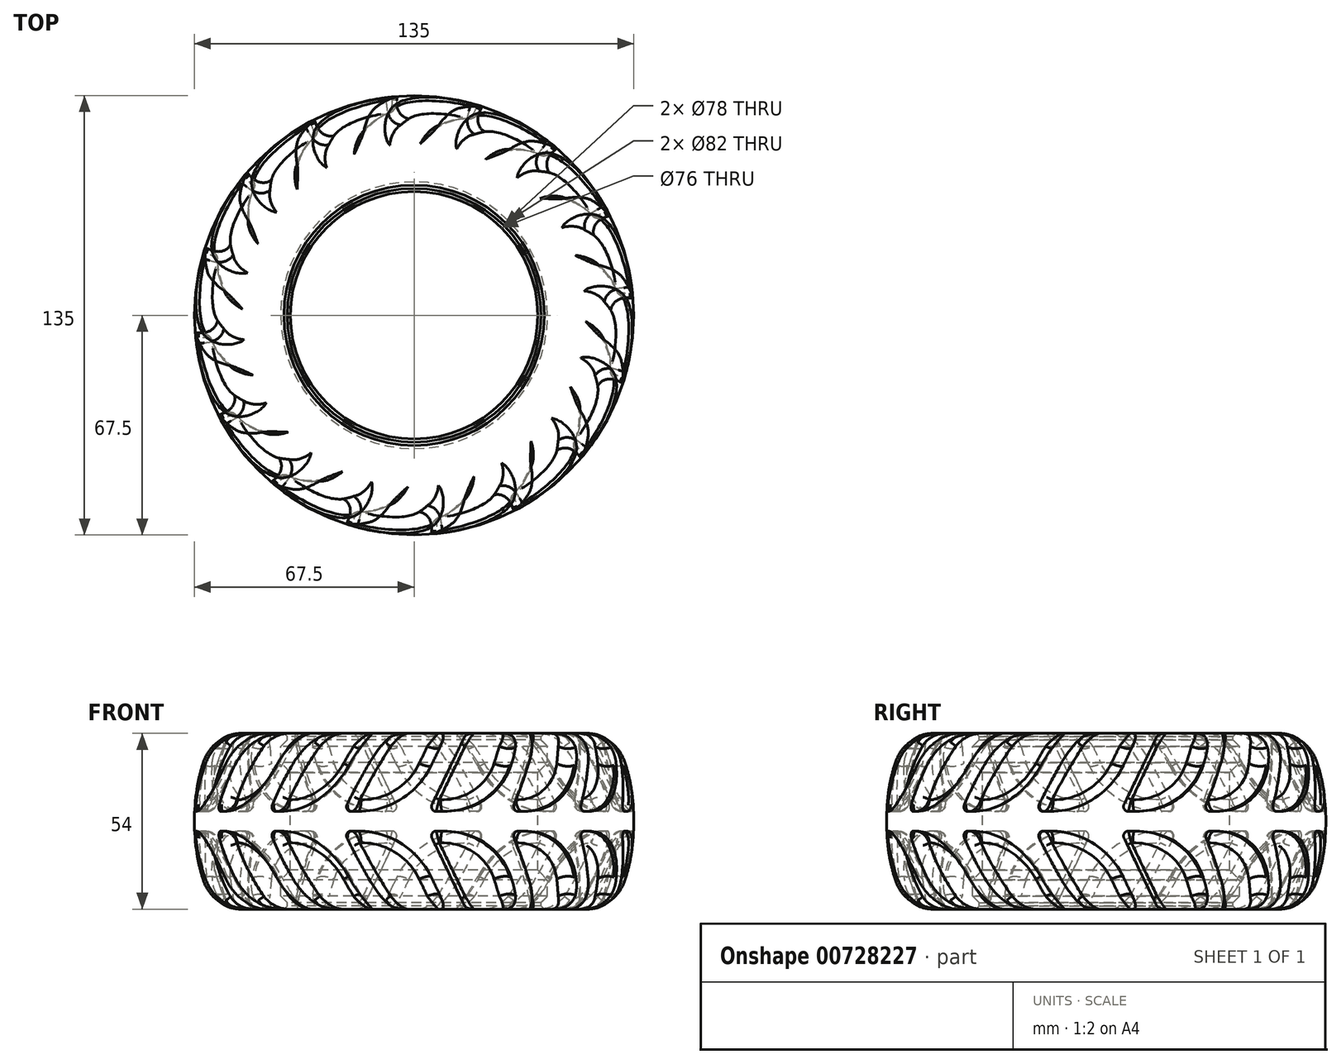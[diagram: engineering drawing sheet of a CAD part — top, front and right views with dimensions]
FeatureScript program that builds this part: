
annotation { "Feature Type Name" : "Feature", "Feature Type Description" : "" }
export const myFeature = defineFeature(function(context is Context, id is Id, definition is map)
    precondition{}
    {
        {
            var Q0;
            Q0=qCreatedBy(makeId("Front.planeOp"),FACE);
            var sketch = newSketch(context, id + "F0", { "sketchPlane" : qUnion([Q0])});
            skLineSegment(sketch, "E0", {"start": v(-39, 25) * mm, "end": v(-39, 27) * mm});
            skLineSegment(sketch, "E1", {"start": v(-39, 25) * mm, "end": v(-41, 23) * mm});
            skLineSegment(sketch, "E2", {"start": v(-41, 23) * mm, "end": v(-41, 18) * mm});
            skLineSegment(sketch, "E3", {"start": v(-41, 18) * mm, "end": v(-38, 15) * mm});
            skLineSegment(sketch, "E4", {"start": v(-38, -15) * mm, "end": v(-41, -18) * mm});
            skLineSegment(sketch, "E5", {"start": v(-41, -18) * mm, "end": v(-41, -23) * mm});
            skLineSegment(sketch, "E6", {"start": v(-41, -23) * mm, "end": v(-39, -25) * mm});
            skLineSegment(sketch, "E7", {"start": v(-39, -25) * mm, "end": v(-39, -27) * mm});
            skLineSegment(sketch, "E8", {"start": v(-38, 15) * mm, "end": v(-38, -15) * mm});
            skLineSegment(sketch, "E9", {"start": v(-38, 0) * mm, "end": v(-62.9, 0) * mm, "construction": true});
            skCircle(sketch, "E10", {"center": v(-52.82, 20.75) * mm, "radius": 6.25 * mm});
            skCircle(sketch, "E11", {"center": v(0, 0) * mm, "radius": 69 * mm});
            skCircle(sketch, "E12", {"center": v(-52.82, -20.75) * mm, "radius": 6.25 * mm});
            skCircle(sketch, "E13", {"center": v(0, 0) * mm, "radius": 63 * mm});
            skLineSegment(sketch, "E14", {"start": v(-39, 27) * mm, "end": v(-52.82, 27) * mm});
            skLineSegment(sketch, "E15", {"start": v(-39, -27) * mm, "end": v(-52.82, -27) * mm});
            skLineSegment(sketch, "E16", {"start": v(0, 89.19) * mm, "end": v(0, -93.9) * mm, "construction": true});
            skCircle(sketch, "E17", {"center": v(-52.82, 20.75) * mm, "radius": 12.25 * mm});
            skSolve(sketch);
        }
        {
            var Q0;
            Q0=makeQuery(id+"F0.imprint","IMPRINT",FACE,{"disambiguationData":[TD([[makeQuery(id+"F0.imprint","IMPRINT",EDGE,{"derivedFrom":sQuery(id+"F0.wireOp",EDGE,"E0")}),1.0]])]});
            var Q1;
            {var subQ0=sQuery(id+"F0.wireOp",EDGE,"E10");var subQ1=makeQuery(id+"F0.imprint","INTERSECT",VERTEX,{"derivedFrom":[subQ0,sQuery(id+"F0.wireOp",EDGE,"E14")]});Q1=makeQuery(id+"F0.imprint","IMPRINT",FACE,{"disambiguationData":[TD([[makeQuery(id+"F0.imprint","IMPRINT",EDGE,{"disambiguationData":[TD([[subQ1,-1.0]])],"derivedFrom":subQ0}),1.0]])]});}
            var Q2;
            {var subQ0=sQuery(id+"F0.wireOp",EDGE,"E12");var subQ1=makeQuery(id+"F0.imprint","INTERSECT",VERTEX,{"derivedFrom":[subQ0,sQuery(id+"F0.wireOp",EDGE,"E15")]});Q2=makeQuery(id+"F0.imprint","IMPRINT",FACE,{"disambiguationData":[TD([[makeQuery(id+"F0.imprint","IMPRINT",EDGE,{"disambiguationData":[TD([[subQ1,1.0]])],"derivedFrom":subQ0}),1.0]])]});}
            var Q3;
            {var subQ6=sQuery(id+"F0.wireOp",EDGE,"E2");Q3=makeQuery(id+"F0.imprint","IMPRINT",FACE,{"disambiguationData":[TD([[makeQuery(id+"F0.imprint","IMPRINT",EDGE,{"derivedFrom":subQ6}),-1.0]])]});}
            var Q4;
            Q4=makeQuery(id+"F0.imprint","IMPRINT",FACE,{"disambiguationData":[TD([[makeQuery(id+"F0.imprint","IMPRINT",EDGE,{"derivedFrom":sQuery(id+"F0.wireOp",EDGE,"E4")}),-1.0]])]});
            var Q5;
            Q5=sQuery(id+"F0.wireOp",EDGE,"E16");
            revolve(context, id + "F1", {"entities" : qUnion([Q0, Q1, Q2, Q3, Q4]), "axis" : qUnion([Q5]), "revolveType" : RevolveType.FULL});
        }
        {
            var Q0;
            Q0=qCreatedBy(makeId("Top.planeOp"),FACE);
            cPlane(context, id + "F2", {"entities" : qUnion([Q0]), "cplaneType" : CPlaneType.OFFSET, "offset" : 27 * mm, "width" : 150 * mm, "height" : 150 * mm});
        }
        {
            var Q0;
            Q0=qCreatedBy(makeId("Top.planeOp"),FACE);
            var sketch = newSketch(context, id + "F3", { "sketchPlane" : qUnion([Q0])});
            skLineSegment(sketch, "E18.bottom", {"start": v(-3, 60) * mm, "end": v(3, 60) * mm});
            skLineSegment(sketch, "E18.top", {"start": v(-3, 70) * mm, "end": v(3, 70) * mm});
            skLineSegment(sketch, "E18.left", {"start": v(-3, 60) * mm, "end": v(-3, 70) * mm});
            skLineSegment(sketch, "E18.right", {"start": v(3, 60) * mm, "end": v(3, 70) * mm});
            skLineSegment(sketch, "E19", {"start": v(0, 113.7) * mm, "end": v(0, -99.56) * mm, "construction": true});
            skLineSegment(sketch, "E20.1.0", {"start": v(-25.73, 54.28) * mm, "end": v(-29.56, 63.52) * mm});
            skLineSegment(sketch, "E20.1.1", {"start": v(-29.56, 63.52) * mm, "end": v(-24.02, 65.82) * mm});
            skLineSegment(sketch, "E20.1.2", {"start": v(-20.19, 56.58) * mm, "end": v(-24.02, 65.82) * mm});
            skLineSegment(sketch, "E20.1.3", {"start": v(-25.73, 54.28) * mm, "end": v(-20.19, 56.58) * mm});
            skLineSegment(sketch, "E20.2.0", {"start": v(-44.55, 40.3) * mm, "end": v(-51.62, 47.38) * mm});
            skLineSegment(sketch, "E20.2.1", {"start": v(-51.62, 47.38) * mm, "end": v(-47.38, 51.62) * mm});
            skLineSegment(sketch, "E20.2.2", {"start": v(-40.3, 44.55) * mm, "end": v(-47.38, 51.62) * mm});
            skLineSegment(sketch, "E20.2.3", {"start": v(-44.55, 40.3) * mm, "end": v(-40.3, 44.55) * mm});
            skLineSegment(sketch, "E20.3.0", {"start": v(-56.58, 20.19) * mm, "end": v(-65.82, 24.02) * mm});
            skLineSegment(sketch, "E20.3.1", {"start": v(-65.82, 24.02) * mm, "end": v(-63.52, 29.56) * mm});
            skLineSegment(sketch, "E20.3.2", {"start": v(-54.28, 25.73) * mm, "end": v(-63.52, 29.56) * mm});
            skLineSegment(sketch, "E20.3.3", {"start": v(-56.58, 20.19) * mm, "end": v(-54.28, 25.73) * mm});
            skLineSegment(sketch, "E20.4.0", {"start": v(-60, -3) * mm, "end": v(-70, -3) * mm});
            skLineSegment(sketch, "E20.4.1", {"start": v(-70, -3) * mm, "end": v(-70, 3) * mm});
            skLineSegment(sketch, "E20.4.2", {"start": v(-60, 3) * mm, "end": v(-70, 3) * mm});
            skLineSegment(sketch, "E20.4.3", {"start": v(-60, -3) * mm, "end": v(-60, 3) * mm});
            skLineSegment(sketch, "E20.5.0", {"start": v(-54.28, -25.73) * mm, "end": v(-63.52, -29.56) * mm});
            skLineSegment(sketch, "E20.5.1", {"start": v(-63.52, -29.56) * mm, "end": v(-65.82, -24.02) * mm});
            skLineSegment(sketch, "E20.5.2", {"start": v(-56.58, -20.19) * mm, "end": v(-65.82, -24.02) * mm});
            skLineSegment(sketch, "E20.5.3", {"start": v(-54.28, -25.73) * mm, "end": v(-56.58, -20.19) * mm});
            skLineSegment(sketch, "E20.6.0", {"start": v(-40.3, -44.55) * mm, "end": v(-47.38, -51.62) * mm});
            skLineSegment(sketch, "E20.6.1", {"start": v(-47.38, -51.62) * mm, "end": v(-51.62, -47.38) * mm});
            skLineSegment(sketch, "E20.6.2", {"start": v(-44.55, -40.3) * mm, "end": v(-51.62, -47.38) * mm});
            skLineSegment(sketch, "E20.6.3", {"start": v(-40.3, -44.55) * mm, "end": v(-44.55, -40.3) * mm});
            skLineSegment(sketch, "E20.7.0", {"start": v(-20.19, -56.58) * mm, "end": v(-24.02, -65.82) * mm});
            skLineSegment(sketch, "E20.7.1", {"start": v(-24.02, -65.82) * mm, "end": v(-29.56, -63.52) * mm});
            skLineSegment(sketch, "E20.7.2", {"start": v(-25.73, -54.28) * mm, "end": v(-29.56, -63.52) * mm});
            skLineSegment(sketch, "E20.7.3", {"start": v(-20.19, -56.58) * mm, "end": v(-25.73, -54.28) * mm});
            skLineSegment(sketch, "E20.8.0", {"start": v(3, -60) * mm, "end": v(3, -70) * mm});
            skLineSegment(sketch, "E20.8.1", {"start": v(3, -70) * mm, "end": v(-3, -70) * mm});
            skLineSegment(sketch, "E20.8.2", {"start": v(-3, -60) * mm, "end": v(-3, -70) * mm});
            skLineSegment(sketch, "E20.8.3", {"start": v(3, -60) * mm, "end": v(-3, -60) * mm});
            skLineSegment(sketch, "E20.9.0", {"start": v(25.73, -54.28) * mm, "end": v(29.56, -63.52) * mm});
            skLineSegment(sketch, "E20.9.1", {"start": v(29.56, -63.52) * mm, "end": v(24.02, -65.82) * mm});
            skLineSegment(sketch, "E20.9.2", {"start": v(20.19, -56.58) * mm, "end": v(24.02, -65.82) * mm});
            skLineSegment(sketch, "E20.9.3", {"start": v(25.73, -54.28) * mm, "end": v(20.19, -56.58) * mm});
            skLineSegment(sketch, "E20.10.0", {"start": v(44.55, -40.3) * mm, "end": v(51.62, -47.38) * mm});
            skLineSegment(sketch, "E20.10.1", {"start": v(51.62, -47.38) * mm, "end": v(47.38, -51.62) * mm});
            skLineSegment(sketch, "E20.10.2", {"start": v(40.3, -44.55) * mm, "end": v(47.38, -51.62) * mm});
            skLineSegment(sketch, "E20.10.3", {"start": v(44.55, -40.3) * mm, "end": v(40.3, -44.55) * mm});
            skLineSegment(sketch, "E20.11.0", {"start": v(56.58, -20.19) * mm, "end": v(65.82, -24.02) * mm});
            skLineSegment(sketch, "E20.11.1", {"start": v(65.82, -24.02) * mm, "end": v(63.52, -29.56) * mm});
            skLineSegment(sketch, "E20.11.2", {"start": v(54.28, -25.73) * mm, "end": v(63.52, -29.56) * mm});
            skLineSegment(sketch, "E20.11.3", {"start": v(56.58, -20.19) * mm, "end": v(54.28, -25.73) * mm});
            skLineSegment(sketch, "E20.12.0", {"start": v(60, 3) * mm, "end": v(70, 3) * mm});
            skLineSegment(sketch, "E20.12.1", {"start": v(70, 3) * mm, "end": v(70, -3) * mm});
            skLineSegment(sketch, "E20.12.2", {"start": v(60, -3) * mm, "end": v(70, -3) * mm});
            skLineSegment(sketch, "E20.12.3", {"start": v(60, 3) * mm, "end": v(60, -3) * mm});
            skLineSegment(sketch, "E20.13.0", {"start": v(54.28, 25.73) * mm, "end": v(63.52, 29.56) * mm});
            skLineSegment(sketch, "E20.13.1", {"start": v(63.52, 29.56) * mm, "end": v(65.82, 24.02) * mm});
            skLineSegment(sketch, "E20.13.2", {"start": v(56.58, 20.19) * mm, "end": v(65.82, 24.02) * mm});
            skLineSegment(sketch, "E20.13.3", {"start": v(54.28, 25.73) * mm, "end": v(56.58, 20.19) * mm});
            skLineSegment(sketch, "E20.14.0", {"start": v(40.3, 44.55) * mm, "end": v(47.38, 51.62) * mm});
            skLineSegment(sketch, "E20.14.1", {"start": v(47.38, 51.62) * mm, "end": v(51.62, 47.38) * mm});
            skLineSegment(sketch, "E20.14.2", {"start": v(44.55, 40.3) * mm, "end": v(51.62, 47.38) * mm});
            skLineSegment(sketch, "E20.14.3", {"start": v(40.3, 44.55) * mm, "end": v(44.55, 40.3) * mm});
            skLineSegment(sketch, "E20.15.0", {"start": v(20.19, 56.58) * mm, "end": v(24.02, 65.82) * mm});
            skLineSegment(sketch, "E20.15.1", {"start": v(24.02, 65.82) * mm, "end": v(29.56, 63.52) * mm});
            skLineSegment(sketch, "E20.15.2", {"start": v(25.73, 54.28) * mm, "end": v(29.56, 63.52) * mm});
            skLineSegment(sketch, "E20.15.3", {"start": v(20.19, 56.58) * mm, "end": v(25.73, 54.28) * mm});
            skPoint(sketch, "E20.center", {"position": v(0, 0) * mm});
            skSolve(sketch);
        }
        {
            var Q0;
            Q0=qCreatedBy(id+"F2.planeOp",FACE);
            var sketch = newSketch(context, id + "F4", { "sketchPlane" : qUnion([Q0])});
            skLineSegment(sketch, "E21", {"start": v(-16, 70) * mm, "end": v(-16, 50) * mm});
            skLineSegment(sketch, "E22", {"start": v(-16, 50) * mm, "end": v(-10, 50) * mm});
            skLineSegment(sketch, "E23", {"start": v(-16, 70) * mm, "end": v(-10, 70) * mm});
            skLineSegment(sketch, "E24", {"start": v(-10, 70) * mm, "end": v(-10, 50) * mm});
            skLineSegment(sketch, "E25", {"start": v(0, 99.7) * mm, "end": v(0, -107.8) * mm, "construction": true});
            skLineSegment(sketch, "E26.1.0", {"start": v(-41.57, 58.55) * mm, "end": v(-33.92, 40.07) * mm});
            skLineSegment(sketch, "E26.1.1", {"start": v(-36.03, 60.84) * mm, "end": v(-28.37, 42.37) * mm});
            skLineSegment(sketch, "E26.1.2", {"start": v(-33.92, 40.07) * mm, "end": v(-28.37, 42.37) * mm});
            skLineSegment(sketch, "E26.1.3", {"start": v(-41.57, 58.55) * mm, "end": v(-36.03, 60.84) * mm});
            skLineSegment(sketch, "E26.2.0", {"start": v(-60.81, 38.18) * mm, "end": v(-46.67, 24.04) * mm});
            skLineSegment(sketch, "E26.2.1", {"start": v(-56.57, 42.43) * mm, "end": v(-42.43, 28.28) * mm});
            skLineSegment(sketch, "E26.2.2", {"start": v(-46.67, 24.04) * mm, "end": v(-42.43, 28.28) * mm});
            skLineSegment(sketch, "E26.2.3", {"start": v(-60.81, 38.18) * mm, "end": v(-56.57, 42.43) * mm});
            skLineSegment(sketch, "E26.3.0", {"start": v(-70.8, 12) * mm, "end": v(-52.32, 4.35) * mm});
            skLineSegment(sketch, "E26.3.1", {"start": v(-68.5, 17.55) * mm, "end": v(-50.02, 9.9) * mm});
            skLineSegment(sketch, "E26.3.2", {"start": v(-52.32, 4.35) * mm, "end": v(-50.02, 9.9) * mm});
            skLineSegment(sketch, "E26.3.3", {"start": v(-70.8, 12) * mm, "end": v(-68.5, 17.55) * mm});
            skLineSegment(sketch, "E26.4.0", {"start": v(-70, -16) * mm, "end": v(-50, -16) * mm});
            skLineSegment(sketch, "E26.4.1", {"start": v(-70, -10) * mm, "end": v(-50, -10) * mm});
            skLineSegment(sketch, "E26.4.2", {"start": v(-50, -16) * mm, "end": v(-50, -10) * mm});
            skLineSegment(sketch, "E26.4.3", {"start": v(-70, -16) * mm, "end": v(-70, -10) * mm});
            skLineSegment(sketch, "E26.5.0", {"start": v(-58.55, -41.57) * mm, "end": v(-40.07, -33.92) * mm});
            skLineSegment(sketch, "E26.5.1", {"start": v(-60.84, -36.03) * mm, "end": v(-42.37, -28.37) * mm});
            skLineSegment(sketch, "E26.5.2", {"start": v(-40.07, -33.92) * mm, "end": v(-42.37, -28.37) * mm});
            skLineSegment(sketch, "E26.5.3", {"start": v(-58.55, -41.57) * mm, "end": v(-60.84, -36.03) * mm});
            skLineSegment(sketch, "E26.6.0", {"start": v(-38.18, -60.81) * mm, "end": v(-24.04, -46.67) * mm});
            skLineSegment(sketch, "E26.6.1", {"start": v(-42.43, -56.57) * mm, "end": v(-28.28, -42.43) * mm});
            skLineSegment(sketch, "E26.6.2", {"start": v(-24.04, -46.67) * mm, "end": v(-28.28, -42.43) * mm});
            skLineSegment(sketch, "E26.6.3", {"start": v(-38.18, -60.81) * mm, "end": v(-42.43, -56.57) * mm});
            skLineSegment(sketch, "E26.7.0", {"start": v(-12, -70.8) * mm, "end": v(-4.35, -52.32) * mm});
            skLineSegment(sketch, "E26.7.1", {"start": v(-17.55, -68.5) * mm, "end": v(-9.9, -50.02) * mm});
            skLineSegment(sketch, "E26.7.2", {"start": v(-4.35, -52.32) * mm, "end": v(-9.9, -50.02) * mm});
            skLineSegment(sketch, "E26.7.3", {"start": v(-12, -70.8) * mm, "end": v(-17.55, -68.5) * mm});
            skLineSegment(sketch, "E26.8.0", {"start": v(16, -70) * mm, "end": v(16, -50) * mm});
            skLineSegment(sketch, "E26.8.1", {"start": v(10, -70) * mm, "end": v(10, -50) * mm});
            skLineSegment(sketch, "E26.8.2", {"start": v(16, -50) * mm, "end": v(10, -50) * mm});
            skLineSegment(sketch, "E26.8.3", {"start": v(16, -70) * mm, "end": v(10, -70) * mm});
            skLineSegment(sketch, "E26.9.0", {"start": v(41.57, -58.55) * mm, "end": v(33.92, -40.07) * mm});
            skLineSegment(sketch, "E26.9.1", {"start": v(36.03, -60.84) * mm, "end": v(28.37, -42.37) * mm});
            skLineSegment(sketch, "E26.9.2", {"start": v(33.92, -40.07) * mm, "end": v(28.37, -42.37) * mm});
            skLineSegment(sketch, "E26.9.3", {"start": v(41.57, -58.55) * mm, "end": v(36.03, -60.84) * mm});
            skLineSegment(sketch, "E26.10.0", {"start": v(60.81, -38.18) * mm, "end": v(46.67, -24.04) * mm});
            skLineSegment(sketch, "E26.10.1", {"start": v(56.57, -42.43) * mm, "end": v(42.43, -28.28) * mm});
            skLineSegment(sketch, "E26.10.2", {"start": v(46.67, -24.04) * mm, "end": v(42.43, -28.28) * mm});
            skLineSegment(sketch, "E26.10.3", {"start": v(60.81, -38.18) * mm, "end": v(56.57, -42.43) * mm});
            skLineSegment(sketch, "E26.11.0", {"start": v(70.8, -12) * mm, "end": v(52.32, -4.35) * mm});
            skLineSegment(sketch, "E26.11.1", {"start": v(68.5, -17.55) * mm, "end": v(50.02, -9.9) * mm});
            skLineSegment(sketch, "E26.11.2", {"start": v(52.32, -4.35) * mm, "end": v(50.02, -9.9) * mm});
            skLineSegment(sketch, "E26.11.3", {"start": v(70.8, -12) * mm, "end": v(68.5, -17.55) * mm});
            skLineSegment(sketch, "E26.12.0", {"start": v(70, 16) * mm, "end": v(50, 16) * mm});
            skLineSegment(sketch, "E26.12.1", {"start": v(70, 10) * mm, "end": v(50, 10) * mm});
            skLineSegment(sketch, "E26.12.2", {"start": v(50, 16) * mm, "end": v(50, 10) * mm});
            skLineSegment(sketch, "E26.12.3", {"start": v(70, 16) * mm, "end": v(70, 10) * mm});
            skLineSegment(sketch, "E26.13.0", {"start": v(58.55, 41.57) * mm, "end": v(40.07, 33.92) * mm});
            skLineSegment(sketch, "E26.13.1", {"start": v(60.84, 36.03) * mm, "end": v(42.37, 28.37) * mm});
            skLineSegment(sketch, "E26.13.2", {"start": v(40.07, 33.92) * mm, "end": v(42.37, 28.37) * mm});
            skLineSegment(sketch, "E26.13.3", {"start": v(58.55, 41.57) * mm, "end": v(60.84, 36.03) * mm});
            skLineSegment(sketch, "E26.14.0", {"start": v(38.18, 60.81) * mm, "end": v(24.04, 46.67) * mm});
            skLineSegment(sketch, "E26.14.1", {"start": v(42.43, 56.57) * mm, "end": v(28.28, 42.43) * mm});
            skLineSegment(sketch, "E26.14.2", {"start": v(24.04, 46.67) * mm, "end": v(28.28, 42.43) * mm});
            skLineSegment(sketch, "E26.14.3", {"start": v(38.18, 60.81) * mm, "end": v(42.43, 56.57) * mm});
            skLineSegment(sketch, "E26.15.0", {"start": v(12, 70.8) * mm, "end": v(4.35, 52.32) * mm});
            skLineSegment(sketch, "E26.15.1", {"start": v(17.55, 68.5) * mm, "end": v(9.9, 50.02) * mm});
            skLineSegment(sketch, "E26.15.2", {"start": v(4.35, 52.32) * mm, "end": v(9.9, 50.02) * mm});
            skLineSegment(sketch, "E26.15.3", {"start": v(12, 70.8) * mm, "end": v(17.55, 68.5) * mm});
            skPoint(sketch, "E26.center", {"position": v(0, 0) * mm});
            skSolve(sketch);
        }
        {
            var Q1;
            Q1=makeQuery(id+"F3.imprint","IMPRINT",FACE,{"disambiguationData":[TD([[makeQuery(id+"F3.imprint","IMPRINT",EDGE,{"derivedFrom":sQuery(id+"F3.wireOp",EDGE,"E18.bottom")}),1.0]])]});
            var Q2;
            Q2=makeQuery(id+"F4.imprint","IMPRINT",FACE,{"disambiguationData":[TD([[makeQuery(id+"F4.imprint","IMPRINT",EDGE,{"derivedFrom":sQuery(id+"F4.wireOp",EDGE,"E21")}),1.0]])]});
            loft(context, id + "F5", {"operationType" : NewBodyOperationType.ADD, "sheetProfilesArray" : [{ "sheetProfileEntities" : qUnion([Q1]) }, { "sheetProfileEntities" : qUnion([Q2]) }]});
        }
        {
            var Q1;
            Q1=makeQuery(id+"F3.imprint","IMPRINT",FACE,{"disambiguationData":[TD([[makeQuery(id+"F3.imprint","IMPRINT",EDGE,{"derivedFrom":sQuery(id+"F3.wireOp",EDGE,"E20.15.0")}),-1.0]])]});
            var Q2;
            Q2=makeQuery(id+"F4.imprint","IMPRINT",FACE,{"disambiguationData":[TD([[makeQuery(id+"F4.imprint","IMPRINT",EDGE,{"derivedFrom":sQuery(id+"F4.wireOp",EDGE,"E26.15.0")}),1.0]])]});
            loft(context, id + "F6", {"operationType" : NewBodyOperationType.ADD, "sheetProfilesArray" : [{ "sheetProfileEntities" : qUnion([Q1]) }, { "sheetProfileEntities" : qUnion([Q2]) }]});
        }
        {
            var Q1;
            Q1=makeQuery(id+"F3.imprint","IMPRINT",FACE,{"disambiguationData":[TD([[makeQuery(id+"F3.imprint","IMPRINT",EDGE,{"derivedFrom":sQuery(id+"F3.wireOp",EDGE,"E20.14.0")}),-1.0]])]});
            var Q2;
            Q2=makeQuery(id+"F4.imprint","IMPRINT",FACE,{"disambiguationData":[TD([[makeQuery(id+"F4.imprint","IMPRINT",EDGE,{"derivedFrom":sQuery(id+"F4.wireOp",EDGE,"E26.14.0")}),1.0]])]});
            loft(context, id + "F7", {"operationType" : NewBodyOperationType.ADD, "sheetProfilesArray" : [{ "sheetProfileEntities" : qUnion([Q1]) }, { "sheetProfileEntities" : qUnion([Q2]) }]});
        }
        {
            var Q1;
            Q1=makeQuery(id+"F3.imprint","IMPRINT",FACE,{"disambiguationData":[TD([[makeQuery(id+"F3.imprint","IMPRINT",EDGE,{"derivedFrom":sQuery(id+"F3.wireOp",EDGE,"E20.13.0")}),-1.0]])]});
            var Q2;
            Q2=makeQuery(id+"F4.imprint","IMPRINT",FACE,{"disambiguationData":[TD([[makeQuery(id+"F4.imprint","IMPRINT",EDGE,{"derivedFrom":sQuery(id+"F4.wireOp",EDGE,"E26.13.0")}),1.0]])]});
            loft(context, id + "F8", {"operationType" : NewBodyOperationType.ADD, "sheetProfilesArray" : [{ "sheetProfileEntities" : qUnion([Q1]) }, { "sheetProfileEntities" : qUnion([Q2]) }]});
        }
        {
            var Q1;
            Q1=makeQuery(id+"F3.imprint","IMPRINT",FACE,{"disambiguationData":[TD([[makeQuery(id+"F3.imprint","IMPRINT",EDGE,{"derivedFrom":sQuery(id+"F3.wireOp",EDGE,"E20.12.0")}),-1.0]])]});
            var Q2;
            Q2=makeQuery(id+"F4.imprint","IMPRINT",FACE,{"disambiguationData":[TD([[makeQuery(id+"F4.imprint","IMPRINT",EDGE,{"derivedFrom":sQuery(id+"F4.wireOp",EDGE,"E26.12.0")}),1.0]])]});
            loft(context, id + "F9", {"operationType" : NewBodyOperationType.ADD, "sheetProfilesArray" : [{ "sheetProfileEntities" : qUnion([Q1]) }, { "sheetProfileEntities" : qUnion([Q2]) }]});
        }
        {
            var Q1;
            Q1=makeQuery(id+"F3.imprint","IMPRINT",FACE,{"disambiguationData":[TD([[makeQuery(id+"F3.imprint","IMPRINT",EDGE,{"derivedFrom":sQuery(id+"F3.wireOp",EDGE,"E20.11.0")}),-1.0]])]});
            var Q2;
            Q2=makeQuery(id+"F4.imprint","IMPRINT",FACE,{"disambiguationData":[TD([[makeQuery(id+"F4.imprint","IMPRINT",EDGE,{"derivedFrom":sQuery(id+"F4.wireOp",EDGE,"E26.11.0")}),1.0]])]});
            loft(context, id + "F10", {"operationType" : NewBodyOperationType.ADD, "sheetProfilesArray" : [{ "sheetProfileEntities" : qUnion([Q1]) }, { "sheetProfileEntities" : qUnion([Q2]) }]});
        }
        {
            var Q1;
            Q1=makeQuery(id+"F3.imprint","IMPRINT",FACE,{"disambiguationData":[TD([[makeQuery(id+"F3.imprint","IMPRINT",EDGE,{"derivedFrom":sQuery(id+"F3.wireOp",EDGE,"E20.10.0")}),-1.0]])]});
            var Q2;
            Q2=makeQuery(id+"F4.imprint","IMPRINT",FACE,{"disambiguationData":[TD([[makeQuery(id+"F4.imprint","IMPRINT",EDGE,{"derivedFrom":sQuery(id+"F4.wireOp",EDGE,"E26.10.0")}),1.0]])]});
            loft(context, id + "F11", {"operationType" : NewBodyOperationType.ADD, "sheetProfilesArray" : [{ "sheetProfileEntities" : qUnion([Q1]) }, { "sheetProfileEntities" : qUnion([Q2]) }]});
        }
        {
            var Q1;
            Q1=makeQuery(id+"F3.imprint","IMPRINT",FACE,{"disambiguationData":[TD([[makeQuery(id+"F3.imprint","IMPRINT",EDGE,{"derivedFrom":sQuery(id+"F3.wireOp",EDGE,"E20.9.0")}),-1.0]])]});
            var Q2;
            Q2=makeQuery(id+"F4.imprint","IMPRINT",FACE,{"disambiguationData":[TD([[makeQuery(id+"F4.imprint","IMPRINT",EDGE,{"derivedFrom":sQuery(id+"F4.wireOp",EDGE,"E26.9.0")}),1.0]])]});
            loft(context, id + "F12", {"operationType" : NewBodyOperationType.ADD, "sheetProfilesArray" : [{ "sheetProfileEntities" : qUnion([Q1]) }, { "sheetProfileEntities" : qUnion([Q2]) }]});
        }
        {
            var Q1;
            Q1=makeQuery(id+"F3.imprint","IMPRINT",FACE,{"disambiguationData":[TD([[makeQuery(id+"F3.imprint","IMPRINT",EDGE,{"derivedFrom":sQuery(id+"F3.wireOp",EDGE,"E20.8.0")}),-1.0]])]});
            var Q2;
            Q2=makeQuery(id+"F4.imprint","IMPRINT",FACE,{"disambiguationData":[TD([[makeQuery(id+"F4.imprint","IMPRINT",EDGE,{"derivedFrom":sQuery(id+"F4.wireOp",EDGE,"E26.8.0")}),1.0]])]});
            loft(context, id + "F13", {"operationType" : NewBodyOperationType.ADD, "sheetProfilesArray" : [{ "sheetProfileEntities" : qUnion([Q1]) }, { "sheetProfileEntities" : qUnion([Q2]) }]});
        }
        {
            var Q1;
            Q1=makeQuery(id+"F3.imprint","IMPRINT",FACE,{"disambiguationData":[TD([[makeQuery(id+"F3.imprint","IMPRINT",EDGE,{"derivedFrom":sQuery(id+"F3.wireOp",EDGE,"E20.7.0")}),-1.0]])]});
            var Q2;
            Q2=makeQuery(id+"F4.imprint","IMPRINT",FACE,{"disambiguationData":[TD([[makeQuery(id+"F4.imprint","IMPRINT",EDGE,{"derivedFrom":sQuery(id+"F4.wireOp",EDGE,"E26.7.0")}),1.0]])]});
            loft(context, id + "F14", {"operationType" : NewBodyOperationType.ADD, "sheetProfilesArray" : [{ "sheetProfileEntities" : qUnion([Q1]) }, { "sheetProfileEntities" : qUnion([Q2]) }]});
        }
        {
            var Q1;
            Q1=makeQuery(id+"F3.imprint","IMPRINT",FACE,{"disambiguationData":[TD([[makeQuery(id+"F3.imprint","IMPRINT",EDGE,{"derivedFrom":sQuery(id+"F3.wireOp",EDGE,"E20.6.0")}),-1.0]])]});
            var Q2;
            Q2=makeQuery(id+"F4.imprint","IMPRINT",FACE,{"disambiguationData":[TD([[makeQuery(id+"F4.imprint","IMPRINT",EDGE,{"derivedFrom":sQuery(id+"F4.wireOp",EDGE,"E26.6.0")}),1.0]])]});
            loft(context, id + "F15", {"operationType" : NewBodyOperationType.ADD, "sheetProfilesArray" : [{ "sheetProfileEntities" : qUnion([Q1]) }, { "sheetProfileEntities" : qUnion([Q2]) }]});
        }
        {
            var Q1;
            Q1=makeQuery(id+"F3.imprint","IMPRINT",FACE,{"disambiguationData":[TD([[makeQuery(id+"F3.imprint","IMPRINT",EDGE,{"derivedFrom":sQuery(id+"F3.wireOp",EDGE,"E20.5.0")}),-1.0]])]});
            var Q2;
            Q2=makeQuery(id+"F4.imprint","IMPRINT",FACE,{"disambiguationData":[TD([[makeQuery(id+"F4.imprint","IMPRINT",EDGE,{"derivedFrom":sQuery(id+"F4.wireOp",EDGE,"E26.5.0")}),1.0]])]});
            loft(context, id + "F16", {"operationType" : NewBodyOperationType.ADD, "sheetProfilesArray" : [{ "sheetProfileEntities" : qUnion([Q1]) }, { "sheetProfileEntities" : qUnion([Q2]) }]});
        }
        {
            var Q1;
            Q1=makeQuery(id+"F4.imprint","IMPRINT",FACE,{"disambiguationData":[TD([[makeQuery(id+"F4.imprint","IMPRINT",EDGE,{"derivedFrom":sQuery(id+"F4.wireOp",EDGE,"E26.4.0")}),1.0]])]});
            var Q2;
            Q2=makeQuery(id+"F3.imprint","IMPRINT",FACE,{"disambiguationData":[TD([[makeQuery(id+"F3.imprint","IMPRINT",EDGE,{"derivedFrom":sQuery(id+"F3.wireOp",EDGE,"E20.4.0")}),-1.0]])]});
            loft(context, id + "F17", {"operationType" : NewBodyOperationType.ADD, "sheetProfilesArray" : [{ "sheetProfileEntities" : qUnion([Q1]) }, { "sheetProfileEntities" : qUnion([Q2]) }]});
        }
        {
            var Q1;
            Q1=makeQuery(id+"F3.imprint","IMPRINT",FACE,{"disambiguationData":[TD([[makeQuery(id+"F3.imprint","IMPRINT",EDGE,{"derivedFrom":sQuery(id+"F3.wireOp",EDGE,"E20.3.0")}),-1.0]])]});
            var Q2;
            Q2=makeQuery(id+"F4.imprint","IMPRINT",FACE,{"disambiguationData":[TD([[makeQuery(id+"F4.imprint","IMPRINT",EDGE,{"derivedFrom":sQuery(id+"F4.wireOp",EDGE,"E26.3.0")}),1.0]])]});
            loft(context, id + "F18", {"operationType" : NewBodyOperationType.ADD, "sheetProfilesArray" : [{ "sheetProfileEntities" : qUnion([Q1]) }, { "sheetProfileEntities" : qUnion([Q2]) }]});
        }
        {
            var Q1;
            Q1=makeQuery(id+"F3.imprint","IMPRINT",FACE,{"disambiguationData":[TD([[makeQuery(id+"F3.imprint","IMPRINT",EDGE,{"derivedFrom":sQuery(id+"F3.wireOp",EDGE,"E20.2.0")}),-1.0]])]});
            var Q2;
            Q2=makeQuery(id+"F4.imprint","IMPRINT",FACE,{"disambiguationData":[TD([[makeQuery(id+"F4.imprint","IMPRINT",EDGE,{"derivedFrom":sQuery(id+"F4.wireOp",EDGE,"E26.2.0")}),1.0]])]});
            loft(context, id + "F19", {"operationType" : NewBodyOperationType.ADD, "sheetProfilesArray" : [{ "sheetProfileEntities" : qUnion([Q1]) }, { "sheetProfileEntities" : qUnion([Q2]) }]});
        }
        {
            var Q1;
            Q1=makeQuery(id+"F3.imprint","IMPRINT",FACE,{"disambiguationData":[TD([[makeQuery(id+"F3.imprint","IMPRINT",EDGE,{"derivedFrom":sQuery(id+"F3.wireOp",EDGE,"E20.1.0")}),-1.0]])]});
            var Q2;
            Q2=makeQuery(id+"F4.imprint","IMPRINT",FACE,{"disambiguationData":[TD([[makeQuery(id+"F4.imprint","IMPRINT",EDGE,{"derivedFrom":sQuery(id+"F4.wireOp",EDGE,"E26.1.0")}),1.0]])]});
            loft(context, id + "F20", {"operationType" : NewBodyOperationType.ADD, "sheetProfilesArray" : [{ "sheetProfileEntities" : qUnion([Q1]) }, { "sheetProfileEntities" : qUnion([Q2]) }]});
        }
        {
            var Q0;
            Q0=qCreatedBy(makeId("Top.planeOp"),FACE);
            cPlane(context, id + "F21", {"entities" : qUnion([Q0]), "cplaneType" : CPlaneType.OFFSET, "offset" : 27 * mm, "oppositeDirection" : true, "width" : 150 * mm, "height" : 150 * mm});
        }
        {
            var Q0;
            Q0=qCreatedBy(id+"F21.planeOp",FACE);
            var sketch = newSketch(context, id + "F22", { "sketchPlane" : qUnion([Q0])});
            skLineSegment(sketch, "E27.bottom", {"start": v(10, -70) * mm, "end": v(16, -70) * mm});
            skLineSegment(sketch, "E27.top", {"start": v(10, -50) * mm, "end": v(16, -50) * mm});
            skLineSegment(sketch, "E27.left", {"start": v(10, -70) * mm, "end": v(10, -50) * mm});
            skLineSegment(sketch, "E27.right", {"start": v(16, -70) * mm, "end": v(16, -50) * mm});
            skLineSegment(sketch, "E28.1.0", {"start": v(36.03, -60.84) * mm, "end": v(28.37, -42.37) * mm});
            skLineSegment(sketch, "E28.1.1", {"start": v(41.57, -58.55) * mm, "end": v(33.92, -40.07) * mm});
            skLineSegment(sketch, "E28.1.2", {"start": v(36.03, -60.84) * mm, "end": v(41.57, -58.55) * mm});
            skLineSegment(sketch, "E28.1.3", {"start": v(28.37, -42.37) * mm, "end": v(33.92, -40.07) * mm});
            skLineSegment(sketch, "E28.2.0", {"start": v(56.57, -42.43) * mm, "end": v(42.43, -28.28) * mm});
            skLineSegment(sketch, "E28.2.1", {"start": v(60.81, -38.18) * mm, "end": v(46.67, -24.04) * mm});
            skLineSegment(sketch, "E28.2.2", {"start": v(56.57, -42.43) * mm, "end": v(60.81, -38.18) * mm});
            skLineSegment(sketch, "E28.2.3", {"start": v(42.43, -28.28) * mm, "end": v(46.67, -24.04) * mm});
            skLineSegment(sketch, "E28.3.0", {"start": v(68.5, -17.55) * mm, "end": v(50.02, -9.9) * mm});
            skLineSegment(sketch, "E28.3.1", {"start": v(70.8, -12) * mm, "end": v(52.32, -4.35) * mm});
            skLineSegment(sketch, "E28.3.2", {"start": v(68.5, -17.55) * mm, "end": v(70.8, -12) * mm});
            skLineSegment(sketch, "E28.3.3", {"start": v(50.02, -9.9) * mm, "end": v(52.32, -4.35) * mm});
            skLineSegment(sketch, "E28.4.0", {"start": v(70, 10) * mm, "end": v(50, 10) * mm});
            skLineSegment(sketch, "E28.4.1", {"start": v(70, 16) * mm, "end": v(50, 16) * mm});
            skLineSegment(sketch, "E28.4.2", {"start": v(70, 10) * mm, "end": v(70, 16) * mm});
            skLineSegment(sketch, "E28.4.3", {"start": v(50, 10) * mm, "end": v(50, 16) * mm});
            skLineSegment(sketch, "E28.5.0", {"start": v(60.84, 36.03) * mm, "end": v(42.37, 28.37) * mm});
            skLineSegment(sketch, "E28.5.1", {"start": v(58.55, 41.57) * mm, "end": v(40.07, 33.92) * mm});
            skLineSegment(sketch, "E28.5.2", {"start": v(60.84, 36.03) * mm, "end": v(58.55, 41.57) * mm});
            skLineSegment(sketch, "E28.5.3", {"start": v(42.37, 28.37) * mm, "end": v(40.07, 33.92) * mm});
            skLineSegment(sketch, "E28.6.0", {"start": v(42.43, 56.57) * mm, "end": v(28.28, 42.43) * mm});
            skLineSegment(sketch, "E28.6.1", {"start": v(38.18, 60.81) * mm, "end": v(24.04, 46.67) * mm});
            skLineSegment(sketch, "E28.6.2", {"start": v(42.43, 56.57) * mm, "end": v(38.18, 60.81) * mm});
            skLineSegment(sketch, "E28.6.3", {"start": v(28.28, 42.43) * mm, "end": v(24.04, 46.67) * mm});
            skLineSegment(sketch, "E28.7.0", {"start": v(17.55, 68.5) * mm, "end": v(9.9, 50.02) * mm});
            skLineSegment(sketch, "E28.7.1", {"start": v(12, 70.8) * mm, "end": v(4.35, 52.32) * mm});
            skLineSegment(sketch, "E28.7.2", {"start": v(17.55, 68.5) * mm, "end": v(12, 70.8) * mm});
            skLineSegment(sketch, "E28.7.3", {"start": v(9.9, 50.02) * mm, "end": v(4.35, 52.32) * mm});
            skLineSegment(sketch, "E28.8.0", {"start": v(-10, 70) * mm, "end": v(-10, 50) * mm});
            skLineSegment(sketch, "E28.8.1", {"start": v(-16, 70) * mm, "end": v(-16, 50) * mm});
            skLineSegment(sketch, "E28.8.2", {"start": v(-10, 70) * mm, "end": v(-16, 70) * mm});
            skLineSegment(sketch, "E28.8.3", {"start": v(-10, 50) * mm, "end": v(-16, 50) * mm});
            skLineSegment(sketch, "E28.9.0", {"start": v(-36.03, 60.84) * mm, "end": v(-28.37, 42.37) * mm});
            skLineSegment(sketch, "E28.9.1", {"start": v(-41.57, 58.55) * mm, "end": v(-33.92, 40.07) * mm});
            skLineSegment(sketch, "E28.9.2", {"start": v(-36.03, 60.84) * mm, "end": v(-41.57, 58.55) * mm});
            skLineSegment(sketch, "E28.9.3", {"start": v(-28.37, 42.37) * mm, "end": v(-33.92, 40.07) * mm});
            skLineSegment(sketch, "E28.10.0", {"start": v(-56.57, 42.43) * mm, "end": v(-42.43, 28.28) * mm});
            skLineSegment(sketch, "E28.10.1", {"start": v(-60.81, 38.18) * mm, "end": v(-46.67, 24.04) * mm});
            skLineSegment(sketch, "E28.10.2", {"start": v(-56.57, 42.43) * mm, "end": v(-60.81, 38.18) * mm});
            skLineSegment(sketch, "E28.10.3", {"start": v(-42.43, 28.28) * mm, "end": v(-46.67, 24.04) * mm});
            skLineSegment(sketch, "E28.11.0", {"start": v(-68.5, 17.55) * mm, "end": v(-50.02, 9.9) * mm});
            skLineSegment(sketch, "E28.11.1", {"start": v(-70.8, 12) * mm, "end": v(-52.32, 4.35) * mm});
            skLineSegment(sketch, "E28.11.2", {"start": v(-68.5, 17.55) * mm, "end": v(-70.8, 12) * mm});
            skLineSegment(sketch, "E28.11.3", {"start": v(-50.02, 9.9) * mm, "end": v(-52.32, 4.35) * mm});
            skLineSegment(sketch, "E28.12.0", {"start": v(-70, -10) * mm, "end": v(-50, -10) * mm});
            skLineSegment(sketch, "E28.12.1", {"start": v(-70, -16) * mm, "end": v(-50, -16) * mm});
            skLineSegment(sketch, "E28.12.2", {"start": v(-70, -10) * mm, "end": v(-70, -16) * mm});
            skLineSegment(sketch, "E28.12.3", {"start": v(-50, -10) * mm, "end": v(-50, -16) * mm});
            skLineSegment(sketch, "E28.13.0", {"start": v(-60.84, -36.03) * mm, "end": v(-42.37, -28.37) * mm});
            skLineSegment(sketch, "E28.13.1", {"start": v(-58.55, -41.57) * mm, "end": v(-40.07, -33.92) * mm});
            skLineSegment(sketch, "E28.13.2", {"start": v(-60.84, -36.03) * mm, "end": v(-58.55, -41.57) * mm});
            skLineSegment(sketch, "E28.13.3", {"start": v(-42.37, -28.37) * mm, "end": v(-40.07, -33.92) * mm});
            skLineSegment(sketch, "E28.14.0", {"start": v(-42.43, -56.57) * mm, "end": v(-28.28, -42.43) * mm});
            skLineSegment(sketch, "E28.14.1", {"start": v(-38.18, -60.81) * mm, "end": v(-24.04, -46.67) * mm});
            skLineSegment(sketch, "E28.14.2", {"start": v(-42.43, -56.57) * mm, "end": v(-38.18, -60.81) * mm});
            skLineSegment(sketch, "E28.14.3", {"start": v(-28.28, -42.43) * mm, "end": v(-24.04, -46.67) * mm});
            skLineSegment(sketch, "E28.15.0", {"start": v(-17.55, -68.5) * mm, "end": v(-9.9, -50.02) * mm});
            skLineSegment(sketch, "E28.15.1", {"start": v(-12, -70.8) * mm, "end": v(-4.35, -52.32) * mm});
            skLineSegment(sketch, "E28.15.2", {"start": v(-17.55, -68.5) * mm, "end": v(-12, -70.8) * mm});
            skLineSegment(sketch, "E28.15.3", {"start": v(-9.9, -50.02) * mm, "end": v(-4.35, -52.32) * mm});
            skPoint(sketch, "E28.center", {"position": v(0, 0) * mm});
            skSolve(sketch);
        }
        {
            var Q1;
            Q1=makeQuery(id+"F22.imprint","IMPRINT",FACE,{"disambiguationData":[TD([[makeQuery(id+"F22.imprint","IMPRINT",EDGE,{"derivedFrom":sQuery(id+"F22.wireOp",EDGE,"E27.bottom")}),1.0]])]});
            var Q2;
            Q2=makeQuery(id+"F3.imprint","IMPRINT",FACE,{"disambiguationData":[TD([[makeQuery(id+"F3.imprint","IMPRINT",EDGE,{"derivedFrom":sQuery(id+"F3.wireOp",EDGE,"E20.8.0")}),-1.0]])]});
            loft(context, id + "F23", {"operationType" : NewBodyOperationType.ADD, "sheetProfilesArray" : [{ "sheetProfileEntities" : qUnion([Q1]) }, { "sheetProfileEntities" : qUnion([Q2]) }]});
        }
        {
            var Q1;
            Q1=makeQuery(id+"F22.imprint","IMPRINT",FACE,{"disambiguationData":[TD([[makeQuery(id+"F22.imprint","IMPRINT",EDGE,{"derivedFrom":sQuery(id+"F22.wireOp",EDGE,"E28.1.0")}),-1.0]])]});
            var Q2;
            Q2=makeQuery(id+"F3.imprint","IMPRINT",FACE,{"disambiguationData":[TD([[makeQuery(id+"F3.imprint","IMPRINT",EDGE,{"derivedFrom":sQuery(id+"F3.wireOp",EDGE,"E20.9.0")}),-1.0]])]});
            loft(context, id + "F24", {"operationType" : NewBodyOperationType.ADD, "sheetProfilesArray" : [{ "sheetProfileEntities" : qUnion([Q1]) }, { "sheetProfileEntities" : qUnion([Q2]) }]});
        }
        {
            var Q1;
            Q1=makeQuery(id+"F22.imprint","IMPRINT",FACE,{"disambiguationData":[TD([[makeQuery(id+"F22.imprint","IMPRINT",EDGE,{"derivedFrom":sQuery(id+"F22.wireOp",EDGE,"E28.2.0")}),-1.0]])]});
            var Q2;
            Q2=makeQuery(id+"F3.imprint","IMPRINT",FACE,{"disambiguationData":[TD([[makeQuery(id+"F3.imprint","IMPRINT",EDGE,{"derivedFrom":sQuery(id+"F3.wireOp",EDGE,"E20.10.0")}),-1.0]])]});
            loft(context, id + "F25", {"operationType" : NewBodyOperationType.ADD, "sheetProfilesArray" : [{ "sheetProfileEntities" : qUnion([Q1]) }, { "sheetProfileEntities" : qUnion([Q2]) }]});
        }
        {
            var Q1;
            Q1=makeQuery(id+"F22.imprint","IMPRINT",FACE,{"disambiguationData":[TD([[makeQuery(id+"F22.imprint","IMPRINT",EDGE,{"derivedFrom":sQuery(id+"F22.wireOp",EDGE,"E28.3.0")}),-1.0]])]});
            var Q2;
            Q2=makeQuery(id+"F3.imprint","IMPRINT",FACE,{"disambiguationData":[TD([[makeQuery(id+"F3.imprint","IMPRINT",EDGE,{"derivedFrom":sQuery(id+"F3.wireOp",EDGE,"E20.11.0")}),-1.0]])]});
            loft(context, id + "F26", {"operationType" : NewBodyOperationType.ADD, "sheetProfilesArray" : [{ "sheetProfileEntities" : qUnion([Q1]) }, { "sheetProfileEntities" : qUnion([Q2]) }]});
        }
        {
            var Q1;
            Q1=makeQuery(id+"F22.imprint","IMPRINT",FACE,{"disambiguationData":[TD([[makeQuery(id+"F22.imprint","IMPRINT",EDGE,{"derivedFrom":sQuery(id+"F22.wireOp",EDGE,"E28.4.0")}),-1.0]])]});
            var Q2;
            Q2=makeQuery(id+"F3.imprint","IMPRINT",FACE,{"disambiguationData":[TD([[makeQuery(id+"F3.imprint","IMPRINT",EDGE,{"derivedFrom":sQuery(id+"F3.wireOp",EDGE,"E20.12.0")}),-1.0]])]});
            loft(context, id + "F27", {"operationType" : NewBodyOperationType.ADD, "sheetProfilesArray" : [{ "sheetProfileEntities" : qUnion([Q1]) }, { "sheetProfileEntities" : qUnion([Q2]) }]});
        }
        {
            var Q1;
            Q1=makeQuery(id+"F22.imprint","IMPRINT",FACE,{"disambiguationData":[TD([[makeQuery(id+"F22.imprint","IMPRINT",EDGE,{"derivedFrom":sQuery(id+"F22.wireOp",EDGE,"E28.5.0")}),-1.0]])]});
            var Q2;
            Q2=makeQuery(id+"F3.imprint","IMPRINT",FACE,{"disambiguationData":[TD([[makeQuery(id+"F3.imprint","IMPRINT",EDGE,{"derivedFrom":sQuery(id+"F3.wireOp",EDGE,"E20.13.0")}),-1.0]])]});
            loft(context, id + "F28", {"operationType" : NewBodyOperationType.ADD, "sheetProfilesArray" : [{ "sheetProfileEntities" : qUnion([Q1]) }, { "sheetProfileEntities" : qUnion([Q2]) }]});
        }
        {
            var Q1;
            Q1=makeQuery(id+"F22.imprint","IMPRINT",FACE,{"disambiguationData":[TD([[makeQuery(id+"F22.imprint","IMPRINT",EDGE,{"derivedFrom":sQuery(id+"F22.wireOp",EDGE,"E28.6.0")}),-1.0]])]});
            var Q2;
            Q2=makeQuery(id+"F3.imprint","IMPRINT",FACE,{"disambiguationData":[TD([[makeQuery(id+"F3.imprint","IMPRINT",EDGE,{"derivedFrom":sQuery(id+"F3.wireOp",EDGE,"E20.14.0")}),-1.0]])]});
            loft(context, id + "F29", {"operationType" : NewBodyOperationType.ADD, "sheetProfilesArray" : [{ "sheetProfileEntities" : qUnion([Q1]) }, { "sheetProfileEntities" : qUnion([Q2]) }]});
        }
        {
            var Q1;
            Q1=makeQuery(id+"F22.imprint","IMPRINT",FACE,{"disambiguationData":[TD([[makeQuery(id+"F22.imprint","IMPRINT",EDGE,{"derivedFrom":sQuery(id+"F22.wireOp",EDGE,"E28.7.0")}),-1.0]])]});
            var Q2;
            Q2=makeQuery(id+"F3.imprint","IMPRINT",FACE,{"disambiguationData":[TD([[makeQuery(id+"F3.imprint","IMPRINT",EDGE,{"derivedFrom":sQuery(id+"F3.wireOp",EDGE,"E20.15.0")}),-1.0]])]});
            loft(context, id + "F30", {"operationType" : NewBodyOperationType.ADD, "sheetProfilesArray" : [{ "sheetProfileEntities" : qUnion([Q1]) }, { "sheetProfileEntities" : qUnion([Q2]) }]});
        }
        {
            var Q1;
            Q1=makeQuery(id+"F22.imprint","IMPRINT",FACE,{"disambiguationData":[TD([[makeQuery(id+"F22.imprint","IMPRINT",EDGE,{"derivedFrom":sQuery(id+"F22.wireOp",EDGE,"E28.8.0")}),-1.0]])]});
            var Q2;
            Q2=makeQuery(id+"F3.imprint","IMPRINT",FACE,{"disambiguationData":[TD([[makeQuery(id+"F3.imprint","IMPRINT",EDGE,{"derivedFrom":sQuery(id+"F3.wireOp",EDGE,"E18.bottom")}),1.0]])]});
            loft(context, id + "F31", {"operationType" : NewBodyOperationType.ADD, "sheetProfilesArray" : [{ "sheetProfileEntities" : qUnion([Q1]) }, { "sheetProfileEntities" : qUnion([Q2]) }]});
        }
        {
            var Q1;
            Q1=makeQuery(id+"F22.imprint","IMPRINT",FACE,{"disambiguationData":[TD([[makeQuery(id+"F22.imprint","IMPRINT",EDGE,{"derivedFrom":sQuery(id+"F22.wireOp",EDGE,"E28.9.0")}),-1.0]])]});
            var Q2;
            Q2=makeQuery(id+"F3.imprint","IMPRINT",FACE,{"disambiguationData":[TD([[makeQuery(id+"F3.imprint","IMPRINT",EDGE,{"derivedFrom":sQuery(id+"F3.wireOp",EDGE,"E20.1.0")}),-1.0]])]});
            loft(context, id + "F32", {"operationType" : NewBodyOperationType.ADD, "sheetProfilesArray" : [{ "sheetProfileEntities" : qUnion([Q1]) }, { "sheetProfileEntities" : qUnion([Q2]) }]});
        }
        {
            var Q1;
            Q1=makeQuery(id+"F22.imprint","IMPRINT",FACE,{"disambiguationData":[TD([[makeQuery(id+"F22.imprint","IMPRINT",EDGE,{"derivedFrom":sQuery(id+"F22.wireOp",EDGE,"E28.10.0")}),-1.0]])]});
            var Q2;
            Q2=makeQuery(id+"F3.imprint","IMPRINT",FACE,{"disambiguationData":[TD([[makeQuery(id+"F3.imprint","IMPRINT",EDGE,{"derivedFrom":sQuery(id+"F3.wireOp",EDGE,"E20.2.0")}),-1.0]])]});
            loft(context, id + "F33", {"operationType" : NewBodyOperationType.ADD, "sheetProfilesArray" : [{ "sheetProfileEntities" : qUnion([Q1]) }, { "sheetProfileEntities" : qUnion([Q2]) }]});
        }
        {
            var Q1;
            Q1=makeQuery(id+"F22.imprint","IMPRINT",FACE,{"disambiguationData":[TD([[makeQuery(id+"F22.imprint","IMPRINT",EDGE,{"derivedFrom":sQuery(id+"F22.wireOp",EDGE,"E28.11.0")}),-1.0]])]});
            var Q2;
            Q2=makeQuery(id+"F3.imprint","IMPRINT",FACE,{"disambiguationData":[TD([[makeQuery(id+"F3.imprint","IMPRINT",EDGE,{"derivedFrom":sQuery(id+"F3.wireOp",EDGE,"E20.3.0")}),-1.0]])]});
            loft(context, id + "F34", {"operationType" : NewBodyOperationType.ADD, "sheetProfilesArray" : [{ "sheetProfileEntities" : qUnion([Q1]) }, { "sheetProfileEntities" : qUnion([Q2]) }]});
        }
        {
            var Q1;
            Q1=makeQuery(id+"F22.imprint","IMPRINT",FACE,{"disambiguationData":[TD([[makeQuery(id+"F22.imprint","IMPRINT",EDGE,{"derivedFrom":sQuery(id+"F22.wireOp",EDGE,"E28.12.0")}),-1.0]])]});
            var Q2;
            Q2=makeQuery(id+"F3.imprint","IMPRINT",FACE,{"disambiguationData":[TD([[makeQuery(id+"F3.imprint","IMPRINT",EDGE,{"derivedFrom":sQuery(id+"F3.wireOp",EDGE,"E20.4.0")}),-1.0]])]});
            loft(context, id + "F35", {"operationType" : NewBodyOperationType.ADD, "sheetProfilesArray" : [{ "sheetProfileEntities" : qUnion([Q1]) }, { "sheetProfileEntities" : qUnion([Q2]) }]});
        }
        {
            var Q1;
            Q1=makeQuery(id+"F22.imprint","IMPRINT",FACE,{"disambiguationData":[TD([[makeQuery(id+"F22.imprint","IMPRINT",EDGE,{"derivedFrom":sQuery(id+"F22.wireOp",EDGE,"E28.13.0")}),-1.0]])]});
            var Q2;
            Q2=makeQuery(id+"F3.imprint","IMPRINT",FACE,{"disambiguationData":[TD([[makeQuery(id+"F3.imprint","IMPRINT",EDGE,{"derivedFrom":sQuery(id+"F3.wireOp",EDGE,"E20.5.0")}),-1.0]])]});
            loft(context, id + "F36", {"operationType" : NewBodyOperationType.ADD, "sheetProfilesArray" : [{ "sheetProfileEntities" : qUnion([Q1]) }, { "sheetProfileEntities" : qUnion([Q2]) }]});
        }
        {
            var Q1;
            Q1=makeQuery(id+"F22.imprint","IMPRINT",FACE,{"disambiguationData":[TD([[makeQuery(id+"F22.imprint","IMPRINT",EDGE,{"derivedFrom":sQuery(id+"F22.wireOp",EDGE,"E28.14.0")}),-1.0]])]});
            var Q2;
            Q2=makeQuery(id+"F3.imprint","IMPRINT",FACE,{"disambiguationData":[TD([[makeQuery(id+"F3.imprint","IMPRINT",EDGE,{"derivedFrom":sQuery(id+"F3.wireOp",EDGE,"E20.6.0")}),-1.0]])]});
            loft(context, id + "F37", {"operationType" : NewBodyOperationType.ADD, "sheetProfilesArray" : [{ "sheetProfileEntities" : qUnion([Q1]) }, { "sheetProfileEntities" : qUnion([Q2]) }]});
        }
        {
            var Q1;
            Q1=makeQuery(id+"F22.imprint","IMPRINT",FACE,{"disambiguationData":[TD([[makeQuery(id+"F22.imprint","IMPRINT",EDGE,{"derivedFrom":sQuery(id+"F22.wireOp",EDGE,"E28.15.0")}),-1.0]])]});
            var Q2;
            Q2=makeQuery(id+"F3.imprint","IMPRINT",FACE,{"disambiguationData":[TD([[makeQuery(id+"F3.imprint","IMPRINT",EDGE,{"derivedFrom":sQuery(id+"F3.wireOp",EDGE,"E20.7.0")}),-1.0]])]});
            loft(context, id + "F38", {"operationType" : NewBodyOperationType.ADD, "sheetProfilesArray" : [{ "sheetProfileEntities" : qUnion([Q1]) }, { "sheetProfileEntities" : qUnion([Q2]) }]});
        }
        {
            var Q0;
            Q0=qCreatedBy(makeId("Top.planeOp"),FACE);
            var sketch = newSketch(context, id + "F39", { "sketchPlane" : qUnion([Q0])});
            skCircle(sketch, "E29", {"center": v(0, 0) * mm, "radius": 61 * mm});
            skCircle(sketch, "E30", {"center": v(0, 0) * mm, "radius": 69 * mm});
            skSolve(sketch);
        }
        {
            var Q0;
            Q0=makeQuery(id+"F39.imprint","IMPRINT",FACE,{"disambiguationData":[TD([[makeQuery(id+"F39.imprint","IMPRINT",EDGE,{"derivedFrom":sQuery(id+"F39.wireOp",EDGE,"E29")}),-1.0]])]});
            extrude(context, id + "F40", {"entities" : qUnion([Q0]), "operationType" : NewBodyOperationType.ADD, "endBound" : BoundingType.SYMMETRIC, "depth" : 6 * mm});
        }
        {
            var Q0;
            Q0=qCreatedBy(makeId("Right.planeOp"),FACE);
            var sketch = newSketch(context, id + "F41", { "sketchPlane" : qUnion([Q0])});
            skLineSegment(sketch, "E31", {"start": v(0, 27) * mm, "end": v(0, -27) * mm, "construction": true});
            skCircle(sketch, "E32", {"center": v(0, 0) * mm, "radius": 67.5 * mm});
            skCircle(sketch, "E33", {"center": v(0, 0) * mm, "radius": 85 * mm});
            skLineSegment(sketch, "E34", {"start": v(0, 85) * mm, "end": v(0, -85) * mm});
            skSolve(sketch);
        }
        {
            var Q0;
            {var subQ0=sQuery(id+"F41.wireOp",EDGE,"E34");var subQ1=sQuery(id+"F41.wireOp",EDGE,"E32");var subQ2=makeQuery(id+"F41.imprint","INTERSECT",VERTEX,{"disambiguationData":[OD(0.0)],"derivedFrom":[subQ1,subQ0]});Q0=makeQuery(id+"F41.imprint","IMPRINT",FACE,{"disambiguationData":[TD([[makeQuery(id+"F41.imprint","IMPRINT",EDGE,{"disambiguationData":[TD([[subQ2,-1.0]])],"derivedFrom":subQ1}),-1.0]])]});}
            var Q1;
            Q1=sQuery(id+"F41.wireOp",EDGE,"E31");
            revolve(context, id + "F42", {"operationType" : NewBodyOperationType.REMOVE, "entities" : qUnion([Q0]), "axis" : qUnion([Q1]), "revolveType" : RevolveType.FULL, "oppositeDirection" : true});
        }
        {
            var Q0;
            Q0=makeQuery(id+"F42.boolean.opBoolean","INTERSECT",EDGE,{"disambiguationData":[OD(5.0)],"derivedFrom":[makeQuery(id+"F20.boolean.opBoolean","MERGE",FACE,{"derivedFrom":[makeQuery(id+"F19.boolean.opBoolean","MERGE",FACE,{"derivedFrom":[makeQuery(id+"F18.boolean.opBoolean","MERGE",FACE,{"derivedFrom":[makeQuery(id+"F17.boolean.opBoolean","MERGE",FACE,{"derivedFrom":[makeQuery(id+"F16.boolean.opBoolean","MERGE",FACE,{"derivedFrom":[makeQuery(id+"F15.boolean.opBoolean","MERGE",FACE,{"derivedFrom":[makeQuery(id+"F14.boolean.opBoolean","MERGE",FACE,{"derivedFrom":[makeQuery(id+"F13.boolean.opBoolean","MERGE",FACE,{"derivedFrom":[makeQuery(id+"F12.boolean.opBoolean","MERGE",FACE,{"derivedFrom":[makeQuery(id+"F11.boolean.opBoolean","MERGE",FACE,{"derivedFrom":[makeQuery(id+"F10.boolean.opBoolean","MERGE",FACE,{"derivedFrom":[makeQuery(id+"F9.boolean.opBoolean","MERGE",FACE,{"derivedFrom":[makeQuery(id+"F8.boolean.opBoolean","MERGE",FACE,{"derivedFrom":[makeQuery(id+"F7.boolean.opBoolean","MERGE",FACE,{"derivedFrom":[makeQuery(id+"F6.boolean.opBoolean","MERGE",FACE,{"derivedFrom":[makeQuery(id+"F5.boolean.opBoolean","MERGE",FACE,{"derivedFrom":[makeQuery(id+"F1.opRevolve","SWEPT_FACE",FACE,{"disambiguationData":[OSD([sQuery(id+"F0.wireOp",EDGE,"E14")])]}),makeQuery(id+"F5.opLoft","CAP_FACE",FACE,{"disambiguationData":[OSD([makeQuery(id+"F4.imprint","IMPRINT",FACE,{"disambiguationData":[TD([[makeQuery(id+"F4.imprint","IMPRINT",EDGE,{"derivedFrom":sQuery(id+"F4.wireOp",EDGE,"E21")}),1.0]])]})])],"isStart":true})]}),makeQuery(id+"F6.opLoft","CAP_FACE",FACE,{"disambiguationData":[OSD([makeQuery(id+"F4.imprint","IMPRINT",FACE,{"disambiguationData":[TD([[makeQuery(id+"F4.imprint","IMPRINT",EDGE,{"derivedFrom":sQuery(id+"F4.wireOp",EDGE,"E26.15.0")}),1.0]])]})])],"isStart":true})]}),makeQuery(id+"F7.opLoft","CAP_FACE",FACE,{"disambiguationData":[OSD([makeQuery(id+"F4.imprint","IMPRINT",FACE,{"disambiguationData":[TD([[makeQuery(id+"F4.imprint","IMPRINT",EDGE,{"derivedFrom":sQuery(id+"F4.wireOp",EDGE,"E26.14.0")}),1.0]])]})])],"isStart":true})]}),makeQuery(id+"F8.opLoft","CAP_FACE",FACE,{"disambiguationData":[OSD([makeQuery(id+"F4.imprint","IMPRINT",FACE,{"disambiguationData":[TD([[makeQuery(id+"F4.imprint","IMPRINT",EDGE,{"derivedFrom":sQuery(id+"F4.wireOp",EDGE,"E26.13.0")}),1.0]])]})])],"isStart":true})]}),makeQuery(id+"F9.opLoft","CAP_FACE",FACE,{"disambiguationData":[OSD([makeQuery(id+"F4.imprint","IMPRINT",FACE,{"disambiguationData":[TD([[makeQuery(id+"F4.imprint","IMPRINT",EDGE,{"derivedFrom":sQuery(id+"F4.wireOp",EDGE,"E26.12.0")}),1.0]])]})])],"isStart":true})]}),makeQuery(id+"F10.opLoft","CAP_FACE",FACE,{"disambiguationData":[OSD([makeQuery(id+"F4.imprint","IMPRINT",FACE,{"disambiguationData":[TD([[makeQuery(id+"F4.imprint","IMPRINT",EDGE,{"derivedFrom":sQuery(id+"F4.wireOp",EDGE,"E26.11.0")}),1.0]])]})])],"isStart":true})]}),makeQuery(id+"F11.opLoft","CAP_FACE",FACE,{"disambiguationData":[OSD([makeQuery(id+"F4.imprint","IMPRINT",FACE,{"disambiguationData":[TD([[makeQuery(id+"F4.imprint","IMPRINT",EDGE,{"derivedFrom":sQuery(id+"F4.wireOp",EDGE,"E26.10.0")}),1.0]])]})])],"isStart":true})]}),makeQuery(id+"F12.opLoft","CAP_FACE",FACE,{"disambiguationData":[OSD([makeQuery(id+"F4.imprint","IMPRINT",FACE,{"disambiguationData":[TD([[makeQuery(id+"F4.imprint","IMPRINT",EDGE,{"derivedFrom":sQuery(id+"F4.wireOp",EDGE,"E26.9.0")}),1.0]])]})])],"isStart":true})]}),makeQuery(id+"F13.opLoft","CAP_FACE",FACE,{"disambiguationData":[OSD([makeQuery(id+"F4.imprint","IMPRINT",FACE,{"disambiguationData":[TD([[makeQuery(id+"F4.imprint","IMPRINT",EDGE,{"derivedFrom":sQuery(id+"F4.wireOp",EDGE,"E26.8.0")}),1.0]])]})])],"isStart":true})]}),makeQuery(id+"F14.opLoft","CAP_FACE",FACE,{"disambiguationData":[OSD([makeQuery(id+"F4.imprint","IMPRINT",FACE,{"disambiguationData":[TD([[makeQuery(id+"F4.imprint","IMPRINT",EDGE,{"derivedFrom":sQuery(id+"F4.wireOp",EDGE,"E26.7.0")}),1.0]])]})])],"isStart":true})]}),makeQuery(id+"F15.opLoft","CAP_FACE",FACE,{"disambiguationData":[OSD([makeQuery(id+"F4.imprint","IMPRINT",FACE,{"disambiguationData":[TD([[makeQuery(id+"F4.imprint","IMPRINT",EDGE,{"derivedFrom":sQuery(id+"F4.wireOp",EDGE,"E26.6.0")}),1.0]])]})])],"isStart":true})]}),makeQuery(id+"F16.opLoft","CAP_FACE",FACE,{"disambiguationData":[OSD([makeQuery(id+"F4.imprint","IMPRINT",FACE,{"disambiguationData":[TD([[makeQuery(id+"F4.imprint","IMPRINT",EDGE,{"derivedFrom":sQuery(id+"F4.wireOp",EDGE,"E26.5.0")}),1.0]])]})])],"isStart":true})]}),makeQuery(id+"F17.opLoft","CAP_FACE",FACE,{"disambiguationData":[OSD([makeQuery(id+"F4.imprint","IMPRINT",FACE,{"disambiguationData":[TD([[makeQuery(id+"F4.imprint","IMPRINT",EDGE,{"derivedFrom":sQuery(id+"F4.wireOp",EDGE,"E26.4.0")}),1.0]])]})])],"isStart":true})]}),makeQuery(id+"F18.opLoft","CAP_FACE",FACE,{"disambiguationData":[OSD([makeQuery(id+"F4.imprint","IMPRINT",FACE,{"disambiguationData":[TD([[makeQuery(id+"F4.imprint","IMPRINT",EDGE,{"derivedFrom":sQuery(id+"F4.wireOp",EDGE,"E26.3.0")}),1.0]])]})])],"isStart":true})]}),makeQuery(id+"F19.opLoft","CAP_FACE",FACE,{"disambiguationData":[OSD([makeQuery(id+"F4.imprint","IMPRINT",FACE,{"disambiguationData":[TD([[makeQuery(id+"F4.imprint","IMPRINT",EDGE,{"derivedFrom":sQuery(id+"F4.wireOp",EDGE,"E26.2.0")}),1.0]])]})])],"isStart":true})]}),makeQuery(id+"F20.opLoft","CAP_FACE",FACE,{"disambiguationData":[OSD([makeQuery(id+"F4.imprint","IMPRINT",FACE,{"disambiguationData":[TD([[makeQuery(id+"F4.imprint","IMPRINT",EDGE,{"derivedFrom":sQuery(id+"F4.wireOp",EDGE,"E26.1.0")}),1.0]])]})])],"isStart":true})]}),makeQuery(id+"F42.opRevolve","SWEPT_FACE",FACE,{"disambiguationData":[OSD([sQuery(id+"F41.wireOp",EDGE,"E32")])]})]});
            var Q1;
            Q1=makeQuery(id+"F42.boolean.opBoolean","INTERSECT",EDGE,{"disambiguationData":[OD(4.0)],"derivedFrom":[makeQuery(id+"F20.boolean.opBoolean","MERGE",FACE,{"derivedFrom":[makeQuery(id+"F19.boolean.opBoolean","MERGE",FACE,{"derivedFrom":[makeQuery(id+"F18.boolean.opBoolean","MERGE",FACE,{"derivedFrom":[makeQuery(id+"F17.boolean.opBoolean","MERGE",FACE,{"derivedFrom":[makeQuery(id+"F16.boolean.opBoolean","MERGE",FACE,{"derivedFrom":[makeQuery(id+"F15.boolean.opBoolean","MERGE",FACE,{"derivedFrom":[makeQuery(id+"F14.boolean.opBoolean","MERGE",FACE,{"derivedFrom":[makeQuery(id+"F13.boolean.opBoolean","MERGE",FACE,{"derivedFrom":[makeQuery(id+"F12.boolean.opBoolean","MERGE",FACE,{"derivedFrom":[makeQuery(id+"F11.boolean.opBoolean","MERGE",FACE,{"derivedFrom":[makeQuery(id+"F10.boolean.opBoolean","MERGE",FACE,{"derivedFrom":[makeQuery(id+"F9.boolean.opBoolean","MERGE",FACE,{"derivedFrom":[makeQuery(id+"F8.boolean.opBoolean","MERGE",FACE,{"derivedFrom":[makeQuery(id+"F7.boolean.opBoolean","MERGE",FACE,{"derivedFrom":[makeQuery(id+"F6.boolean.opBoolean","MERGE",FACE,{"derivedFrom":[makeQuery(id+"F5.boolean.opBoolean","MERGE",FACE,{"derivedFrom":[makeQuery(id+"F1.opRevolve","SWEPT_FACE",FACE,{"disambiguationData":[OSD([sQuery(id+"F0.wireOp",EDGE,"E14")])]}),makeQuery(id+"F5.opLoft","CAP_FACE",FACE,{"disambiguationData":[OSD([makeQuery(id+"F4.imprint","IMPRINT",FACE,{"disambiguationData":[TD([[makeQuery(id+"F4.imprint","IMPRINT",EDGE,{"derivedFrom":sQuery(id+"F4.wireOp",EDGE,"E21")}),1.0]])]})])],"isStart":true})]}),makeQuery(id+"F6.opLoft","CAP_FACE",FACE,{"disambiguationData":[OSD([makeQuery(id+"F4.imprint","IMPRINT",FACE,{"disambiguationData":[TD([[makeQuery(id+"F4.imprint","IMPRINT",EDGE,{"derivedFrom":sQuery(id+"F4.wireOp",EDGE,"E26.15.0")}),1.0]])]})])],"isStart":true})]}),makeQuery(id+"F7.opLoft","CAP_FACE",FACE,{"disambiguationData":[OSD([makeQuery(id+"F4.imprint","IMPRINT",FACE,{"disambiguationData":[TD([[makeQuery(id+"F4.imprint","IMPRINT",EDGE,{"derivedFrom":sQuery(id+"F4.wireOp",EDGE,"E26.14.0")}),1.0]])]})])],"isStart":true})]}),makeQuery(id+"F8.opLoft","CAP_FACE",FACE,{"disambiguationData":[OSD([makeQuery(id+"F4.imprint","IMPRINT",FACE,{"disambiguationData":[TD([[makeQuery(id+"F4.imprint","IMPRINT",EDGE,{"derivedFrom":sQuery(id+"F4.wireOp",EDGE,"E26.13.0")}),1.0]])]})])],"isStart":true})]}),makeQuery(id+"F9.opLoft","CAP_FACE",FACE,{"disambiguationData":[OSD([makeQuery(id+"F4.imprint","IMPRINT",FACE,{"disambiguationData":[TD([[makeQuery(id+"F4.imprint","IMPRINT",EDGE,{"derivedFrom":sQuery(id+"F4.wireOp",EDGE,"E26.12.0")}),1.0]])]})])],"isStart":true})]}),makeQuery(id+"F10.opLoft","CAP_FACE",FACE,{"disambiguationData":[OSD([makeQuery(id+"F4.imprint","IMPRINT",FACE,{"disambiguationData":[TD([[makeQuery(id+"F4.imprint","IMPRINT",EDGE,{"derivedFrom":sQuery(id+"F4.wireOp",EDGE,"E26.11.0")}),1.0]])]})])],"isStart":true})]}),makeQuery(id+"F11.opLoft","CAP_FACE",FACE,{"disambiguationData":[OSD([makeQuery(id+"F4.imprint","IMPRINT",FACE,{"disambiguationData":[TD([[makeQuery(id+"F4.imprint","IMPRINT",EDGE,{"derivedFrom":sQuery(id+"F4.wireOp",EDGE,"E26.10.0")}),1.0]])]})])],"isStart":true})]}),makeQuery(id+"F12.opLoft","CAP_FACE",FACE,{"disambiguationData":[OSD([makeQuery(id+"F4.imprint","IMPRINT",FACE,{"disambiguationData":[TD([[makeQuery(id+"F4.imprint","IMPRINT",EDGE,{"derivedFrom":sQuery(id+"F4.wireOp",EDGE,"E26.9.0")}),1.0]])]})])],"isStart":true})]}),makeQuery(id+"F13.opLoft","CAP_FACE",FACE,{"disambiguationData":[OSD([makeQuery(id+"F4.imprint","IMPRINT",FACE,{"disambiguationData":[TD([[makeQuery(id+"F4.imprint","IMPRINT",EDGE,{"derivedFrom":sQuery(id+"F4.wireOp",EDGE,"E26.8.0")}),1.0]])]})])],"isStart":true})]}),makeQuery(id+"F14.opLoft","CAP_FACE",FACE,{"disambiguationData":[OSD([makeQuery(id+"F4.imprint","IMPRINT",FACE,{"disambiguationData":[TD([[makeQuery(id+"F4.imprint","IMPRINT",EDGE,{"derivedFrom":sQuery(id+"F4.wireOp",EDGE,"E26.7.0")}),1.0]])]})])],"isStart":true})]}),makeQuery(id+"F15.opLoft","CAP_FACE",FACE,{"disambiguationData":[OSD([makeQuery(id+"F4.imprint","IMPRINT",FACE,{"disambiguationData":[TD([[makeQuery(id+"F4.imprint","IMPRINT",EDGE,{"derivedFrom":sQuery(id+"F4.wireOp",EDGE,"E26.6.0")}),1.0]])]})])],"isStart":true})]}),makeQuery(id+"F16.opLoft","CAP_FACE",FACE,{"disambiguationData":[OSD([makeQuery(id+"F4.imprint","IMPRINT",FACE,{"disambiguationData":[TD([[makeQuery(id+"F4.imprint","IMPRINT",EDGE,{"derivedFrom":sQuery(id+"F4.wireOp",EDGE,"E26.5.0")}),1.0]])]})])],"isStart":true})]}),makeQuery(id+"F17.opLoft","CAP_FACE",FACE,{"disambiguationData":[OSD([makeQuery(id+"F4.imprint","IMPRINT",FACE,{"disambiguationData":[TD([[makeQuery(id+"F4.imprint","IMPRINT",EDGE,{"derivedFrom":sQuery(id+"F4.wireOp",EDGE,"E26.4.0")}),1.0]])]})])],"isStart":true})]}),makeQuery(id+"F18.opLoft","CAP_FACE",FACE,{"disambiguationData":[OSD([makeQuery(id+"F4.imprint","IMPRINT",FACE,{"disambiguationData":[TD([[makeQuery(id+"F4.imprint","IMPRINT",EDGE,{"derivedFrom":sQuery(id+"F4.wireOp",EDGE,"E26.3.0")}),1.0]])]})])],"isStart":true})]}),makeQuery(id+"F19.opLoft","CAP_FACE",FACE,{"disambiguationData":[OSD([makeQuery(id+"F4.imprint","IMPRINT",FACE,{"disambiguationData":[TD([[makeQuery(id+"F4.imprint","IMPRINT",EDGE,{"derivedFrom":sQuery(id+"F4.wireOp",EDGE,"E26.2.0")}),1.0]])]})])],"isStart":true})]}),makeQuery(id+"F20.opLoft","CAP_FACE",FACE,{"disambiguationData":[OSD([makeQuery(id+"F4.imprint","IMPRINT",FACE,{"disambiguationData":[TD([[makeQuery(id+"F4.imprint","IMPRINT",EDGE,{"derivedFrom":sQuery(id+"F4.wireOp",EDGE,"E26.1.0")}),1.0]])]})])],"isStart":true})]}),makeQuery(id+"F42.opRevolve","SWEPT_FACE",FACE,{"disambiguationData":[OSD([sQuery(id+"F41.wireOp",EDGE,"E32")])]})]});
            var Q2;
            Q2=makeQuery(id+"F42.boolean.opBoolean","INTERSECT",EDGE,{"disambiguationData":[OD(3.0)],"derivedFrom":[makeQuery(id+"F20.boolean.opBoolean","MERGE",FACE,{"derivedFrom":[makeQuery(id+"F19.boolean.opBoolean","MERGE",FACE,{"derivedFrom":[makeQuery(id+"F18.boolean.opBoolean","MERGE",FACE,{"derivedFrom":[makeQuery(id+"F17.boolean.opBoolean","MERGE",FACE,{"derivedFrom":[makeQuery(id+"F16.boolean.opBoolean","MERGE",FACE,{"derivedFrom":[makeQuery(id+"F15.boolean.opBoolean","MERGE",FACE,{"derivedFrom":[makeQuery(id+"F14.boolean.opBoolean","MERGE",FACE,{"derivedFrom":[makeQuery(id+"F13.boolean.opBoolean","MERGE",FACE,{"derivedFrom":[makeQuery(id+"F12.boolean.opBoolean","MERGE",FACE,{"derivedFrom":[makeQuery(id+"F11.boolean.opBoolean","MERGE",FACE,{"derivedFrom":[makeQuery(id+"F10.boolean.opBoolean","MERGE",FACE,{"derivedFrom":[makeQuery(id+"F9.boolean.opBoolean","MERGE",FACE,{"derivedFrom":[makeQuery(id+"F8.boolean.opBoolean","MERGE",FACE,{"derivedFrom":[makeQuery(id+"F7.boolean.opBoolean","MERGE",FACE,{"derivedFrom":[makeQuery(id+"F6.boolean.opBoolean","MERGE",FACE,{"derivedFrom":[makeQuery(id+"F5.boolean.opBoolean","MERGE",FACE,{"derivedFrom":[makeQuery(id+"F1.opRevolve","SWEPT_FACE",FACE,{"disambiguationData":[OSD([sQuery(id+"F0.wireOp",EDGE,"E14")])]}),makeQuery(id+"F5.opLoft","CAP_FACE",FACE,{"disambiguationData":[OSD([makeQuery(id+"F4.imprint","IMPRINT",FACE,{"disambiguationData":[TD([[makeQuery(id+"F4.imprint","IMPRINT",EDGE,{"derivedFrom":sQuery(id+"F4.wireOp",EDGE,"E21")}),1.0]])]})])],"isStart":true})]}),makeQuery(id+"F6.opLoft","CAP_FACE",FACE,{"disambiguationData":[OSD([makeQuery(id+"F4.imprint","IMPRINT",FACE,{"disambiguationData":[TD([[makeQuery(id+"F4.imprint","IMPRINT",EDGE,{"derivedFrom":sQuery(id+"F4.wireOp",EDGE,"E26.15.0")}),1.0]])]})])],"isStart":true})]}),makeQuery(id+"F7.opLoft","CAP_FACE",FACE,{"disambiguationData":[OSD([makeQuery(id+"F4.imprint","IMPRINT",FACE,{"disambiguationData":[TD([[makeQuery(id+"F4.imprint","IMPRINT",EDGE,{"derivedFrom":sQuery(id+"F4.wireOp",EDGE,"E26.14.0")}),1.0]])]})])],"isStart":true})]}),makeQuery(id+"F8.opLoft","CAP_FACE",FACE,{"disambiguationData":[OSD([makeQuery(id+"F4.imprint","IMPRINT",FACE,{"disambiguationData":[TD([[makeQuery(id+"F4.imprint","IMPRINT",EDGE,{"derivedFrom":sQuery(id+"F4.wireOp",EDGE,"E26.13.0")}),1.0]])]})])],"isStart":true})]}),makeQuery(id+"F9.opLoft","CAP_FACE",FACE,{"disambiguationData":[OSD([makeQuery(id+"F4.imprint","IMPRINT",FACE,{"disambiguationData":[TD([[makeQuery(id+"F4.imprint","IMPRINT",EDGE,{"derivedFrom":sQuery(id+"F4.wireOp",EDGE,"E26.12.0")}),1.0]])]})])],"isStart":true})]}),makeQuery(id+"F10.opLoft","CAP_FACE",FACE,{"disambiguationData":[OSD([makeQuery(id+"F4.imprint","IMPRINT",FACE,{"disambiguationData":[TD([[makeQuery(id+"F4.imprint","IMPRINT",EDGE,{"derivedFrom":sQuery(id+"F4.wireOp",EDGE,"E26.11.0")}),1.0]])]})])],"isStart":true})]}),makeQuery(id+"F11.opLoft","CAP_FACE",FACE,{"disambiguationData":[OSD([makeQuery(id+"F4.imprint","IMPRINT",FACE,{"disambiguationData":[TD([[makeQuery(id+"F4.imprint","IMPRINT",EDGE,{"derivedFrom":sQuery(id+"F4.wireOp",EDGE,"E26.10.0")}),1.0]])]})])],"isStart":true})]}),makeQuery(id+"F12.opLoft","CAP_FACE",FACE,{"disambiguationData":[OSD([makeQuery(id+"F4.imprint","IMPRINT",FACE,{"disambiguationData":[TD([[makeQuery(id+"F4.imprint","IMPRINT",EDGE,{"derivedFrom":sQuery(id+"F4.wireOp",EDGE,"E26.9.0")}),1.0]])]})])],"isStart":true})]}),makeQuery(id+"F13.opLoft","CAP_FACE",FACE,{"disambiguationData":[OSD([makeQuery(id+"F4.imprint","IMPRINT",FACE,{"disambiguationData":[TD([[makeQuery(id+"F4.imprint","IMPRINT",EDGE,{"derivedFrom":sQuery(id+"F4.wireOp",EDGE,"E26.8.0")}),1.0]])]})])],"isStart":true})]}),makeQuery(id+"F14.opLoft","CAP_FACE",FACE,{"disambiguationData":[OSD([makeQuery(id+"F4.imprint","IMPRINT",FACE,{"disambiguationData":[TD([[makeQuery(id+"F4.imprint","IMPRINT",EDGE,{"derivedFrom":sQuery(id+"F4.wireOp",EDGE,"E26.7.0")}),1.0]])]})])],"isStart":true})]}),makeQuery(id+"F15.opLoft","CAP_FACE",FACE,{"disambiguationData":[OSD([makeQuery(id+"F4.imprint","IMPRINT",FACE,{"disambiguationData":[TD([[makeQuery(id+"F4.imprint","IMPRINT",EDGE,{"derivedFrom":sQuery(id+"F4.wireOp",EDGE,"E26.6.0")}),1.0]])]})])],"isStart":true})]}),makeQuery(id+"F16.opLoft","CAP_FACE",FACE,{"disambiguationData":[OSD([makeQuery(id+"F4.imprint","IMPRINT",FACE,{"disambiguationData":[TD([[makeQuery(id+"F4.imprint","IMPRINT",EDGE,{"derivedFrom":sQuery(id+"F4.wireOp",EDGE,"E26.5.0")}),1.0]])]})])],"isStart":true})]}),makeQuery(id+"F17.opLoft","CAP_FACE",FACE,{"disambiguationData":[OSD([makeQuery(id+"F4.imprint","IMPRINT",FACE,{"disambiguationData":[TD([[makeQuery(id+"F4.imprint","IMPRINT",EDGE,{"derivedFrom":sQuery(id+"F4.wireOp",EDGE,"E26.4.0")}),1.0]])]})])],"isStart":true})]}),makeQuery(id+"F18.opLoft","CAP_FACE",FACE,{"disambiguationData":[OSD([makeQuery(id+"F4.imprint","IMPRINT",FACE,{"disambiguationData":[TD([[makeQuery(id+"F4.imprint","IMPRINT",EDGE,{"derivedFrom":sQuery(id+"F4.wireOp",EDGE,"E26.3.0")}),1.0]])]})])],"isStart":true})]}),makeQuery(id+"F19.opLoft","CAP_FACE",FACE,{"disambiguationData":[OSD([makeQuery(id+"F4.imprint","IMPRINT",FACE,{"disambiguationData":[TD([[makeQuery(id+"F4.imprint","IMPRINT",EDGE,{"derivedFrom":sQuery(id+"F4.wireOp",EDGE,"E26.2.0")}),1.0]])]})])],"isStart":true})]}),makeQuery(id+"F20.opLoft","CAP_FACE",FACE,{"disambiguationData":[OSD([makeQuery(id+"F4.imprint","IMPRINT",FACE,{"disambiguationData":[TD([[makeQuery(id+"F4.imprint","IMPRINT",EDGE,{"derivedFrom":sQuery(id+"F4.wireOp",EDGE,"E26.1.0")}),1.0]])]})])],"isStart":true})]}),makeQuery(id+"F42.opRevolve","SWEPT_FACE",FACE,{"disambiguationData":[OSD([sQuery(id+"F41.wireOp",EDGE,"E32")])]})]});
            var Q3;
            Q3=makeQuery(id+"F42.boolean.opBoolean","INTERSECT",EDGE,{"disambiguationData":[OD(2.0)],"derivedFrom":[makeQuery(id+"F20.boolean.opBoolean","MERGE",FACE,{"derivedFrom":[makeQuery(id+"F19.boolean.opBoolean","MERGE",FACE,{"derivedFrom":[makeQuery(id+"F18.boolean.opBoolean","MERGE",FACE,{"derivedFrom":[makeQuery(id+"F17.boolean.opBoolean","MERGE",FACE,{"derivedFrom":[makeQuery(id+"F16.boolean.opBoolean","MERGE",FACE,{"derivedFrom":[makeQuery(id+"F15.boolean.opBoolean","MERGE",FACE,{"derivedFrom":[makeQuery(id+"F14.boolean.opBoolean","MERGE",FACE,{"derivedFrom":[makeQuery(id+"F13.boolean.opBoolean","MERGE",FACE,{"derivedFrom":[makeQuery(id+"F12.boolean.opBoolean","MERGE",FACE,{"derivedFrom":[makeQuery(id+"F11.boolean.opBoolean","MERGE",FACE,{"derivedFrom":[makeQuery(id+"F10.boolean.opBoolean","MERGE",FACE,{"derivedFrom":[makeQuery(id+"F9.boolean.opBoolean","MERGE",FACE,{"derivedFrom":[makeQuery(id+"F8.boolean.opBoolean","MERGE",FACE,{"derivedFrom":[makeQuery(id+"F7.boolean.opBoolean","MERGE",FACE,{"derivedFrom":[makeQuery(id+"F6.boolean.opBoolean","MERGE",FACE,{"derivedFrom":[makeQuery(id+"F5.boolean.opBoolean","MERGE",FACE,{"derivedFrom":[makeQuery(id+"F1.opRevolve","SWEPT_FACE",FACE,{"disambiguationData":[OSD([sQuery(id+"F0.wireOp",EDGE,"E14")])]}),makeQuery(id+"F5.opLoft","CAP_FACE",FACE,{"disambiguationData":[OSD([makeQuery(id+"F4.imprint","IMPRINT",FACE,{"disambiguationData":[TD([[makeQuery(id+"F4.imprint","IMPRINT",EDGE,{"derivedFrom":sQuery(id+"F4.wireOp",EDGE,"E21")}),1.0]])]})])],"isStart":true})]}),makeQuery(id+"F6.opLoft","CAP_FACE",FACE,{"disambiguationData":[OSD([makeQuery(id+"F4.imprint","IMPRINT",FACE,{"disambiguationData":[TD([[makeQuery(id+"F4.imprint","IMPRINT",EDGE,{"derivedFrom":sQuery(id+"F4.wireOp",EDGE,"E26.15.0")}),1.0]])]})])],"isStart":true})]}),makeQuery(id+"F7.opLoft","CAP_FACE",FACE,{"disambiguationData":[OSD([makeQuery(id+"F4.imprint","IMPRINT",FACE,{"disambiguationData":[TD([[makeQuery(id+"F4.imprint","IMPRINT",EDGE,{"derivedFrom":sQuery(id+"F4.wireOp",EDGE,"E26.14.0")}),1.0]])]})])],"isStart":true})]}),makeQuery(id+"F8.opLoft","CAP_FACE",FACE,{"disambiguationData":[OSD([makeQuery(id+"F4.imprint","IMPRINT",FACE,{"disambiguationData":[TD([[makeQuery(id+"F4.imprint","IMPRINT",EDGE,{"derivedFrom":sQuery(id+"F4.wireOp",EDGE,"E26.13.0")}),1.0]])]})])],"isStart":true})]}),makeQuery(id+"F9.opLoft","CAP_FACE",FACE,{"disambiguationData":[OSD([makeQuery(id+"F4.imprint","IMPRINT",FACE,{"disambiguationData":[TD([[makeQuery(id+"F4.imprint","IMPRINT",EDGE,{"derivedFrom":sQuery(id+"F4.wireOp",EDGE,"E26.12.0")}),1.0]])]})])],"isStart":true})]}),makeQuery(id+"F10.opLoft","CAP_FACE",FACE,{"disambiguationData":[OSD([makeQuery(id+"F4.imprint","IMPRINT",FACE,{"disambiguationData":[TD([[makeQuery(id+"F4.imprint","IMPRINT",EDGE,{"derivedFrom":sQuery(id+"F4.wireOp",EDGE,"E26.11.0")}),1.0]])]})])],"isStart":true})]}),makeQuery(id+"F11.opLoft","CAP_FACE",FACE,{"disambiguationData":[OSD([makeQuery(id+"F4.imprint","IMPRINT",FACE,{"disambiguationData":[TD([[makeQuery(id+"F4.imprint","IMPRINT",EDGE,{"derivedFrom":sQuery(id+"F4.wireOp",EDGE,"E26.10.0")}),1.0]])]})])],"isStart":true})]}),makeQuery(id+"F12.opLoft","CAP_FACE",FACE,{"disambiguationData":[OSD([makeQuery(id+"F4.imprint","IMPRINT",FACE,{"disambiguationData":[TD([[makeQuery(id+"F4.imprint","IMPRINT",EDGE,{"derivedFrom":sQuery(id+"F4.wireOp",EDGE,"E26.9.0")}),1.0]])]})])],"isStart":true})]}),makeQuery(id+"F13.opLoft","CAP_FACE",FACE,{"disambiguationData":[OSD([makeQuery(id+"F4.imprint","IMPRINT",FACE,{"disambiguationData":[TD([[makeQuery(id+"F4.imprint","IMPRINT",EDGE,{"derivedFrom":sQuery(id+"F4.wireOp",EDGE,"E26.8.0")}),1.0]])]})])],"isStart":true})]}),makeQuery(id+"F14.opLoft","CAP_FACE",FACE,{"disambiguationData":[OSD([makeQuery(id+"F4.imprint","IMPRINT",FACE,{"disambiguationData":[TD([[makeQuery(id+"F4.imprint","IMPRINT",EDGE,{"derivedFrom":sQuery(id+"F4.wireOp",EDGE,"E26.7.0")}),1.0]])]})])],"isStart":true})]}),makeQuery(id+"F15.opLoft","CAP_FACE",FACE,{"disambiguationData":[OSD([makeQuery(id+"F4.imprint","IMPRINT",FACE,{"disambiguationData":[TD([[makeQuery(id+"F4.imprint","IMPRINT",EDGE,{"derivedFrom":sQuery(id+"F4.wireOp",EDGE,"E26.6.0")}),1.0]])]})])],"isStart":true})]}),makeQuery(id+"F16.opLoft","CAP_FACE",FACE,{"disambiguationData":[OSD([makeQuery(id+"F4.imprint","IMPRINT",FACE,{"disambiguationData":[TD([[makeQuery(id+"F4.imprint","IMPRINT",EDGE,{"derivedFrom":sQuery(id+"F4.wireOp",EDGE,"E26.5.0")}),1.0]])]})])],"isStart":true})]}),makeQuery(id+"F17.opLoft","CAP_FACE",FACE,{"disambiguationData":[OSD([makeQuery(id+"F4.imprint","IMPRINT",FACE,{"disambiguationData":[TD([[makeQuery(id+"F4.imprint","IMPRINT",EDGE,{"derivedFrom":sQuery(id+"F4.wireOp",EDGE,"E26.4.0")}),1.0]])]})])],"isStart":true})]}),makeQuery(id+"F18.opLoft","CAP_FACE",FACE,{"disambiguationData":[OSD([makeQuery(id+"F4.imprint","IMPRINT",FACE,{"disambiguationData":[TD([[makeQuery(id+"F4.imprint","IMPRINT",EDGE,{"derivedFrom":sQuery(id+"F4.wireOp",EDGE,"E26.3.0")}),1.0]])]})])],"isStart":true})]}),makeQuery(id+"F19.opLoft","CAP_FACE",FACE,{"disambiguationData":[OSD([makeQuery(id+"F4.imprint","IMPRINT",FACE,{"disambiguationData":[TD([[makeQuery(id+"F4.imprint","IMPRINT",EDGE,{"derivedFrom":sQuery(id+"F4.wireOp",EDGE,"E26.2.0")}),1.0]])]})])],"isStart":true})]}),makeQuery(id+"F20.opLoft","CAP_FACE",FACE,{"disambiguationData":[OSD([makeQuery(id+"F4.imprint","IMPRINT",FACE,{"disambiguationData":[TD([[makeQuery(id+"F4.imprint","IMPRINT",EDGE,{"derivedFrom":sQuery(id+"F4.wireOp",EDGE,"E26.1.0")}),1.0]])]})])],"isStart":true})]}),makeQuery(id+"F42.opRevolve","SWEPT_FACE",FACE,{"disambiguationData":[OSD([sQuery(id+"F41.wireOp",EDGE,"E32")])]})]});
            var Q4;
            Q4=makeQuery(id+"F42.boolean.opBoolean","INTERSECT",EDGE,{"disambiguationData":[OD(1.0)],"derivedFrom":[makeQuery(id+"F20.boolean.opBoolean","MERGE",FACE,{"derivedFrom":[makeQuery(id+"F19.boolean.opBoolean","MERGE",FACE,{"derivedFrom":[makeQuery(id+"F18.boolean.opBoolean","MERGE",FACE,{"derivedFrom":[makeQuery(id+"F17.boolean.opBoolean","MERGE",FACE,{"derivedFrom":[makeQuery(id+"F16.boolean.opBoolean","MERGE",FACE,{"derivedFrom":[makeQuery(id+"F15.boolean.opBoolean","MERGE",FACE,{"derivedFrom":[makeQuery(id+"F14.boolean.opBoolean","MERGE",FACE,{"derivedFrom":[makeQuery(id+"F13.boolean.opBoolean","MERGE",FACE,{"derivedFrom":[makeQuery(id+"F12.boolean.opBoolean","MERGE",FACE,{"derivedFrom":[makeQuery(id+"F11.boolean.opBoolean","MERGE",FACE,{"derivedFrom":[makeQuery(id+"F10.boolean.opBoolean","MERGE",FACE,{"derivedFrom":[makeQuery(id+"F9.boolean.opBoolean","MERGE",FACE,{"derivedFrom":[makeQuery(id+"F8.boolean.opBoolean","MERGE",FACE,{"derivedFrom":[makeQuery(id+"F7.boolean.opBoolean","MERGE",FACE,{"derivedFrom":[makeQuery(id+"F6.boolean.opBoolean","MERGE",FACE,{"derivedFrom":[makeQuery(id+"F5.boolean.opBoolean","MERGE",FACE,{"derivedFrom":[makeQuery(id+"F1.opRevolve","SWEPT_FACE",FACE,{"disambiguationData":[OSD([sQuery(id+"F0.wireOp",EDGE,"E14")])]}),makeQuery(id+"F5.opLoft","CAP_FACE",FACE,{"disambiguationData":[OSD([makeQuery(id+"F4.imprint","IMPRINT",FACE,{"disambiguationData":[TD([[makeQuery(id+"F4.imprint","IMPRINT",EDGE,{"derivedFrom":sQuery(id+"F4.wireOp",EDGE,"E21")}),1.0]])]})])],"isStart":true})]}),makeQuery(id+"F6.opLoft","CAP_FACE",FACE,{"disambiguationData":[OSD([makeQuery(id+"F4.imprint","IMPRINT",FACE,{"disambiguationData":[TD([[makeQuery(id+"F4.imprint","IMPRINT",EDGE,{"derivedFrom":sQuery(id+"F4.wireOp",EDGE,"E26.15.0")}),1.0]])]})])],"isStart":true})]}),makeQuery(id+"F7.opLoft","CAP_FACE",FACE,{"disambiguationData":[OSD([makeQuery(id+"F4.imprint","IMPRINT",FACE,{"disambiguationData":[TD([[makeQuery(id+"F4.imprint","IMPRINT",EDGE,{"derivedFrom":sQuery(id+"F4.wireOp",EDGE,"E26.14.0")}),1.0]])]})])],"isStart":true})]}),makeQuery(id+"F8.opLoft","CAP_FACE",FACE,{"disambiguationData":[OSD([makeQuery(id+"F4.imprint","IMPRINT",FACE,{"disambiguationData":[TD([[makeQuery(id+"F4.imprint","IMPRINT",EDGE,{"derivedFrom":sQuery(id+"F4.wireOp",EDGE,"E26.13.0")}),1.0]])]})])],"isStart":true})]}),makeQuery(id+"F9.opLoft","CAP_FACE",FACE,{"disambiguationData":[OSD([makeQuery(id+"F4.imprint","IMPRINT",FACE,{"disambiguationData":[TD([[makeQuery(id+"F4.imprint","IMPRINT",EDGE,{"derivedFrom":sQuery(id+"F4.wireOp",EDGE,"E26.12.0")}),1.0]])]})])],"isStart":true})]}),makeQuery(id+"F10.opLoft","CAP_FACE",FACE,{"disambiguationData":[OSD([makeQuery(id+"F4.imprint","IMPRINT",FACE,{"disambiguationData":[TD([[makeQuery(id+"F4.imprint","IMPRINT",EDGE,{"derivedFrom":sQuery(id+"F4.wireOp",EDGE,"E26.11.0")}),1.0]])]})])],"isStart":true})]}),makeQuery(id+"F11.opLoft","CAP_FACE",FACE,{"disambiguationData":[OSD([makeQuery(id+"F4.imprint","IMPRINT",FACE,{"disambiguationData":[TD([[makeQuery(id+"F4.imprint","IMPRINT",EDGE,{"derivedFrom":sQuery(id+"F4.wireOp",EDGE,"E26.10.0")}),1.0]])]})])],"isStart":true})]}),makeQuery(id+"F12.opLoft","CAP_FACE",FACE,{"disambiguationData":[OSD([makeQuery(id+"F4.imprint","IMPRINT",FACE,{"disambiguationData":[TD([[makeQuery(id+"F4.imprint","IMPRINT",EDGE,{"derivedFrom":sQuery(id+"F4.wireOp",EDGE,"E26.9.0")}),1.0]])]})])],"isStart":true})]}),makeQuery(id+"F13.opLoft","CAP_FACE",FACE,{"disambiguationData":[OSD([makeQuery(id+"F4.imprint","IMPRINT",FACE,{"disambiguationData":[TD([[makeQuery(id+"F4.imprint","IMPRINT",EDGE,{"derivedFrom":sQuery(id+"F4.wireOp",EDGE,"E26.8.0")}),1.0]])]})])],"isStart":true})]}),makeQuery(id+"F14.opLoft","CAP_FACE",FACE,{"disambiguationData":[OSD([makeQuery(id+"F4.imprint","IMPRINT",FACE,{"disambiguationData":[TD([[makeQuery(id+"F4.imprint","IMPRINT",EDGE,{"derivedFrom":sQuery(id+"F4.wireOp",EDGE,"E26.7.0")}),1.0]])]})])],"isStart":true})]}),makeQuery(id+"F15.opLoft","CAP_FACE",FACE,{"disambiguationData":[OSD([makeQuery(id+"F4.imprint","IMPRINT",FACE,{"disambiguationData":[TD([[makeQuery(id+"F4.imprint","IMPRINT",EDGE,{"derivedFrom":sQuery(id+"F4.wireOp",EDGE,"E26.6.0")}),1.0]])]})])],"isStart":true})]}),makeQuery(id+"F16.opLoft","CAP_FACE",FACE,{"disambiguationData":[OSD([makeQuery(id+"F4.imprint","IMPRINT",FACE,{"disambiguationData":[TD([[makeQuery(id+"F4.imprint","IMPRINT",EDGE,{"derivedFrom":sQuery(id+"F4.wireOp",EDGE,"E26.5.0")}),1.0]])]})])],"isStart":true})]}),makeQuery(id+"F17.opLoft","CAP_FACE",FACE,{"disambiguationData":[OSD([makeQuery(id+"F4.imprint","IMPRINT",FACE,{"disambiguationData":[TD([[makeQuery(id+"F4.imprint","IMPRINT",EDGE,{"derivedFrom":sQuery(id+"F4.wireOp",EDGE,"E26.4.0")}),1.0]])]})])],"isStart":true})]}),makeQuery(id+"F18.opLoft","CAP_FACE",FACE,{"disambiguationData":[OSD([makeQuery(id+"F4.imprint","IMPRINT",FACE,{"disambiguationData":[TD([[makeQuery(id+"F4.imprint","IMPRINT",EDGE,{"derivedFrom":sQuery(id+"F4.wireOp",EDGE,"E26.3.0")}),1.0]])]})])],"isStart":true})]}),makeQuery(id+"F19.opLoft","CAP_FACE",FACE,{"disambiguationData":[OSD([makeQuery(id+"F4.imprint","IMPRINT",FACE,{"disambiguationData":[TD([[makeQuery(id+"F4.imprint","IMPRINT",EDGE,{"derivedFrom":sQuery(id+"F4.wireOp",EDGE,"E26.2.0")}),1.0]])]})])],"isStart":true})]}),makeQuery(id+"F20.opLoft","CAP_FACE",FACE,{"disambiguationData":[OSD([makeQuery(id+"F4.imprint","IMPRINT",FACE,{"disambiguationData":[TD([[makeQuery(id+"F4.imprint","IMPRINT",EDGE,{"derivedFrom":sQuery(id+"F4.wireOp",EDGE,"E26.1.0")}),1.0]])]})])],"isStart":true})]}),makeQuery(id+"F42.opRevolve","SWEPT_FACE",FACE,{"disambiguationData":[OSD([sQuery(id+"F41.wireOp",EDGE,"E32")])]})]});
            var Q5;
            Q5=makeQuery(id+"F42.boolean.opBoolean","INTERSECT",EDGE,{"disambiguationData":[OD(0.0)],"derivedFrom":[makeQuery(id+"F20.boolean.opBoolean","MERGE",FACE,{"derivedFrom":[makeQuery(id+"F19.boolean.opBoolean","MERGE",FACE,{"derivedFrom":[makeQuery(id+"F18.boolean.opBoolean","MERGE",FACE,{"derivedFrom":[makeQuery(id+"F17.boolean.opBoolean","MERGE",FACE,{"derivedFrom":[makeQuery(id+"F16.boolean.opBoolean","MERGE",FACE,{"derivedFrom":[makeQuery(id+"F15.boolean.opBoolean","MERGE",FACE,{"derivedFrom":[makeQuery(id+"F14.boolean.opBoolean","MERGE",FACE,{"derivedFrom":[makeQuery(id+"F13.boolean.opBoolean","MERGE",FACE,{"derivedFrom":[makeQuery(id+"F12.boolean.opBoolean","MERGE",FACE,{"derivedFrom":[makeQuery(id+"F11.boolean.opBoolean","MERGE",FACE,{"derivedFrom":[makeQuery(id+"F10.boolean.opBoolean","MERGE",FACE,{"derivedFrom":[makeQuery(id+"F9.boolean.opBoolean","MERGE",FACE,{"derivedFrom":[makeQuery(id+"F8.boolean.opBoolean","MERGE",FACE,{"derivedFrom":[makeQuery(id+"F7.boolean.opBoolean","MERGE",FACE,{"derivedFrom":[makeQuery(id+"F6.boolean.opBoolean","MERGE",FACE,{"derivedFrom":[makeQuery(id+"F5.boolean.opBoolean","MERGE",FACE,{"derivedFrom":[makeQuery(id+"F1.opRevolve","SWEPT_FACE",FACE,{"disambiguationData":[OSD([sQuery(id+"F0.wireOp",EDGE,"E14")])]}),makeQuery(id+"F5.opLoft","CAP_FACE",FACE,{"disambiguationData":[OSD([makeQuery(id+"F4.imprint","IMPRINT",FACE,{"disambiguationData":[TD([[makeQuery(id+"F4.imprint","IMPRINT",EDGE,{"derivedFrom":sQuery(id+"F4.wireOp",EDGE,"E21")}),1.0]])]})])],"isStart":true})]}),makeQuery(id+"F6.opLoft","CAP_FACE",FACE,{"disambiguationData":[OSD([makeQuery(id+"F4.imprint","IMPRINT",FACE,{"disambiguationData":[TD([[makeQuery(id+"F4.imprint","IMPRINT",EDGE,{"derivedFrom":sQuery(id+"F4.wireOp",EDGE,"E26.15.0")}),1.0]])]})])],"isStart":true})]}),makeQuery(id+"F7.opLoft","CAP_FACE",FACE,{"disambiguationData":[OSD([makeQuery(id+"F4.imprint","IMPRINT",FACE,{"disambiguationData":[TD([[makeQuery(id+"F4.imprint","IMPRINT",EDGE,{"derivedFrom":sQuery(id+"F4.wireOp",EDGE,"E26.14.0")}),1.0]])]})])],"isStart":true})]}),makeQuery(id+"F8.opLoft","CAP_FACE",FACE,{"disambiguationData":[OSD([makeQuery(id+"F4.imprint","IMPRINT",FACE,{"disambiguationData":[TD([[makeQuery(id+"F4.imprint","IMPRINT",EDGE,{"derivedFrom":sQuery(id+"F4.wireOp",EDGE,"E26.13.0")}),1.0]])]})])],"isStart":true})]}),makeQuery(id+"F9.opLoft","CAP_FACE",FACE,{"disambiguationData":[OSD([makeQuery(id+"F4.imprint","IMPRINT",FACE,{"disambiguationData":[TD([[makeQuery(id+"F4.imprint","IMPRINT",EDGE,{"derivedFrom":sQuery(id+"F4.wireOp",EDGE,"E26.12.0")}),1.0]])]})])],"isStart":true})]}),makeQuery(id+"F10.opLoft","CAP_FACE",FACE,{"disambiguationData":[OSD([makeQuery(id+"F4.imprint","IMPRINT",FACE,{"disambiguationData":[TD([[makeQuery(id+"F4.imprint","IMPRINT",EDGE,{"derivedFrom":sQuery(id+"F4.wireOp",EDGE,"E26.11.0")}),1.0]])]})])],"isStart":true})]}),makeQuery(id+"F11.opLoft","CAP_FACE",FACE,{"disambiguationData":[OSD([makeQuery(id+"F4.imprint","IMPRINT",FACE,{"disambiguationData":[TD([[makeQuery(id+"F4.imprint","IMPRINT",EDGE,{"derivedFrom":sQuery(id+"F4.wireOp",EDGE,"E26.10.0")}),1.0]])]})])],"isStart":true})]}),makeQuery(id+"F12.opLoft","CAP_FACE",FACE,{"disambiguationData":[OSD([makeQuery(id+"F4.imprint","IMPRINT",FACE,{"disambiguationData":[TD([[makeQuery(id+"F4.imprint","IMPRINT",EDGE,{"derivedFrom":sQuery(id+"F4.wireOp",EDGE,"E26.9.0")}),1.0]])]})])],"isStart":true})]}),makeQuery(id+"F13.opLoft","CAP_FACE",FACE,{"disambiguationData":[OSD([makeQuery(id+"F4.imprint","IMPRINT",FACE,{"disambiguationData":[TD([[makeQuery(id+"F4.imprint","IMPRINT",EDGE,{"derivedFrom":sQuery(id+"F4.wireOp",EDGE,"E26.8.0")}),1.0]])]})])],"isStart":true})]}),makeQuery(id+"F14.opLoft","CAP_FACE",FACE,{"disambiguationData":[OSD([makeQuery(id+"F4.imprint","IMPRINT",FACE,{"disambiguationData":[TD([[makeQuery(id+"F4.imprint","IMPRINT",EDGE,{"derivedFrom":sQuery(id+"F4.wireOp",EDGE,"E26.7.0")}),1.0]])]})])],"isStart":true})]}),makeQuery(id+"F15.opLoft","CAP_FACE",FACE,{"disambiguationData":[OSD([makeQuery(id+"F4.imprint","IMPRINT",FACE,{"disambiguationData":[TD([[makeQuery(id+"F4.imprint","IMPRINT",EDGE,{"derivedFrom":sQuery(id+"F4.wireOp",EDGE,"E26.6.0")}),1.0]])]})])],"isStart":true})]}),makeQuery(id+"F16.opLoft","CAP_FACE",FACE,{"disambiguationData":[OSD([makeQuery(id+"F4.imprint","IMPRINT",FACE,{"disambiguationData":[TD([[makeQuery(id+"F4.imprint","IMPRINT",EDGE,{"derivedFrom":sQuery(id+"F4.wireOp",EDGE,"E26.5.0")}),1.0]])]})])],"isStart":true})]}),makeQuery(id+"F17.opLoft","CAP_FACE",FACE,{"disambiguationData":[OSD([makeQuery(id+"F4.imprint","IMPRINT",FACE,{"disambiguationData":[TD([[makeQuery(id+"F4.imprint","IMPRINT",EDGE,{"derivedFrom":sQuery(id+"F4.wireOp",EDGE,"E26.4.0")}),1.0]])]})])],"isStart":true})]}),makeQuery(id+"F18.opLoft","CAP_FACE",FACE,{"disambiguationData":[OSD([makeQuery(id+"F4.imprint","IMPRINT",FACE,{"disambiguationData":[TD([[makeQuery(id+"F4.imprint","IMPRINT",EDGE,{"derivedFrom":sQuery(id+"F4.wireOp",EDGE,"E26.3.0")}),1.0]])]})])],"isStart":true})]}),makeQuery(id+"F19.opLoft","CAP_FACE",FACE,{"disambiguationData":[OSD([makeQuery(id+"F4.imprint","IMPRINT",FACE,{"disambiguationData":[TD([[makeQuery(id+"F4.imprint","IMPRINT",EDGE,{"derivedFrom":sQuery(id+"F4.wireOp",EDGE,"E26.2.0")}),1.0]])]})])],"isStart":true})]}),makeQuery(id+"F20.opLoft","CAP_FACE",FACE,{"disambiguationData":[OSD([makeQuery(id+"F4.imprint","IMPRINT",FACE,{"disambiguationData":[TD([[makeQuery(id+"F4.imprint","IMPRINT",EDGE,{"derivedFrom":sQuery(id+"F4.wireOp",EDGE,"E26.1.0")}),1.0]])]})])],"isStart":true})]}),makeQuery(id+"F42.opRevolve","SWEPT_FACE",FACE,{"disambiguationData":[OSD([sQuery(id+"F41.wireOp",EDGE,"E32")])]})]});
            var Q6;
            Q6=makeQuery(id+"F42.boolean.opBoolean","INTERSECT",EDGE,{"disambiguationData":[OD(15.0)],"derivedFrom":[makeQuery(id+"F20.boolean.opBoolean","MERGE",FACE,{"derivedFrom":[makeQuery(id+"F19.boolean.opBoolean","MERGE",FACE,{"derivedFrom":[makeQuery(id+"F18.boolean.opBoolean","MERGE",FACE,{"derivedFrom":[makeQuery(id+"F17.boolean.opBoolean","MERGE",FACE,{"derivedFrom":[makeQuery(id+"F16.boolean.opBoolean","MERGE",FACE,{"derivedFrom":[makeQuery(id+"F15.boolean.opBoolean","MERGE",FACE,{"derivedFrom":[makeQuery(id+"F14.boolean.opBoolean","MERGE",FACE,{"derivedFrom":[makeQuery(id+"F13.boolean.opBoolean","MERGE",FACE,{"derivedFrom":[makeQuery(id+"F12.boolean.opBoolean","MERGE",FACE,{"derivedFrom":[makeQuery(id+"F11.boolean.opBoolean","MERGE",FACE,{"derivedFrom":[makeQuery(id+"F10.boolean.opBoolean","MERGE",FACE,{"derivedFrom":[makeQuery(id+"F9.boolean.opBoolean","MERGE",FACE,{"derivedFrom":[makeQuery(id+"F8.boolean.opBoolean","MERGE",FACE,{"derivedFrom":[makeQuery(id+"F7.boolean.opBoolean","MERGE",FACE,{"derivedFrom":[makeQuery(id+"F6.boolean.opBoolean","MERGE",FACE,{"derivedFrom":[makeQuery(id+"F5.boolean.opBoolean","MERGE",FACE,{"derivedFrom":[makeQuery(id+"F1.opRevolve","SWEPT_FACE",FACE,{"disambiguationData":[OSD([sQuery(id+"F0.wireOp",EDGE,"E14")])]}),makeQuery(id+"F5.opLoft","CAP_FACE",FACE,{"disambiguationData":[OSD([makeQuery(id+"F4.imprint","IMPRINT",FACE,{"disambiguationData":[TD([[makeQuery(id+"F4.imprint","IMPRINT",EDGE,{"derivedFrom":sQuery(id+"F4.wireOp",EDGE,"E21")}),1.0]])]})])],"isStart":true})]}),makeQuery(id+"F6.opLoft","CAP_FACE",FACE,{"disambiguationData":[OSD([makeQuery(id+"F4.imprint","IMPRINT",FACE,{"disambiguationData":[TD([[makeQuery(id+"F4.imprint","IMPRINT",EDGE,{"derivedFrom":sQuery(id+"F4.wireOp",EDGE,"E26.15.0")}),1.0]])]})])],"isStart":true})]}),makeQuery(id+"F7.opLoft","CAP_FACE",FACE,{"disambiguationData":[OSD([makeQuery(id+"F4.imprint","IMPRINT",FACE,{"disambiguationData":[TD([[makeQuery(id+"F4.imprint","IMPRINT",EDGE,{"derivedFrom":sQuery(id+"F4.wireOp",EDGE,"E26.14.0")}),1.0]])]})])],"isStart":true})]}),makeQuery(id+"F8.opLoft","CAP_FACE",FACE,{"disambiguationData":[OSD([makeQuery(id+"F4.imprint","IMPRINT",FACE,{"disambiguationData":[TD([[makeQuery(id+"F4.imprint","IMPRINT",EDGE,{"derivedFrom":sQuery(id+"F4.wireOp",EDGE,"E26.13.0")}),1.0]])]})])],"isStart":true})]}),makeQuery(id+"F9.opLoft","CAP_FACE",FACE,{"disambiguationData":[OSD([makeQuery(id+"F4.imprint","IMPRINT",FACE,{"disambiguationData":[TD([[makeQuery(id+"F4.imprint","IMPRINT",EDGE,{"derivedFrom":sQuery(id+"F4.wireOp",EDGE,"E26.12.0")}),1.0]])]})])],"isStart":true})]}),makeQuery(id+"F10.opLoft","CAP_FACE",FACE,{"disambiguationData":[OSD([makeQuery(id+"F4.imprint","IMPRINT",FACE,{"disambiguationData":[TD([[makeQuery(id+"F4.imprint","IMPRINT",EDGE,{"derivedFrom":sQuery(id+"F4.wireOp",EDGE,"E26.11.0")}),1.0]])]})])],"isStart":true})]}),makeQuery(id+"F11.opLoft","CAP_FACE",FACE,{"disambiguationData":[OSD([makeQuery(id+"F4.imprint","IMPRINT",FACE,{"disambiguationData":[TD([[makeQuery(id+"F4.imprint","IMPRINT",EDGE,{"derivedFrom":sQuery(id+"F4.wireOp",EDGE,"E26.10.0")}),1.0]])]})])],"isStart":true})]}),makeQuery(id+"F12.opLoft","CAP_FACE",FACE,{"disambiguationData":[OSD([makeQuery(id+"F4.imprint","IMPRINT",FACE,{"disambiguationData":[TD([[makeQuery(id+"F4.imprint","IMPRINT",EDGE,{"derivedFrom":sQuery(id+"F4.wireOp",EDGE,"E26.9.0")}),1.0]])]})])],"isStart":true})]}),makeQuery(id+"F13.opLoft","CAP_FACE",FACE,{"disambiguationData":[OSD([makeQuery(id+"F4.imprint","IMPRINT",FACE,{"disambiguationData":[TD([[makeQuery(id+"F4.imprint","IMPRINT",EDGE,{"derivedFrom":sQuery(id+"F4.wireOp",EDGE,"E26.8.0")}),1.0]])]})])],"isStart":true})]}),makeQuery(id+"F14.opLoft","CAP_FACE",FACE,{"disambiguationData":[OSD([makeQuery(id+"F4.imprint","IMPRINT",FACE,{"disambiguationData":[TD([[makeQuery(id+"F4.imprint","IMPRINT",EDGE,{"derivedFrom":sQuery(id+"F4.wireOp",EDGE,"E26.7.0")}),1.0]])]})])],"isStart":true})]}),makeQuery(id+"F15.opLoft","CAP_FACE",FACE,{"disambiguationData":[OSD([makeQuery(id+"F4.imprint","IMPRINT",FACE,{"disambiguationData":[TD([[makeQuery(id+"F4.imprint","IMPRINT",EDGE,{"derivedFrom":sQuery(id+"F4.wireOp",EDGE,"E26.6.0")}),1.0]])]})])],"isStart":true})]}),makeQuery(id+"F16.opLoft","CAP_FACE",FACE,{"disambiguationData":[OSD([makeQuery(id+"F4.imprint","IMPRINT",FACE,{"disambiguationData":[TD([[makeQuery(id+"F4.imprint","IMPRINT",EDGE,{"derivedFrom":sQuery(id+"F4.wireOp",EDGE,"E26.5.0")}),1.0]])]})])],"isStart":true})]}),makeQuery(id+"F17.opLoft","CAP_FACE",FACE,{"disambiguationData":[OSD([makeQuery(id+"F4.imprint","IMPRINT",FACE,{"disambiguationData":[TD([[makeQuery(id+"F4.imprint","IMPRINT",EDGE,{"derivedFrom":sQuery(id+"F4.wireOp",EDGE,"E26.4.0")}),1.0]])]})])],"isStart":true})]}),makeQuery(id+"F18.opLoft","CAP_FACE",FACE,{"disambiguationData":[OSD([makeQuery(id+"F4.imprint","IMPRINT",FACE,{"disambiguationData":[TD([[makeQuery(id+"F4.imprint","IMPRINT",EDGE,{"derivedFrom":sQuery(id+"F4.wireOp",EDGE,"E26.3.0")}),1.0]])]})])],"isStart":true})]}),makeQuery(id+"F19.opLoft","CAP_FACE",FACE,{"disambiguationData":[OSD([makeQuery(id+"F4.imprint","IMPRINT",FACE,{"disambiguationData":[TD([[makeQuery(id+"F4.imprint","IMPRINT",EDGE,{"derivedFrom":sQuery(id+"F4.wireOp",EDGE,"E26.2.0")}),1.0]])]})])],"isStart":true})]}),makeQuery(id+"F20.opLoft","CAP_FACE",FACE,{"disambiguationData":[OSD([makeQuery(id+"F4.imprint","IMPRINT",FACE,{"disambiguationData":[TD([[makeQuery(id+"F4.imprint","IMPRINT",EDGE,{"derivedFrom":sQuery(id+"F4.wireOp",EDGE,"E26.1.0")}),1.0]])]})])],"isStart":true})]}),makeQuery(id+"F42.opRevolve","SWEPT_FACE",FACE,{"disambiguationData":[OSD([sQuery(id+"F41.wireOp",EDGE,"E32")])]})]});
            var Q7;
            Q7=makeQuery(id+"F42.boolean.opBoolean","INTERSECT",EDGE,{"disambiguationData":[OD(14.0)],"derivedFrom":[makeQuery(id+"F20.boolean.opBoolean","MERGE",FACE,{"derivedFrom":[makeQuery(id+"F19.boolean.opBoolean","MERGE",FACE,{"derivedFrom":[makeQuery(id+"F18.boolean.opBoolean","MERGE",FACE,{"derivedFrom":[makeQuery(id+"F17.boolean.opBoolean","MERGE",FACE,{"derivedFrom":[makeQuery(id+"F16.boolean.opBoolean","MERGE",FACE,{"derivedFrom":[makeQuery(id+"F15.boolean.opBoolean","MERGE",FACE,{"derivedFrom":[makeQuery(id+"F14.boolean.opBoolean","MERGE",FACE,{"derivedFrom":[makeQuery(id+"F13.boolean.opBoolean","MERGE",FACE,{"derivedFrom":[makeQuery(id+"F12.boolean.opBoolean","MERGE",FACE,{"derivedFrom":[makeQuery(id+"F11.boolean.opBoolean","MERGE",FACE,{"derivedFrom":[makeQuery(id+"F10.boolean.opBoolean","MERGE",FACE,{"derivedFrom":[makeQuery(id+"F9.boolean.opBoolean","MERGE",FACE,{"derivedFrom":[makeQuery(id+"F8.boolean.opBoolean","MERGE",FACE,{"derivedFrom":[makeQuery(id+"F7.boolean.opBoolean","MERGE",FACE,{"derivedFrom":[makeQuery(id+"F6.boolean.opBoolean","MERGE",FACE,{"derivedFrom":[makeQuery(id+"F5.boolean.opBoolean","MERGE",FACE,{"derivedFrom":[makeQuery(id+"F1.opRevolve","SWEPT_FACE",FACE,{"disambiguationData":[OSD([sQuery(id+"F0.wireOp",EDGE,"E14")])]}),makeQuery(id+"F5.opLoft","CAP_FACE",FACE,{"disambiguationData":[OSD([makeQuery(id+"F4.imprint","IMPRINT",FACE,{"disambiguationData":[TD([[makeQuery(id+"F4.imprint","IMPRINT",EDGE,{"derivedFrom":sQuery(id+"F4.wireOp",EDGE,"E21")}),1.0]])]})])],"isStart":true})]}),makeQuery(id+"F6.opLoft","CAP_FACE",FACE,{"disambiguationData":[OSD([makeQuery(id+"F4.imprint","IMPRINT",FACE,{"disambiguationData":[TD([[makeQuery(id+"F4.imprint","IMPRINT",EDGE,{"derivedFrom":sQuery(id+"F4.wireOp",EDGE,"E26.15.0")}),1.0]])]})])],"isStart":true})]}),makeQuery(id+"F7.opLoft","CAP_FACE",FACE,{"disambiguationData":[OSD([makeQuery(id+"F4.imprint","IMPRINT",FACE,{"disambiguationData":[TD([[makeQuery(id+"F4.imprint","IMPRINT",EDGE,{"derivedFrom":sQuery(id+"F4.wireOp",EDGE,"E26.14.0")}),1.0]])]})])],"isStart":true})]}),makeQuery(id+"F8.opLoft","CAP_FACE",FACE,{"disambiguationData":[OSD([makeQuery(id+"F4.imprint","IMPRINT",FACE,{"disambiguationData":[TD([[makeQuery(id+"F4.imprint","IMPRINT",EDGE,{"derivedFrom":sQuery(id+"F4.wireOp",EDGE,"E26.13.0")}),1.0]])]})])],"isStart":true})]}),makeQuery(id+"F9.opLoft","CAP_FACE",FACE,{"disambiguationData":[OSD([makeQuery(id+"F4.imprint","IMPRINT",FACE,{"disambiguationData":[TD([[makeQuery(id+"F4.imprint","IMPRINT",EDGE,{"derivedFrom":sQuery(id+"F4.wireOp",EDGE,"E26.12.0")}),1.0]])]})])],"isStart":true})]}),makeQuery(id+"F10.opLoft","CAP_FACE",FACE,{"disambiguationData":[OSD([makeQuery(id+"F4.imprint","IMPRINT",FACE,{"disambiguationData":[TD([[makeQuery(id+"F4.imprint","IMPRINT",EDGE,{"derivedFrom":sQuery(id+"F4.wireOp",EDGE,"E26.11.0")}),1.0]])]})])],"isStart":true})]}),makeQuery(id+"F11.opLoft","CAP_FACE",FACE,{"disambiguationData":[OSD([makeQuery(id+"F4.imprint","IMPRINT",FACE,{"disambiguationData":[TD([[makeQuery(id+"F4.imprint","IMPRINT",EDGE,{"derivedFrom":sQuery(id+"F4.wireOp",EDGE,"E26.10.0")}),1.0]])]})])],"isStart":true})]}),makeQuery(id+"F12.opLoft","CAP_FACE",FACE,{"disambiguationData":[OSD([makeQuery(id+"F4.imprint","IMPRINT",FACE,{"disambiguationData":[TD([[makeQuery(id+"F4.imprint","IMPRINT",EDGE,{"derivedFrom":sQuery(id+"F4.wireOp",EDGE,"E26.9.0")}),1.0]])]})])],"isStart":true})]}),makeQuery(id+"F13.opLoft","CAP_FACE",FACE,{"disambiguationData":[OSD([makeQuery(id+"F4.imprint","IMPRINT",FACE,{"disambiguationData":[TD([[makeQuery(id+"F4.imprint","IMPRINT",EDGE,{"derivedFrom":sQuery(id+"F4.wireOp",EDGE,"E26.8.0")}),1.0]])]})])],"isStart":true})]}),makeQuery(id+"F14.opLoft","CAP_FACE",FACE,{"disambiguationData":[OSD([makeQuery(id+"F4.imprint","IMPRINT",FACE,{"disambiguationData":[TD([[makeQuery(id+"F4.imprint","IMPRINT",EDGE,{"derivedFrom":sQuery(id+"F4.wireOp",EDGE,"E26.7.0")}),1.0]])]})])],"isStart":true})]}),makeQuery(id+"F15.opLoft","CAP_FACE",FACE,{"disambiguationData":[OSD([makeQuery(id+"F4.imprint","IMPRINT",FACE,{"disambiguationData":[TD([[makeQuery(id+"F4.imprint","IMPRINT",EDGE,{"derivedFrom":sQuery(id+"F4.wireOp",EDGE,"E26.6.0")}),1.0]])]})])],"isStart":true})]}),makeQuery(id+"F16.opLoft","CAP_FACE",FACE,{"disambiguationData":[OSD([makeQuery(id+"F4.imprint","IMPRINT",FACE,{"disambiguationData":[TD([[makeQuery(id+"F4.imprint","IMPRINT",EDGE,{"derivedFrom":sQuery(id+"F4.wireOp",EDGE,"E26.5.0")}),1.0]])]})])],"isStart":true})]}),makeQuery(id+"F17.opLoft","CAP_FACE",FACE,{"disambiguationData":[OSD([makeQuery(id+"F4.imprint","IMPRINT",FACE,{"disambiguationData":[TD([[makeQuery(id+"F4.imprint","IMPRINT",EDGE,{"derivedFrom":sQuery(id+"F4.wireOp",EDGE,"E26.4.0")}),1.0]])]})])],"isStart":true})]}),makeQuery(id+"F18.opLoft","CAP_FACE",FACE,{"disambiguationData":[OSD([makeQuery(id+"F4.imprint","IMPRINT",FACE,{"disambiguationData":[TD([[makeQuery(id+"F4.imprint","IMPRINT",EDGE,{"derivedFrom":sQuery(id+"F4.wireOp",EDGE,"E26.3.0")}),1.0]])]})])],"isStart":true})]}),makeQuery(id+"F19.opLoft","CAP_FACE",FACE,{"disambiguationData":[OSD([makeQuery(id+"F4.imprint","IMPRINT",FACE,{"disambiguationData":[TD([[makeQuery(id+"F4.imprint","IMPRINT",EDGE,{"derivedFrom":sQuery(id+"F4.wireOp",EDGE,"E26.2.0")}),1.0]])]})])],"isStart":true})]}),makeQuery(id+"F20.opLoft","CAP_FACE",FACE,{"disambiguationData":[OSD([makeQuery(id+"F4.imprint","IMPRINT",FACE,{"disambiguationData":[TD([[makeQuery(id+"F4.imprint","IMPRINT",EDGE,{"derivedFrom":sQuery(id+"F4.wireOp",EDGE,"E26.1.0")}),1.0]])]})])],"isStart":true})]}),makeQuery(id+"F42.opRevolve","SWEPT_FACE",FACE,{"disambiguationData":[OSD([sQuery(id+"F41.wireOp",EDGE,"E32")])]})]});
            var Q8;
            Q8=makeQuery(id+"F42.boolean.opBoolean","INTERSECT",EDGE,{"disambiguationData":[OD(13.0)],"derivedFrom":[makeQuery(id+"F20.boolean.opBoolean","MERGE",FACE,{"derivedFrom":[makeQuery(id+"F19.boolean.opBoolean","MERGE",FACE,{"derivedFrom":[makeQuery(id+"F18.boolean.opBoolean","MERGE",FACE,{"derivedFrom":[makeQuery(id+"F17.boolean.opBoolean","MERGE",FACE,{"derivedFrom":[makeQuery(id+"F16.boolean.opBoolean","MERGE",FACE,{"derivedFrom":[makeQuery(id+"F15.boolean.opBoolean","MERGE",FACE,{"derivedFrom":[makeQuery(id+"F14.boolean.opBoolean","MERGE",FACE,{"derivedFrom":[makeQuery(id+"F13.boolean.opBoolean","MERGE",FACE,{"derivedFrom":[makeQuery(id+"F12.boolean.opBoolean","MERGE",FACE,{"derivedFrom":[makeQuery(id+"F11.boolean.opBoolean","MERGE",FACE,{"derivedFrom":[makeQuery(id+"F10.boolean.opBoolean","MERGE",FACE,{"derivedFrom":[makeQuery(id+"F9.boolean.opBoolean","MERGE",FACE,{"derivedFrom":[makeQuery(id+"F8.boolean.opBoolean","MERGE",FACE,{"derivedFrom":[makeQuery(id+"F7.boolean.opBoolean","MERGE",FACE,{"derivedFrom":[makeQuery(id+"F6.boolean.opBoolean","MERGE",FACE,{"derivedFrom":[makeQuery(id+"F5.boolean.opBoolean","MERGE",FACE,{"derivedFrom":[makeQuery(id+"F1.opRevolve","SWEPT_FACE",FACE,{"disambiguationData":[OSD([sQuery(id+"F0.wireOp",EDGE,"E14")])]}),makeQuery(id+"F5.opLoft","CAP_FACE",FACE,{"disambiguationData":[OSD([makeQuery(id+"F4.imprint","IMPRINT",FACE,{"disambiguationData":[TD([[makeQuery(id+"F4.imprint","IMPRINT",EDGE,{"derivedFrom":sQuery(id+"F4.wireOp",EDGE,"E21")}),1.0]])]})])],"isStart":true})]}),makeQuery(id+"F6.opLoft","CAP_FACE",FACE,{"disambiguationData":[OSD([makeQuery(id+"F4.imprint","IMPRINT",FACE,{"disambiguationData":[TD([[makeQuery(id+"F4.imprint","IMPRINT",EDGE,{"derivedFrom":sQuery(id+"F4.wireOp",EDGE,"E26.15.0")}),1.0]])]})])],"isStart":true})]}),makeQuery(id+"F7.opLoft","CAP_FACE",FACE,{"disambiguationData":[OSD([makeQuery(id+"F4.imprint","IMPRINT",FACE,{"disambiguationData":[TD([[makeQuery(id+"F4.imprint","IMPRINT",EDGE,{"derivedFrom":sQuery(id+"F4.wireOp",EDGE,"E26.14.0")}),1.0]])]})])],"isStart":true})]}),makeQuery(id+"F8.opLoft","CAP_FACE",FACE,{"disambiguationData":[OSD([makeQuery(id+"F4.imprint","IMPRINT",FACE,{"disambiguationData":[TD([[makeQuery(id+"F4.imprint","IMPRINT",EDGE,{"derivedFrom":sQuery(id+"F4.wireOp",EDGE,"E26.13.0")}),1.0]])]})])],"isStart":true})]}),makeQuery(id+"F9.opLoft","CAP_FACE",FACE,{"disambiguationData":[OSD([makeQuery(id+"F4.imprint","IMPRINT",FACE,{"disambiguationData":[TD([[makeQuery(id+"F4.imprint","IMPRINT",EDGE,{"derivedFrom":sQuery(id+"F4.wireOp",EDGE,"E26.12.0")}),1.0]])]})])],"isStart":true})]}),makeQuery(id+"F10.opLoft","CAP_FACE",FACE,{"disambiguationData":[OSD([makeQuery(id+"F4.imprint","IMPRINT",FACE,{"disambiguationData":[TD([[makeQuery(id+"F4.imprint","IMPRINT",EDGE,{"derivedFrom":sQuery(id+"F4.wireOp",EDGE,"E26.11.0")}),1.0]])]})])],"isStart":true})]}),makeQuery(id+"F11.opLoft","CAP_FACE",FACE,{"disambiguationData":[OSD([makeQuery(id+"F4.imprint","IMPRINT",FACE,{"disambiguationData":[TD([[makeQuery(id+"F4.imprint","IMPRINT",EDGE,{"derivedFrom":sQuery(id+"F4.wireOp",EDGE,"E26.10.0")}),1.0]])]})])],"isStart":true})]}),makeQuery(id+"F12.opLoft","CAP_FACE",FACE,{"disambiguationData":[OSD([makeQuery(id+"F4.imprint","IMPRINT",FACE,{"disambiguationData":[TD([[makeQuery(id+"F4.imprint","IMPRINT",EDGE,{"derivedFrom":sQuery(id+"F4.wireOp",EDGE,"E26.9.0")}),1.0]])]})])],"isStart":true})]}),makeQuery(id+"F13.opLoft","CAP_FACE",FACE,{"disambiguationData":[OSD([makeQuery(id+"F4.imprint","IMPRINT",FACE,{"disambiguationData":[TD([[makeQuery(id+"F4.imprint","IMPRINT",EDGE,{"derivedFrom":sQuery(id+"F4.wireOp",EDGE,"E26.8.0")}),1.0]])]})])],"isStart":true})]}),makeQuery(id+"F14.opLoft","CAP_FACE",FACE,{"disambiguationData":[OSD([makeQuery(id+"F4.imprint","IMPRINT",FACE,{"disambiguationData":[TD([[makeQuery(id+"F4.imprint","IMPRINT",EDGE,{"derivedFrom":sQuery(id+"F4.wireOp",EDGE,"E26.7.0")}),1.0]])]})])],"isStart":true})]}),makeQuery(id+"F15.opLoft","CAP_FACE",FACE,{"disambiguationData":[OSD([makeQuery(id+"F4.imprint","IMPRINT",FACE,{"disambiguationData":[TD([[makeQuery(id+"F4.imprint","IMPRINT",EDGE,{"derivedFrom":sQuery(id+"F4.wireOp",EDGE,"E26.6.0")}),1.0]])]})])],"isStart":true})]}),makeQuery(id+"F16.opLoft","CAP_FACE",FACE,{"disambiguationData":[OSD([makeQuery(id+"F4.imprint","IMPRINT",FACE,{"disambiguationData":[TD([[makeQuery(id+"F4.imprint","IMPRINT",EDGE,{"derivedFrom":sQuery(id+"F4.wireOp",EDGE,"E26.5.0")}),1.0]])]})])],"isStart":true})]}),makeQuery(id+"F17.opLoft","CAP_FACE",FACE,{"disambiguationData":[OSD([makeQuery(id+"F4.imprint","IMPRINT",FACE,{"disambiguationData":[TD([[makeQuery(id+"F4.imprint","IMPRINT",EDGE,{"derivedFrom":sQuery(id+"F4.wireOp",EDGE,"E26.4.0")}),1.0]])]})])],"isStart":true})]}),makeQuery(id+"F18.opLoft","CAP_FACE",FACE,{"disambiguationData":[OSD([makeQuery(id+"F4.imprint","IMPRINT",FACE,{"disambiguationData":[TD([[makeQuery(id+"F4.imprint","IMPRINT",EDGE,{"derivedFrom":sQuery(id+"F4.wireOp",EDGE,"E26.3.0")}),1.0]])]})])],"isStart":true})]}),makeQuery(id+"F19.opLoft","CAP_FACE",FACE,{"disambiguationData":[OSD([makeQuery(id+"F4.imprint","IMPRINT",FACE,{"disambiguationData":[TD([[makeQuery(id+"F4.imprint","IMPRINT",EDGE,{"derivedFrom":sQuery(id+"F4.wireOp",EDGE,"E26.2.0")}),1.0]])]})])],"isStart":true})]}),makeQuery(id+"F20.opLoft","CAP_FACE",FACE,{"disambiguationData":[OSD([makeQuery(id+"F4.imprint","IMPRINT",FACE,{"disambiguationData":[TD([[makeQuery(id+"F4.imprint","IMPRINT",EDGE,{"derivedFrom":sQuery(id+"F4.wireOp",EDGE,"E26.1.0")}),1.0]])]})])],"isStart":true})]}),makeQuery(id+"F42.opRevolve","SWEPT_FACE",FACE,{"disambiguationData":[OSD([sQuery(id+"F41.wireOp",EDGE,"E32")])]})]});
            var Q9;
            Q9=makeQuery(id+"F42.boolean.opBoolean","INTERSECT",EDGE,{"disambiguationData":[OD(12.0)],"derivedFrom":[makeQuery(id+"F20.boolean.opBoolean","MERGE",FACE,{"derivedFrom":[makeQuery(id+"F19.boolean.opBoolean","MERGE",FACE,{"derivedFrom":[makeQuery(id+"F18.boolean.opBoolean","MERGE",FACE,{"derivedFrom":[makeQuery(id+"F17.boolean.opBoolean","MERGE",FACE,{"derivedFrom":[makeQuery(id+"F16.boolean.opBoolean","MERGE",FACE,{"derivedFrom":[makeQuery(id+"F15.boolean.opBoolean","MERGE",FACE,{"derivedFrom":[makeQuery(id+"F14.boolean.opBoolean","MERGE",FACE,{"derivedFrom":[makeQuery(id+"F13.boolean.opBoolean","MERGE",FACE,{"derivedFrom":[makeQuery(id+"F12.boolean.opBoolean","MERGE",FACE,{"derivedFrom":[makeQuery(id+"F11.boolean.opBoolean","MERGE",FACE,{"derivedFrom":[makeQuery(id+"F10.boolean.opBoolean","MERGE",FACE,{"derivedFrom":[makeQuery(id+"F9.boolean.opBoolean","MERGE",FACE,{"derivedFrom":[makeQuery(id+"F8.boolean.opBoolean","MERGE",FACE,{"derivedFrom":[makeQuery(id+"F7.boolean.opBoolean","MERGE",FACE,{"derivedFrom":[makeQuery(id+"F6.boolean.opBoolean","MERGE",FACE,{"derivedFrom":[makeQuery(id+"F5.boolean.opBoolean","MERGE",FACE,{"derivedFrom":[makeQuery(id+"F1.opRevolve","SWEPT_FACE",FACE,{"disambiguationData":[OSD([sQuery(id+"F0.wireOp",EDGE,"E14")])]}),makeQuery(id+"F5.opLoft","CAP_FACE",FACE,{"disambiguationData":[OSD([makeQuery(id+"F4.imprint","IMPRINT",FACE,{"disambiguationData":[TD([[makeQuery(id+"F4.imprint","IMPRINT",EDGE,{"derivedFrom":sQuery(id+"F4.wireOp",EDGE,"E21")}),1.0]])]})])],"isStart":true})]}),makeQuery(id+"F6.opLoft","CAP_FACE",FACE,{"disambiguationData":[OSD([makeQuery(id+"F4.imprint","IMPRINT",FACE,{"disambiguationData":[TD([[makeQuery(id+"F4.imprint","IMPRINT",EDGE,{"derivedFrom":sQuery(id+"F4.wireOp",EDGE,"E26.15.0")}),1.0]])]})])],"isStart":true})]}),makeQuery(id+"F7.opLoft","CAP_FACE",FACE,{"disambiguationData":[OSD([makeQuery(id+"F4.imprint","IMPRINT",FACE,{"disambiguationData":[TD([[makeQuery(id+"F4.imprint","IMPRINT",EDGE,{"derivedFrom":sQuery(id+"F4.wireOp",EDGE,"E26.14.0")}),1.0]])]})])],"isStart":true})]}),makeQuery(id+"F8.opLoft","CAP_FACE",FACE,{"disambiguationData":[OSD([makeQuery(id+"F4.imprint","IMPRINT",FACE,{"disambiguationData":[TD([[makeQuery(id+"F4.imprint","IMPRINT",EDGE,{"derivedFrom":sQuery(id+"F4.wireOp",EDGE,"E26.13.0")}),1.0]])]})])],"isStart":true})]}),makeQuery(id+"F9.opLoft","CAP_FACE",FACE,{"disambiguationData":[OSD([makeQuery(id+"F4.imprint","IMPRINT",FACE,{"disambiguationData":[TD([[makeQuery(id+"F4.imprint","IMPRINT",EDGE,{"derivedFrom":sQuery(id+"F4.wireOp",EDGE,"E26.12.0")}),1.0]])]})])],"isStart":true})]}),makeQuery(id+"F10.opLoft","CAP_FACE",FACE,{"disambiguationData":[OSD([makeQuery(id+"F4.imprint","IMPRINT",FACE,{"disambiguationData":[TD([[makeQuery(id+"F4.imprint","IMPRINT",EDGE,{"derivedFrom":sQuery(id+"F4.wireOp",EDGE,"E26.11.0")}),1.0]])]})])],"isStart":true})]}),makeQuery(id+"F11.opLoft","CAP_FACE",FACE,{"disambiguationData":[OSD([makeQuery(id+"F4.imprint","IMPRINT",FACE,{"disambiguationData":[TD([[makeQuery(id+"F4.imprint","IMPRINT",EDGE,{"derivedFrom":sQuery(id+"F4.wireOp",EDGE,"E26.10.0")}),1.0]])]})])],"isStart":true})]}),makeQuery(id+"F12.opLoft","CAP_FACE",FACE,{"disambiguationData":[OSD([makeQuery(id+"F4.imprint","IMPRINT",FACE,{"disambiguationData":[TD([[makeQuery(id+"F4.imprint","IMPRINT",EDGE,{"derivedFrom":sQuery(id+"F4.wireOp",EDGE,"E26.9.0")}),1.0]])]})])],"isStart":true})]}),makeQuery(id+"F13.opLoft","CAP_FACE",FACE,{"disambiguationData":[OSD([makeQuery(id+"F4.imprint","IMPRINT",FACE,{"disambiguationData":[TD([[makeQuery(id+"F4.imprint","IMPRINT",EDGE,{"derivedFrom":sQuery(id+"F4.wireOp",EDGE,"E26.8.0")}),1.0]])]})])],"isStart":true})]}),makeQuery(id+"F14.opLoft","CAP_FACE",FACE,{"disambiguationData":[OSD([makeQuery(id+"F4.imprint","IMPRINT",FACE,{"disambiguationData":[TD([[makeQuery(id+"F4.imprint","IMPRINT",EDGE,{"derivedFrom":sQuery(id+"F4.wireOp",EDGE,"E26.7.0")}),1.0]])]})])],"isStart":true})]}),makeQuery(id+"F15.opLoft","CAP_FACE",FACE,{"disambiguationData":[OSD([makeQuery(id+"F4.imprint","IMPRINT",FACE,{"disambiguationData":[TD([[makeQuery(id+"F4.imprint","IMPRINT",EDGE,{"derivedFrom":sQuery(id+"F4.wireOp",EDGE,"E26.6.0")}),1.0]])]})])],"isStart":true})]}),makeQuery(id+"F16.opLoft","CAP_FACE",FACE,{"disambiguationData":[OSD([makeQuery(id+"F4.imprint","IMPRINT",FACE,{"disambiguationData":[TD([[makeQuery(id+"F4.imprint","IMPRINT",EDGE,{"derivedFrom":sQuery(id+"F4.wireOp",EDGE,"E26.5.0")}),1.0]])]})])],"isStart":true})]}),makeQuery(id+"F17.opLoft","CAP_FACE",FACE,{"disambiguationData":[OSD([makeQuery(id+"F4.imprint","IMPRINT",FACE,{"disambiguationData":[TD([[makeQuery(id+"F4.imprint","IMPRINT",EDGE,{"derivedFrom":sQuery(id+"F4.wireOp",EDGE,"E26.4.0")}),1.0]])]})])],"isStart":true})]}),makeQuery(id+"F18.opLoft","CAP_FACE",FACE,{"disambiguationData":[OSD([makeQuery(id+"F4.imprint","IMPRINT",FACE,{"disambiguationData":[TD([[makeQuery(id+"F4.imprint","IMPRINT",EDGE,{"derivedFrom":sQuery(id+"F4.wireOp",EDGE,"E26.3.0")}),1.0]])]})])],"isStart":true})]}),makeQuery(id+"F19.opLoft","CAP_FACE",FACE,{"disambiguationData":[OSD([makeQuery(id+"F4.imprint","IMPRINT",FACE,{"disambiguationData":[TD([[makeQuery(id+"F4.imprint","IMPRINT",EDGE,{"derivedFrom":sQuery(id+"F4.wireOp",EDGE,"E26.2.0")}),1.0]])]})])],"isStart":true})]}),makeQuery(id+"F20.opLoft","CAP_FACE",FACE,{"disambiguationData":[OSD([makeQuery(id+"F4.imprint","IMPRINT",FACE,{"disambiguationData":[TD([[makeQuery(id+"F4.imprint","IMPRINT",EDGE,{"derivedFrom":sQuery(id+"F4.wireOp",EDGE,"E26.1.0")}),1.0]])]})])],"isStart":true})]}),makeQuery(id+"F42.opRevolve","SWEPT_FACE",FACE,{"disambiguationData":[OSD([sQuery(id+"F41.wireOp",EDGE,"E32")])]})]});
            var Q10;
            Q10=makeQuery(id+"F42.boolean.opBoolean","INTERSECT",EDGE,{"disambiguationData":[OD(11.0)],"derivedFrom":[makeQuery(id+"F20.boolean.opBoolean","MERGE",FACE,{"derivedFrom":[makeQuery(id+"F19.boolean.opBoolean","MERGE",FACE,{"derivedFrom":[makeQuery(id+"F18.boolean.opBoolean","MERGE",FACE,{"derivedFrom":[makeQuery(id+"F17.boolean.opBoolean","MERGE",FACE,{"derivedFrom":[makeQuery(id+"F16.boolean.opBoolean","MERGE",FACE,{"derivedFrom":[makeQuery(id+"F15.boolean.opBoolean","MERGE",FACE,{"derivedFrom":[makeQuery(id+"F14.boolean.opBoolean","MERGE",FACE,{"derivedFrom":[makeQuery(id+"F13.boolean.opBoolean","MERGE",FACE,{"derivedFrom":[makeQuery(id+"F12.boolean.opBoolean","MERGE",FACE,{"derivedFrom":[makeQuery(id+"F11.boolean.opBoolean","MERGE",FACE,{"derivedFrom":[makeQuery(id+"F10.boolean.opBoolean","MERGE",FACE,{"derivedFrom":[makeQuery(id+"F9.boolean.opBoolean","MERGE",FACE,{"derivedFrom":[makeQuery(id+"F8.boolean.opBoolean","MERGE",FACE,{"derivedFrom":[makeQuery(id+"F7.boolean.opBoolean","MERGE",FACE,{"derivedFrom":[makeQuery(id+"F6.boolean.opBoolean","MERGE",FACE,{"derivedFrom":[makeQuery(id+"F5.boolean.opBoolean","MERGE",FACE,{"derivedFrom":[makeQuery(id+"F1.opRevolve","SWEPT_FACE",FACE,{"disambiguationData":[OSD([sQuery(id+"F0.wireOp",EDGE,"E14")])]}),makeQuery(id+"F5.opLoft","CAP_FACE",FACE,{"disambiguationData":[OSD([makeQuery(id+"F4.imprint","IMPRINT",FACE,{"disambiguationData":[TD([[makeQuery(id+"F4.imprint","IMPRINT",EDGE,{"derivedFrom":sQuery(id+"F4.wireOp",EDGE,"E21")}),1.0]])]})])],"isStart":true})]}),makeQuery(id+"F6.opLoft","CAP_FACE",FACE,{"disambiguationData":[OSD([makeQuery(id+"F4.imprint","IMPRINT",FACE,{"disambiguationData":[TD([[makeQuery(id+"F4.imprint","IMPRINT",EDGE,{"derivedFrom":sQuery(id+"F4.wireOp",EDGE,"E26.15.0")}),1.0]])]})])],"isStart":true})]}),makeQuery(id+"F7.opLoft","CAP_FACE",FACE,{"disambiguationData":[OSD([makeQuery(id+"F4.imprint","IMPRINT",FACE,{"disambiguationData":[TD([[makeQuery(id+"F4.imprint","IMPRINT",EDGE,{"derivedFrom":sQuery(id+"F4.wireOp",EDGE,"E26.14.0")}),1.0]])]})])],"isStart":true})]}),makeQuery(id+"F8.opLoft","CAP_FACE",FACE,{"disambiguationData":[OSD([makeQuery(id+"F4.imprint","IMPRINT",FACE,{"disambiguationData":[TD([[makeQuery(id+"F4.imprint","IMPRINT",EDGE,{"derivedFrom":sQuery(id+"F4.wireOp",EDGE,"E26.13.0")}),1.0]])]})])],"isStart":true})]}),makeQuery(id+"F9.opLoft","CAP_FACE",FACE,{"disambiguationData":[OSD([makeQuery(id+"F4.imprint","IMPRINT",FACE,{"disambiguationData":[TD([[makeQuery(id+"F4.imprint","IMPRINT",EDGE,{"derivedFrom":sQuery(id+"F4.wireOp",EDGE,"E26.12.0")}),1.0]])]})])],"isStart":true})]}),makeQuery(id+"F10.opLoft","CAP_FACE",FACE,{"disambiguationData":[OSD([makeQuery(id+"F4.imprint","IMPRINT",FACE,{"disambiguationData":[TD([[makeQuery(id+"F4.imprint","IMPRINT",EDGE,{"derivedFrom":sQuery(id+"F4.wireOp",EDGE,"E26.11.0")}),1.0]])]})])],"isStart":true})]}),makeQuery(id+"F11.opLoft","CAP_FACE",FACE,{"disambiguationData":[OSD([makeQuery(id+"F4.imprint","IMPRINT",FACE,{"disambiguationData":[TD([[makeQuery(id+"F4.imprint","IMPRINT",EDGE,{"derivedFrom":sQuery(id+"F4.wireOp",EDGE,"E26.10.0")}),1.0]])]})])],"isStart":true})]}),makeQuery(id+"F12.opLoft","CAP_FACE",FACE,{"disambiguationData":[OSD([makeQuery(id+"F4.imprint","IMPRINT",FACE,{"disambiguationData":[TD([[makeQuery(id+"F4.imprint","IMPRINT",EDGE,{"derivedFrom":sQuery(id+"F4.wireOp",EDGE,"E26.9.0")}),1.0]])]})])],"isStart":true})]}),makeQuery(id+"F13.opLoft","CAP_FACE",FACE,{"disambiguationData":[OSD([makeQuery(id+"F4.imprint","IMPRINT",FACE,{"disambiguationData":[TD([[makeQuery(id+"F4.imprint","IMPRINT",EDGE,{"derivedFrom":sQuery(id+"F4.wireOp",EDGE,"E26.8.0")}),1.0]])]})])],"isStart":true})]}),makeQuery(id+"F14.opLoft","CAP_FACE",FACE,{"disambiguationData":[OSD([makeQuery(id+"F4.imprint","IMPRINT",FACE,{"disambiguationData":[TD([[makeQuery(id+"F4.imprint","IMPRINT",EDGE,{"derivedFrom":sQuery(id+"F4.wireOp",EDGE,"E26.7.0")}),1.0]])]})])],"isStart":true})]}),makeQuery(id+"F15.opLoft","CAP_FACE",FACE,{"disambiguationData":[OSD([makeQuery(id+"F4.imprint","IMPRINT",FACE,{"disambiguationData":[TD([[makeQuery(id+"F4.imprint","IMPRINT",EDGE,{"derivedFrom":sQuery(id+"F4.wireOp",EDGE,"E26.6.0")}),1.0]])]})])],"isStart":true})]}),makeQuery(id+"F16.opLoft","CAP_FACE",FACE,{"disambiguationData":[OSD([makeQuery(id+"F4.imprint","IMPRINT",FACE,{"disambiguationData":[TD([[makeQuery(id+"F4.imprint","IMPRINT",EDGE,{"derivedFrom":sQuery(id+"F4.wireOp",EDGE,"E26.5.0")}),1.0]])]})])],"isStart":true})]}),makeQuery(id+"F17.opLoft","CAP_FACE",FACE,{"disambiguationData":[OSD([makeQuery(id+"F4.imprint","IMPRINT",FACE,{"disambiguationData":[TD([[makeQuery(id+"F4.imprint","IMPRINT",EDGE,{"derivedFrom":sQuery(id+"F4.wireOp",EDGE,"E26.4.0")}),1.0]])]})])],"isStart":true})]}),makeQuery(id+"F18.opLoft","CAP_FACE",FACE,{"disambiguationData":[OSD([makeQuery(id+"F4.imprint","IMPRINT",FACE,{"disambiguationData":[TD([[makeQuery(id+"F4.imprint","IMPRINT",EDGE,{"derivedFrom":sQuery(id+"F4.wireOp",EDGE,"E26.3.0")}),1.0]])]})])],"isStart":true})]}),makeQuery(id+"F19.opLoft","CAP_FACE",FACE,{"disambiguationData":[OSD([makeQuery(id+"F4.imprint","IMPRINT",FACE,{"disambiguationData":[TD([[makeQuery(id+"F4.imprint","IMPRINT",EDGE,{"derivedFrom":sQuery(id+"F4.wireOp",EDGE,"E26.2.0")}),1.0]])]})])],"isStart":true})]}),makeQuery(id+"F20.opLoft","CAP_FACE",FACE,{"disambiguationData":[OSD([makeQuery(id+"F4.imprint","IMPRINT",FACE,{"disambiguationData":[TD([[makeQuery(id+"F4.imprint","IMPRINT",EDGE,{"derivedFrom":sQuery(id+"F4.wireOp",EDGE,"E26.1.0")}),1.0]])]})])],"isStart":true})]}),makeQuery(id+"F42.opRevolve","SWEPT_FACE",FACE,{"disambiguationData":[OSD([sQuery(id+"F41.wireOp",EDGE,"E32")])]})]});
            var Q11;
            Q11=makeQuery(id+"F42.boolean.opBoolean","INTERSECT",EDGE,{"disambiguationData":[OD(10.0)],"derivedFrom":[makeQuery(id+"F20.boolean.opBoolean","MERGE",FACE,{"derivedFrom":[makeQuery(id+"F19.boolean.opBoolean","MERGE",FACE,{"derivedFrom":[makeQuery(id+"F18.boolean.opBoolean","MERGE",FACE,{"derivedFrom":[makeQuery(id+"F17.boolean.opBoolean","MERGE",FACE,{"derivedFrom":[makeQuery(id+"F16.boolean.opBoolean","MERGE",FACE,{"derivedFrom":[makeQuery(id+"F15.boolean.opBoolean","MERGE",FACE,{"derivedFrom":[makeQuery(id+"F14.boolean.opBoolean","MERGE",FACE,{"derivedFrom":[makeQuery(id+"F13.boolean.opBoolean","MERGE",FACE,{"derivedFrom":[makeQuery(id+"F12.boolean.opBoolean","MERGE",FACE,{"derivedFrom":[makeQuery(id+"F11.boolean.opBoolean","MERGE",FACE,{"derivedFrom":[makeQuery(id+"F10.boolean.opBoolean","MERGE",FACE,{"derivedFrom":[makeQuery(id+"F9.boolean.opBoolean","MERGE",FACE,{"derivedFrom":[makeQuery(id+"F8.boolean.opBoolean","MERGE",FACE,{"derivedFrom":[makeQuery(id+"F7.boolean.opBoolean","MERGE",FACE,{"derivedFrom":[makeQuery(id+"F6.boolean.opBoolean","MERGE",FACE,{"derivedFrom":[makeQuery(id+"F5.boolean.opBoolean","MERGE",FACE,{"derivedFrom":[makeQuery(id+"F1.opRevolve","SWEPT_FACE",FACE,{"disambiguationData":[OSD([sQuery(id+"F0.wireOp",EDGE,"E14")])]}),makeQuery(id+"F5.opLoft","CAP_FACE",FACE,{"disambiguationData":[OSD([makeQuery(id+"F4.imprint","IMPRINT",FACE,{"disambiguationData":[TD([[makeQuery(id+"F4.imprint","IMPRINT",EDGE,{"derivedFrom":sQuery(id+"F4.wireOp",EDGE,"E21")}),1.0]])]})])],"isStart":true})]}),makeQuery(id+"F6.opLoft","CAP_FACE",FACE,{"disambiguationData":[OSD([makeQuery(id+"F4.imprint","IMPRINT",FACE,{"disambiguationData":[TD([[makeQuery(id+"F4.imprint","IMPRINT",EDGE,{"derivedFrom":sQuery(id+"F4.wireOp",EDGE,"E26.15.0")}),1.0]])]})])],"isStart":true})]}),makeQuery(id+"F7.opLoft","CAP_FACE",FACE,{"disambiguationData":[OSD([makeQuery(id+"F4.imprint","IMPRINT",FACE,{"disambiguationData":[TD([[makeQuery(id+"F4.imprint","IMPRINT",EDGE,{"derivedFrom":sQuery(id+"F4.wireOp",EDGE,"E26.14.0")}),1.0]])]})])],"isStart":true})]}),makeQuery(id+"F8.opLoft","CAP_FACE",FACE,{"disambiguationData":[OSD([makeQuery(id+"F4.imprint","IMPRINT",FACE,{"disambiguationData":[TD([[makeQuery(id+"F4.imprint","IMPRINT",EDGE,{"derivedFrom":sQuery(id+"F4.wireOp",EDGE,"E26.13.0")}),1.0]])]})])],"isStart":true})]}),makeQuery(id+"F9.opLoft","CAP_FACE",FACE,{"disambiguationData":[OSD([makeQuery(id+"F4.imprint","IMPRINT",FACE,{"disambiguationData":[TD([[makeQuery(id+"F4.imprint","IMPRINT",EDGE,{"derivedFrom":sQuery(id+"F4.wireOp",EDGE,"E26.12.0")}),1.0]])]})])],"isStart":true})]}),makeQuery(id+"F10.opLoft","CAP_FACE",FACE,{"disambiguationData":[OSD([makeQuery(id+"F4.imprint","IMPRINT",FACE,{"disambiguationData":[TD([[makeQuery(id+"F4.imprint","IMPRINT",EDGE,{"derivedFrom":sQuery(id+"F4.wireOp",EDGE,"E26.11.0")}),1.0]])]})])],"isStart":true})]}),makeQuery(id+"F11.opLoft","CAP_FACE",FACE,{"disambiguationData":[OSD([makeQuery(id+"F4.imprint","IMPRINT",FACE,{"disambiguationData":[TD([[makeQuery(id+"F4.imprint","IMPRINT",EDGE,{"derivedFrom":sQuery(id+"F4.wireOp",EDGE,"E26.10.0")}),1.0]])]})])],"isStart":true})]}),makeQuery(id+"F12.opLoft","CAP_FACE",FACE,{"disambiguationData":[OSD([makeQuery(id+"F4.imprint","IMPRINT",FACE,{"disambiguationData":[TD([[makeQuery(id+"F4.imprint","IMPRINT",EDGE,{"derivedFrom":sQuery(id+"F4.wireOp",EDGE,"E26.9.0")}),1.0]])]})])],"isStart":true})]}),makeQuery(id+"F13.opLoft","CAP_FACE",FACE,{"disambiguationData":[OSD([makeQuery(id+"F4.imprint","IMPRINT",FACE,{"disambiguationData":[TD([[makeQuery(id+"F4.imprint","IMPRINT",EDGE,{"derivedFrom":sQuery(id+"F4.wireOp",EDGE,"E26.8.0")}),1.0]])]})])],"isStart":true})]}),makeQuery(id+"F14.opLoft","CAP_FACE",FACE,{"disambiguationData":[OSD([makeQuery(id+"F4.imprint","IMPRINT",FACE,{"disambiguationData":[TD([[makeQuery(id+"F4.imprint","IMPRINT",EDGE,{"derivedFrom":sQuery(id+"F4.wireOp",EDGE,"E26.7.0")}),1.0]])]})])],"isStart":true})]}),makeQuery(id+"F15.opLoft","CAP_FACE",FACE,{"disambiguationData":[OSD([makeQuery(id+"F4.imprint","IMPRINT",FACE,{"disambiguationData":[TD([[makeQuery(id+"F4.imprint","IMPRINT",EDGE,{"derivedFrom":sQuery(id+"F4.wireOp",EDGE,"E26.6.0")}),1.0]])]})])],"isStart":true})]}),makeQuery(id+"F16.opLoft","CAP_FACE",FACE,{"disambiguationData":[OSD([makeQuery(id+"F4.imprint","IMPRINT",FACE,{"disambiguationData":[TD([[makeQuery(id+"F4.imprint","IMPRINT",EDGE,{"derivedFrom":sQuery(id+"F4.wireOp",EDGE,"E26.5.0")}),1.0]])]})])],"isStart":true})]}),makeQuery(id+"F17.opLoft","CAP_FACE",FACE,{"disambiguationData":[OSD([makeQuery(id+"F4.imprint","IMPRINT",FACE,{"disambiguationData":[TD([[makeQuery(id+"F4.imprint","IMPRINT",EDGE,{"derivedFrom":sQuery(id+"F4.wireOp",EDGE,"E26.4.0")}),1.0]])]})])],"isStart":true})]}),makeQuery(id+"F18.opLoft","CAP_FACE",FACE,{"disambiguationData":[OSD([makeQuery(id+"F4.imprint","IMPRINT",FACE,{"disambiguationData":[TD([[makeQuery(id+"F4.imprint","IMPRINT",EDGE,{"derivedFrom":sQuery(id+"F4.wireOp",EDGE,"E26.3.0")}),1.0]])]})])],"isStart":true})]}),makeQuery(id+"F19.opLoft","CAP_FACE",FACE,{"disambiguationData":[OSD([makeQuery(id+"F4.imprint","IMPRINT",FACE,{"disambiguationData":[TD([[makeQuery(id+"F4.imprint","IMPRINT",EDGE,{"derivedFrom":sQuery(id+"F4.wireOp",EDGE,"E26.2.0")}),1.0]])]})])],"isStart":true})]}),makeQuery(id+"F20.opLoft","CAP_FACE",FACE,{"disambiguationData":[OSD([makeQuery(id+"F4.imprint","IMPRINT",FACE,{"disambiguationData":[TD([[makeQuery(id+"F4.imprint","IMPRINT",EDGE,{"derivedFrom":sQuery(id+"F4.wireOp",EDGE,"E26.1.0")}),1.0]])]})])],"isStart":true})]}),makeQuery(id+"F42.opRevolve","SWEPT_FACE",FACE,{"disambiguationData":[OSD([sQuery(id+"F41.wireOp",EDGE,"E32")])]})]});
            var Q12;
            Q12=makeQuery(id+"F42.boolean.opBoolean","INTERSECT",EDGE,{"disambiguationData":[OD(9.0)],"derivedFrom":[makeQuery(id+"F20.boolean.opBoolean","MERGE",FACE,{"derivedFrom":[makeQuery(id+"F19.boolean.opBoolean","MERGE",FACE,{"derivedFrom":[makeQuery(id+"F18.boolean.opBoolean","MERGE",FACE,{"derivedFrom":[makeQuery(id+"F17.boolean.opBoolean","MERGE",FACE,{"derivedFrom":[makeQuery(id+"F16.boolean.opBoolean","MERGE",FACE,{"derivedFrom":[makeQuery(id+"F15.boolean.opBoolean","MERGE",FACE,{"derivedFrom":[makeQuery(id+"F14.boolean.opBoolean","MERGE",FACE,{"derivedFrom":[makeQuery(id+"F13.boolean.opBoolean","MERGE",FACE,{"derivedFrom":[makeQuery(id+"F12.boolean.opBoolean","MERGE",FACE,{"derivedFrom":[makeQuery(id+"F11.boolean.opBoolean","MERGE",FACE,{"derivedFrom":[makeQuery(id+"F10.boolean.opBoolean","MERGE",FACE,{"derivedFrom":[makeQuery(id+"F9.boolean.opBoolean","MERGE",FACE,{"derivedFrom":[makeQuery(id+"F8.boolean.opBoolean","MERGE",FACE,{"derivedFrom":[makeQuery(id+"F7.boolean.opBoolean","MERGE",FACE,{"derivedFrom":[makeQuery(id+"F6.boolean.opBoolean","MERGE",FACE,{"derivedFrom":[makeQuery(id+"F5.boolean.opBoolean","MERGE",FACE,{"derivedFrom":[makeQuery(id+"F1.opRevolve","SWEPT_FACE",FACE,{"disambiguationData":[OSD([sQuery(id+"F0.wireOp",EDGE,"E14")])]}),makeQuery(id+"F5.opLoft","CAP_FACE",FACE,{"disambiguationData":[OSD([makeQuery(id+"F4.imprint","IMPRINT",FACE,{"disambiguationData":[TD([[makeQuery(id+"F4.imprint","IMPRINT",EDGE,{"derivedFrom":sQuery(id+"F4.wireOp",EDGE,"E21")}),1.0]])]})])],"isStart":true})]}),makeQuery(id+"F6.opLoft","CAP_FACE",FACE,{"disambiguationData":[OSD([makeQuery(id+"F4.imprint","IMPRINT",FACE,{"disambiguationData":[TD([[makeQuery(id+"F4.imprint","IMPRINT",EDGE,{"derivedFrom":sQuery(id+"F4.wireOp",EDGE,"E26.15.0")}),1.0]])]})])],"isStart":true})]}),makeQuery(id+"F7.opLoft","CAP_FACE",FACE,{"disambiguationData":[OSD([makeQuery(id+"F4.imprint","IMPRINT",FACE,{"disambiguationData":[TD([[makeQuery(id+"F4.imprint","IMPRINT",EDGE,{"derivedFrom":sQuery(id+"F4.wireOp",EDGE,"E26.14.0")}),1.0]])]})])],"isStart":true})]}),makeQuery(id+"F8.opLoft","CAP_FACE",FACE,{"disambiguationData":[OSD([makeQuery(id+"F4.imprint","IMPRINT",FACE,{"disambiguationData":[TD([[makeQuery(id+"F4.imprint","IMPRINT",EDGE,{"derivedFrom":sQuery(id+"F4.wireOp",EDGE,"E26.13.0")}),1.0]])]})])],"isStart":true})]}),makeQuery(id+"F9.opLoft","CAP_FACE",FACE,{"disambiguationData":[OSD([makeQuery(id+"F4.imprint","IMPRINT",FACE,{"disambiguationData":[TD([[makeQuery(id+"F4.imprint","IMPRINT",EDGE,{"derivedFrom":sQuery(id+"F4.wireOp",EDGE,"E26.12.0")}),1.0]])]})])],"isStart":true})]}),makeQuery(id+"F10.opLoft","CAP_FACE",FACE,{"disambiguationData":[OSD([makeQuery(id+"F4.imprint","IMPRINT",FACE,{"disambiguationData":[TD([[makeQuery(id+"F4.imprint","IMPRINT",EDGE,{"derivedFrom":sQuery(id+"F4.wireOp",EDGE,"E26.11.0")}),1.0]])]})])],"isStart":true})]}),makeQuery(id+"F11.opLoft","CAP_FACE",FACE,{"disambiguationData":[OSD([makeQuery(id+"F4.imprint","IMPRINT",FACE,{"disambiguationData":[TD([[makeQuery(id+"F4.imprint","IMPRINT",EDGE,{"derivedFrom":sQuery(id+"F4.wireOp",EDGE,"E26.10.0")}),1.0]])]})])],"isStart":true})]}),makeQuery(id+"F12.opLoft","CAP_FACE",FACE,{"disambiguationData":[OSD([makeQuery(id+"F4.imprint","IMPRINT",FACE,{"disambiguationData":[TD([[makeQuery(id+"F4.imprint","IMPRINT",EDGE,{"derivedFrom":sQuery(id+"F4.wireOp",EDGE,"E26.9.0")}),1.0]])]})])],"isStart":true})]}),makeQuery(id+"F13.opLoft","CAP_FACE",FACE,{"disambiguationData":[OSD([makeQuery(id+"F4.imprint","IMPRINT",FACE,{"disambiguationData":[TD([[makeQuery(id+"F4.imprint","IMPRINT",EDGE,{"derivedFrom":sQuery(id+"F4.wireOp",EDGE,"E26.8.0")}),1.0]])]})])],"isStart":true})]}),makeQuery(id+"F14.opLoft","CAP_FACE",FACE,{"disambiguationData":[OSD([makeQuery(id+"F4.imprint","IMPRINT",FACE,{"disambiguationData":[TD([[makeQuery(id+"F4.imprint","IMPRINT",EDGE,{"derivedFrom":sQuery(id+"F4.wireOp",EDGE,"E26.7.0")}),1.0]])]})])],"isStart":true})]}),makeQuery(id+"F15.opLoft","CAP_FACE",FACE,{"disambiguationData":[OSD([makeQuery(id+"F4.imprint","IMPRINT",FACE,{"disambiguationData":[TD([[makeQuery(id+"F4.imprint","IMPRINT",EDGE,{"derivedFrom":sQuery(id+"F4.wireOp",EDGE,"E26.6.0")}),1.0]])]})])],"isStart":true})]}),makeQuery(id+"F16.opLoft","CAP_FACE",FACE,{"disambiguationData":[OSD([makeQuery(id+"F4.imprint","IMPRINT",FACE,{"disambiguationData":[TD([[makeQuery(id+"F4.imprint","IMPRINT",EDGE,{"derivedFrom":sQuery(id+"F4.wireOp",EDGE,"E26.5.0")}),1.0]])]})])],"isStart":true})]}),makeQuery(id+"F17.opLoft","CAP_FACE",FACE,{"disambiguationData":[OSD([makeQuery(id+"F4.imprint","IMPRINT",FACE,{"disambiguationData":[TD([[makeQuery(id+"F4.imprint","IMPRINT",EDGE,{"derivedFrom":sQuery(id+"F4.wireOp",EDGE,"E26.4.0")}),1.0]])]})])],"isStart":true})]}),makeQuery(id+"F18.opLoft","CAP_FACE",FACE,{"disambiguationData":[OSD([makeQuery(id+"F4.imprint","IMPRINT",FACE,{"disambiguationData":[TD([[makeQuery(id+"F4.imprint","IMPRINT",EDGE,{"derivedFrom":sQuery(id+"F4.wireOp",EDGE,"E26.3.0")}),1.0]])]})])],"isStart":true})]}),makeQuery(id+"F19.opLoft","CAP_FACE",FACE,{"disambiguationData":[OSD([makeQuery(id+"F4.imprint","IMPRINT",FACE,{"disambiguationData":[TD([[makeQuery(id+"F4.imprint","IMPRINT",EDGE,{"derivedFrom":sQuery(id+"F4.wireOp",EDGE,"E26.2.0")}),1.0]])]})])],"isStart":true})]}),makeQuery(id+"F20.opLoft","CAP_FACE",FACE,{"disambiguationData":[OSD([makeQuery(id+"F4.imprint","IMPRINT",FACE,{"disambiguationData":[TD([[makeQuery(id+"F4.imprint","IMPRINT",EDGE,{"derivedFrom":sQuery(id+"F4.wireOp",EDGE,"E26.1.0")}),1.0]])]})])],"isStart":true})]}),makeQuery(id+"F42.opRevolve","SWEPT_FACE",FACE,{"disambiguationData":[OSD([sQuery(id+"F41.wireOp",EDGE,"E32")])]})]});
            var Q13;
            Q13=makeQuery(id+"F42.boolean.opBoolean","INTERSECT",EDGE,{"disambiguationData":[OD(8.0)],"derivedFrom":[makeQuery(id+"F20.boolean.opBoolean","MERGE",FACE,{"derivedFrom":[makeQuery(id+"F19.boolean.opBoolean","MERGE",FACE,{"derivedFrom":[makeQuery(id+"F18.boolean.opBoolean","MERGE",FACE,{"derivedFrom":[makeQuery(id+"F17.boolean.opBoolean","MERGE",FACE,{"derivedFrom":[makeQuery(id+"F16.boolean.opBoolean","MERGE",FACE,{"derivedFrom":[makeQuery(id+"F15.boolean.opBoolean","MERGE",FACE,{"derivedFrom":[makeQuery(id+"F14.boolean.opBoolean","MERGE",FACE,{"derivedFrom":[makeQuery(id+"F13.boolean.opBoolean","MERGE",FACE,{"derivedFrom":[makeQuery(id+"F12.boolean.opBoolean","MERGE",FACE,{"derivedFrom":[makeQuery(id+"F11.boolean.opBoolean","MERGE",FACE,{"derivedFrom":[makeQuery(id+"F10.boolean.opBoolean","MERGE",FACE,{"derivedFrom":[makeQuery(id+"F9.boolean.opBoolean","MERGE",FACE,{"derivedFrom":[makeQuery(id+"F8.boolean.opBoolean","MERGE",FACE,{"derivedFrom":[makeQuery(id+"F7.boolean.opBoolean","MERGE",FACE,{"derivedFrom":[makeQuery(id+"F6.boolean.opBoolean","MERGE",FACE,{"derivedFrom":[makeQuery(id+"F5.boolean.opBoolean","MERGE",FACE,{"derivedFrom":[makeQuery(id+"F1.opRevolve","SWEPT_FACE",FACE,{"disambiguationData":[OSD([sQuery(id+"F0.wireOp",EDGE,"E14")])]}),makeQuery(id+"F5.opLoft","CAP_FACE",FACE,{"disambiguationData":[OSD([makeQuery(id+"F4.imprint","IMPRINT",FACE,{"disambiguationData":[TD([[makeQuery(id+"F4.imprint","IMPRINT",EDGE,{"derivedFrom":sQuery(id+"F4.wireOp",EDGE,"E21")}),1.0]])]})])],"isStart":true})]}),makeQuery(id+"F6.opLoft","CAP_FACE",FACE,{"disambiguationData":[OSD([makeQuery(id+"F4.imprint","IMPRINT",FACE,{"disambiguationData":[TD([[makeQuery(id+"F4.imprint","IMPRINT",EDGE,{"derivedFrom":sQuery(id+"F4.wireOp",EDGE,"E26.15.0")}),1.0]])]})])],"isStart":true})]}),makeQuery(id+"F7.opLoft","CAP_FACE",FACE,{"disambiguationData":[OSD([makeQuery(id+"F4.imprint","IMPRINT",FACE,{"disambiguationData":[TD([[makeQuery(id+"F4.imprint","IMPRINT",EDGE,{"derivedFrom":sQuery(id+"F4.wireOp",EDGE,"E26.14.0")}),1.0]])]})])],"isStart":true})]}),makeQuery(id+"F8.opLoft","CAP_FACE",FACE,{"disambiguationData":[OSD([makeQuery(id+"F4.imprint","IMPRINT",FACE,{"disambiguationData":[TD([[makeQuery(id+"F4.imprint","IMPRINT",EDGE,{"derivedFrom":sQuery(id+"F4.wireOp",EDGE,"E26.13.0")}),1.0]])]})])],"isStart":true})]}),makeQuery(id+"F9.opLoft","CAP_FACE",FACE,{"disambiguationData":[OSD([makeQuery(id+"F4.imprint","IMPRINT",FACE,{"disambiguationData":[TD([[makeQuery(id+"F4.imprint","IMPRINT",EDGE,{"derivedFrom":sQuery(id+"F4.wireOp",EDGE,"E26.12.0")}),1.0]])]})])],"isStart":true})]}),makeQuery(id+"F10.opLoft","CAP_FACE",FACE,{"disambiguationData":[OSD([makeQuery(id+"F4.imprint","IMPRINT",FACE,{"disambiguationData":[TD([[makeQuery(id+"F4.imprint","IMPRINT",EDGE,{"derivedFrom":sQuery(id+"F4.wireOp",EDGE,"E26.11.0")}),1.0]])]})])],"isStart":true})]}),makeQuery(id+"F11.opLoft","CAP_FACE",FACE,{"disambiguationData":[OSD([makeQuery(id+"F4.imprint","IMPRINT",FACE,{"disambiguationData":[TD([[makeQuery(id+"F4.imprint","IMPRINT",EDGE,{"derivedFrom":sQuery(id+"F4.wireOp",EDGE,"E26.10.0")}),1.0]])]})])],"isStart":true})]}),makeQuery(id+"F12.opLoft","CAP_FACE",FACE,{"disambiguationData":[OSD([makeQuery(id+"F4.imprint","IMPRINT",FACE,{"disambiguationData":[TD([[makeQuery(id+"F4.imprint","IMPRINT",EDGE,{"derivedFrom":sQuery(id+"F4.wireOp",EDGE,"E26.9.0")}),1.0]])]})])],"isStart":true})]}),makeQuery(id+"F13.opLoft","CAP_FACE",FACE,{"disambiguationData":[OSD([makeQuery(id+"F4.imprint","IMPRINT",FACE,{"disambiguationData":[TD([[makeQuery(id+"F4.imprint","IMPRINT",EDGE,{"derivedFrom":sQuery(id+"F4.wireOp",EDGE,"E26.8.0")}),1.0]])]})])],"isStart":true})]}),makeQuery(id+"F14.opLoft","CAP_FACE",FACE,{"disambiguationData":[OSD([makeQuery(id+"F4.imprint","IMPRINT",FACE,{"disambiguationData":[TD([[makeQuery(id+"F4.imprint","IMPRINT",EDGE,{"derivedFrom":sQuery(id+"F4.wireOp",EDGE,"E26.7.0")}),1.0]])]})])],"isStart":true})]}),makeQuery(id+"F15.opLoft","CAP_FACE",FACE,{"disambiguationData":[OSD([makeQuery(id+"F4.imprint","IMPRINT",FACE,{"disambiguationData":[TD([[makeQuery(id+"F4.imprint","IMPRINT",EDGE,{"derivedFrom":sQuery(id+"F4.wireOp",EDGE,"E26.6.0")}),1.0]])]})])],"isStart":true})]}),makeQuery(id+"F16.opLoft","CAP_FACE",FACE,{"disambiguationData":[OSD([makeQuery(id+"F4.imprint","IMPRINT",FACE,{"disambiguationData":[TD([[makeQuery(id+"F4.imprint","IMPRINT",EDGE,{"derivedFrom":sQuery(id+"F4.wireOp",EDGE,"E26.5.0")}),1.0]])]})])],"isStart":true})]}),makeQuery(id+"F17.opLoft","CAP_FACE",FACE,{"disambiguationData":[OSD([makeQuery(id+"F4.imprint","IMPRINT",FACE,{"disambiguationData":[TD([[makeQuery(id+"F4.imprint","IMPRINT",EDGE,{"derivedFrom":sQuery(id+"F4.wireOp",EDGE,"E26.4.0")}),1.0]])]})])],"isStart":true})]}),makeQuery(id+"F18.opLoft","CAP_FACE",FACE,{"disambiguationData":[OSD([makeQuery(id+"F4.imprint","IMPRINT",FACE,{"disambiguationData":[TD([[makeQuery(id+"F4.imprint","IMPRINT",EDGE,{"derivedFrom":sQuery(id+"F4.wireOp",EDGE,"E26.3.0")}),1.0]])]})])],"isStart":true})]}),makeQuery(id+"F19.opLoft","CAP_FACE",FACE,{"disambiguationData":[OSD([makeQuery(id+"F4.imprint","IMPRINT",FACE,{"disambiguationData":[TD([[makeQuery(id+"F4.imprint","IMPRINT",EDGE,{"derivedFrom":sQuery(id+"F4.wireOp",EDGE,"E26.2.0")}),1.0]])]})])],"isStart":true})]}),makeQuery(id+"F20.opLoft","CAP_FACE",FACE,{"disambiguationData":[OSD([makeQuery(id+"F4.imprint","IMPRINT",FACE,{"disambiguationData":[TD([[makeQuery(id+"F4.imprint","IMPRINT",EDGE,{"derivedFrom":sQuery(id+"F4.wireOp",EDGE,"E26.1.0")}),1.0]])]})])],"isStart":true})]}),makeQuery(id+"F42.opRevolve","SWEPT_FACE",FACE,{"disambiguationData":[OSD([sQuery(id+"F41.wireOp",EDGE,"E32")])]})]});
            var Q14;
            Q14=makeQuery(id+"F42.boolean.opBoolean","INTERSECT",EDGE,{"disambiguationData":[OD(7.0)],"derivedFrom":[makeQuery(id+"F20.boolean.opBoolean","MERGE",FACE,{"derivedFrom":[makeQuery(id+"F19.boolean.opBoolean","MERGE",FACE,{"derivedFrom":[makeQuery(id+"F18.boolean.opBoolean","MERGE",FACE,{"derivedFrom":[makeQuery(id+"F17.boolean.opBoolean","MERGE",FACE,{"derivedFrom":[makeQuery(id+"F16.boolean.opBoolean","MERGE",FACE,{"derivedFrom":[makeQuery(id+"F15.boolean.opBoolean","MERGE",FACE,{"derivedFrom":[makeQuery(id+"F14.boolean.opBoolean","MERGE",FACE,{"derivedFrom":[makeQuery(id+"F13.boolean.opBoolean","MERGE",FACE,{"derivedFrom":[makeQuery(id+"F12.boolean.opBoolean","MERGE",FACE,{"derivedFrom":[makeQuery(id+"F11.boolean.opBoolean","MERGE",FACE,{"derivedFrom":[makeQuery(id+"F10.boolean.opBoolean","MERGE",FACE,{"derivedFrom":[makeQuery(id+"F9.boolean.opBoolean","MERGE",FACE,{"derivedFrom":[makeQuery(id+"F8.boolean.opBoolean","MERGE",FACE,{"derivedFrom":[makeQuery(id+"F7.boolean.opBoolean","MERGE",FACE,{"derivedFrom":[makeQuery(id+"F6.boolean.opBoolean","MERGE",FACE,{"derivedFrom":[makeQuery(id+"F5.boolean.opBoolean","MERGE",FACE,{"derivedFrom":[makeQuery(id+"F1.opRevolve","SWEPT_FACE",FACE,{"disambiguationData":[OSD([sQuery(id+"F0.wireOp",EDGE,"E14")])]}),makeQuery(id+"F5.opLoft","CAP_FACE",FACE,{"disambiguationData":[OSD([makeQuery(id+"F4.imprint","IMPRINT",FACE,{"disambiguationData":[TD([[makeQuery(id+"F4.imprint","IMPRINT",EDGE,{"derivedFrom":sQuery(id+"F4.wireOp",EDGE,"E21")}),1.0]])]})])],"isStart":true})]}),makeQuery(id+"F6.opLoft","CAP_FACE",FACE,{"disambiguationData":[OSD([makeQuery(id+"F4.imprint","IMPRINT",FACE,{"disambiguationData":[TD([[makeQuery(id+"F4.imprint","IMPRINT",EDGE,{"derivedFrom":sQuery(id+"F4.wireOp",EDGE,"E26.15.0")}),1.0]])]})])],"isStart":true})]}),makeQuery(id+"F7.opLoft","CAP_FACE",FACE,{"disambiguationData":[OSD([makeQuery(id+"F4.imprint","IMPRINT",FACE,{"disambiguationData":[TD([[makeQuery(id+"F4.imprint","IMPRINT",EDGE,{"derivedFrom":sQuery(id+"F4.wireOp",EDGE,"E26.14.0")}),1.0]])]})])],"isStart":true})]}),makeQuery(id+"F8.opLoft","CAP_FACE",FACE,{"disambiguationData":[OSD([makeQuery(id+"F4.imprint","IMPRINT",FACE,{"disambiguationData":[TD([[makeQuery(id+"F4.imprint","IMPRINT",EDGE,{"derivedFrom":sQuery(id+"F4.wireOp",EDGE,"E26.13.0")}),1.0]])]})])],"isStart":true})]}),makeQuery(id+"F9.opLoft","CAP_FACE",FACE,{"disambiguationData":[OSD([makeQuery(id+"F4.imprint","IMPRINT",FACE,{"disambiguationData":[TD([[makeQuery(id+"F4.imprint","IMPRINT",EDGE,{"derivedFrom":sQuery(id+"F4.wireOp",EDGE,"E26.12.0")}),1.0]])]})])],"isStart":true})]}),makeQuery(id+"F10.opLoft","CAP_FACE",FACE,{"disambiguationData":[OSD([makeQuery(id+"F4.imprint","IMPRINT",FACE,{"disambiguationData":[TD([[makeQuery(id+"F4.imprint","IMPRINT",EDGE,{"derivedFrom":sQuery(id+"F4.wireOp",EDGE,"E26.11.0")}),1.0]])]})])],"isStart":true})]}),makeQuery(id+"F11.opLoft","CAP_FACE",FACE,{"disambiguationData":[OSD([makeQuery(id+"F4.imprint","IMPRINT",FACE,{"disambiguationData":[TD([[makeQuery(id+"F4.imprint","IMPRINT",EDGE,{"derivedFrom":sQuery(id+"F4.wireOp",EDGE,"E26.10.0")}),1.0]])]})])],"isStart":true})]}),makeQuery(id+"F12.opLoft","CAP_FACE",FACE,{"disambiguationData":[OSD([makeQuery(id+"F4.imprint","IMPRINT",FACE,{"disambiguationData":[TD([[makeQuery(id+"F4.imprint","IMPRINT",EDGE,{"derivedFrom":sQuery(id+"F4.wireOp",EDGE,"E26.9.0")}),1.0]])]})])],"isStart":true})]}),makeQuery(id+"F13.opLoft","CAP_FACE",FACE,{"disambiguationData":[OSD([makeQuery(id+"F4.imprint","IMPRINT",FACE,{"disambiguationData":[TD([[makeQuery(id+"F4.imprint","IMPRINT",EDGE,{"derivedFrom":sQuery(id+"F4.wireOp",EDGE,"E26.8.0")}),1.0]])]})])],"isStart":true})]}),makeQuery(id+"F14.opLoft","CAP_FACE",FACE,{"disambiguationData":[OSD([makeQuery(id+"F4.imprint","IMPRINT",FACE,{"disambiguationData":[TD([[makeQuery(id+"F4.imprint","IMPRINT",EDGE,{"derivedFrom":sQuery(id+"F4.wireOp",EDGE,"E26.7.0")}),1.0]])]})])],"isStart":true})]}),makeQuery(id+"F15.opLoft","CAP_FACE",FACE,{"disambiguationData":[OSD([makeQuery(id+"F4.imprint","IMPRINT",FACE,{"disambiguationData":[TD([[makeQuery(id+"F4.imprint","IMPRINT",EDGE,{"derivedFrom":sQuery(id+"F4.wireOp",EDGE,"E26.6.0")}),1.0]])]})])],"isStart":true})]}),makeQuery(id+"F16.opLoft","CAP_FACE",FACE,{"disambiguationData":[OSD([makeQuery(id+"F4.imprint","IMPRINT",FACE,{"disambiguationData":[TD([[makeQuery(id+"F4.imprint","IMPRINT",EDGE,{"derivedFrom":sQuery(id+"F4.wireOp",EDGE,"E26.5.0")}),1.0]])]})])],"isStart":true})]}),makeQuery(id+"F17.opLoft","CAP_FACE",FACE,{"disambiguationData":[OSD([makeQuery(id+"F4.imprint","IMPRINT",FACE,{"disambiguationData":[TD([[makeQuery(id+"F4.imprint","IMPRINT",EDGE,{"derivedFrom":sQuery(id+"F4.wireOp",EDGE,"E26.4.0")}),1.0]])]})])],"isStart":true})]}),makeQuery(id+"F18.opLoft","CAP_FACE",FACE,{"disambiguationData":[OSD([makeQuery(id+"F4.imprint","IMPRINT",FACE,{"disambiguationData":[TD([[makeQuery(id+"F4.imprint","IMPRINT",EDGE,{"derivedFrom":sQuery(id+"F4.wireOp",EDGE,"E26.3.0")}),1.0]])]})])],"isStart":true})]}),makeQuery(id+"F19.opLoft","CAP_FACE",FACE,{"disambiguationData":[OSD([makeQuery(id+"F4.imprint","IMPRINT",FACE,{"disambiguationData":[TD([[makeQuery(id+"F4.imprint","IMPRINT",EDGE,{"derivedFrom":sQuery(id+"F4.wireOp",EDGE,"E26.2.0")}),1.0]])]})])],"isStart":true})]}),makeQuery(id+"F20.opLoft","CAP_FACE",FACE,{"disambiguationData":[OSD([makeQuery(id+"F4.imprint","IMPRINT",FACE,{"disambiguationData":[TD([[makeQuery(id+"F4.imprint","IMPRINT",EDGE,{"derivedFrom":sQuery(id+"F4.wireOp",EDGE,"E26.1.0")}),1.0]])]})])],"isStart":true})]}),makeQuery(id+"F42.opRevolve","SWEPT_FACE",FACE,{"disambiguationData":[OSD([sQuery(id+"F41.wireOp",EDGE,"E32")])]})]});
            var Q15;
            Q15=makeQuery(id+"F42.boolean.opBoolean","INTERSECT",EDGE,{"disambiguationData":[OD(6.0)],"derivedFrom":[makeQuery(id+"F20.boolean.opBoolean","MERGE",FACE,{"derivedFrom":[makeQuery(id+"F19.boolean.opBoolean","MERGE",FACE,{"derivedFrom":[makeQuery(id+"F18.boolean.opBoolean","MERGE",FACE,{"derivedFrom":[makeQuery(id+"F17.boolean.opBoolean","MERGE",FACE,{"derivedFrom":[makeQuery(id+"F16.boolean.opBoolean","MERGE",FACE,{"derivedFrom":[makeQuery(id+"F15.boolean.opBoolean","MERGE",FACE,{"derivedFrom":[makeQuery(id+"F14.boolean.opBoolean","MERGE",FACE,{"derivedFrom":[makeQuery(id+"F13.boolean.opBoolean","MERGE",FACE,{"derivedFrom":[makeQuery(id+"F12.boolean.opBoolean","MERGE",FACE,{"derivedFrom":[makeQuery(id+"F11.boolean.opBoolean","MERGE",FACE,{"derivedFrom":[makeQuery(id+"F10.boolean.opBoolean","MERGE",FACE,{"derivedFrom":[makeQuery(id+"F9.boolean.opBoolean","MERGE",FACE,{"derivedFrom":[makeQuery(id+"F8.boolean.opBoolean","MERGE",FACE,{"derivedFrom":[makeQuery(id+"F7.boolean.opBoolean","MERGE",FACE,{"derivedFrom":[makeQuery(id+"F6.boolean.opBoolean","MERGE",FACE,{"derivedFrom":[makeQuery(id+"F5.boolean.opBoolean","MERGE",FACE,{"derivedFrom":[makeQuery(id+"F1.opRevolve","SWEPT_FACE",FACE,{"disambiguationData":[OSD([sQuery(id+"F0.wireOp",EDGE,"E14")])]}),makeQuery(id+"F5.opLoft","CAP_FACE",FACE,{"disambiguationData":[OSD([makeQuery(id+"F4.imprint","IMPRINT",FACE,{"disambiguationData":[TD([[makeQuery(id+"F4.imprint","IMPRINT",EDGE,{"derivedFrom":sQuery(id+"F4.wireOp",EDGE,"E21")}),1.0]])]})])],"isStart":true})]}),makeQuery(id+"F6.opLoft","CAP_FACE",FACE,{"disambiguationData":[OSD([makeQuery(id+"F4.imprint","IMPRINT",FACE,{"disambiguationData":[TD([[makeQuery(id+"F4.imprint","IMPRINT",EDGE,{"derivedFrom":sQuery(id+"F4.wireOp",EDGE,"E26.15.0")}),1.0]])]})])],"isStart":true})]}),makeQuery(id+"F7.opLoft","CAP_FACE",FACE,{"disambiguationData":[OSD([makeQuery(id+"F4.imprint","IMPRINT",FACE,{"disambiguationData":[TD([[makeQuery(id+"F4.imprint","IMPRINT",EDGE,{"derivedFrom":sQuery(id+"F4.wireOp",EDGE,"E26.14.0")}),1.0]])]})])],"isStart":true})]}),makeQuery(id+"F8.opLoft","CAP_FACE",FACE,{"disambiguationData":[OSD([makeQuery(id+"F4.imprint","IMPRINT",FACE,{"disambiguationData":[TD([[makeQuery(id+"F4.imprint","IMPRINT",EDGE,{"derivedFrom":sQuery(id+"F4.wireOp",EDGE,"E26.13.0")}),1.0]])]})])],"isStart":true})]}),makeQuery(id+"F9.opLoft","CAP_FACE",FACE,{"disambiguationData":[OSD([makeQuery(id+"F4.imprint","IMPRINT",FACE,{"disambiguationData":[TD([[makeQuery(id+"F4.imprint","IMPRINT",EDGE,{"derivedFrom":sQuery(id+"F4.wireOp",EDGE,"E26.12.0")}),1.0]])]})])],"isStart":true})]}),makeQuery(id+"F10.opLoft","CAP_FACE",FACE,{"disambiguationData":[OSD([makeQuery(id+"F4.imprint","IMPRINT",FACE,{"disambiguationData":[TD([[makeQuery(id+"F4.imprint","IMPRINT",EDGE,{"derivedFrom":sQuery(id+"F4.wireOp",EDGE,"E26.11.0")}),1.0]])]})])],"isStart":true})]}),makeQuery(id+"F11.opLoft","CAP_FACE",FACE,{"disambiguationData":[OSD([makeQuery(id+"F4.imprint","IMPRINT",FACE,{"disambiguationData":[TD([[makeQuery(id+"F4.imprint","IMPRINT",EDGE,{"derivedFrom":sQuery(id+"F4.wireOp",EDGE,"E26.10.0")}),1.0]])]})])],"isStart":true})]}),makeQuery(id+"F12.opLoft","CAP_FACE",FACE,{"disambiguationData":[OSD([makeQuery(id+"F4.imprint","IMPRINT",FACE,{"disambiguationData":[TD([[makeQuery(id+"F4.imprint","IMPRINT",EDGE,{"derivedFrom":sQuery(id+"F4.wireOp",EDGE,"E26.9.0")}),1.0]])]})])],"isStart":true})]}),makeQuery(id+"F13.opLoft","CAP_FACE",FACE,{"disambiguationData":[OSD([makeQuery(id+"F4.imprint","IMPRINT",FACE,{"disambiguationData":[TD([[makeQuery(id+"F4.imprint","IMPRINT",EDGE,{"derivedFrom":sQuery(id+"F4.wireOp",EDGE,"E26.8.0")}),1.0]])]})])],"isStart":true})]}),makeQuery(id+"F14.opLoft","CAP_FACE",FACE,{"disambiguationData":[OSD([makeQuery(id+"F4.imprint","IMPRINT",FACE,{"disambiguationData":[TD([[makeQuery(id+"F4.imprint","IMPRINT",EDGE,{"derivedFrom":sQuery(id+"F4.wireOp",EDGE,"E26.7.0")}),1.0]])]})])],"isStart":true})]}),makeQuery(id+"F15.opLoft","CAP_FACE",FACE,{"disambiguationData":[OSD([makeQuery(id+"F4.imprint","IMPRINT",FACE,{"disambiguationData":[TD([[makeQuery(id+"F4.imprint","IMPRINT",EDGE,{"derivedFrom":sQuery(id+"F4.wireOp",EDGE,"E26.6.0")}),1.0]])]})])],"isStart":true})]}),makeQuery(id+"F16.opLoft","CAP_FACE",FACE,{"disambiguationData":[OSD([makeQuery(id+"F4.imprint","IMPRINT",FACE,{"disambiguationData":[TD([[makeQuery(id+"F4.imprint","IMPRINT",EDGE,{"derivedFrom":sQuery(id+"F4.wireOp",EDGE,"E26.5.0")}),1.0]])]})])],"isStart":true})]}),makeQuery(id+"F17.opLoft","CAP_FACE",FACE,{"disambiguationData":[OSD([makeQuery(id+"F4.imprint","IMPRINT",FACE,{"disambiguationData":[TD([[makeQuery(id+"F4.imprint","IMPRINT",EDGE,{"derivedFrom":sQuery(id+"F4.wireOp",EDGE,"E26.4.0")}),1.0]])]})])],"isStart":true})]}),makeQuery(id+"F18.opLoft","CAP_FACE",FACE,{"disambiguationData":[OSD([makeQuery(id+"F4.imprint","IMPRINT",FACE,{"disambiguationData":[TD([[makeQuery(id+"F4.imprint","IMPRINT",EDGE,{"derivedFrom":sQuery(id+"F4.wireOp",EDGE,"E26.3.0")}),1.0]])]})])],"isStart":true})]}),makeQuery(id+"F19.opLoft","CAP_FACE",FACE,{"disambiguationData":[OSD([makeQuery(id+"F4.imprint","IMPRINT",FACE,{"disambiguationData":[TD([[makeQuery(id+"F4.imprint","IMPRINT",EDGE,{"derivedFrom":sQuery(id+"F4.wireOp",EDGE,"E26.2.0")}),1.0]])]})])],"isStart":true})]}),makeQuery(id+"F20.opLoft","CAP_FACE",FACE,{"disambiguationData":[OSD([makeQuery(id+"F4.imprint","IMPRINT",FACE,{"disambiguationData":[TD([[makeQuery(id+"F4.imprint","IMPRINT",EDGE,{"derivedFrom":sQuery(id+"F4.wireOp",EDGE,"E26.1.0")}),1.0]])]})])],"isStart":true})]}),makeQuery(id+"F42.opRevolve","SWEPT_FACE",FACE,{"disambiguationData":[OSD([sQuery(id+"F41.wireOp",EDGE,"E32")])]})]});
            var Q16;
            Q16=makeQuery(id+"F42.boolean.opBoolean","INTERSECT",EDGE,{"derivedFrom":[makeQuery(id+"F27.opLoft","CAP_FACE",FACE,{"disambiguationData":[OSD([makeQuery(id+"F22.imprint","IMPRINT",FACE,{"disambiguationData":[TD([[makeQuery(id+"F22.imprint","IMPRINT",EDGE,{"derivedFrom":sQuery(id+"F22.wireOp",EDGE,"E28.4.0")}),-1.0]])]})])],"isStart":true}),makeQuery(id+"F42.opRevolve","SWEPT_FACE",FACE,{"disambiguationData":[OSD([sQuery(id+"F41.wireOp",EDGE,"E32")])]})]});
            var Q17;
            Q17=makeQuery(id+"F42.boolean.opBoolean","INTERSECT",EDGE,{"derivedFrom":[makeQuery(id+"F26.opLoft","CAP_FACE",FACE,{"disambiguationData":[OSD([makeQuery(id+"F22.imprint","IMPRINT",FACE,{"disambiguationData":[TD([[makeQuery(id+"F22.imprint","IMPRINT",EDGE,{"derivedFrom":sQuery(id+"F22.wireOp",EDGE,"E28.3.0")}),-1.0]])]})])],"isStart":true}),makeQuery(id+"F42.opRevolve","SWEPT_FACE",FACE,{"disambiguationData":[OSD([sQuery(id+"F41.wireOp",EDGE,"E32")])]})]});
            var Q18;
            Q18=makeQuery(id+"F42.boolean.opBoolean","INTERSECT",EDGE,{"derivedFrom":[makeQuery(id+"F25.opLoft","CAP_FACE",FACE,{"disambiguationData":[OSD([makeQuery(id+"F22.imprint","IMPRINT",FACE,{"disambiguationData":[TD([[makeQuery(id+"F22.imprint","IMPRINT",EDGE,{"derivedFrom":sQuery(id+"F22.wireOp",EDGE,"E28.2.0")}),-1.0]])]})])],"isStart":true}),makeQuery(id+"F42.opRevolve","SWEPT_FACE",FACE,{"disambiguationData":[OSD([sQuery(id+"F41.wireOp",EDGE,"E32")])]})]});
            var Q19;
            Q19=makeQuery(id+"F42.boolean.opBoolean","INTERSECT",EDGE,{"derivedFrom":[makeQuery(id+"F24.opLoft","CAP_FACE",FACE,{"disambiguationData":[OSD([makeQuery(id+"F22.imprint","IMPRINT",FACE,{"disambiguationData":[TD([[makeQuery(id+"F22.imprint","IMPRINT",EDGE,{"derivedFrom":sQuery(id+"F22.wireOp",EDGE,"E28.1.0")}),-1.0]])]})])],"isStart":true}),makeQuery(id+"F42.opRevolve","SWEPT_FACE",FACE,{"disambiguationData":[OSD([sQuery(id+"F41.wireOp",EDGE,"E32")])]})]});
            var Q20;
            Q20=makeQuery(id+"F42.boolean.opBoolean","INTERSECT",EDGE,{"derivedFrom":[makeQuery(id+"F23.opLoft","CAP_FACE",FACE,{"disambiguationData":[OSD([makeQuery(id+"F22.imprint","IMPRINT",FACE,{"disambiguationData":[TD([[makeQuery(id+"F22.imprint","IMPRINT",EDGE,{"derivedFrom":sQuery(id+"F22.wireOp",EDGE,"E27.bottom")}),1.0]])]})])],"isStart":true}),makeQuery(id+"F42.opRevolve","SWEPT_FACE",FACE,{"disambiguationData":[OSD([sQuery(id+"F41.wireOp",EDGE,"E32")])]})]});
            var Q21;
            Q21=makeQuery(id+"F42.boolean.opBoolean","INTERSECT",EDGE,{"derivedFrom":[makeQuery(id+"F38.opLoft","CAP_FACE",FACE,{"disambiguationData":[OSD([makeQuery(id+"F22.imprint","IMPRINT",FACE,{"disambiguationData":[TD([[makeQuery(id+"F22.imprint","IMPRINT",EDGE,{"derivedFrom":sQuery(id+"F22.wireOp",EDGE,"E28.15.0")}),-1.0]])]})])],"isStart":true}),makeQuery(id+"F42.opRevolve","SWEPT_FACE",FACE,{"disambiguationData":[OSD([sQuery(id+"F41.wireOp",EDGE,"E32")])]})]});
            var Q22;
            Q22=makeQuery(id+"F42.boolean.opBoolean","INTERSECT",EDGE,{"derivedFrom":[makeQuery(id+"F37.opLoft","CAP_FACE",FACE,{"disambiguationData":[OSD([makeQuery(id+"F22.imprint","IMPRINT",FACE,{"disambiguationData":[TD([[makeQuery(id+"F22.imprint","IMPRINT",EDGE,{"derivedFrom":sQuery(id+"F22.wireOp",EDGE,"E28.14.0")}),-1.0]])]})])],"isStart":true}),makeQuery(id+"F42.opRevolve","SWEPT_FACE",FACE,{"disambiguationData":[OSD([sQuery(id+"F41.wireOp",EDGE,"E32")])]})]});
            var Q23;
            Q23=makeQuery(id+"F42.boolean.opBoolean","INTERSECT",EDGE,{"derivedFrom":[makeQuery(id+"F36.opLoft","CAP_FACE",FACE,{"disambiguationData":[OSD([makeQuery(id+"F22.imprint","IMPRINT",FACE,{"disambiguationData":[TD([[makeQuery(id+"F22.imprint","IMPRINT",EDGE,{"derivedFrom":sQuery(id+"F22.wireOp",EDGE,"E28.13.0")}),-1.0]])]})])],"isStart":true}),makeQuery(id+"F42.opRevolve","SWEPT_FACE",FACE,{"disambiguationData":[OSD([sQuery(id+"F41.wireOp",EDGE,"E32")])]})]});
            var Q24;
            Q24=makeQuery(id+"F42.boolean.opBoolean","INTERSECT",EDGE,{"derivedFrom":[makeQuery(id+"F35.opLoft","CAP_FACE",FACE,{"disambiguationData":[OSD([makeQuery(id+"F22.imprint","IMPRINT",FACE,{"disambiguationData":[TD([[makeQuery(id+"F22.imprint","IMPRINT",EDGE,{"derivedFrom":sQuery(id+"F22.wireOp",EDGE,"E28.12.0")}),-1.0]])]})])],"isStart":true}),makeQuery(id+"F42.opRevolve","SWEPT_FACE",FACE,{"disambiguationData":[OSD([sQuery(id+"F41.wireOp",EDGE,"E32")])]})]});
            var Q25;
            Q25=makeQuery(id+"F42.boolean.opBoolean","INTERSECT",EDGE,{"derivedFrom":[makeQuery(id+"F34.opLoft","CAP_FACE",FACE,{"disambiguationData":[OSD([makeQuery(id+"F22.imprint","IMPRINT",FACE,{"disambiguationData":[TD([[makeQuery(id+"F22.imprint","IMPRINT",EDGE,{"derivedFrom":sQuery(id+"F22.wireOp",EDGE,"E28.11.0")}),-1.0]])]})])],"isStart":true}),makeQuery(id+"F42.opRevolve","SWEPT_FACE",FACE,{"disambiguationData":[OSD([sQuery(id+"F41.wireOp",EDGE,"E32")])]})]});
            var Q26;
            Q26=makeQuery(id+"F42.boolean.opBoolean","INTERSECT",EDGE,{"derivedFrom":[makeQuery(id+"F33.opLoft","CAP_FACE",FACE,{"disambiguationData":[OSD([makeQuery(id+"F22.imprint","IMPRINT",FACE,{"disambiguationData":[TD([[makeQuery(id+"F22.imprint","IMPRINT",EDGE,{"derivedFrom":sQuery(id+"F22.wireOp",EDGE,"E28.10.0")}),-1.0]])]})])],"isStart":true}),makeQuery(id+"F42.opRevolve","SWEPT_FACE",FACE,{"disambiguationData":[OSD([sQuery(id+"F41.wireOp",EDGE,"E32")])]})]});
            var Q27;
            Q27=makeQuery(id+"F42.boolean.opBoolean","INTERSECT",EDGE,{"derivedFrom":[makeQuery(id+"F32.opLoft","CAP_FACE",FACE,{"disambiguationData":[OSD([makeQuery(id+"F22.imprint","IMPRINT",FACE,{"disambiguationData":[TD([[makeQuery(id+"F22.imprint","IMPRINT",EDGE,{"derivedFrom":sQuery(id+"F22.wireOp",EDGE,"E28.9.0")}),-1.0]])]})])],"isStart":true}),makeQuery(id+"F42.opRevolve","SWEPT_FACE",FACE,{"disambiguationData":[OSD([sQuery(id+"F41.wireOp",EDGE,"E32")])]})]});
            var Q28;
            Q28=makeQuery(id+"F42.boolean.opBoolean","INTERSECT",EDGE,{"derivedFrom":[makeQuery(id+"F31.opLoft","CAP_FACE",FACE,{"disambiguationData":[OSD([makeQuery(id+"F22.imprint","IMPRINT",FACE,{"disambiguationData":[TD([[makeQuery(id+"F22.imprint","IMPRINT",EDGE,{"derivedFrom":sQuery(id+"F22.wireOp",EDGE,"E28.8.0")}),-1.0]])]})])],"isStart":true}),makeQuery(id+"F42.opRevolve","SWEPT_FACE",FACE,{"disambiguationData":[OSD([sQuery(id+"F41.wireOp",EDGE,"E32")])]})]});
            var Q29;
            Q29=makeQuery(id+"F42.boolean.opBoolean","INTERSECT",EDGE,{"derivedFrom":[makeQuery(id+"F30.opLoft","CAP_FACE",FACE,{"disambiguationData":[OSD([makeQuery(id+"F22.imprint","IMPRINT",FACE,{"disambiguationData":[TD([[makeQuery(id+"F22.imprint","IMPRINT",EDGE,{"derivedFrom":sQuery(id+"F22.wireOp",EDGE,"E28.7.0")}),-1.0]])]})])],"isStart":true}),makeQuery(id+"F42.opRevolve","SWEPT_FACE",FACE,{"disambiguationData":[OSD([sQuery(id+"F41.wireOp",EDGE,"E32")])]})]});
            var Q30;
            Q30=makeQuery(id+"F42.boolean.opBoolean","INTERSECT",EDGE,{"derivedFrom":[makeQuery(id+"F29.opLoft","CAP_FACE",FACE,{"disambiguationData":[OSD([makeQuery(id+"F22.imprint","IMPRINT",FACE,{"disambiguationData":[TD([[makeQuery(id+"F22.imprint","IMPRINT",EDGE,{"derivedFrom":sQuery(id+"F22.wireOp",EDGE,"E28.6.0")}),-1.0]])]})])],"isStart":true}),makeQuery(id+"F42.opRevolve","SWEPT_FACE",FACE,{"disambiguationData":[OSD([sQuery(id+"F41.wireOp",EDGE,"E32")])]})]});
            var Q31;
            Q31=makeQuery(id+"F42.boolean.opBoolean","INTERSECT",EDGE,{"derivedFrom":[makeQuery(id+"F28.opLoft","CAP_FACE",FACE,{"disambiguationData":[OSD([makeQuery(id+"F22.imprint","IMPRINT",FACE,{"disambiguationData":[TD([[makeQuery(id+"F22.imprint","IMPRINT",EDGE,{"derivedFrom":sQuery(id+"F22.wireOp",EDGE,"E28.5.0")}),-1.0]])]})])],"isStart":true}),makeQuery(id+"F42.opRevolve","SWEPT_FACE",FACE,{"disambiguationData":[OSD([sQuery(id+"F41.wireOp",EDGE,"E32")])]})]});
            fillet(context, id + "F43", {"entities" : qUnion([Q0, Q1, Q2, Q3, Q4, Q5, Q6, Q7, Q8, Q9, Q10, Q11, Q12, Q13, Q14, Q15, Q16, Q17, Q18, Q19, Q20, Q21, Q22, Q23, Q24, Q25, Q26, Q27, Q28, Q29, Q30, Q31]), "radius" : 12 * mm, "tangentPropagation" : true, "allowEdgeOverflow" : false});
        }
        {
            var Q0;
            Q0=makeQuery(id+"F40.boolean.opBoolean","INTERSECT",EDGE,{"derivedFrom":[makeQuery(id+"F20.opLoft","SWEPT_FACE",FACE,{"disambiguationData":[OSD([sQuery(id+"F3.wireOp",EDGE,"E20.1.1"),sQuery(id+"F3.wireOp",EDGE,"E20.1.2"),sQuery(id+"F3.wireOp",EDGE,"E20.1.3"),sQuery(id+"F4.wireOp",EDGE,"E26.1.1"),sQuery(id+"F4.wireOp",EDGE,"E26.1.2"),sQuery(id+"F4.wireOp",EDGE,"E26.1.3")])]}),makeQuery(id+"F40.opExtrude","CAP_FACE",FACE,{"disambiguationData":[OSD([sQuery(id+"F39.wireOp",EDGE,"E29"),sQuery(id+"F39.wireOp",EDGE,"E30")])],"isStart":false})]});
            var Q1;
            Q1=makeQuery(id+"F40.boolean.opBoolean","INTERSECT",EDGE,{"derivedFrom":[makeQuery(id+"F32.opLoft","SWEPT_FACE",FACE,{"disambiguationData":[OSD([sQuery(id+"F3.wireOp",EDGE,"E20.1.1"),sQuery(id+"F3.wireOp",EDGE,"E20.1.2"),sQuery(id+"F3.wireOp",EDGE,"E20.1.3"),sQuery(id+"F22.wireOp",EDGE,"E28.9.0"),sQuery(id+"F22.wireOp",EDGE,"E28.9.2"),sQuery(id+"F22.wireOp",EDGE,"E28.9.3")])]}),makeQuery(id+"F40.opExtrude","CAP_FACE",FACE,{"disambiguationData":[OSD([sQuery(id+"F39.wireOp",EDGE,"E29"),sQuery(id+"F39.wireOp",EDGE,"E30")])],"isStart":true})]});
            var Q2;
            Q2=makeQuery(id+"F40.boolean.opBoolean","INTERSECT",EDGE,{"derivedFrom":[makeQuery(id+"F5.opLoft","SWEPT_FACE",FACE,{"disambiguationData":[OSD([sQuery(id+"F3.wireOp",EDGE,"E18.bottom"),sQuery(id+"F3.wireOp",EDGE,"E18.top"),sQuery(id+"F3.wireOp",EDGE,"E18.right"),sQuery(id+"F4.wireOp",EDGE,"E22"),sQuery(id+"F4.wireOp",EDGE,"E23"),sQuery(id+"F4.wireOp",EDGE,"E24")])]}),makeQuery(id+"F40.opExtrude","CAP_FACE",FACE,{"disambiguationData":[OSD([sQuery(id+"F39.wireOp",EDGE,"E29"),sQuery(id+"F39.wireOp",EDGE,"E30")])],"isStart":false})]});
            var Q3;
            Q3=makeQuery(id+"F40.boolean.opBoolean","INTERSECT",EDGE,{"derivedFrom":[makeQuery(id+"F31.opLoft","SWEPT_FACE",FACE,{"disambiguationData":[OSD([sQuery(id+"F3.wireOp",EDGE,"E18.bottom"),sQuery(id+"F3.wireOp",EDGE,"E18.top"),sQuery(id+"F3.wireOp",EDGE,"E18.right"),sQuery(id+"F22.wireOp",EDGE,"E28.8.0"),sQuery(id+"F22.wireOp",EDGE,"E28.8.2"),sQuery(id+"F22.wireOp",EDGE,"E28.8.3")])]}),makeQuery(id+"F40.opExtrude","CAP_FACE",FACE,{"disambiguationData":[OSD([sQuery(id+"F39.wireOp",EDGE,"E29"),sQuery(id+"F39.wireOp",EDGE,"E30")])],"isStart":true})]});
            var Q4;
            Q4=makeQuery(id+"F40.boolean.opBoolean","INTERSECT",EDGE,{"derivedFrom":[makeQuery(id+"F6.opLoft","SWEPT_FACE",FACE,{"disambiguationData":[OSD([sQuery(id+"F3.wireOp",EDGE,"E20.15.1"),sQuery(id+"F3.wireOp",EDGE,"E20.15.2"),sQuery(id+"F3.wireOp",EDGE,"E20.15.3"),sQuery(id+"F4.wireOp",EDGE,"E26.15.1"),sQuery(id+"F4.wireOp",EDGE,"E26.15.2"),sQuery(id+"F4.wireOp",EDGE,"E26.15.3")])]}),makeQuery(id+"F40.opExtrude","CAP_FACE",FACE,{"disambiguationData":[OSD([sQuery(id+"F39.wireOp",EDGE,"E29"),sQuery(id+"F39.wireOp",EDGE,"E30")])],"isStart":false})]});
            var Q5;
            Q5=makeQuery(id+"F40.boolean.opBoolean","INTERSECT",EDGE,{"derivedFrom":[makeQuery(id+"F30.opLoft","SWEPT_FACE",FACE,{"disambiguationData":[OSD([sQuery(id+"F3.wireOp",EDGE,"E20.15.1"),sQuery(id+"F3.wireOp",EDGE,"E20.15.2"),sQuery(id+"F3.wireOp",EDGE,"E20.15.3"),sQuery(id+"F22.wireOp",EDGE,"E28.7.0"),sQuery(id+"F22.wireOp",EDGE,"E28.7.2"),sQuery(id+"F22.wireOp",EDGE,"E28.7.3")])]}),makeQuery(id+"F40.opExtrude","CAP_FACE",FACE,{"disambiguationData":[OSD([sQuery(id+"F39.wireOp",EDGE,"E29"),sQuery(id+"F39.wireOp",EDGE,"E30")])],"isStart":true})]});
            var Q6;
            Q6=makeQuery(id+"F40.boolean.opBoolean","INTERSECT",EDGE,{"derivedFrom":[makeQuery(id+"F29.opLoft","SWEPT_FACE",FACE,{"disambiguationData":[OSD([sQuery(id+"F3.wireOp",EDGE,"E20.14.1"),sQuery(id+"F3.wireOp",EDGE,"E20.14.2"),sQuery(id+"F3.wireOp",EDGE,"E20.14.3"),sQuery(id+"F22.wireOp",EDGE,"E28.6.0"),sQuery(id+"F22.wireOp",EDGE,"E28.6.2"),sQuery(id+"F22.wireOp",EDGE,"E28.6.3")])]}),makeQuery(id+"F40.opExtrude","CAP_FACE",FACE,{"disambiguationData":[OSD([sQuery(id+"F39.wireOp",EDGE,"E29"),sQuery(id+"F39.wireOp",EDGE,"E30")])],"isStart":true})]});
            var Q7;
            Q7=makeQuery(id+"F40.boolean.opBoolean","INTERSECT",EDGE,{"derivedFrom":[makeQuery(id+"F28.opLoft","SWEPT_FACE",FACE,{"disambiguationData":[OSD([sQuery(id+"F3.wireOp",EDGE,"E20.13.1"),sQuery(id+"F3.wireOp",EDGE,"E20.13.2"),sQuery(id+"F3.wireOp",EDGE,"E20.13.3"),sQuery(id+"F22.wireOp",EDGE,"E28.5.0"),sQuery(id+"F22.wireOp",EDGE,"E28.5.2"),sQuery(id+"F22.wireOp",EDGE,"E28.5.3")])]}),makeQuery(id+"F40.opExtrude","CAP_FACE",FACE,{"disambiguationData":[OSD([sQuery(id+"F39.wireOp",EDGE,"E29"),sQuery(id+"F39.wireOp",EDGE,"E30")])],"isStart":true})]});
            var Q8;
            Q8=makeQuery(id+"F40.boolean.opBoolean","INTERSECT",EDGE,{"derivedFrom":[makeQuery(id+"F27.opLoft","SWEPT_FACE",FACE,{"disambiguationData":[OSD([sQuery(id+"F3.wireOp",EDGE,"E20.12.1"),sQuery(id+"F3.wireOp",EDGE,"E20.12.2"),sQuery(id+"F3.wireOp",EDGE,"E20.12.3"),sQuery(id+"F22.wireOp",EDGE,"E28.4.0"),sQuery(id+"F22.wireOp",EDGE,"E28.4.2"),sQuery(id+"F22.wireOp",EDGE,"E28.4.3")])]}),makeQuery(id+"F40.opExtrude","CAP_FACE",FACE,{"disambiguationData":[OSD([sQuery(id+"F39.wireOp",EDGE,"E29"),sQuery(id+"F39.wireOp",EDGE,"E30")])],"isStart":true})]});
            var Q9;
            Q9=makeQuery(id+"F40.boolean.opBoolean","INTERSECT",EDGE,{"derivedFrom":[makeQuery(id+"F26.opLoft","SWEPT_FACE",FACE,{"disambiguationData":[OSD([sQuery(id+"F3.wireOp",EDGE,"E20.11.1"),sQuery(id+"F3.wireOp",EDGE,"E20.11.2"),sQuery(id+"F3.wireOp",EDGE,"E20.11.3"),sQuery(id+"F22.wireOp",EDGE,"E28.3.0"),sQuery(id+"F22.wireOp",EDGE,"E28.3.2"),sQuery(id+"F22.wireOp",EDGE,"E28.3.3")])]}),makeQuery(id+"F40.opExtrude","CAP_FACE",FACE,{"disambiguationData":[OSD([sQuery(id+"F39.wireOp",EDGE,"E29"),sQuery(id+"F39.wireOp",EDGE,"E30")])],"isStart":true})]});
            var Q10;
            Q10=makeQuery(id+"F40.boolean.opBoolean","INTERSECT",EDGE,{"derivedFrom":[makeQuery(id+"F25.opLoft","SWEPT_FACE",FACE,{"disambiguationData":[OSD([sQuery(id+"F3.wireOp",EDGE,"E20.10.1"),sQuery(id+"F3.wireOp",EDGE,"E20.10.2"),sQuery(id+"F3.wireOp",EDGE,"E20.10.3"),sQuery(id+"F22.wireOp",EDGE,"E28.2.0"),sQuery(id+"F22.wireOp",EDGE,"E28.2.2"),sQuery(id+"F22.wireOp",EDGE,"E28.2.3")])]}),makeQuery(id+"F40.opExtrude","CAP_FACE",FACE,{"disambiguationData":[OSD([sQuery(id+"F39.wireOp",EDGE,"E29"),sQuery(id+"F39.wireOp",EDGE,"E30")])],"isStart":true})]});
            var Q11;
            Q11=makeQuery(id+"F40.boolean.opBoolean","INTERSECT",EDGE,{"derivedFrom":[makeQuery(id+"F24.opLoft","SWEPT_FACE",FACE,{"disambiguationData":[OSD([sQuery(id+"F3.wireOp",EDGE,"E20.9.1"),sQuery(id+"F3.wireOp",EDGE,"E20.9.2"),sQuery(id+"F3.wireOp",EDGE,"E20.9.3"),sQuery(id+"F22.wireOp",EDGE,"E28.1.0"),sQuery(id+"F22.wireOp",EDGE,"E28.1.2"),sQuery(id+"F22.wireOp",EDGE,"E28.1.3")])]}),makeQuery(id+"F40.opExtrude","CAP_FACE",FACE,{"disambiguationData":[OSD([sQuery(id+"F39.wireOp",EDGE,"E29"),sQuery(id+"F39.wireOp",EDGE,"E30")])],"isStart":true})]});
            var Q12;
            Q12=makeQuery(id+"F40.boolean.opBoolean","INTERSECT",EDGE,{"derivedFrom":[makeQuery(id+"F23.opLoft","SWEPT_FACE",FACE,{"disambiguationData":[OSD([sQuery(id+"F3.wireOp",EDGE,"E20.8.1"),sQuery(id+"F3.wireOp",EDGE,"E20.8.2"),sQuery(id+"F3.wireOp",EDGE,"E20.8.3"),sQuery(id+"F22.wireOp",EDGE,"E27.bottom"),sQuery(id+"F22.wireOp",EDGE,"E27.top"),sQuery(id+"F22.wireOp",EDGE,"E27.left")])]}),makeQuery(id+"F40.opExtrude","CAP_FACE",FACE,{"disambiguationData":[OSD([sQuery(id+"F39.wireOp",EDGE,"E29"),sQuery(id+"F39.wireOp",EDGE,"E30")])],"isStart":true})]});
            var Q13;
            Q13=makeQuery(id+"F40.boolean.opBoolean","INTERSECT",EDGE,{"derivedFrom":[makeQuery(id+"F38.opLoft","SWEPT_FACE",FACE,{"disambiguationData":[OSD([sQuery(id+"F3.wireOp",EDGE,"E20.7.1"),sQuery(id+"F3.wireOp",EDGE,"E20.7.2"),sQuery(id+"F3.wireOp",EDGE,"E20.7.3"),sQuery(id+"F22.wireOp",EDGE,"E28.15.0"),sQuery(id+"F22.wireOp",EDGE,"E28.15.2"),sQuery(id+"F22.wireOp",EDGE,"E28.15.3")])]}),makeQuery(id+"F40.opExtrude","CAP_FACE",FACE,{"disambiguationData":[OSD([sQuery(id+"F39.wireOp",EDGE,"E29"),sQuery(id+"F39.wireOp",EDGE,"E30")])],"isStart":true})]});
            var Q14;
            Q14=makeQuery(id+"F40.boolean.opBoolean","INTERSECT",EDGE,{"derivedFrom":[makeQuery(id+"F37.opLoft","SWEPT_FACE",FACE,{"disambiguationData":[OSD([sQuery(id+"F3.wireOp",EDGE,"E20.6.1"),sQuery(id+"F3.wireOp",EDGE,"E20.6.2"),sQuery(id+"F3.wireOp",EDGE,"E20.6.3"),sQuery(id+"F22.wireOp",EDGE,"E28.14.0"),sQuery(id+"F22.wireOp",EDGE,"E28.14.2"),sQuery(id+"F22.wireOp",EDGE,"E28.14.3")])]}),makeQuery(id+"F40.opExtrude","CAP_FACE",FACE,{"disambiguationData":[OSD([sQuery(id+"F39.wireOp",EDGE,"E29"),sQuery(id+"F39.wireOp",EDGE,"E30")])],"isStart":true})]});
            var Q15;
            Q15=makeQuery(id+"F40.boolean.opBoolean","INTERSECT",EDGE,{"derivedFrom":[makeQuery(id+"F36.opLoft","SWEPT_FACE",FACE,{"disambiguationData":[OSD([sQuery(id+"F3.wireOp",EDGE,"E20.5.1"),sQuery(id+"F3.wireOp",EDGE,"E20.5.2"),sQuery(id+"F3.wireOp",EDGE,"E20.5.3"),sQuery(id+"F22.wireOp",EDGE,"E28.13.0"),sQuery(id+"F22.wireOp",EDGE,"E28.13.2"),sQuery(id+"F22.wireOp",EDGE,"E28.13.3")])]}),makeQuery(id+"F40.opExtrude","CAP_FACE",FACE,{"disambiguationData":[OSD([sQuery(id+"F39.wireOp",EDGE,"E29"),sQuery(id+"F39.wireOp",EDGE,"E30")])],"isStart":true})]});
            var Q16;
            Q16=makeQuery(id+"F40.boolean.opBoolean","INTERSECT",EDGE,{"derivedFrom":[makeQuery(id+"F35.opLoft","SWEPT_FACE",FACE,{"disambiguationData":[OSD([sQuery(id+"F3.wireOp",EDGE,"E20.4.1"),sQuery(id+"F3.wireOp",EDGE,"E20.4.2"),sQuery(id+"F3.wireOp",EDGE,"E20.4.3"),sQuery(id+"F22.wireOp",EDGE,"E28.12.0"),sQuery(id+"F22.wireOp",EDGE,"E28.12.2"),sQuery(id+"F22.wireOp",EDGE,"E28.12.3")])]}),makeQuery(id+"F40.opExtrude","CAP_FACE",FACE,{"disambiguationData":[OSD([sQuery(id+"F39.wireOp",EDGE,"E29"),sQuery(id+"F39.wireOp",EDGE,"E30")])],"isStart":true})]});
            var Q17;
            Q17=makeQuery(id+"F40.boolean.opBoolean","INTERSECT",EDGE,{"derivedFrom":[makeQuery(id+"F34.opLoft","SWEPT_FACE",FACE,{"disambiguationData":[OSD([sQuery(id+"F3.wireOp",EDGE,"E20.3.1"),sQuery(id+"F3.wireOp",EDGE,"E20.3.2"),sQuery(id+"F3.wireOp",EDGE,"E20.3.3"),sQuery(id+"F22.wireOp",EDGE,"E28.11.0"),sQuery(id+"F22.wireOp",EDGE,"E28.11.2"),sQuery(id+"F22.wireOp",EDGE,"E28.11.3")])]}),makeQuery(id+"F40.opExtrude","CAP_FACE",FACE,{"disambiguationData":[OSD([sQuery(id+"F39.wireOp",EDGE,"E29"),sQuery(id+"F39.wireOp",EDGE,"E30")])],"isStart":true})]});
            var Q18;
            Q18=makeQuery(id+"F40.boolean.opBoolean","INTERSECT",EDGE,{"derivedFrom":[makeQuery(id+"F33.opLoft","SWEPT_FACE",FACE,{"disambiguationData":[OSD([sQuery(id+"F3.wireOp",EDGE,"E20.2.1"),sQuery(id+"F3.wireOp",EDGE,"E20.2.2"),sQuery(id+"F3.wireOp",EDGE,"E20.2.3"),sQuery(id+"F22.wireOp",EDGE,"E28.10.0"),sQuery(id+"F22.wireOp",EDGE,"E28.10.2"),sQuery(id+"F22.wireOp",EDGE,"E28.10.3")])]}),makeQuery(id+"F40.opExtrude","CAP_FACE",FACE,{"disambiguationData":[OSD([sQuery(id+"F39.wireOp",EDGE,"E29"),sQuery(id+"F39.wireOp",EDGE,"E30")])],"isStart":true})]});
            var Q19;
            Q19=makeQuery(id+"F40.boolean.opBoolean","INTERSECT",EDGE,{"derivedFrom":[makeQuery(id+"F19.opLoft","SWEPT_FACE",FACE,{"disambiguationData":[OSD([sQuery(id+"F3.wireOp",EDGE,"E20.2.1"),sQuery(id+"F3.wireOp",EDGE,"E20.2.2"),sQuery(id+"F3.wireOp",EDGE,"E20.2.3"),sQuery(id+"F4.wireOp",EDGE,"E26.2.1"),sQuery(id+"F4.wireOp",EDGE,"E26.2.2"),sQuery(id+"F4.wireOp",EDGE,"E26.2.3")])]}),makeQuery(id+"F40.opExtrude","CAP_FACE",FACE,{"disambiguationData":[OSD([sQuery(id+"F39.wireOp",EDGE,"E29"),sQuery(id+"F39.wireOp",EDGE,"E30")])],"isStart":false})]});
            var Q20;
            Q20=makeQuery(id+"F40.boolean.opBoolean","INTERSECT",EDGE,{"derivedFrom":[makeQuery(id+"F18.opLoft","SWEPT_FACE",FACE,{"disambiguationData":[OSD([sQuery(id+"F3.wireOp",EDGE,"E20.3.1"),sQuery(id+"F3.wireOp",EDGE,"E20.3.2"),sQuery(id+"F3.wireOp",EDGE,"E20.3.3"),sQuery(id+"F4.wireOp",EDGE,"E26.3.1"),sQuery(id+"F4.wireOp",EDGE,"E26.3.2"),sQuery(id+"F4.wireOp",EDGE,"E26.3.3")])]}),makeQuery(id+"F40.opExtrude","CAP_FACE",FACE,{"disambiguationData":[OSD([sQuery(id+"F39.wireOp",EDGE,"E29"),sQuery(id+"F39.wireOp",EDGE,"E30")])],"isStart":false})]});
            var Q21;
            Q21=makeQuery(id+"F40.boolean.opBoolean","INTERSECT",EDGE,{"derivedFrom":[makeQuery(id+"F17.opLoft","SWEPT_FACE",FACE,{"disambiguationData":[OSD([sQuery(id+"F3.wireOp",EDGE,"E20.4.1"),sQuery(id+"F3.wireOp",EDGE,"E20.4.2"),sQuery(id+"F3.wireOp",EDGE,"E20.4.3"),sQuery(id+"F4.wireOp",EDGE,"E26.4.1"),sQuery(id+"F4.wireOp",EDGE,"E26.4.2"),sQuery(id+"F4.wireOp",EDGE,"E26.4.3")])]}),makeQuery(id+"F40.opExtrude","CAP_FACE",FACE,{"disambiguationData":[OSD([sQuery(id+"F39.wireOp",EDGE,"E29"),sQuery(id+"F39.wireOp",EDGE,"E30")])],"isStart":false})]});
            var Q22;
            Q22=makeQuery(id+"F40.boolean.opBoolean","INTERSECT",EDGE,{"derivedFrom":[makeQuery(id+"F16.opLoft","SWEPT_FACE",FACE,{"disambiguationData":[OSD([sQuery(id+"F3.wireOp",EDGE,"E20.5.1"),sQuery(id+"F3.wireOp",EDGE,"E20.5.2"),sQuery(id+"F3.wireOp",EDGE,"E20.5.3"),sQuery(id+"F4.wireOp",EDGE,"E26.5.1"),sQuery(id+"F4.wireOp",EDGE,"E26.5.2"),sQuery(id+"F4.wireOp",EDGE,"E26.5.3")])]}),makeQuery(id+"F40.opExtrude","CAP_FACE",FACE,{"disambiguationData":[OSD([sQuery(id+"F39.wireOp",EDGE,"E29"),sQuery(id+"F39.wireOp",EDGE,"E30")])],"isStart":false})]});
            var Q23;
            Q23=makeQuery(id+"F40.boolean.opBoolean","INTERSECT",EDGE,{"derivedFrom":[makeQuery(id+"F15.opLoft","SWEPT_FACE",FACE,{"disambiguationData":[OSD([sQuery(id+"F3.wireOp",EDGE,"E20.6.1"),sQuery(id+"F3.wireOp",EDGE,"E20.6.2"),sQuery(id+"F3.wireOp",EDGE,"E20.6.3"),sQuery(id+"F4.wireOp",EDGE,"E26.6.1"),sQuery(id+"F4.wireOp",EDGE,"E26.6.2"),sQuery(id+"F4.wireOp",EDGE,"E26.6.3")])]}),makeQuery(id+"F40.opExtrude","CAP_FACE",FACE,{"disambiguationData":[OSD([sQuery(id+"F39.wireOp",EDGE,"E29"),sQuery(id+"F39.wireOp",EDGE,"E30")])],"isStart":false})]});
            var Q24;
            Q24=makeQuery(id+"F40.boolean.opBoolean","INTERSECT",EDGE,{"derivedFrom":[makeQuery(id+"F14.opLoft","SWEPT_FACE",FACE,{"disambiguationData":[OSD([sQuery(id+"F3.wireOp",EDGE,"E20.7.1"),sQuery(id+"F3.wireOp",EDGE,"E20.7.2"),sQuery(id+"F3.wireOp",EDGE,"E20.7.3"),sQuery(id+"F4.wireOp",EDGE,"E26.7.1"),sQuery(id+"F4.wireOp",EDGE,"E26.7.2"),sQuery(id+"F4.wireOp",EDGE,"E26.7.3")])]}),makeQuery(id+"F40.opExtrude","CAP_FACE",FACE,{"disambiguationData":[OSD([sQuery(id+"F39.wireOp",EDGE,"E29"),sQuery(id+"F39.wireOp",EDGE,"E30")])],"isStart":false})]});
            var Q25;
            Q25=makeQuery(id+"F40.boolean.opBoolean","INTERSECT",EDGE,{"derivedFrom":[makeQuery(id+"F13.opLoft","SWEPT_FACE",FACE,{"disambiguationData":[OSD([sQuery(id+"F3.wireOp",EDGE,"E20.8.1"),sQuery(id+"F3.wireOp",EDGE,"E20.8.2"),sQuery(id+"F3.wireOp",EDGE,"E20.8.3"),sQuery(id+"F4.wireOp",EDGE,"E26.8.1"),sQuery(id+"F4.wireOp",EDGE,"E26.8.2"),sQuery(id+"F4.wireOp",EDGE,"E26.8.3")])]}),makeQuery(id+"F40.opExtrude","CAP_FACE",FACE,{"disambiguationData":[OSD([sQuery(id+"F39.wireOp",EDGE,"E29"),sQuery(id+"F39.wireOp",EDGE,"E30")])],"isStart":false})]});
            var Q26;
            Q26=makeQuery(id+"F40.boolean.opBoolean","INTERSECT",EDGE,{"derivedFrom":[makeQuery(id+"F12.opLoft","SWEPT_FACE",FACE,{"disambiguationData":[OSD([sQuery(id+"F3.wireOp",EDGE,"E20.9.1"),sQuery(id+"F3.wireOp",EDGE,"E20.9.2"),sQuery(id+"F3.wireOp",EDGE,"E20.9.3"),sQuery(id+"F4.wireOp",EDGE,"E26.9.1"),sQuery(id+"F4.wireOp",EDGE,"E26.9.2"),sQuery(id+"F4.wireOp",EDGE,"E26.9.3")])]}),makeQuery(id+"F40.opExtrude","CAP_FACE",FACE,{"disambiguationData":[OSD([sQuery(id+"F39.wireOp",EDGE,"E29"),sQuery(id+"F39.wireOp",EDGE,"E30")])],"isStart":false})]});
            var Q27;
            Q27=makeQuery(id+"F40.boolean.opBoolean","INTERSECT",EDGE,{"derivedFrom":[makeQuery(id+"F11.opLoft","SWEPT_FACE",FACE,{"disambiguationData":[OSD([sQuery(id+"F3.wireOp",EDGE,"E20.10.1"),sQuery(id+"F3.wireOp",EDGE,"E20.10.2"),sQuery(id+"F3.wireOp",EDGE,"E20.10.3"),sQuery(id+"F4.wireOp",EDGE,"E26.10.1"),sQuery(id+"F4.wireOp",EDGE,"E26.10.2"),sQuery(id+"F4.wireOp",EDGE,"E26.10.3")])]}),makeQuery(id+"F40.opExtrude","CAP_FACE",FACE,{"disambiguationData":[OSD([sQuery(id+"F39.wireOp",EDGE,"E29"),sQuery(id+"F39.wireOp",EDGE,"E30")])],"isStart":false})]});
            var Q28;
            Q28=makeQuery(id+"F40.boolean.opBoolean","INTERSECT",EDGE,{"derivedFrom":[makeQuery(id+"F10.opLoft","SWEPT_FACE",FACE,{"disambiguationData":[OSD([sQuery(id+"F3.wireOp",EDGE,"E20.11.1"),sQuery(id+"F3.wireOp",EDGE,"E20.11.2"),sQuery(id+"F3.wireOp",EDGE,"E20.11.3"),sQuery(id+"F4.wireOp",EDGE,"E26.11.1"),sQuery(id+"F4.wireOp",EDGE,"E26.11.2"),sQuery(id+"F4.wireOp",EDGE,"E26.11.3")])]}),makeQuery(id+"F40.opExtrude","CAP_FACE",FACE,{"disambiguationData":[OSD([sQuery(id+"F39.wireOp",EDGE,"E29"),sQuery(id+"F39.wireOp",EDGE,"E30")])],"isStart":false})]});
            var Q29;
            Q29=makeQuery(id+"F40.boolean.opBoolean","INTERSECT",EDGE,{"derivedFrom":[makeQuery(id+"F9.opLoft","SWEPT_FACE",FACE,{"disambiguationData":[OSD([sQuery(id+"F3.wireOp",EDGE,"E20.12.1"),sQuery(id+"F3.wireOp",EDGE,"E20.12.2"),sQuery(id+"F3.wireOp",EDGE,"E20.12.3"),sQuery(id+"F4.wireOp",EDGE,"E26.12.1"),sQuery(id+"F4.wireOp",EDGE,"E26.12.2"),sQuery(id+"F4.wireOp",EDGE,"E26.12.3")])]}),makeQuery(id+"F40.opExtrude","CAP_FACE",FACE,{"disambiguationData":[OSD([sQuery(id+"F39.wireOp",EDGE,"E29"),sQuery(id+"F39.wireOp",EDGE,"E30")])],"isStart":false})]});
            var Q30;
            Q30=makeQuery(id+"F40.boolean.opBoolean","INTERSECT",EDGE,{"derivedFrom":[makeQuery(id+"F8.opLoft","SWEPT_FACE",FACE,{"disambiguationData":[OSD([sQuery(id+"F3.wireOp",EDGE,"E20.13.1"),sQuery(id+"F3.wireOp",EDGE,"E20.13.2"),sQuery(id+"F3.wireOp",EDGE,"E20.13.3"),sQuery(id+"F4.wireOp",EDGE,"E26.13.1"),sQuery(id+"F4.wireOp",EDGE,"E26.13.2"),sQuery(id+"F4.wireOp",EDGE,"E26.13.3")])]}),makeQuery(id+"F40.opExtrude","CAP_FACE",FACE,{"disambiguationData":[OSD([sQuery(id+"F39.wireOp",EDGE,"E29"),sQuery(id+"F39.wireOp",EDGE,"E30")])],"isStart":false})]});
            var Q31;
            Q31=makeQuery(id+"F40.boolean.opBoolean","INTERSECT",EDGE,{"derivedFrom":[makeQuery(id+"F7.opLoft","SWEPT_FACE",FACE,{"disambiguationData":[OSD([sQuery(id+"F3.wireOp",EDGE,"E20.14.1"),sQuery(id+"F3.wireOp",EDGE,"E20.14.2"),sQuery(id+"F3.wireOp",EDGE,"E20.14.3"),sQuery(id+"F4.wireOp",EDGE,"E26.14.1"),sQuery(id+"F4.wireOp",EDGE,"E26.14.2"),sQuery(id+"F4.wireOp",EDGE,"E26.14.3")])]}),makeQuery(id+"F40.opExtrude","CAP_FACE",FACE,{"disambiguationData":[OSD([sQuery(id+"F39.wireOp",EDGE,"E29"),sQuery(id+"F39.wireOp",EDGE,"E30")])],"isStart":false})]});
            fillet(context, id + "F44", {"entities" : qUnion([Q0, Q1, Q2, Q3, Q4, Q5, Q6, Q7, Q8, Q9, Q10, Q11, Q12, Q13, Q14, Q15, Q16, Q17, Q18, Q19, Q20, Q21, Q22, Q23, Q24, Q25, Q26, Q27, Q28, Q29, Q30, Q31]), "radius" : 25 * mm, "tangentPropagation" : true, "allowEdgeOverflow" : false});
        }
        {
            var Q0;
            {var subQ0=makeQuery(id+"F1.opRevolve","SWEPT_FACE",FACE,{"disambiguationData":[OSD([sQuery(id+"F0.wireOp",EDGE,"E10")])]});var subQ1=sQuery(id+"F4.wireOp",EDGE,"E23");var subQ2=sQuery(id+"F4.wireOp",EDGE,"E22");var subQ3=sQuery(id+"F3.wireOp",EDGE,"E18.right");var subQ4=sQuery(id+"F3.wireOp",EDGE,"E18.top");var subQ5=sQuery(id+"F3.wireOp",EDGE,"E18.bottom");var subQ6=makeQuery(id+"F5.opLoft","SWEPT_FACE",FACE,{"disambiguationData":[OSD([subQ5,subQ4,subQ3,subQ2,subQ1,sQuery(id+"F4.wireOp",EDGE,"E24")])]});var subQ13=makeQuery(id+"F40.opExtrude","CAP_FACE",FACE,{"disambiguationData":[OSD([sQuery(id+"F39.wireOp",EDGE,"E29"),sQuery(id+"F39.wireOp",EDGE,"E30")])],"isStart":false});var subQ58=makeQuery(id+"F5.opLoft","CAP_FACE",FACE,{"disambiguationData":[OSD([makeQuery(id+"F3.imprint","IMPRINT",FACE,{"disambiguationData":[TD([[makeQuery(id+"F3.imprint","IMPRINT",EDGE,{"derivedFrom":subQ5}),1.0]])]})])],"isStart":true});Q0=makeQuery(id+"F44.opFillet","BLEND_EDGE",EDGE,{"blendedFrom":[makeQuery(id+"F40.boolean.opBoolean","INTERSECT",EDGE,{"derivedFrom":[subQ6,subQ13]}),makeQuery(id+"F40.boolean.opBoolean","SPLIT",FACE,{"disambiguationData":[TD([subQ0])],"derivedFrom":makeQuery(id+"F31.boolean.opBoolean","SPLIT",FACE,{"disambiguationData":[TD([subQ6])],"derivedFrom":makeQuery(id+"F30.boolean.opBoolean","SPLIT",FACE,{"disambiguationData":[TD([subQ58])],"derivedFrom":makeQuery(id+"F29.boolean.opBoolean","SPLIT",FACE,{"disambiguationData":[TD([subQ58])],"derivedFrom":makeQuery(id+"F28.boolean.opBoolean","SPLIT",FACE,{"disambiguationData":[TD([subQ58])],"derivedFrom":makeQuery(id+"F27.boolean.opBoolean","SPLIT",FACE,{"disambiguationData":[TD([subQ58])],"derivedFrom":makeQuery(id+"F26.boolean.opBoolean","SPLIT",FACE,{"disambiguationData":[TD([subQ58])],"derivedFrom":makeQuery(id+"F25.boolean.opBoolean","SPLIT",FACE,{"disambiguationData":[TD([subQ58])],"derivedFrom":makeQuery(id+"F24.boolean.opBoolean","SPLIT",FACE,{"disambiguationData":[TD([subQ58])],"derivedFrom":makeQuery(id+"F1.opRevolve","SWEPT_FACE",FACE,{"disambiguationData":[OSD([sQuery(id+"F0.wireOp",EDGE,"E13")])]})})})})})})})})})})],"blendedInto":[makeQuery(id+"F40.boolean.opBoolean","SPLIT",FACE,{"disambiguationData":[TD([subQ0])],"derivedFrom":makeQuery(id+"F31.boolean.opBoolean","SPLIT",FACE,{"disambiguationData":[TD([subQ6])],"derivedFrom":makeQuery(id+"F30.boolean.opBoolean","SPLIT",FACE,{"disambiguationData":[TD([subQ58])],"derivedFrom":makeQuery(id+"F29.boolean.opBoolean","SPLIT",FACE,{"disambiguationData":[TD([subQ58])],"derivedFrom":makeQuery(id+"F28.boolean.opBoolean","SPLIT",FACE,{"disambiguationData":[TD([subQ58])],"derivedFrom":makeQuery(id+"F27.boolean.opBoolean","SPLIT",FACE,{"disambiguationData":[TD([subQ58])],"derivedFrom":makeQuery(id+"F26.boolean.opBoolean","SPLIT",FACE,{"disambiguationData":[TD([subQ58])],"derivedFrom":makeQuery(id+"F25.boolean.opBoolean","SPLIT",FACE,{"disambiguationData":[TD([subQ58])],"derivedFrom":makeQuery(id+"F24.boolean.opBoolean","SPLIT",FACE,{"disambiguationData":[TD([subQ58])],"derivedFrom":makeQuery(id+"F1.opRevolve","SWEPT_FACE",FACE,{"disambiguationData":[OSD([sQuery(id+"F0.wireOp",EDGE,"E13")])]})})})})})})})})})})]});}
            var Q1;
            {var subQ0=makeQuery(id+"F1.opRevolve","SWEPT_FACE",FACE,{"disambiguationData":[OSD([sQuery(id+"F0.wireOp",EDGE,"E10")])]});var subQ1=sQuery(id+"F4.wireOp",EDGE,"E23");var subQ2=sQuery(id+"F4.wireOp",EDGE,"E22");var subQ3=sQuery(id+"F3.wireOp",EDGE,"E18.left");var subQ4=sQuery(id+"F3.wireOp",EDGE,"E18.top");var subQ5=sQuery(id+"F3.wireOp",EDGE,"E18.bottom");var subQ6=makeQuery(id+"F5.opLoft","SWEPT_FACE",FACE,{"disambiguationData":[OSD([subQ5,subQ4,subQ3,sQuery(id+"F4.wireOp",EDGE,"E21"),subQ2,subQ1])]});var subQ7=sQuery(id+"F4.wireOp",EDGE,"E26.1.3");var subQ8=sQuery(id+"F4.wireOp",EDGE,"E26.1.2");var subQ9=sQuery(id+"F3.wireOp",EDGE,"E20.1.3");var subQ10=sQuery(id+"F3.wireOp",EDGE,"E20.1.2");var subQ11=sQuery(id+"F3.wireOp",EDGE,"E20.1.1");var subQ12=makeQuery(id+"F20.opLoft","SWEPT_FACE",FACE,{"disambiguationData":[OSD([subQ11,subQ10,subQ9,sQuery(id+"F4.wireOp",EDGE,"E26.1.1"),subQ8,subQ7])]});var subQ13=makeQuery(id+"F40.opExtrude","CAP_FACE",FACE,{"disambiguationData":[OSD([sQuery(id+"F39.wireOp",EDGE,"E29"),sQuery(id+"F39.wireOp",EDGE,"E30")])],"isStart":false});var subQ64=sQuery(id+"F3.wireOp",EDGE,"E20.7.0");var subQ72=makeQuery(id+"F14.opLoft","CAP_FACE",FACE,{"disambiguationData":[OSD([makeQuery(id+"F3.imprint","IMPRINT",FACE,{"disambiguationData":[TD([[makeQuery(id+"F3.imprint","IMPRINT",EDGE,{"derivedFrom":subQ64}),-1.0]])]})])],"isStart":true});var subQ80=makeQuery(id+"F5.opLoft","CAP_FACE",FACE,{"disambiguationData":[OSD([makeQuery(id+"F3.imprint","IMPRINT",FACE,{"disambiguationData":[TD([[makeQuery(id+"F3.imprint","IMPRINT",EDGE,{"derivedFrom":subQ5}),1.0]])]})])],"isStart":true});Q1=makeQuery(id+"F44.opFillet","BLEND_EDGE",EDGE,{"blendedFrom":[makeQuery(id+"F40.boolean.opBoolean","INTERSECT",EDGE,{"derivedFrom":[subQ12,subQ13]}),makeQuery(id+"F40.boolean.opBoolean","SPLIT",FACE,{"disambiguationData":[TD([subQ0])],"derivedFrom":makeQuery(id+"F32.boolean.opBoolean","SPLIT",FACE,{"disambiguationData":[TD([subQ6])],"derivedFrom":makeQuery(id+"F31.boolean.opBoolean","SPLIT",FACE,{"disambiguationData":[TD([subQ72])],"derivedFrom":makeQuery(id+"F30.boolean.opBoolean","SPLIT",FACE,{"disambiguationData":[TD([subQ80])],"derivedFrom":makeQuery(id+"F29.boolean.opBoolean","SPLIT",FACE,{"disambiguationData":[TD([subQ80])],"derivedFrom":makeQuery(id+"F28.boolean.opBoolean","SPLIT",FACE,{"disambiguationData":[TD([subQ80])],"derivedFrom":makeQuery(id+"F27.boolean.opBoolean","SPLIT",FACE,{"disambiguationData":[TD([subQ80])],"derivedFrom":makeQuery(id+"F26.boolean.opBoolean","SPLIT",FACE,{"disambiguationData":[TD([subQ80])],"derivedFrom":makeQuery(id+"F25.boolean.opBoolean","SPLIT",FACE,{"disambiguationData":[TD([subQ80])],"derivedFrom":makeQuery(id+"F24.boolean.opBoolean","SPLIT",FACE,{"disambiguationData":[TD([subQ80])],"derivedFrom":makeQuery(id+"F1.opRevolve","SWEPT_FACE",FACE,{"disambiguationData":[OSD([sQuery(id+"F0.wireOp",EDGE,"E13")])]})})})})})})})})})})})],"blendedInto":[makeQuery(id+"F40.boolean.opBoolean","SPLIT",FACE,{"disambiguationData":[TD([subQ0])],"derivedFrom":makeQuery(id+"F32.boolean.opBoolean","SPLIT",FACE,{"disambiguationData":[TD([subQ6])],"derivedFrom":makeQuery(id+"F31.boolean.opBoolean","SPLIT",FACE,{"disambiguationData":[TD([subQ72])],"derivedFrom":makeQuery(id+"F30.boolean.opBoolean","SPLIT",FACE,{"disambiguationData":[TD([subQ80])],"derivedFrom":makeQuery(id+"F29.boolean.opBoolean","SPLIT",FACE,{"disambiguationData":[TD([subQ80])],"derivedFrom":makeQuery(id+"F28.boolean.opBoolean","SPLIT",FACE,{"disambiguationData":[TD([subQ80])],"derivedFrom":makeQuery(id+"F27.boolean.opBoolean","SPLIT",FACE,{"disambiguationData":[TD([subQ80])],"derivedFrom":makeQuery(id+"F26.boolean.opBoolean","SPLIT",FACE,{"disambiguationData":[TD([subQ80])],"derivedFrom":makeQuery(id+"F25.boolean.opBoolean","SPLIT",FACE,{"disambiguationData":[TD([subQ80])],"derivedFrom":makeQuery(id+"F24.boolean.opBoolean","SPLIT",FACE,{"disambiguationData":[TD([subQ80])],"derivedFrom":makeQuery(id+"F1.opRevolve","SWEPT_FACE",FACE,{"disambiguationData":[OSD([sQuery(id+"F0.wireOp",EDGE,"E13")])]})})})})})})})})})})})]});}
            var Q2;
            {var subQ0=makeQuery(id+"F1.opRevolve","SWEPT_FACE",FACE,{"disambiguationData":[OSD([sQuery(id+"F0.wireOp",EDGE,"E10")])]});var subQ1=sQuery(id+"F4.wireOp",EDGE,"E26.2.3");var subQ2=sQuery(id+"F4.wireOp",EDGE,"E26.2.2");var subQ3=sQuery(id+"F3.wireOp",EDGE,"E20.2.3");var subQ4=sQuery(id+"F3.wireOp",EDGE,"E20.2.2");var subQ5=sQuery(id+"F3.wireOp",EDGE,"E20.2.1");var subQ6=makeQuery(id+"F19.opLoft","SWEPT_FACE",FACE,{"disambiguationData":[OSD([subQ5,subQ4,subQ3,sQuery(id+"F4.wireOp",EDGE,"E26.2.1"),subQ2,subQ1])]});var subQ13=makeQuery(id+"F40.opExtrude","CAP_FACE",FACE,{"disambiguationData":[OSD([sQuery(id+"F39.wireOp",EDGE,"E29"),sQuery(id+"F39.wireOp",EDGE,"E30")])],"isStart":false});var subQ55=sQuery(id+"F3.wireOp",EDGE,"E20.7.0");var subQ62=makeQuery(id+"F14.opLoft","CAP_FACE",FACE,{"disambiguationData":[OSD([makeQuery(id+"F3.imprint","IMPRINT",FACE,{"disambiguationData":[TD([[makeQuery(id+"F3.imprint","IMPRINT",EDGE,{"derivedFrom":subQ55}),-1.0]])]})])],"isStart":true});var subQ75=sQuery(id+"F3.wireOp",EDGE,"E18.bottom");var subQ80=makeQuery(id+"F5.opLoft","CAP_FACE",FACE,{"disambiguationData":[OSD([makeQuery(id+"F3.imprint","IMPRINT",FACE,{"disambiguationData":[TD([[makeQuery(id+"F3.imprint","IMPRINT",EDGE,{"derivedFrom":subQ75}),1.0]])]})])],"isStart":true});Q2=makeQuery(id+"F44.opFillet","BLEND_EDGE",EDGE,{"blendedFrom":[makeQuery(id+"F40.boolean.opBoolean","INTERSECT",EDGE,{"derivedFrom":[subQ6,subQ13]}),makeQuery(id+"F40.boolean.opBoolean","SPLIT",FACE,{"disambiguationData":[TD([subQ0])],"derivedFrom":makeQuery(id+"F33.boolean.opBoolean","SPLIT",FACE,{"disambiguationData":[TD([subQ6])],"derivedFrom":makeQuery(id+"F32.boolean.opBoolean","SPLIT",FACE,{"disambiguationData":[TD([subQ62])],"derivedFrom":makeQuery(id+"F31.boolean.opBoolean","SPLIT",FACE,{"disambiguationData":[TD([subQ62])],"derivedFrom":makeQuery(id+"F30.boolean.opBoolean","SPLIT",FACE,{"disambiguationData":[TD([subQ80])],"derivedFrom":makeQuery(id+"F29.boolean.opBoolean","SPLIT",FACE,{"disambiguationData":[TD([subQ80])],"derivedFrom":makeQuery(id+"F28.boolean.opBoolean","SPLIT",FACE,{"disambiguationData":[TD([subQ80])],"derivedFrom":makeQuery(id+"F27.boolean.opBoolean","SPLIT",FACE,{"disambiguationData":[TD([subQ80])],"derivedFrom":makeQuery(id+"F26.boolean.opBoolean","SPLIT",FACE,{"disambiguationData":[TD([subQ80])],"derivedFrom":makeQuery(id+"F25.boolean.opBoolean","SPLIT",FACE,{"disambiguationData":[TD([subQ80])],"derivedFrom":makeQuery(id+"F24.boolean.opBoolean","SPLIT",FACE,{"disambiguationData":[TD([subQ80])],"derivedFrom":makeQuery(id+"F1.opRevolve","SWEPT_FACE",FACE,{"disambiguationData":[OSD([sQuery(id+"F0.wireOp",EDGE,"E13")])]})})})})})})})})})})})})],"blendedInto":[makeQuery(id+"F40.boolean.opBoolean","SPLIT",FACE,{"disambiguationData":[TD([subQ0])],"derivedFrom":makeQuery(id+"F33.boolean.opBoolean","SPLIT",FACE,{"disambiguationData":[TD([subQ6])],"derivedFrom":makeQuery(id+"F32.boolean.opBoolean","SPLIT",FACE,{"disambiguationData":[TD([subQ62])],"derivedFrom":makeQuery(id+"F31.boolean.opBoolean","SPLIT",FACE,{"disambiguationData":[TD([subQ62])],"derivedFrom":makeQuery(id+"F30.boolean.opBoolean","SPLIT",FACE,{"disambiguationData":[TD([subQ80])],"derivedFrom":makeQuery(id+"F29.boolean.opBoolean","SPLIT",FACE,{"disambiguationData":[TD([subQ80])],"derivedFrom":makeQuery(id+"F28.boolean.opBoolean","SPLIT",FACE,{"disambiguationData":[TD([subQ80])],"derivedFrom":makeQuery(id+"F27.boolean.opBoolean","SPLIT",FACE,{"disambiguationData":[TD([subQ80])],"derivedFrom":makeQuery(id+"F26.boolean.opBoolean","SPLIT",FACE,{"disambiguationData":[TD([subQ80])],"derivedFrom":makeQuery(id+"F25.boolean.opBoolean","SPLIT",FACE,{"disambiguationData":[TD([subQ80])],"derivedFrom":makeQuery(id+"F24.boolean.opBoolean","SPLIT",FACE,{"disambiguationData":[TD([subQ80])],"derivedFrom":makeQuery(id+"F1.opRevolve","SWEPT_FACE",FACE,{"disambiguationData":[OSD([sQuery(id+"F0.wireOp",EDGE,"E13")])]})})})})})})})})})})})})]});}
            var Q3;
            {var subQ0=makeQuery(id+"F1.opRevolve","SWEPT_FACE",FACE,{"disambiguationData":[OSD([sQuery(id+"F0.wireOp",EDGE,"E12")])]});var subQ5=sQuery(id+"F3.wireOp",EDGE,"E20.2.3");var subQ6=sQuery(id+"F3.wireOp",EDGE,"E20.2.2");var subQ7=sQuery(id+"F3.wireOp",EDGE,"E20.2.1");var subQ8=makeQuery(id+"F33.opLoft","SWEPT_FACE",FACE,{"disambiguationData":[OSD([subQ7,subQ6,subQ5,sQuery(id+"F22.wireOp",EDGE,"E28.10.0"),sQuery(id+"F22.wireOp",EDGE,"E28.10.2"),sQuery(id+"F22.wireOp",EDGE,"E28.10.3")])]});var subQ9=makeQuery(id+"F40.opExtrude","CAP_FACE",FACE,{"disambiguationData":[OSD([sQuery(id+"F39.wireOp",EDGE,"E29"),sQuery(id+"F39.wireOp",EDGE,"E30")])],"isStart":true});var subQ13=sQuery(id+"F4.wireOp",EDGE,"E26.2.3");var subQ14=sQuery(id+"F4.wireOp",EDGE,"E26.2.2");var subQ15=makeQuery(id+"F19.opLoft","SWEPT_FACE",FACE,{"disambiguationData":[OSD([subQ7,subQ6,subQ5,sQuery(id+"F4.wireOp",EDGE,"E26.2.1"),subQ14,subQ13])]});var subQ56=sQuery(id+"F3.wireOp",EDGE,"E20.7.0");var subQ63=makeQuery(id+"F14.opLoft","CAP_FACE",FACE,{"disambiguationData":[OSD([makeQuery(id+"F3.imprint","IMPRINT",FACE,{"disambiguationData":[TD([[makeQuery(id+"F3.imprint","IMPRINT",EDGE,{"derivedFrom":subQ56}),-1.0]])]})])],"isStart":true});var subQ76=sQuery(id+"F3.wireOp",EDGE,"E18.bottom");var subQ81=makeQuery(id+"F5.opLoft","CAP_FACE",FACE,{"disambiguationData":[OSD([makeQuery(id+"F3.imprint","IMPRINT",FACE,{"disambiguationData":[TD([[makeQuery(id+"F3.imprint","IMPRINT",EDGE,{"derivedFrom":subQ76}),1.0]])]})])],"isStart":true});Q3=makeQuery(id+"F44.opFillet","BLEND_EDGE",EDGE,{"blendedFrom":[makeQuery(id+"F40.boolean.opBoolean","INTERSECT",EDGE,{"derivedFrom":[subQ8,subQ9]}),makeQuery(id+"F40.boolean.opBoolean","SPLIT",FACE,{"disambiguationData":[TD([subQ0])],"derivedFrom":makeQuery(id+"F33.boolean.opBoolean","SPLIT",FACE,{"disambiguationData":[TD([subQ15])],"derivedFrom":makeQuery(id+"F32.boolean.opBoolean","SPLIT",FACE,{"disambiguationData":[TD([subQ63])],"derivedFrom":makeQuery(id+"F31.boolean.opBoolean","SPLIT",FACE,{"disambiguationData":[TD([subQ63])],"derivedFrom":makeQuery(id+"F30.boolean.opBoolean","SPLIT",FACE,{"disambiguationData":[TD([subQ81])],"derivedFrom":makeQuery(id+"F29.boolean.opBoolean","SPLIT",FACE,{"disambiguationData":[TD([subQ81])],"derivedFrom":makeQuery(id+"F28.boolean.opBoolean","SPLIT",FACE,{"disambiguationData":[TD([subQ81])],"derivedFrom":makeQuery(id+"F27.boolean.opBoolean","SPLIT",FACE,{"disambiguationData":[TD([subQ81])],"derivedFrom":makeQuery(id+"F26.boolean.opBoolean","SPLIT",FACE,{"disambiguationData":[TD([subQ81])],"derivedFrom":makeQuery(id+"F25.boolean.opBoolean","SPLIT",FACE,{"disambiguationData":[TD([subQ81])],"derivedFrom":makeQuery(id+"F24.boolean.opBoolean","SPLIT",FACE,{"disambiguationData":[TD([subQ81])],"derivedFrom":makeQuery(id+"F1.opRevolve","SWEPT_FACE",FACE,{"disambiguationData":[OSD([sQuery(id+"F0.wireOp",EDGE,"E13")])]})})})})})})})})})})})})],"blendedInto":[makeQuery(id+"F40.boolean.opBoolean","SPLIT",FACE,{"disambiguationData":[TD([subQ0])],"derivedFrom":makeQuery(id+"F33.boolean.opBoolean","SPLIT",FACE,{"disambiguationData":[TD([subQ15])],"derivedFrom":makeQuery(id+"F32.boolean.opBoolean","SPLIT",FACE,{"disambiguationData":[TD([subQ63])],"derivedFrom":makeQuery(id+"F31.boolean.opBoolean","SPLIT",FACE,{"disambiguationData":[TD([subQ63])],"derivedFrom":makeQuery(id+"F30.boolean.opBoolean","SPLIT",FACE,{"disambiguationData":[TD([subQ81])],"derivedFrom":makeQuery(id+"F29.boolean.opBoolean","SPLIT",FACE,{"disambiguationData":[TD([subQ81])],"derivedFrom":makeQuery(id+"F28.boolean.opBoolean","SPLIT",FACE,{"disambiguationData":[TD([subQ81])],"derivedFrom":makeQuery(id+"F27.boolean.opBoolean","SPLIT",FACE,{"disambiguationData":[TD([subQ81])],"derivedFrom":makeQuery(id+"F26.boolean.opBoolean","SPLIT",FACE,{"disambiguationData":[TD([subQ81])],"derivedFrom":makeQuery(id+"F25.boolean.opBoolean","SPLIT",FACE,{"disambiguationData":[TD([subQ81])],"derivedFrom":makeQuery(id+"F24.boolean.opBoolean","SPLIT",FACE,{"disambiguationData":[TD([subQ81])],"derivedFrom":makeQuery(id+"F1.opRevolve","SWEPT_FACE",FACE,{"disambiguationData":[OSD([sQuery(id+"F0.wireOp",EDGE,"E13")])]})})})})})})})})})})})})]});}
            var Q4;
            {var subQ0=makeQuery(id+"F1.opRevolve","SWEPT_FACE",FACE,{"disambiguationData":[OSD([sQuery(id+"F0.wireOp",EDGE,"E12")])]});var subQ1=sQuery(id+"F3.wireOp",EDGE,"E20.1.3");var subQ2=sQuery(id+"F3.wireOp",EDGE,"E20.1.2");var subQ3=sQuery(id+"F3.wireOp",EDGE,"E20.1.1");var subQ4=makeQuery(id+"F32.opLoft","SWEPT_FACE",FACE,{"disambiguationData":[OSD([subQ3,subQ2,subQ1,sQuery(id+"F22.wireOp",EDGE,"E28.9.0"),sQuery(id+"F22.wireOp",EDGE,"E28.9.2"),sQuery(id+"F22.wireOp",EDGE,"E28.9.3")])]});var subQ5=sQuery(id+"F3.wireOp",EDGE,"E18.left");var subQ6=sQuery(id+"F3.wireOp",EDGE,"E18.top");var subQ7=sQuery(id+"F3.wireOp",EDGE,"E18.bottom");var subQ9=makeQuery(id+"F40.opExtrude","CAP_FACE",FACE,{"disambiguationData":[OSD([sQuery(id+"F39.wireOp",EDGE,"E29"),sQuery(id+"F39.wireOp",EDGE,"E30")])],"isStart":true});var subQ13=sQuery(id+"F4.wireOp",EDGE,"E23");var subQ14=sQuery(id+"F4.wireOp",EDGE,"E22");var subQ15=makeQuery(id+"F5.opLoft","SWEPT_FACE",FACE,{"disambiguationData":[OSD([subQ7,subQ6,subQ5,sQuery(id+"F4.wireOp",EDGE,"E21"),subQ14,subQ13])]});var subQ65=sQuery(id+"F3.wireOp",EDGE,"E20.7.0");var subQ73=makeQuery(id+"F14.opLoft","CAP_FACE",FACE,{"disambiguationData":[OSD([makeQuery(id+"F3.imprint","IMPRINT",FACE,{"disambiguationData":[TD([[makeQuery(id+"F3.imprint","IMPRINT",EDGE,{"derivedFrom":subQ65}),-1.0]])]})])],"isStart":true});var subQ81=makeQuery(id+"F5.opLoft","CAP_FACE",FACE,{"disambiguationData":[OSD([makeQuery(id+"F3.imprint","IMPRINT",FACE,{"disambiguationData":[TD([[makeQuery(id+"F3.imprint","IMPRINT",EDGE,{"derivedFrom":subQ7}),1.0]])]})])],"isStart":true});Q4=makeQuery(id+"F44.opFillet","BLEND_EDGE",EDGE,{"blendedFrom":[makeQuery(id+"F40.boolean.opBoolean","INTERSECT",EDGE,{"derivedFrom":[subQ4,subQ9]}),makeQuery(id+"F40.boolean.opBoolean","SPLIT",FACE,{"disambiguationData":[TD([subQ0])],"derivedFrom":makeQuery(id+"F32.boolean.opBoolean","SPLIT",FACE,{"disambiguationData":[TD([subQ15])],"derivedFrom":makeQuery(id+"F31.boolean.opBoolean","SPLIT",FACE,{"disambiguationData":[TD([subQ73])],"derivedFrom":makeQuery(id+"F30.boolean.opBoolean","SPLIT",FACE,{"disambiguationData":[TD([subQ81])],"derivedFrom":makeQuery(id+"F29.boolean.opBoolean","SPLIT",FACE,{"disambiguationData":[TD([subQ81])],"derivedFrom":makeQuery(id+"F28.boolean.opBoolean","SPLIT",FACE,{"disambiguationData":[TD([subQ81])],"derivedFrom":makeQuery(id+"F27.boolean.opBoolean","SPLIT",FACE,{"disambiguationData":[TD([subQ81])],"derivedFrom":makeQuery(id+"F26.boolean.opBoolean","SPLIT",FACE,{"disambiguationData":[TD([subQ81])],"derivedFrom":makeQuery(id+"F25.boolean.opBoolean","SPLIT",FACE,{"disambiguationData":[TD([subQ81])],"derivedFrom":makeQuery(id+"F24.boolean.opBoolean","SPLIT",FACE,{"disambiguationData":[TD([subQ81])],"derivedFrom":makeQuery(id+"F1.opRevolve","SWEPT_FACE",FACE,{"disambiguationData":[OSD([sQuery(id+"F0.wireOp",EDGE,"E13")])]})})})})})})})})})})})],"blendedInto":[makeQuery(id+"F40.boolean.opBoolean","SPLIT",FACE,{"disambiguationData":[TD([subQ0])],"derivedFrom":makeQuery(id+"F32.boolean.opBoolean","SPLIT",FACE,{"disambiguationData":[TD([subQ15])],"derivedFrom":makeQuery(id+"F31.boolean.opBoolean","SPLIT",FACE,{"disambiguationData":[TD([subQ73])],"derivedFrom":makeQuery(id+"F30.boolean.opBoolean","SPLIT",FACE,{"disambiguationData":[TD([subQ81])],"derivedFrom":makeQuery(id+"F29.boolean.opBoolean","SPLIT",FACE,{"disambiguationData":[TD([subQ81])],"derivedFrom":makeQuery(id+"F28.boolean.opBoolean","SPLIT",FACE,{"disambiguationData":[TD([subQ81])],"derivedFrom":makeQuery(id+"F27.boolean.opBoolean","SPLIT",FACE,{"disambiguationData":[TD([subQ81])],"derivedFrom":makeQuery(id+"F26.boolean.opBoolean","SPLIT",FACE,{"disambiguationData":[TD([subQ81])],"derivedFrom":makeQuery(id+"F25.boolean.opBoolean","SPLIT",FACE,{"disambiguationData":[TD([subQ81])],"derivedFrom":makeQuery(id+"F24.boolean.opBoolean","SPLIT",FACE,{"disambiguationData":[TD([subQ81])],"derivedFrom":makeQuery(id+"F1.opRevolve","SWEPT_FACE",FACE,{"disambiguationData":[OSD([sQuery(id+"F0.wireOp",EDGE,"E13")])]})})})})})})})})})})})]});}
            var Q5;
            {var subQ0=makeQuery(id+"F1.opRevolve","SWEPT_FACE",FACE,{"disambiguationData":[OSD([sQuery(id+"F0.wireOp",EDGE,"E12")])]});var subQ1=sQuery(id+"F3.wireOp",EDGE,"E18.right");var subQ2=sQuery(id+"F3.wireOp",EDGE,"E18.top");var subQ3=sQuery(id+"F3.wireOp",EDGE,"E18.bottom");var subQ4=makeQuery(id+"F31.opLoft","SWEPT_FACE",FACE,{"disambiguationData":[OSD([subQ3,subQ2,subQ1,sQuery(id+"F22.wireOp",EDGE,"E28.8.0"),sQuery(id+"F22.wireOp",EDGE,"E28.8.2"),sQuery(id+"F22.wireOp",EDGE,"E28.8.3")])]});var subQ9=makeQuery(id+"F40.opExtrude","CAP_FACE",FACE,{"disambiguationData":[OSD([sQuery(id+"F39.wireOp",EDGE,"E29"),sQuery(id+"F39.wireOp",EDGE,"E30")])],"isStart":true});var subQ13=sQuery(id+"F4.wireOp",EDGE,"E23");var subQ14=sQuery(id+"F4.wireOp",EDGE,"E22");var subQ15=makeQuery(id+"F5.opLoft","SWEPT_FACE",FACE,{"disambiguationData":[OSD([subQ3,subQ2,subQ1,subQ14,subQ13,sQuery(id+"F4.wireOp",EDGE,"E24")])]});var subQ59=makeQuery(id+"F5.opLoft","CAP_FACE",FACE,{"disambiguationData":[OSD([makeQuery(id+"F3.imprint","IMPRINT",FACE,{"disambiguationData":[TD([[makeQuery(id+"F3.imprint","IMPRINT",EDGE,{"derivedFrom":subQ3}),1.0]])]})])],"isStart":true});Q5=makeQuery(id+"F44.opFillet","BLEND_EDGE",EDGE,{"blendedFrom":[makeQuery(id+"F40.boolean.opBoolean","INTERSECT",EDGE,{"derivedFrom":[subQ4,subQ9]}),makeQuery(id+"F40.boolean.opBoolean","SPLIT",FACE,{"disambiguationData":[TD([subQ0])],"derivedFrom":makeQuery(id+"F31.boolean.opBoolean","SPLIT",FACE,{"disambiguationData":[TD([subQ15])],"derivedFrom":makeQuery(id+"F30.boolean.opBoolean","SPLIT",FACE,{"disambiguationData":[TD([subQ59])],"derivedFrom":makeQuery(id+"F29.boolean.opBoolean","SPLIT",FACE,{"disambiguationData":[TD([subQ59])],"derivedFrom":makeQuery(id+"F28.boolean.opBoolean","SPLIT",FACE,{"disambiguationData":[TD([subQ59])],"derivedFrom":makeQuery(id+"F27.boolean.opBoolean","SPLIT",FACE,{"disambiguationData":[TD([subQ59])],"derivedFrom":makeQuery(id+"F26.boolean.opBoolean","SPLIT",FACE,{"disambiguationData":[TD([subQ59])],"derivedFrom":makeQuery(id+"F25.boolean.opBoolean","SPLIT",FACE,{"disambiguationData":[TD([subQ59])],"derivedFrom":makeQuery(id+"F24.boolean.opBoolean","SPLIT",FACE,{"disambiguationData":[TD([subQ59])],"derivedFrom":makeQuery(id+"F1.opRevolve","SWEPT_FACE",FACE,{"disambiguationData":[OSD([sQuery(id+"F0.wireOp",EDGE,"E13")])]})})})})})})})})})})],"blendedInto":[makeQuery(id+"F40.boolean.opBoolean","SPLIT",FACE,{"disambiguationData":[TD([subQ0])],"derivedFrom":makeQuery(id+"F31.boolean.opBoolean","SPLIT",FACE,{"disambiguationData":[TD([subQ15])],"derivedFrom":makeQuery(id+"F30.boolean.opBoolean","SPLIT",FACE,{"disambiguationData":[TD([subQ59])],"derivedFrom":makeQuery(id+"F29.boolean.opBoolean","SPLIT",FACE,{"disambiguationData":[TD([subQ59])],"derivedFrom":makeQuery(id+"F28.boolean.opBoolean","SPLIT",FACE,{"disambiguationData":[TD([subQ59])],"derivedFrom":makeQuery(id+"F27.boolean.opBoolean","SPLIT",FACE,{"disambiguationData":[TD([subQ59])],"derivedFrom":makeQuery(id+"F26.boolean.opBoolean","SPLIT",FACE,{"disambiguationData":[TD([subQ59])],"derivedFrom":makeQuery(id+"F25.boolean.opBoolean","SPLIT",FACE,{"disambiguationData":[TD([subQ59])],"derivedFrom":makeQuery(id+"F24.boolean.opBoolean","SPLIT",FACE,{"disambiguationData":[TD([subQ59])],"derivedFrom":makeQuery(id+"F1.opRevolve","SWEPT_FACE",FACE,{"disambiguationData":[OSD([sQuery(id+"F0.wireOp",EDGE,"E13")])]})})})})})})})})})})]});}
            var Q6;
            {var subQ0=makeQuery(id+"F1.opRevolve","SWEPT_FACE",FACE,{"disambiguationData":[OSD([sQuery(id+"F0.wireOp",EDGE,"E12")])]});var subQ5=sQuery(id+"F3.wireOp",EDGE,"E20.15.3");var subQ6=sQuery(id+"F3.wireOp",EDGE,"E20.15.2");var subQ7=sQuery(id+"F3.wireOp",EDGE,"E20.15.1");var subQ8=makeQuery(id+"F30.opLoft","SWEPT_FACE",FACE,{"disambiguationData":[OSD([subQ7,subQ6,subQ5,sQuery(id+"F22.wireOp",EDGE,"E28.7.0"),sQuery(id+"F22.wireOp",EDGE,"E28.7.2"),sQuery(id+"F22.wireOp",EDGE,"E28.7.3")])]});var subQ9=makeQuery(id+"F40.opExtrude","CAP_FACE",FACE,{"disambiguationData":[OSD([sQuery(id+"F39.wireOp",EDGE,"E29"),sQuery(id+"F39.wireOp",EDGE,"E30")])],"isStart":true});var subQ10=sQuery(id+"F4.wireOp",EDGE,"E26.15.3");var subQ11=sQuery(id+"F4.wireOp",EDGE,"E26.15.2");var subQ12=makeQuery(id+"F6.opLoft","SWEPT_FACE",FACE,{"disambiguationData":[OSD([subQ7,subQ6,subQ5,sQuery(id+"F4.wireOp",EDGE,"E26.15.1"),subQ11,subQ10])]});var subQ48=sQuery(id+"F3.wireOp",EDGE,"E18.bottom");var subQ51=makeQuery(id+"F5.opLoft","CAP_FACE",FACE,{"disambiguationData":[OSD([makeQuery(id+"F3.imprint","IMPRINT",FACE,{"disambiguationData":[TD([[makeQuery(id+"F3.imprint","IMPRINT",EDGE,{"derivedFrom":subQ48}),1.0]])]})])],"isStart":true});Q6=makeQuery(id+"F44.opFillet","BLEND_EDGE",EDGE,{"blendedFrom":[makeQuery(id+"F40.boolean.opBoolean","INTERSECT",EDGE,{"derivedFrom":[subQ8,subQ9]}),makeQuery(id+"F40.boolean.opBoolean","SPLIT",FACE,{"disambiguationData":[TD([subQ0])],"derivedFrom":makeQuery(id+"F30.boolean.opBoolean","SPLIT",FACE,{"disambiguationData":[TD([subQ12])],"derivedFrom":makeQuery(id+"F29.boolean.opBoolean","SPLIT",FACE,{"disambiguationData":[TD([subQ51])],"derivedFrom":makeQuery(id+"F28.boolean.opBoolean","SPLIT",FACE,{"disambiguationData":[TD([subQ51])],"derivedFrom":makeQuery(id+"F27.boolean.opBoolean","SPLIT",FACE,{"disambiguationData":[TD([subQ51])],"derivedFrom":makeQuery(id+"F26.boolean.opBoolean","SPLIT",FACE,{"disambiguationData":[TD([subQ51])],"derivedFrom":makeQuery(id+"F25.boolean.opBoolean","SPLIT",FACE,{"disambiguationData":[TD([subQ51])],"derivedFrom":makeQuery(id+"F24.boolean.opBoolean","SPLIT",FACE,{"disambiguationData":[TD([subQ51])],"derivedFrom":makeQuery(id+"F1.opRevolve","SWEPT_FACE",FACE,{"disambiguationData":[OSD([sQuery(id+"F0.wireOp",EDGE,"E13")])]})})})})})})})})})],"blendedInto":[makeQuery(id+"F40.boolean.opBoolean","SPLIT",FACE,{"disambiguationData":[TD([subQ0])],"derivedFrom":makeQuery(id+"F30.boolean.opBoolean","SPLIT",FACE,{"disambiguationData":[TD([subQ12])],"derivedFrom":makeQuery(id+"F29.boolean.opBoolean","SPLIT",FACE,{"disambiguationData":[TD([subQ51])],"derivedFrom":makeQuery(id+"F28.boolean.opBoolean","SPLIT",FACE,{"disambiguationData":[TD([subQ51])],"derivedFrom":makeQuery(id+"F27.boolean.opBoolean","SPLIT",FACE,{"disambiguationData":[TD([subQ51])],"derivedFrom":makeQuery(id+"F26.boolean.opBoolean","SPLIT",FACE,{"disambiguationData":[TD([subQ51])],"derivedFrom":makeQuery(id+"F25.boolean.opBoolean","SPLIT",FACE,{"disambiguationData":[TD([subQ51])],"derivedFrom":makeQuery(id+"F24.boolean.opBoolean","SPLIT",FACE,{"disambiguationData":[TD([subQ51])],"derivedFrom":makeQuery(id+"F1.opRevolve","SWEPT_FACE",FACE,{"disambiguationData":[OSD([sQuery(id+"F0.wireOp",EDGE,"E13")])]})})})})})})})})})]});}
            var Q7;
            {var subQ0=makeQuery(id+"F1.opRevolve","SWEPT_FACE",FACE,{"disambiguationData":[OSD([sQuery(id+"F0.wireOp",EDGE,"E12")])]});var subQ5=sQuery(id+"F3.wireOp",EDGE,"E20.14.3");var subQ6=sQuery(id+"F3.wireOp",EDGE,"E20.14.2");var subQ7=sQuery(id+"F3.wireOp",EDGE,"E20.14.1");var subQ8=makeQuery(id+"F29.opLoft","SWEPT_FACE",FACE,{"disambiguationData":[OSD([subQ7,subQ6,subQ5,sQuery(id+"F22.wireOp",EDGE,"E28.6.0"),sQuery(id+"F22.wireOp",EDGE,"E28.6.2"),sQuery(id+"F22.wireOp",EDGE,"E28.6.3")])]});var subQ9=makeQuery(id+"F40.opExtrude","CAP_FACE",FACE,{"disambiguationData":[OSD([sQuery(id+"F39.wireOp",EDGE,"E29"),sQuery(id+"F39.wireOp",EDGE,"E30")])],"isStart":true});var subQ13=sQuery(id+"F4.wireOp",EDGE,"E26.14.3");var subQ14=sQuery(id+"F4.wireOp",EDGE,"E26.14.2");var subQ15=makeQuery(id+"F7.opLoft","SWEPT_FACE",FACE,{"disambiguationData":[OSD([subQ7,subQ6,subQ5,sQuery(id+"F4.wireOp",EDGE,"E26.14.1"),subQ14,subQ13])]});var subQ49=sQuery(id+"F3.wireOp",EDGE,"E18.bottom");var subQ52=makeQuery(id+"F5.opLoft","CAP_FACE",FACE,{"disambiguationData":[OSD([makeQuery(id+"F3.imprint","IMPRINT",FACE,{"disambiguationData":[TD([[makeQuery(id+"F3.imprint","IMPRINT",EDGE,{"derivedFrom":subQ49}),1.0]])]})])],"isStart":true});Q7=makeQuery(id+"F44.opFillet","BLEND_EDGE",EDGE,{"blendedFrom":[makeQuery(id+"F40.boolean.opBoolean","INTERSECT",EDGE,{"derivedFrom":[subQ8,subQ9]}),makeQuery(id+"F40.boolean.opBoolean","SPLIT",FACE,{"disambiguationData":[TD([subQ0])],"derivedFrom":makeQuery(id+"F29.boolean.opBoolean","SPLIT",FACE,{"disambiguationData":[TD([subQ15])],"derivedFrom":makeQuery(id+"F28.boolean.opBoolean","SPLIT",FACE,{"disambiguationData":[TD([subQ52])],"derivedFrom":makeQuery(id+"F27.boolean.opBoolean","SPLIT",FACE,{"disambiguationData":[TD([subQ52])],"derivedFrom":makeQuery(id+"F26.boolean.opBoolean","SPLIT",FACE,{"disambiguationData":[TD([subQ52])],"derivedFrom":makeQuery(id+"F25.boolean.opBoolean","SPLIT",FACE,{"disambiguationData":[TD([subQ52])],"derivedFrom":makeQuery(id+"F24.boolean.opBoolean","SPLIT",FACE,{"disambiguationData":[TD([subQ52])],"derivedFrom":makeQuery(id+"F1.opRevolve","SWEPT_FACE",FACE,{"disambiguationData":[OSD([sQuery(id+"F0.wireOp",EDGE,"E13")])]})})})})})})})})],"blendedInto":[makeQuery(id+"F40.boolean.opBoolean","SPLIT",FACE,{"disambiguationData":[TD([subQ0])],"derivedFrom":makeQuery(id+"F29.boolean.opBoolean","SPLIT",FACE,{"disambiguationData":[TD([subQ15])],"derivedFrom":makeQuery(id+"F28.boolean.opBoolean","SPLIT",FACE,{"disambiguationData":[TD([subQ52])],"derivedFrom":makeQuery(id+"F27.boolean.opBoolean","SPLIT",FACE,{"disambiguationData":[TD([subQ52])],"derivedFrom":makeQuery(id+"F26.boolean.opBoolean","SPLIT",FACE,{"disambiguationData":[TD([subQ52])],"derivedFrom":makeQuery(id+"F25.boolean.opBoolean","SPLIT",FACE,{"disambiguationData":[TD([subQ52])],"derivedFrom":makeQuery(id+"F24.boolean.opBoolean","SPLIT",FACE,{"disambiguationData":[TD([subQ52])],"derivedFrom":makeQuery(id+"F1.opRevolve","SWEPT_FACE",FACE,{"disambiguationData":[OSD([sQuery(id+"F0.wireOp",EDGE,"E13")])]})})})})})})})})]});}
            var Q8;
            {var subQ0=makeQuery(id+"F1.opRevolve","SWEPT_FACE",FACE,{"disambiguationData":[OSD([sQuery(id+"F0.wireOp",EDGE,"E12")])]});var subQ5=sQuery(id+"F3.wireOp",EDGE,"E20.13.3");var subQ6=sQuery(id+"F3.wireOp",EDGE,"E20.13.2");var subQ7=sQuery(id+"F3.wireOp",EDGE,"E20.13.1");var subQ8=makeQuery(id+"F28.opLoft","SWEPT_FACE",FACE,{"disambiguationData":[OSD([subQ7,subQ6,subQ5,sQuery(id+"F22.wireOp",EDGE,"E28.5.0"),sQuery(id+"F22.wireOp",EDGE,"E28.5.2"),sQuery(id+"F22.wireOp",EDGE,"E28.5.3")])]});var subQ9=makeQuery(id+"F40.opExtrude","CAP_FACE",FACE,{"disambiguationData":[OSD([sQuery(id+"F39.wireOp",EDGE,"E29"),sQuery(id+"F39.wireOp",EDGE,"E30")])],"isStart":true});var subQ13=sQuery(id+"F4.wireOp",EDGE,"E26.13.3");var subQ14=sQuery(id+"F4.wireOp",EDGE,"E26.13.2");var subQ15=makeQuery(id+"F8.opLoft","SWEPT_FACE",FACE,{"disambiguationData":[OSD([subQ7,subQ6,subQ5,sQuery(id+"F4.wireOp",EDGE,"E26.13.1"),subQ14,subQ13])]});var subQ57=sQuery(id+"F3.wireOp",EDGE,"E18.bottom");var subQ60=makeQuery(id+"F5.opLoft","CAP_FACE",FACE,{"disambiguationData":[OSD([makeQuery(id+"F3.imprint","IMPRINT",FACE,{"disambiguationData":[TD([[makeQuery(id+"F3.imprint","IMPRINT",EDGE,{"derivedFrom":subQ57}),1.0]])]})])],"isStart":true});Q8=makeQuery(id+"F44.opFillet","BLEND_EDGE",EDGE,{"blendedFrom":[makeQuery(id+"F40.boolean.opBoolean","INTERSECT",EDGE,{"derivedFrom":[subQ8,subQ9]}),makeQuery(id+"F40.boolean.opBoolean","SPLIT",FACE,{"disambiguationData":[TD([subQ0])],"derivedFrom":makeQuery(id+"F28.boolean.opBoolean","SPLIT",FACE,{"disambiguationData":[TD([subQ15])],"derivedFrom":makeQuery(id+"F27.boolean.opBoolean","SPLIT",FACE,{"disambiguationData":[TD([subQ60])],"derivedFrom":makeQuery(id+"F26.boolean.opBoolean","SPLIT",FACE,{"disambiguationData":[TD([subQ60])],"derivedFrom":makeQuery(id+"F25.boolean.opBoolean","SPLIT",FACE,{"disambiguationData":[TD([subQ60])],"derivedFrom":makeQuery(id+"F24.boolean.opBoolean","SPLIT",FACE,{"disambiguationData":[TD([subQ60])],"derivedFrom":makeQuery(id+"F1.opRevolve","SWEPT_FACE",FACE,{"disambiguationData":[OSD([sQuery(id+"F0.wireOp",EDGE,"E13")])]})})})})})})})],"blendedInto":[makeQuery(id+"F40.boolean.opBoolean","SPLIT",FACE,{"disambiguationData":[TD([subQ0])],"derivedFrom":makeQuery(id+"F28.boolean.opBoolean","SPLIT",FACE,{"disambiguationData":[TD([subQ15])],"derivedFrom":makeQuery(id+"F27.boolean.opBoolean","SPLIT",FACE,{"disambiguationData":[TD([subQ60])],"derivedFrom":makeQuery(id+"F26.boolean.opBoolean","SPLIT",FACE,{"disambiguationData":[TD([subQ60])],"derivedFrom":makeQuery(id+"F25.boolean.opBoolean","SPLIT",FACE,{"disambiguationData":[TD([subQ60])],"derivedFrom":makeQuery(id+"F24.boolean.opBoolean","SPLIT",FACE,{"disambiguationData":[TD([subQ60])],"derivedFrom":makeQuery(id+"F1.opRevolve","SWEPT_FACE",FACE,{"disambiguationData":[OSD([sQuery(id+"F0.wireOp",EDGE,"E13")])]})})})})})})})]});}
            var Q9;
            {var subQ0=makeQuery(id+"F1.opRevolve","SWEPT_FACE",FACE,{"disambiguationData":[OSD([sQuery(id+"F0.wireOp",EDGE,"E12")])]});var subQ5=sQuery(id+"F3.wireOp",EDGE,"E20.12.3");var subQ6=sQuery(id+"F3.wireOp",EDGE,"E20.12.2");var subQ7=sQuery(id+"F3.wireOp",EDGE,"E20.12.1");var subQ8=makeQuery(id+"F27.opLoft","SWEPT_FACE",FACE,{"disambiguationData":[OSD([subQ7,subQ6,subQ5,sQuery(id+"F22.wireOp",EDGE,"E28.4.0"),sQuery(id+"F22.wireOp",EDGE,"E28.4.2"),sQuery(id+"F22.wireOp",EDGE,"E28.4.3")])]});var subQ9=makeQuery(id+"F40.opExtrude","CAP_FACE",FACE,{"disambiguationData":[OSD([sQuery(id+"F39.wireOp",EDGE,"E29"),sQuery(id+"F39.wireOp",EDGE,"E30")])],"isStart":true});var subQ13=sQuery(id+"F4.wireOp",EDGE,"E26.12.3");var subQ14=sQuery(id+"F4.wireOp",EDGE,"E26.12.2");var subQ15=makeQuery(id+"F9.opLoft","SWEPT_FACE",FACE,{"disambiguationData":[OSD([subQ7,subQ6,subQ5,sQuery(id+"F4.wireOp",EDGE,"E26.12.1"),subQ14,subQ13])]});var subQ75=sQuery(id+"F3.wireOp",EDGE,"E18.bottom");var subQ78=makeQuery(id+"F5.opLoft","CAP_FACE",FACE,{"disambiguationData":[OSD([makeQuery(id+"F3.imprint","IMPRINT",FACE,{"disambiguationData":[TD([[makeQuery(id+"F3.imprint","IMPRINT",EDGE,{"derivedFrom":subQ75}),1.0]])]})])],"isStart":true});Q9=makeQuery(id+"F44.opFillet","BLEND_EDGE",EDGE,{"blendedFrom":[makeQuery(id+"F40.boolean.opBoolean","INTERSECT",EDGE,{"derivedFrom":[subQ8,subQ9]}),makeQuery(id+"F40.boolean.opBoolean","SPLIT",FACE,{"disambiguationData":[TD([subQ0])],"derivedFrom":makeQuery(id+"F27.boolean.opBoolean","SPLIT",FACE,{"disambiguationData":[TD([subQ15])],"derivedFrom":makeQuery(id+"F26.boolean.opBoolean","SPLIT",FACE,{"disambiguationData":[TD([subQ78])],"derivedFrom":makeQuery(id+"F25.boolean.opBoolean","SPLIT",FACE,{"disambiguationData":[TD([subQ78])],"derivedFrom":makeQuery(id+"F24.boolean.opBoolean","SPLIT",FACE,{"disambiguationData":[TD([subQ78])],"derivedFrom":makeQuery(id+"F1.opRevolve","SWEPT_FACE",FACE,{"disambiguationData":[OSD([sQuery(id+"F0.wireOp",EDGE,"E13")])]})})})})})})],"blendedInto":[makeQuery(id+"F40.boolean.opBoolean","SPLIT",FACE,{"disambiguationData":[TD([subQ0])],"derivedFrom":makeQuery(id+"F27.boolean.opBoolean","SPLIT",FACE,{"disambiguationData":[TD([subQ15])],"derivedFrom":makeQuery(id+"F26.boolean.opBoolean","SPLIT",FACE,{"disambiguationData":[TD([subQ78])],"derivedFrom":makeQuery(id+"F25.boolean.opBoolean","SPLIT",FACE,{"disambiguationData":[TD([subQ78])],"derivedFrom":makeQuery(id+"F24.boolean.opBoolean","SPLIT",FACE,{"disambiguationData":[TD([subQ78])],"derivedFrom":makeQuery(id+"F1.opRevolve","SWEPT_FACE",FACE,{"disambiguationData":[OSD([sQuery(id+"F0.wireOp",EDGE,"E13")])]})})})})})})]});}
            var Q10;
            {var subQ0=makeQuery(id+"F1.opRevolve","SWEPT_FACE",FACE,{"disambiguationData":[OSD([sQuery(id+"F0.wireOp",EDGE,"E12")])]});var subQ5=sQuery(id+"F3.wireOp",EDGE,"E20.11.3");var subQ6=sQuery(id+"F3.wireOp",EDGE,"E20.11.2");var subQ7=sQuery(id+"F3.wireOp",EDGE,"E20.11.1");var subQ8=makeQuery(id+"F26.opLoft","SWEPT_FACE",FACE,{"disambiguationData":[OSD([subQ7,subQ6,subQ5,sQuery(id+"F22.wireOp",EDGE,"E28.3.0"),sQuery(id+"F22.wireOp",EDGE,"E28.3.2"),sQuery(id+"F22.wireOp",EDGE,"E28.3.3")])]});var subQ9=makeQuery(id+"F40.opExtrude","CAP_FACE",FACE,{"disambiguationData":[OSD([sQuery(id+"F39.wireOp",EDGE,"E29"),sQuery(id+"F39.wireOp",EDGE,"E30")])],"isStart":true});var subQ13=sQuery(id+"F4.wireOp",EDGE,"E26.11.3");var subQ14=sQuery(id+"F4.wireOp",EDGE,"E26.11.2");var subQ15=makeQuery(id+"F10.opLoft","SWEPT_FACE",FACE,{"disambiguationData":[OSD([subQ7,subQ6,subQ5,sQuery(id+"F4.wireOp",EDGE,"E26.11.1"),subQ14,subQ13])]});var subQ80=sQuery(id+"F3.wireOp",EDGE,"E18.bottom");var subQ83=makeQuery(id+"F5.opLoft","CAP_FACE",FACE,{"disambiguationData":[OSD([makeQuery(id+"F3.imprint","IMPRINT",FACE,{"disambiguationData":[TD([[makeQuery(id+"F3.imprint","IMPRINT",EDGE,{"derivedFrom":subQ80}),1.0]])]})])],"isStart":true});Q10=makeQuery(id+"F44.opFillet","BLEND_EDGE",EDGE,{"blendedFrom":[makeQuery(id+"F40.boolean.opBoolean","INTERSECT",EDGE,{"derivedFrom":[subQ8,subQ9]}),makeQuery(id+"F40.boolean.opBoolean","SPLIT",FACE,{"disambiguationData":[TD([subQ0])],"derivedFrom":makeQuery(id+"F26.boolean.opBoolean","SPLIT",FACE,{"disambiguationData":[TD([subQ15])],"derivedFrom":makeQuery(id+"F25.boolean.opBoolean","SPLIT",FACE,{"disambiguationData":[TD([subQ83])],"derivedFrom":makeQuery(id+"F24.boolean.opBoolean","SPLIT",FACE,{"disambiguationData":[TD([subQ83])],"derivedFrom":makeQuery(id+"F1.opRevolve","SWEPT_FACE",FACE,{"disambiguationData":[OSD([sQuery(id+"F0.wireOp",EDGE,"E13")])]})})})})})],"blendedInto":[makeQuery(id+"F40.boolean.opBoolean","SPLIT",FACE,{"disambiguationData":[TD([subQ0])],"derivedFrom":makeQuery(id+"F26.boolean.opBoolean","SPLIT",FACE,{"disambiguationData":[TD([subQ15])],"derivedFrom":makeQuery(id+"F25.boolean.opBoolean","SPLIT",FACE,{"disambiguationData":[TD([subQ83])],"derivedFrom":makeQuery(id+"F24.boolean.opBoolean","SPLIT",FACE,{"disambiguationData":[TD([subQ83])],"derivedFrom":makeQuery(id+"F1.opRevolve","SWEPT_FACE",FACE,{"disambiguationData":[OSD([sQuery(id+"F0.wireOp",EDGE,"E13")])]})})})})})]});}
            var Q11;
            {var subQ0=makeQuery(id+"F1.opRevolve","SWEPT_FACE",FACE,{"disambiguationData":[OSD([sQuery(id+"F0.wireOp",EDGE,"E12")])]});var subQ5=sQuery(id+"F3.wireOp",EDGE,"E20.10.3");var subQ6=sQuery(id+"F3.wireOp",EDGE,"E20.10.2");var subQ7=sQuery(id+"F3.wireOp",EDGE,"E20.10.1");var subQ8=makeQuery(id+"F25.opLoft","SWEPT_FACE",FACE,{"disambiguationData":[OSD([subQ7,subQ6,subQ5,sQuery(id+"F22.wireOp",EDGE,"E28.2.0"),sQuery(id+"F22.wireOp",EDGE,"E28.2.2"),sQuery(id+"F22.wireOp",EDGE,"E28.2.3")])]});var subQ9=makeQuery(id+"F40.opExtrude","CAP_FACE",FACE,{"disambiguationData":[OSD([sQuery(id+"F39.wireOp",EDGE,"E29"),sQuery(id+"F39.wireOp",EDGE,"E30")])],"isStart":true});var subQ12=sQuery(id+"F4.wireOp",EDGE,"E26.10.3");var subQ13=sQuery(id+"F4.wireOp",EDGE,"E26.10.2");var subQ14=makeQuery(id+"F11.opLoft","SWEPT_FACE",FACE,{"disambiguationData":[OSD([subQ7,subQ6,subQ5,sQuery(id+"F4.wireOp",EDGE,"E26.10.1"),subQ13,subQ12])]});var subQ90=sQuery(id+"F3.wireOp",EDGE,"E18.bottom");Q11=makeQuery(id+"F44.opFillet","BLEND_EDGE",EDGE,{"blendedFrom":[makeQuery(id+"F40.boolean.opBoolean","INTERSECT",EDGE,{"derivedFrom":[subQ8,subQ9]}),makeQuery(id+"F40.boolean.opBoolean","SPLIT",FACE,{"disambiguationData":[TD([subQ0])],"derivedFrom":makeQuery(id+"F25.boolean.opBoolean","SPLIT",FACE,{"disambiguationData":[TD([subQ14])],"derivedFrom":makeQuery(id+"F24.boolean.opBoolean","SPLIT",FACE,{"disambiguationData":[TD([makeQuery(id+"F5.opLoft","CAP_FACE",FACE,{"disambiguationData":[OSD([makeQuery(id+"F3.imprint","IMPRINT",FACE,{"disambiguationData":[TD([[makeQuery(id+"F3.imprint","IMPRINT",EDGE,{"derivedFrom":subQ90}),1.0]])]})])],"isStart":true})])],"derivedFrom":makeQuery(id+"F1.opRevolve","SWEPT_FACE",FACE,{"disambiguationData":[OSD([sQuery(id+"F0.wireOp",EDGE,"E13")])]})})})})],"blendedInto":[makeQuery(id+"F40.boolean.opBoolean","SPLIT",FACE,{"disambiguationData":[TD([subQ0])],"derivedFrom":makeQuery(id+"F25.boolean.opBoolean","SPLIT",FACE,{"disambiguationData":[TD([subQ14])],"derivedFrom":makeQuery(id+"F24.boolean.opBoolean","SPLIT",FACE,{"disambiguationData":[TD([makeQuery(id+"F5.opLoft","CAP_FACE",FACE,{"disambiguationData":[OSD([makeQuery(id+"F3.imprint","IMPRINT",FACE,{"disambiguationData":[TD([[makeQuery(id+"F3.imprint","IMPRINT",EDGE,{"derivedFrom":subQ90}),1.0]])]})])],"isStart":true})])],"derivedFrom":makeQuery(id+"F1.opRevolve","SWEPT_FACE",FACE,{"disambiguationData":[OSD([sQuery(id+"F0.wireOp",EDGE,"E13")])]})})})})]});}
            var Q12;
            {var subQ0=makeQuery(id+"F1.opRevolve","SWEPT_FACE",FACE,{"disambiguationData":[OSD([sQuery(id+"F0.wireOp",EDGE,"E12")])]});var subQ1=sQuery(id+"F3.wireOp",EDGE,"E20.9.3");var subQ2=sQuery(id+"F3.wireOp",EDGE,"E20.9.2");var subQ3=sQuery(id+"F3.wireOp",EDGE,"E20.9.1");var subQ4=makeQuery(id+"F24.opLoft","SWEPT_FACE",FACE,{"disambiguationData":[OSD([subQ3,subQ2,subQ1,sQuery(id+"F22.wireOp",EDGE,"E28.1.0"),sQuery(id+"F22.wireOp",EDGE,"E28.1.2"),sQuery(id+"F22.wireOp",EDGE,"E28.1.3")])]});var subQ9=makeQuery(id+"F40.opExtrude","CAP_FACE",FACE,{"disambiguationData":[OSD([sQuery(id+"F39.wireOp",EDGE,"E29"),sQuery(id+"F39.wireOp",EDGE,"E30")])],"isStart":true});Q12=makeQuery(id+"F44.opFillet","BLEND_EDGE",EDGE,{"blendedFrom":[makeQuery(id+"F40.boolean.opBoolean","INTERSECT",EDGE,{"derivedFrom":[subQ4,subQ9]}),makeQuery(id+"F40.boolean.opBoolean","SPLIT",FACE,{"disambiguationData":[TD([subQ0])],"derivedFrom":makeQuery(id+"F24.boolean.opBoolean","SPLIT",FACE,{"disambiguationData":[TD([makeQuery(id+"F12.opLoft","SWEPT_FACE",FACE,{"disambiguationData":[OSD([subQ3,subQ2,subQ1,sQuery(id+"F4.wireOp",EDGE,"E26.9.1"),sQuery(id+"F4.wireOp",EDGE,"E26.9.2"),sQuery(id+"F4.wireOp",EDGE,"E26.9.3")])]})])],"derivedFrom":makeQuery(id+"F1.opRevolve","SWEPT_FACE",FACE,{"disambiguationData":[OSD([sQuery(id+"F0.wireOp",EDGE,"E13")])]})})})],"blendedInto":[makeQuery(id+"F40.boolean.opBoolean","SPLIT",FACE,{"disambiguationData":[TD([subQ0])],"derivedFrom":makeQuery(id+"F24.boolean.opBoolean","SPLIT",FACE,{"disambiguationData":[TD([makeQuery(id+"F12.opLoft","SWEPT_FACE",FACE,{"disambiguationData":[OSD([subQ3,subQ2,subQ1,sQuery(id+"F4.wireOp",EDGE,"E26.9.1"),sQuery(id+"F4.wireOp",EDGE,"E26.9.2"),sQuery(id+"F4.wireOp",EDGE,"E26.9.3")])]})])],"derivedFrom":makeQuery(id+"F1.opRevolve","SWEPT_FACE",FACE,{"disambiguationData":[OSD([sQuery(id+"F0.wireOp",EDGE,"E13")])]})})})]});}
            var Q13;
            {var subQ0=makeQuery(id+"F1.opRevolve","SWEPT_FACE",FACE,{"disambiguationData":[OSD([sQuery(id+"F0.wireOp",EDGE,"E12")])]});var subQ1=sQuery(id+"F3.wireOp",EDGE,"E20.8.3");var subQ2=sQuery(id+"F3.wireOp",EDGE,"E20.8.2");var subQ3=sQuery(id+"F3.wireOp",EDGE,"E20.8.1");var subQ4=makeQuery(id+"F23.opLoft","SWEPT_FACE",FACE,{"disambiguationData":[OSD([subQ3,subQ2,subQ1,sQuery(id+"F22.wireOp",EDGE,"E27.bottom"),sQuery(id+"F22.wireOp",EDGE,"E27.top"),sQuery(id+"F22.wireOp",EDGE,"E27.left")])]});var subQ7=sQuery(id+"F3.wireOp",EDGE,"E20.7.0");var subQ9=makeQuery(id+"F40.opExtrude","CAP_FACE",FACE,{"disambiguationData":[OSD([sQuery(id+"F39.wireOp",EDGE,"E29"),sQuery(id+"F39.wireOp",EDGE,"E30")])],"isStart":true});var subQ10=makeQuery(id+"F13.opLoft","SWEPT_FACE",FACE,{"disambiguationData":[OSD([subQ3,subQ2,subQ1,sQuery(id+"F4.wireOp",EDGE,"E26.8.1"),sQuery(id+"F4.wireOp",EDGE,"E26.8.2"),sQuery(id+"F4.wireOp",EDGE,"E26.8.3")])]});var subQ17=makeQuery(id+"F14.opLoft","CAP_FACE",FACE,{"disambiguationData":[OSD([makeQuery(id+"F3.imprint","IMPRINT",FACE,{"disambiguationData":[TD([[makeQuery(id+"F3.imprint","IMPRINT",EDGE,{"derivedFrom":subQ7}),-1.0]])]})])],"isStart":true});var subQ75=sQuery(id+"F3.wireOp",EDGE,"E18.bottom");var subQ80=makeQuery(id+"F5.opLoft","CAP_FACE",FACE,{"disambiguationData":[OSD([makeQuery(id+"F3.imprint","IMPRINT",FACE,{"disambiguationData":[TD([[makeQuery(id+"F3.imprint","IMPRINT",EDGE,{"derivedFrom":subQ75}),1.0]])]})])],"isStart":true});Q13=makeQuery(id+"F44.opFillet","BLEND_EDGE",EDGE,{"blendedFrom":[makeQuery(id+"F40.boolean.opBoolean","INTERSECT",EDGE,{"derivedFrom":[subQ4,subQ9]}),makeQuery(id+"F40.boolean.opBoolean","SPLIT",FACE,{"disambiguationData":[TD([subQ0])],"derivedFrom":makeQuery(id+"F38.boolean.opBoolean","SPLIT",FACE,{"disambiguationData":[TD([subQ10])],"derivedFrom":makeQuery(id+"F37.boolean.opBoolean","SPLIT",FACE,{"disambiguationData":[TD([subQ17])],"derivedFrom":makeQuery(id+"F36.boolean.opBoolean","SPLIT",FACE,{"disambiguationData":[TD([subQ17])],"derivedFrom":makeQuery(id+"F35.boolean.opBoolean","SPLIT",FACE,{"disambiguationData":[TD([subQ17])],"derivedFrom":makeQuery(id+"F34.boolean.opBoolean","SPLIT",FACE,{"disambiguationData":[TD([subQ17])],"derivedFrom":makeQuery(id+"F33.boolean.opBoolean","SPLIT",FACE,{"disambiguationData":[TD([subQ17])],"derivedFrom":makeQuery(id+"F32.boolean.opBoolean","SPLIT",FACE,{"disambiguationData":[TD([subQ17])],"derivedFrom":makeQuery(id+"F31.boolean.opBoolean","SPLIT",FACE,{"disambiguationData":[TD([subQ17])],"derivedFrom":makeQuery(id+"F30.boolean.opBoolean","SPLIT",FACE,{"disambiguationData":[TD([subQ80])],"derivedFrom":makeQuery(id+"F29.boolean.opBoolean","SPLIT",FACE,{"disambiguationData":[TD([subQ80])],"derivedFrom":makeQuery(id+"F28.boolean.opBoolean","SPLIT",FACE,{"disambiguationData":[TD([subQ80])],"derivedFrom":makeQuery(id+"F27.boolean.opBoolean","SPLIT",FACE,{"disambiguationData":[TD([subQ80])],"derivedFrom":makeQuery(id+"F26.boolean.opBoolean","SPLIT",FACE,{"disambiguationData":[TD([subQ80])],"derivedFrom":makeQuery(id+"F25.boolean.opBoolean","SPLIT",FACE,{"disambiguationData":[TD([subQ80])],"derivedFrom":makeQuery(id+"F24.boolean.opBoolean","SPLIT",FACE,{"disambiguationData":[TD([subQ80])],"derivedFrom":makeQuery(id+"F1.opRevolve","SWEPT_FACE",FACE,{"disambiguationData":[OSD([sQuery(id+"F0.wireOp",EDGE,"E13")])]})})})})})})})})})})})})})})})})})],"blendedInto":[makeQuery(id+"F40.boolean.opBoolean","SPLIT",FACE,{"disambiguationData":[TD([subQ0])],"derivedFrom":makeQuery(id+"F38.boolean.opBoolean","SPLIT",FACE,{"disambiguationData":[TD([subQ10])],"derivedFrom":makeQuery(id+"F37.boolean.opBoolean","SPLIT",FACE,{"disambiguationData":[TD([subQ17])],"derivedFrom":makeQuery(id+"F36.boolean.opBoolean","SPLIT",FACE,{"disambiguationData":[TD([subQ17])],"derivedFrom":makeQuery(id+"F35.boolean.opBoolean","SPLIT",FACE,{"disambiguationData":[TD([subQ17])],"derivedFrom":makeQuery(id+"F34.boolean.opBoolean","SPLIT",FACE,{"disambiguationData":[TD([subQ17])],"derivedFrom":makeQuery(id+"F33.boolean.opBoolean","SPLIT",FACE,{"disambiguationData":[TD([subQ17])],"derivedFrom":makeQuery(id+"F32.boolean.opBoolean","SPLIT",FACE,{"disambiguationData":[TD([subQ17])],"derivedFrom":makeQuery(id+"F31.boolean.opBoolean","SPLIT",FACE,{"disambiguationData":[TD([subQ17])],"derivedFrom":makeQuery(id+"F30.boolean.opBoolean","SPLIT",FACE,{"disambiguationData":[TD([subQ80])],"derivedFrom":makeQuery(id+"F29.boolean.opBoolean","SPLIT",FACE,{"disambiguationData":[TD([subQ80])],"derivedFrom":makeQuery(id+"F28.boolean.opBoolean","SPLIT",FACE,{"disambiguationData":[TD([subQ80])],"derivedFrom":makeQuery(id+"F27.boolean.opBoolean","SPLIT",FACE,{"disambiguationData":[TD([subQ80])],"derivedFrom":makeQuery(id+"F26.boolean.opBoolean","SPLIT",FACE,{"disambiguationData":[TD([subQ80])],"derivedFrom":makeQuery(id+"F25.boolean.opBoolean","SPLIT",FACE,{"disambiguationData":[TD([subQ80])],"derivedFrom":makeQuery(id+"F24.boolean.opBoolean","SPLIT",FACE,{"disambiguationData":[TD([subQ80])],"derivedFrom":makeQuery(id+"F1.opRevolve","SWEPT_FACE",FACE,{"disambiguationData":[OSD([sQuery(id+"F0.wireOp",EDGE,"E13")])]})})})})})})})})})})})})})})})})})]});}
            var Q14;
            {var subQ0=makeQuery(id+"F1.opRevolve","SWEPT_FACE",FACE,{"disambiguationData":[OSD([sQuery(id+"F0.wireOp",EDGE,"E12")])]});var subQ5=sQuery(id+"F3.wireOp",EDGE,"E20.7.3");var subQ6=sQuery(id+"F3.wireOp",EDGE,"E20.7.2");var subQ7=sQuery(id+"F3.wireOp",EDGE,"E20.7.1");var subQ8=makeQuery(id+"F38.opLoft","SWEPT_FACE",FACE,{"disambiguationData":[OSD([subQ7,subQ6,subQ5,sQuery(id+"F22.wireOp",EDGE,"E28.15.0"),sQuery(id+"F22.wireOp",EDGE,"E28.15.2"),sQuery(id+"F22.wireOp",EDGE,"E28.15.3")])]});var subQ9=makeQuery(id+"F40.opExtrude","CAP_FACE",FACE,{"disambiguationData":[OSD([sQuery(id+"F39.wireOp",EDGE,"E29"),sQuery(id+"F39.wireOp",EDGE,"E30")])],"isStart":true});var subQ13=sQuery(id+"F4.wireOp",EDGE,"E26.7.3");var subQ14=sQuery(id+"F4.wireOp",EDGE,"E26.7.2");var subQ15=makeQuery(id+"F14.opLoft","SWEPT_FACE",FACE,{"disambiguationData":[OSD([subQ7,subQ6,subQ5,sQuery(id+"F4.wireOp",EDGE,"E26.7.1"),subQ14,subQ13])]});var subQ21=sQuery(id+"F3.wireOp",EDGE,"E20.7.0");var subQ23=makeQuery(id+"F14.opLoft","CAP_FACE",FACE,{"disambiguationData":[OSD([makeQuery(id+"F3.imprint","IMPRINT",FACE,{"disambiguationData":[TD([[makeQuery(id+"F3.imprint","IMPRINT",EDGE,{"derivedFrom":subQ21}),-1.0]])]})])],"isStart":true});var subQ76=sQuery(id+"F3.wireOp",EDGE,"E18.bottom");var subQ81=makeQuery(id+"F5.opLoft","CAP_FACE",FACE,{"disambiguationData":[OSD([makeQuery(id+"F3.imprint","IMPRINT",FACE,{"disambiguationData":[TD([[makeQuery(id+"F3.imprint","IMPRINT",EDGE,{"derivedFrom":subQ76}),1.0]])]})])],"isStart":true});Q14=makeQuery(id+"F44.opFillet","BLEND_EDGE",EDGE,{"blendedFrom":[makeQuery(id+"F40.boolean.opBoolean","INTERSECT",EDGE,{"derivedFrom":[subQ8,subQ9]}),makeQuery(id+"F40.boolean.opBoolean","SPLIT",FACE,{"disambiguationData":[TD([subQ0])],"derivedFrom":makeQuery(id+"F38.boolean.opBoolean","SPLIT",FACE,{"disambiguationData":[TD([subQ15])],"derivedFrom":makeQuery(id+"F37.boolean.opBoolean","SPLIT",FACE,{"disambiguationData":[TD([subQ23])],"derivedFrom":makeQuery(id+"F36.boolean.opBoolean","SPLIT",FACE,{"disambiguationData":[TD([subQ23])],"derivedFrom":makeQuery(id+"F35.boolean.opBoolean","SPLIT",FACE,{"disambiguationData":[TD([subQ23])],"derivedFrom":makeQuery(id+"F34.boolean.opBoolean","SPLIT",FACE,{"disambiguationData":[TD([subQ23])],"derivedFrom":makeQuery(id+"F33.boolean.opBoolean","SPLIT",FACE,{"disambiguationData":[TD([subQ23])],"derivedFrom":makeQuery(id+"F32.boolean.opBoolean","SPLIT",FACE,{"disambiguationData":[TD([subQ23])],"derivedFrom":makeQuery(id+"F31.boolean.opBoolean","SPLIT",FACE,{"disambiguationData":[TD([subQ23])],"derivedFrom":makeQuery(id+"F30.boolean.opBoolean","SPLIT",FACE,{"disambiguationData":[TD([subQ81])],"derivedFrom":makeQuery(id+"F29.boolean.opBoolean","SPLIT",FACE,{"disambiguationData":[TD([subQ81])],"derivedFrom":makeQuery(id+"F28.boolean.opBoolean","SPLIT",FACE,{"disambiguationData":[TD([subQ81])],"derivedFrom":makeQuery(id+"F27.boolean.opBoolean","SPLIT",FACE,{"disambiguationData":[TD([subQ81])],"derivedFrom":makeQuery(id+"F26.boolean.opBoolean","SPLIT",FACE,{"disambiguationData":[TD([subQ81])],"derivedFrom":makeQuery(id+"F25.boolean.opBoolean","SPLIT",FACE,{"disambiguationData":[TD([subQ81])],"derivedFrom":makeQuery(id+"F24.boolean.opBoolean","SPLIT",FACE,{"disambiguationData":[TD([subQ81])],"derivedFrom":makeQuery(id+"F1.opRevolve","SWEPT_FACE",FACE,{"disambiguationData":[OSD([sQuery(id+"F0.wireOp",EDGE,"E13")])]})})})})})})})})})})})})})})})})})],"blendedInto":[makeQuery(id+"F40.boolean.opBoolean","SPLIT",FACE,{"disambiguationData":[TD([subQ0])],"derivedFrom":makeQuery(id+"F38.boolean.opBoolean","SPLIT",FACE,{"disambiguationData":[TD([subQ15])],"derivedFrom":makeQuery(id+"F37.boolean.opBoolean","SPLIT",FACE,{"disambiguationData":[TD([subQ23])],"derivedFrom":makeQuery(id+"F36.boolean.opBoolean","SPLIT",FACE,{"disambiguationData":[TD([subQ23])],"derivedFrom":makeQuery(id+"F35.boolean.opBoolean","SPLIT",FACE,{"disambiguationData":[TD([subQ23])],"derivedFrom":makeQuery(id+"F34.boolean.opBoolean","SPLIT",FACE,{"disambiguationData":[TD([subQ23])],"derivedFrom":makeQuery(id+"F33.boolean.opBoolean","SPLIT",FACE,{"disambiguationData":[TD([subQ23])],"derivedFrom":makeQuery(id+"F32.boolean.opBoolean","SPLIT",FACE,{"disambiguationData":[TD([subQ23])],"derivedFrom":makeQuery(id+"F31.boolean.opBoolean","SPLIT",FACE,{"disambiguationData":[TD([subQ23])],"derivedFrom":makeQuery(id+"F30.boolean.opBoolean","SPLIT",FACE,{"disambiguationData":[TD([subQ81])],"derivedFrom":makeQuery(id+"F29.boolean.opBoolean","SPLIT",FACE,{"disambiguationData":[TD([subQ81])],"derivedFrom":makeQuery(id+"F28.boolean.opBoolean","SPLIT",FACE,{"disambiguationData":[TD([subQ81])],"derivedFrom":makeQuery(id+"F27.boolean.opBoolean","SPLIT",FACE,{"disambiguationData":[TD([subQ81])],"derivedFrom":makeQuery(id+"F26.boolean.opBoolean","SPLIT",FACE,{"disambiguationData":[TD([subQ81])],"derivedFrom":makeQuery(id+"F25.boolean.opBoolean","SPLIT",FACE,{"disambiguationData":[TD([subQ81])],"derivedFrom":makeQuery(id+"F24.boolean.opBoolean","SPLIT",FACE,{"disambiguationData":[TD([subQ81])],"derivedFrom":makeQuery(id+"F1.opRevolve","SWEPT_FACE",FACE,{"disambiguationData":[OSD([sQuery(id+"F0.wireOp",EDGE,"E13")])]})})})})})})})})})})})})})})})})})]});}
            var Q15;
            {var subQ0=makeQuery(id+"F1.opRevolve","SWEPT_FACE",FACE,{"disambiguationData":[OSD([sQuery(id+"F0.wireOp",EDGE,"E12")])]});var subQ5=sQuery(id+"F3.wireOp",EDGE,"E20.6.3");var subQ6=sQuery(id+"F3.wireOp",EDGE,"E20.6.2");var subQ7=sQuery(id+"F3.wireOp",EDGE,"E20.6.1");var subQ8=makeQuery(id+"F37.opLoft","SWEPT_FACE",FACE,{"disambiguationData":[OSD([subQ7,subQ6,subQ5,sQuery(id+"F22.wireOp",EDGE,"E28.14.0"),sQuery(id+"F22.wireOp",EDGE,"E28.14.2"),sQuery(id+"F22.wireOp",EDGE,"E28.14.3")])]});var subQ9=makeQuery(id+"F40.opExtrude","CAP_FACE",FACE,{"disambiguationData":[OSD([sQuery(id+"F39.wireOp",EDGE,"E29"),sQuery(id+"F39.wireOp",EDGE,"E30")])],"isStart":true});var subQ13=sQuery(id+"F4.wireOp",EDGE,"E26.6.3");var subQ14=sQuery(id+"F4.wireOp",EDGE,"E26.6.2");var subQ15=makeQuery(id+"F15.opLoft","SWEPT_FACE",FACE,{"disambiguationData":[OSD([subQ7,subQ6,subQ5,sQuery(id+"F4.wireOp",EDGE,"E26.6.1"),subQ14,subQ13])]});var subQ20=sQuery(id+"F3.wireOp",EDGE,"E20.7.0");var subQ24=makeQuery(id+"F14.opLoft","CAP_FACE",FACE,{"disambiguationData":[OSD([makeQuery(id+"F3.imprint","IMPRINT",FACE,{"disambiguationData":[TD([[makeQuery(id+"F3.imprint","IMPRINT",EDGE,{"derivedFrom":subQ20}),-1.0]])]})])],"isStart":true});var subQ76=sQuery(id+"F3.wireOp",EDGE,"E18.bottom");var subQ81=makeQuery(id+"F5.opLoft","CAP_FACE",FACE,{"disambiguationData":[OSD([makeQuery(id+"F3.imprint","IMPRINT",FACE,{"disambiguationData":[TD([[makeQuery(id+"F3.imprint","IMPRINT",EDGE,{"derivedFrom":subQ76}),1.0]])]})])],"isStart":true});Q15=makeQuery(id+"F44.opFillet","BLEND_EDGE",EDGE,{"blendedFrom":[makeQuery(id+"F40.boolean.opBoolean","INTERSECT",EDGE,{"derivedFrom":[subQ8,subQ9]}),makeQuery(id+"F40.boolean.opBoolean","SPLIT",FACE,{"disambiguationData":[TD([subQ0])],"derivedFrom":makeQuery(id+"F37.boolean.opBoolean","SPLIT",FACE,{"disambiguationData":[TD([subQ15])],"derivedFrom":makeQuery(id+"F36.boolean.opBoolean","SPLIT",FACE,{"disambiguationData":[TD([subQ24])],"derivedFrom":makeQuery(id+"F35.boolean.opBoolean","SPLIT",FACE,{"disambiguationData":[TD([subQ24])],"derivedFrom":makeQuery(id+"F34.boolean.opBoolean","SPLIT",FACE,{"disambiguationData":[TD([subQ24])],"derivedFrom":makeQuery(id+"F33.boolean.opBoolean","SPLIT",FACE,{"disambiguationData":[TD([subQ24])],"derivedFrom":makeQuery(id+"F32.boolean.opBoolean","SPLIT",FACE,{"disambiguationData":[TD([subQ24])],"derivedFrom":makeQuery(id+"F31.boolean.opBoolean","SPLIT",FACE,{"disambiguationData":[TD([subQ24])],"derivedFrom":makeQuery(id+"F30.boolean.opBoolean","SPLIT",FACE,{"disambiguationData":[TD([subQ81])],"derivedFrom":makeQuery(id+"F29.boolean.opBoolean","SPLIT",FACE,{"disambiguationData":[TD([subQ81])],"derivedFrom":makeQuery(id+"F28.boolean.opBoolean","SPLIT",FACE,{"disambiguationData":[TD([subQ81])],"derivedFrom":makeQuery(id+"F27.boolean.opBoolean","SPLIT",FACE,{"disambiguationData":[TD([subQ81])],"derivedFrom":makeQuery(id+"F26.boolean.opBoolean","SPLIT",FACE,{"disambiguationData":[TD([subQ81])],"derivedFrom":makeQuery(id+"F25.boolean.opBoolean","SPLIT",FACE,{"disambiguationData":[TD([subQ81])],"derivedFrom":makeQuery(id+"F24.boolean.opBoolean","SPLIT",FACE,{"disambiguationData":[TD([subQ81])],"derivedFrom":makeQuery(id+"F1.opRevolve","SWEPT_FACE",FACE,{"disambiguationData":[OSD([sQuery(id+"F0.wireOp",EDGE,"E13")])]})})})})})})})})})})})})})})})})],"blendedInto":[makeQuery(id+"F40.boolean.opBoolean","SPLIT",FACE,{"disambiguationData":[TD([subQ0])],"derivedFrom":makeQuery(id+"F37.boolean.opBoolean","SPLIT",FACE,{"disambiguationData":[TD([subQ15])],"derivedFrom":makeQuery(id+"F36.boolean.opBoolean","SPLIT",FACE,{"disambiguationData":[TD([subQ24])],"derivedFrom":makeQuery(id+"F35.boolean.opBoolean","SPLIT",FACE,{"disambiguationData":[TD([subQ24])],"derivedFrom":makeQuery(id+"F34.boolean.opBoolean","SPLIT",FACE,{"disambiguationData":[TD([subQ24])],"derivedFrom":makeQuery(id+"F33.boolean.opBoolean","SPLIT",FACE,{"disambiguationData":[TD([subQ24])],"derivedFrom":makeQuery(id+"F32.boolean.opBoolean","SPLIT",FACE,{"disambiguationData":[TD([subQ24])],"derivedFrom":makeQuery(id+"F31.boolean.opBoolean","SPLIT",FACE,{"disambiguationData":[TD([subQ24])],"derivedFrom":makeQuery(id+"F30.boolean.opBoolean","SPLIT",FACE,{"disambiguationData":[TD([subQ81])],"derivedFrom":makeQuery(id+"F29.boolean.opBoolean","SPLIT",FACE,{"disambiguationData":[TD([subQ81])],"derivedFrom":makeQuery(id+"F28.boolean.opBoolean","SPLIT",FACE,{"disambiguationData":[TD([subQ81])],"derivedFrom":makeQuery(id+"F27.boolean.opBoolean","SPLIT",FACE,{"disambiguationData":[TD([subQ81])],"derivedFrom":makeQuery(id+"F26.boolean.opBoolean","SPLIT",FACE,{"disambiguationData":[TD([subQ81])],"derivedFrom":makeQuery(id+"F25.boolean.opBoolean","SPLIT",FACE,{"disambiguationData":[TD([subQ81])],"derivedFrom":makeQuery(id+"F24.boolean.opBoolean","SPLIT",FACE,{"disambiguationData":[TD([subQ81])],"derivedFrom":makeQuery(id+"F1.opRevolve","SWEPT_FACE",FACE,{"disambiguationData":[OSD([sQuery(id+"F0.wireOp",EDGE,"E13")])]})})})})})})})})})})})})})})})})]});}
            var Q16;
            {var subQ0=makeQuery(id+"F1.opRevolve","SWEPT_FACE",FACE,{"disambiguationData":[OSD([sQuery(id+"F0.wireOp",EDGE,"E12")])]});var subQ1=sQuery(id+"F3.wireOp",EDGE,"E20.5.3");var subQ2=sQuery(id+"F3.wireOp",EDGE,"E20.5.2");var subQ3=sQuery(id+"F3.wireOp",EDGE,"E20.5.1");var subQ4=makeQuery(id+"F36.opLoft","SWEPT_FACE",FACE,{"disambiguationData":[OSD([subQ3,subQ2,subQ1,sQuery(id+"F22.wireOp",EDGE,"E28.13.0"),sQuery(id+"F22.wireOp",EDGE,"E28.13.2"),sQuery(id+"F22.wireOp",EDGE,"E28.13.3")])]});var subQ9=makeQuery(id+"F40.opExtrude","CAP_FACE",FACE,{"disambiguationData":[OSD([sQuery(id+"F39.wireOp",EDGE,"E29"),sQuery(id+"F39.wireOp",EDGE,"E30")])],"isStart":true});var subQ10=sQuery(id+"F4.wireOp",EDGE,"E26.5.3");var subQ11=sQuery(id+"F4.wireOp",EDGE,"E26.5.2");var subQ12=makeQuery(id+"F16.opLoft","SWEPT_FACE",FACE,{"disambiguationData":[OSD([subQ3,subQ2,subQ1,sQuery(id+"F4.wireOp",EDGE,"E26.5.1"),subQ11,subQ10])]});var subQ27=sQuery(id+"F3.wireOp",EDGE,"E20.7.0");var subQ31=makeQuery(id+"F14.opLoft","CAP_FACE",FACE,{"disambiguationData":[OSD([makeQuery(id+"F3.imprint","IMPRINT",FACE,{"disambiguationData":[TD([[makeQuery(id+"F3.imprint","IMPRINT",EDGE,{"derivedFrom":subQ27}),-1.0]])]})])],"isStart":true});var subQ76=sQuery(id+"F3.wireOp",EDGE,"E18.bottom");var subQ81=makeQuery(id+"F5.opLoft","CAP_FACE",FACE,{"disambiguationData":[OSD([makeQuery(id+"F3.imprint","IMPRINT",FACE,{"disambiguationData":[TD([[makeQuery(id+"F3.imprint","IMPRINT",EDGE,{"derivedFrom":subQ76}),1.0]])]})])],"isStart":true});Q16=makeQuery(id+"F44.opFillet","BLEND_EDGE",EDGE,{"blendedFrom":[makeQuery(id+"F40.boolean.opBoolean","INTERSECT",EDGE,{"derivedFrom":[subQ4,subQ9]}),makeQuery(id+"F40.boolean.opBoolean","SPLIT",FACE,{"disambiguationData":[TD([subQ0])],"derivedFrom":makeQuery(id+"F36.boolean.opBoolean","SPLIT",FACE,{"disambiguationData":[TD([subQ12])],"derivedFrom":makeQuery(id+"F35.boolean.opBoolean","SPLIT",FACE,{"disambiguationData":[TD([subQ31])],"derivedFrom":makeQuery(id+"F34.boolean.opBoolean","SPLIT",FACE,{"disambiguationData":[TD([subQ31])],"derivedFrom":makeQuery(id+"F33.boolean.opBoolean","SPLIT",FACE,{"disambiguationData":[TD([subQ31])],"derivedFrom":makeQuery(id+"F32.boolean.opBoolean","SPLIT",FACE,{"disambiguationData":[TD([subQ31])],"derivedFrom":makeQuery(id+"F31.boolean.opBoolean","SPLIT",FACE,{"disambiguationData":[TD([subQ31])],"derivedFrom":makeQuery(id+"F30.boolean.opBoolean","SPLIT",FACE,{"disambiguationData":[TD([subQ81])],"derivedFrom":makeQuery(id+"F29.boolean.opBoolean","SPLIT",FACE,{"disambiguationData":[TD([subQ81])],"derivedFrom":makeQuery(id+"F28.boolean.opBoolean","SPLIT",FACE,{"disambiguationData":[TD([subQ81])],"derivedFrom":makeQuery(id+"F27.boolean.opBoolean","SPLIT",FACE,{"disambiguationData":[TD([subQ81])],"derivedFrom":makeQuery(id+"F26.boolean.opBoolean","SPLIT",FACE,{"disambiguationData":[TD([subQ81])],"derivedFrom":makeQuery(id+"F25.boolean.opBoolean","SPLIT",FACE,{"disambiguationData":[TD([subQ81])],"derivedFrom":makeQuery(id+"F24.boolean.opBoolean","SPLIT",FACE,{"disambiguationData":[TD([subQ81])],"derivedFrom":makeQuery(id+"F1.opRevolve","SWEPT_FACE",FACE,{"disambiguationData":[OSD([sQuery(id+"F0.wireOp",EDGE,"E13")])]})})})})})})})})})})})})})})})],"blendedInto":[makeQuery(id+"F40.boolean.opBoolean","SPLIT",FACE,{"disambiguationData":[TD([subQ0])],"derivedFrom":makeQuery(id+"F36.boolean.opBoolean","SPLIT",FACE,{"disambiguationData":[TD([subQ12])],"derivedFrom":makeQuery(id+"F35.boolean.opBoolean","SPLIT",FACE,{"disambiguationData":[TD([subQ31])],"derivedFrom":makeQuery(id+"F34.boolean.opBoolean","SPLIT",FACE,{"disambiguationData":[TD([subQ31])],"derivedFrom":makeQuery(id+"F33.boolean.opBoolean","SPLIT",FACE,{"disambiguationData":[TD([subQ31])],"derivedFrom":makeQuery(id+"F32.boolean.opBoolean","SPLIT",FACE,{"disambiguationData":[TD([subQ31])],"derivedFrom":makeQuery(id+"F31.boolean.opBoolean","SPLIT",FACE,{"disambiguationData":[TD([subQ31])],"derivedFrom":makeQuery(id+"F30.boolean.opBoolean","SPLIT",FACE,{"disambiguationData":[TD([subQ81])],"derivedFrom":makeQuery(id+"F29.boolean.opBoolean","SPLIT",FACE,{"disambiguationData":[TD([subQ81])],"derivedFrom":makeQuery(id+"F28.boolean.opBoolean","SPLIT",FACE,{"disambiguationData":[TD([subQ81])],"derivedFrom":makeQuery(id+"F27.boolean.opBoolean","SPLIT",FACE,{"disambiguationData":[TD([subQ81])],"derivedFrom":makeQuery(id+"F26.boolean.opBoolean","SPLIT",FACE,{"disambiguationData":[TD([subQ81])],"derivedFrom":makeQuery(id+"F25.boolean.opBoolean","SPLIT",FACE,{"disambiguationData":[TD([subQ81])],"derivedFrom":makeQuery(id+"F24.boolean.opBoolean","SPLIT",FACE,{"disambiguationData":[TD([subQ81])],"derivedFrom":makeQuery(id+"F1.opRevolve","SWEPT_FACE",FACE,{"disambiguationData":[OSD([sQuery(id+"F0.wireOp",EDGE,"E13")])]})})})})})})})})})})})})})})})]});}
            var Q17;
            {var subQ0=makeQuery(id+"F1.opRevolve","SWEPT_FACE",FACE,{"disambiguationData":[OSD([sQuery(id+"F0.wireOp",EDGE,"E12")])]});var subQ5=sQuery(id+"F3.wireOp",EDGE,"E20.4.3");var subQ6=sQuery(id+"F3.wireOp",EDGE,"E20.4.2");var subQ7=sQuery(id+"F3.wireOp",EDGE,"E20.4.1");var subQ8=makeQuery(id+"F35.opLoft","SWEPT_FACE",FACE,{"disambiguationData":[OSD([subQ7,subQ6,subQ5,sQuery(id+"F22.wireOp",EDGE,"E28.12.0"),sQuery(id+"F22.wireOp",EDGE,"E28.12.2"),sQuery(id+"F22.wireOp",EDGE,"E28.12.3")])]});var subQ9=makeQuery(id+"F40.opExtrude","CAP_FACE",FACE,{"disambiguationData":[OSD([sQuery(id+"F39.wireOp",EDGE,"E29"),sQuery(id+"F39.wireOp",EDGE,"E30")])],"isStart":true});var subQ10=sQuery(id+"F4.wireOp",EDGE,"E26.4.3");var subQ11=sQuery(id+"F4.wireOp",EDGE,"E26.4.2");var subQ12=makeQuery(id+"F17.opLoft","SWEPT_FACE",FACE,{"disambiguationData":[OSD([subQ7,subQ6,subQ5,sQuery(id+"F4.wireOp",EDGE,"E26.4.1"),subQ11,subQ10])]});var subQ33=sQuery(id+"F3.wireOp",EDGE,"E20.7.0");var subQ37=makeQuery(id+"F14.opLoft","CAP_FACE",FACE,{"disambiguationData":[OSD([makeQuery(id+"F3.imprint","IMPRINT",FACE,{"disambiguationData":[TD([[makeQuery(id+"F3.imprint","IMPRINT",EDGE,{"derivedFrom":subQ33}),-1.0]])]})])],"isStart":true});var subQ76=sQuery(id+"F3.wireOp",EDGE,"E18.bottom");var subQ81=makeQuery(id+"F5.opLoft","CAP_FACE",FACE,{"disambiguationData":[OSD([makeQuery(id+"F3.imprint","IMPRINT",FACE,{"disambiguationData":[TD([[makeQuery(id+"F3.imprint","IMPRINT",EDGE,{"derivedFrom":subQ76}),1.0]])]})])],"isStart":true});Q17=makeQuery(id+"F44.opFillet","BLEND_EDGE",EDGE,{"blendedFrom":[makeQuery(id+"F40.boolean.opBoolean","INTERSECT",EDGE,{"derivedFrom":[subQ8,subQ9]}),makeQuery(id+"F40.boolean.opBoolean","SPLIT",FACE,{"disambiguationData":[TD([subQ0])],"derivedFrom":makeQuery(id+"F35.boolean.opBoolean","SPLIT",FACE,{"disambiguationData":[TD([subQ12])],"derivedFrom":makeQuery(id+"F34.boolean.opBoolean","SPLIT",FACE,{"disambiguationData":[TD([subQ37])],"derivedFrom":makeQuery(id+"F33.boolean.opBoolean","SPLIT",FACE,{"disambiguationData":[TD([subQ37])],"derivedFrom":makeQuery(id+"F32.boolean.opBoolean","SPLIT",FACE,{"disambiguationData":[TD([subQ37])],"derivedFrom":makeQuery(id+"F31.boolean.opBoolean","SPLIT",FACE,{"disambiguationData":[TD([subQ37])],"derivedFrom":makeQuery(id+"F30.boolean.opBoolean","SPLIT",FACE,{"disambiguationData":[TD([subQ81])],"derivedFrom":makeQuery(id+"F29.boolean.opBoolean","SPLIT",FACE,{"disambiguationData":[TD([subQ81])],"derivedFrom":makeQuery(id+"F28.boolean.opBoolean","SPLIT",FACE,{"disambiguationData":[TD([subQ81])],"derivedFrom":makeQuery(id+"F27.boolean.opBoolean","SPLIT",FACE,{"disambiguationData":[TD([subQ81])],"derivedFrom":makeQuery(id+"F26.boolean.opBoolean","SPLIT",FACE,{"disambiguationData":[TD([subQ81])],"derivedFrom":makeQuery(id+"F25.boolean.opBoolean","SPLIT",FACE,{"disambiguationData":[TD([subQ81])],"derivedFrom":makeQuery(id+"F24.boolean.opBoolean","SPLIT",FACE,{"disambiguationData":[TD([subQ81])],"derivedFrom":makeQuery(id+"F1.opRevolve","SWEPT_FACE",FACE,{"disambiguationData":[OSD([sQuery(id+"F0.wireOp",EDGE,"E13")])]})})})})})})})})})})})})})})],"blendedInto":[makeQuery(id+"F40.boolean.opBoolean","SPLIT",FACE,{"disambiguationData":[TD([subQ0])],"derivedFrom":makeQuery(id+"F35.boolean.opBoolean","SPLIT",FACE,{"disambiguationData":[TD([subQ12])],"derivedFrom":makeQuery(id+"F34.boolean.opBoolean","SPLIT",FACE,{"disambiguationData":[TD([subQ37])],"derivedFrom":makeQuery(id+"F33.boolean.opBoolean","SPLIT",FACE,{"disambiguationData":[TD([subQ37])],"derivedFrom":makeQuery(id+"F32.boolean.opBoolean","SPLIT",FACE,{"disambiguationData":[TD([subQ37])],"derivedFrom":makeQuery(id+"F31.boolean.opBoolean","SPLIT",FACE,{"disambiguationData":[TD([subQ37])],"derivedFrom":makeQuery(id+"F30.boolean.opBoolean","SPLIT",FACE,{"disambiguationData":[TD([subQ81])],"derivedFrom":makeQuery(id+"F29.boolean.opBoolean","SPLIT",FACE,{"disambiguationData":[TD([subQ81])],"derivedFrom":makeQuery(id+"F28.boolean.opBoolean","SPLIT",FACE,{"disambiguationData":[TD([subQ81])],"derivedFrom":makeQuery(id+"F27.boolean.opBoolean","SPLIT",FACE,{"disambiguationData":[TD([subQ81])],"derivedFrom":makeQuery(id+"F26.boolean.opBoolean","SPLIT",FACE,{"disambiguationData":[TD([subQ81])],"derivedFrom":makeQuery(id+"F25.boolean.opBoolean","SPLIT",FACE,{"disambiguationData":[TD([subQ81])],"derivedFrom":makeQuery(id+"F24.boolean.opBoolean","SPLIT",FACE,{"disambiguationData":[TD([subQ81])],"derivedFrom":makeQuery(id+"F1.opRevolve","SWEPT_FACE",FACE,{"disambiguationData":[OSD([sQuery(id+"F0.wireOp",EDGE,"E13")])]})})})})})})})})})})})})})})]});}
            var Q18;
            {var subQ0=makeQuery(id+"F1.opRevolve","SWEPT_FACE",FACE,{"disambiguationData":[OSD([sQuery(id+"F0.wireOp",EDGE,"E12")])]});var subQ5=makeQuery(id+"F40.opExtrude","CAP_FACE",FACE,{"disambiguationData":[OSD([sQuery(id+"F39.wireOp",EDGE,"E29"),sQuery(id+"F39.wireOp",EDGE,"E30")])],"isStart":true});var subQ6=sQuery(id+"F3.wireOp",EDGE,"E20.3.3");var subQ7=sQuery(id+"F3.wireOp",EDGE,"E20.3.2");var subQ8=sQuery(id+"F3.wireOp",EDGE,"E20.3.1");var subQ9=makeQuery(id+"F34.opLoft","SWEPT_FACE",FACE,{"disambiguationData":[OSD([subQ8,subQ7,subQ6,sQuery(id+"F22.wireOp",EDGE,"E28.11.0"),sQuery(id+"F22.wireOp",EDGE,"E28.11.2"),sQuery(id+"F22.wireOp",EDGE,"E28.11.3")])]});var subQ13=sQuery(id+"F4.wireOp",EDGE,"E26.3.3");var subQ14=sQuery(id+"F4.wireOp",EDGE,"E26.3.2");var subQ15=makeQuery(id+"F18.opLoft","SWEPT_FACE",FACE,{"disambiguationData":[OSD([subQ8,subQ7,subQ6,sQuery(id+"F4.wireOp",EDGE,"E26.3.1"),subQ14,subQ13])]});var subQ36=sQuery(id+"F3.wireOp",EDGE,"E20.7.0");var subQ40=makeQuery(id+"F14.opLoft","CAP_FACE",FACE,{"disambiguationData":[OSD([makeQuery(id+"F3.imprint","IMPRINT",FACE,{"disambiguationData":[TD([[makeQuery(id+"F3.imprint","IMPRINT",EDGE,{"derivedFrom":subQ36}),-1.0]])]})])],"isStart":true});var subQ76=sQuery(id+"F3.wireOp",EDGE,"E18.bottom");var subQ81=makeQuery(id+"F5.opLoft","CAP_FACE",FACE,{"disambiguationData":[OSD([makeQuery(id+"F3.imprint","IMPRINT",FACE,{"disambiguationData":[TD([[makeQuery(id+"F3.imprint","IMPRINT",EDGE,{"derivedFrom":subQ76}),1.0]])]})])],"isStart":true});Q18=makeQuery(id+"F44.opFillet","BLEND_EDGE",EDGE,{"blendedFrom":[makeQuery(id+"F40.boolean.opBoolean","INTERSECT",EDGE,{"derivedFrom":[subQ9,subQ5]}),makeQuery(id+"F40.boolean.opBoolean","SPLIT",FACE,{"disambiguationData":[TD([subQ0])],"derivedFrom":makeQuery(id+"F34.boolean.opBoolean","SPLIT",FACE,{"disambiguationData":[TD([subQ15])],"derivedFrom":makeQuery(id+"F33.boolean.opBoolean","SPLIT",FACE,{"disambiguationData":[TD([subQ40])],"derivedFrom":makeQuery(id+"F32.boolean.opBoolean","SPLIT",FACE,{"disambiguationData":[TD([subQ40])],"derivedFrom":makeQuery(id+"F31.boolean.opBoolean","SPLIT",FACE,{"disambiguationData":[TD([subQ40])],"derivedFrom":makeQuery(id+"F30.boolean.opBoolean","SPLIT",FACE,{"disambiguationData":[TD([subQ81])],"derivedFrom":makeQuery(id+"F29.boolean.opBoolean","SPLIT",FACE,{"disambiguationData":[TD([subQ81])],"derivedFrom":makeQuery(id+"F28.boolean.opBoolean","SPLIT",FACE,{"disambiguationData":[TD([subQ81])],"derivedFrom":makeQuery(id+"F27.boolean.opBoolean","SPLIT",FACE,{"disambiguationData":[TD([subQ81])],"derivedFrom":makeQuery(id+"F26.boolean.opBoolean","SPLIT",FACE,{"disambiguationData":[TD([subQ81])],"derivedFrom":makeQuery(id+"F25.boolean.opBoolean","SPLIT",FACE,{"disambiguationData":[TD([subQ81])],"derivedFrom":makeQuery(id+"F24.boolean.opBoolean","SPLIT",FACE,{"disambiguationData":[TD([subQ81])],"derivedFrom":makeQuery(id+"F1.opRevolve","SWEPT_FACE",FACE,{"disambiguationData":[OSD([sQuery(id+"F0.wireOp",EDGE,"E13")])]})})})})})})})})})})})})})],"blendedInto":[makeQuery(id+"F40.boolean.opBoolean","SPLIT",FACE,{"disambiguationData":[TD([subQ0])],"derivedFrom":makeQuery(id+"F34.boolean.opBoolean","SPLIT",FACE,{"disambiguationData":[TD([subQ15])],"derivedFrom":makeQuery(id+"F33.boolean.opBoolean","SPLIT",FACE,{"disambiguationData":[TD([subQ40])],"derivedFrom":makeQuery(id+"F32.boolean.opBoolean","SPLIT",FACE,{"disambiguationData":[TD([subQ40])],"derivedFrom":makeQuery(id+"F31.boolean.opBoolean","SPLIT",FACE,{"disambiguationData":[TD([subQ40])],"derivedFrom":makeQuery(id+"F30.boolean.opBoolean","SPLIT",FACE,{"disambiguationData":[TD([subQ81])],"derivedFrom":makeQuery(id+"F29.boolean.opBoolean","SPLIT",FACE,{"disambiguationData":[TD([subQ81])],"derivedFrom":makeQuery(id+"F28.boolean.opBoolean","SPLIT",FACE,{"disambiguationData":[TD([subQ81])],"derivedFrom":makeQuery(id+"F27.boolean.opBoolean","SPLIT",FACE,{"disambiguationData":[TD([subQ81])],"derivedFrom":makeQuery(id+"F26.boolean.opBoolean","SPLIT",FACE,{"disambiguationData":[TD([subQ81])],"derivedFrom":makeQuery(id+"F25.boolean.opBoolean","SPLIT",FACE,{"disambiguationData":[TD([subQ81])],"derivedFrom":makeQuery(id+"F24.boolean.opBoolean","SPLIT",FACE,{"disambiguationData":[TD([subQ81])],"derivedFrom":makeQuery(id+"F1.opRevolve","SWEPT_FACE",FACE,{"disambiguationData":[OSD([sQuery(id+"F0.wireOp",EDGE,"E13")])]})})})})})})})})})})})})})]});}
            var Q19;
            {var subQ0=makeQuery(id+"F1.opRevolve","SWEPT_FACE",FACE,{"disambiguationData":[OSD([sQuery(id+"F0.wireOp",EDGE,"E10")])]});var subQ1=sQuery(id+"F4.wireOp",EDGE,"E26.3.3");var subQ2=sQuery(id+"F4.wireOp",EDGE,"E26.3.2");var subQ3=sQuery(id+"F3.wireOp",EDGE,"E20.3.3");var subQ4=sQuery(id+"F3.wireOp",EDGE,"E20.3.2");var subQ5=sQuery(id+"F3.wireOp",EDGE,"E20.3.1");var subQ6=makeQuery(id+"F18.opLoft","SWEPT_FACE",FACE,{"disambiguationData":[OSD([subQ5,subQ4,subQ3,sQuery(id+"F4.wireOp",EDGE,"E26.3.1"),subQ2,subQ1])]});var subQ13=makeQuery(id+"F40.opExtrude","CAP_FACE",FACE,{"disambiguationData":[OSD([sQuery(id+"F39.wireOp",EDGE,"E29"),sQuery(id+"F39.wireOp",EDGE,"E30")])],"isStart":false});var subQ35=sQuery(id+"F3.wireOp",EDGE,"E20.7.0");var subQ39=makeQuery(id+"F14.opLoft","CAP_FACE",FACE,{"disambiguationData":[OSD([makeQuery(id+"F3.imprint","IMPRINT",FACE,{"disambiguationData":[TD([[makeQuery(id+"F3.imprint","IMPRINT",EDGE,{"derivedFrom":subQ35}),-1.0]])]})])],"isStart":true});var subQ75=sQuery(id+"F3.wireOp",EDGE,"E18.bottom");var subQ80=makeQuery(id+"F5.opLoft","CAP_FACE",FACE,{"disambiguationData":[OSD([makeQuery(id+"F3.imprint","IMPRINT",FACE,{"disambiguationData":[TD([[makeQuery(id+"F3.imprint","IMPRINT",EDGE,{"derivedFrom":subQ75}),1.0]])]})])],"isStart":true});Q19=makeQuery(id+"F44.opFillet","BLEND_EDGE",EDGE,{"blendedFrom":[makeQuery(id+"F40.boolean.opBoolean","INTERSECT",EDGE,{"derivedFrom":[subQ6,subQ13]}),makeQuery(id+"F40.boolean.opBoolean","SPLIT",FACE,{"disambiguationData":[TD([subQ0])],"derivedFrom":makeQuery(id+"F34.boolean.opBoolean","SPLIT",FACE,{"disambiguationData":[TD([subQ6])],"derivedFrom":makeQuery(id+"F33.boolean.opBoolean","SPLIT",FACE,{"disambiguationData":[TD([subQ39])],"derivedFrom":makeQuery(id+"F32.boolean.opBoolean","SPLIT",FACE,{"disambiguationData":[TD([subQ39])],"derivedFrom":makeQuery(id+"F31.boolean.opBoolean","SPLIT",FACE,{"disambiguationData":[TD([subQ39])],"derivedFrom":makeQuery(id+"F30.boolean.opBoolean","SPLIT",FACE,{"disambiguationData":[TD([subQ80])],"derivedFrom":makeQuery(id+"F29.boolean.opBoolean","SPLIT",FACE,{"disambiguationData":[TD([subQ80])],"derivedFrom":makeQuery(id+"F28.boolean.opBoolean","SPLIT",FACE,{"disambiguationData":[TD([subQ80])],"derivedFrom":makeQuery(id+"F27.boolean.opBoolean","SPLIT",FACE,{"disambiguationData":[TD([subQ80])],"derivedFrom":makeQuery(id+"F26.boolean.opBoolean","SPLIT",FACE,{"disambiguationData":[TD([subQ80])],"derivedFrom":makeQuery(id+"F25.boolean.opBoolean","SPLIT",FACE,{"disambiguationData":[TD([subQ80])],"derivedFrom":makeQuery(id+"F24.boolean.opBoolean","SPLIT",FACE,{"disambiguationData":[TD([subQ80])],"derivedFrom":makeQuery(id+"F1.opRevolve","SWEPT_FACE",FACE,{"disambiguationData":[OSD([sQuery(id+"F0.wireOp",EDGE,"E13")])]})})})})})})})})})})})})})],"blendedInto":[makeQuery(id+"F40.boolean.opBoolean","SPLIT",FACE,{"disambiguationData":[TD([subQ0])],"derivedFrom":makeQuery(id+"F34.boolean.opBoolean","SPLIT",FACE,{"disambiguationData":[TD([subQ6])],"derivedFrom":makeQuery(id+"F33.boolean.opBoolean","SPLIT",FACE,{"disambiguationData":[TD([subQ39])],"derivedFrom":makeQuery(id+"F32.boolean.opBoolean","SPLIT",FACE,{"disambiguationData":[TD([subQ39])],"derivedFrom":makeQuery(id+"F31.boolean.opBoolean","SPLIT",FACE,{"disambiguationData":[TD([subQ39])],"derivedFrom":makeQuery(id+"F30.boolean.opBoolean","SPLIT",FACE,{"disambiguationData":[TD([subQ80])],"derivedFrom":makeQuery(id+"F29.boolean.opBoolean","SPLIT",FACE,{"disambiguationData":[TD([subQ80])],"derivedFrom":makeQuery(id+"F28.boolean.opBoolean","SPLIT",FACE,{"disambiguationData":[TD([subQ80])],"derivedFrom":makeQuery(id+"F27.boolean.opBoolean","SPLIT",FACE,{"disambiguationData":[TD([subQ80])],"derivedFrom":makeQuery(id+"F26.boolean.opBoolean","SPLIT",FACE,{"disambiguationData":[TD([subQ80])],"derivedFrom":makeQuery(id+"F25.boolean.opBoolean","SPLIT",FACE,{"disambiguationData":[TD([subQ80])],"derivedFrom":makeQuery(id+"F24.boolean.opBoolean","SPLIT",FACE,{"disambiguationData":[TD([subQ80])],"derivedFrom":makeQuery(id+"F1.opRevolve","SWEPT_FACE",FACE,{"disambiguationData":[OSD([sQuery(id+"F0.wireOp",EDGE,"E13")])]})})})})})})})})})})})})})]});}
            var Q20;
            {var subQ0=makeQuery(id+"F1.opRevolve","SWEPT_FACE",FACE,{"disambiguationData":[OSD([sQuery(id+"F0.wireOp",EDGE,"E10")])]});var subQ7=sQuery(id+"F4.wireOp",EDGE,"E26.4.3");var subQ8=sQuery(id+"F4.wireOp",EDGE,"E26.4.2");var subQ9=sQuery(id+"F3.wireOp",EDGE,"E20.4.3");var subQ10=sQuery(id+"F3.wireOp",EDGE,"E20.4.2");var subQ11=sQuery(id+"F3.wireOp",EDGE,"E20.4.1");var subQ12=makeQuery(id+"F17.opLoft","SWEPT_FACE",FACE,{"disambiguationData":[OSD([subQ11,subQ10,subQ9,sQuery(id+"F4.wireOp",EDGE,"E26.4.1"),subQ8,subQ7])]});var subQ13=makeQuery(id+"F40.opExtrude","CAP_FACE",FACE,{"disambiguationData":[OSD([sQuery(id+"F39.wireOp",EDGE,"E29"),sQuery(id+"F39.wireOp",EDGE,"E30")])],"isStart":false});var subQ32=sQuery(id+"F3.wireOp",EDGE,"E20.7.0");var subQ36=makeQuery(id+"F14.opLoft","CAP_FACE",FACE,{"disambiguationData":[OSD([makeQuery(id+"F3.imprint","IMPRINT",FACE,{"disambiguationData":[TD([[makeQuery(id+"F3.imprint","IMPRINT",EDGE,{"derivedFrom":subQ32}),-1.0]])]})])],"isStart":true});var subQ75=sQuery(id+"F3.wireOp",EDGE,"E18.bottom");var subQ80=makeQuery(id+"F5.opLoft","CAP_FACE",FACE,{"disambiguationData":[OSD([makeQuery(id+"F3.imprint","IMPRINT",FACE,{"disambiguationData":[TD([[makeQuery(id+"F3.imprint","IMPRINT",EDGE,{"derivedFrom":subQ75}),1.0]])]})])],"isStart":true});Q20=makeQuery(id+"F44.opFillet","BLEND_EDGE",EDGE,{"blendedFrom":[makeQuery(id+"F40.boolean.opBoolean","INTERSECT",EDGE,{"derivedFrom":[subQ12,subQ13]}),makeQuery(id+"F40.boolean.opBoolean","SPLIT",FACE,{"disambiguationData":[TD([subQ0])],"derivedFrom":makeQuery(id+"F35.boolean.opBoolean","SPLIT",FACE,{"disambiguationData":[TD([subQ12])],"derivedFrom":makeQuery(id+"F34.boolean.opBoolean","SPLIT",FACE,{"disambiguationData":[TD([subQ36])],"derivedFrom":makeQuery(id+"F33.boolean.opBoolean","SPLIT",FACE,{"disambiguationData":[TD([subQ36])],"derivedFrom":makeQuery(id+"F32.boolean.opBoolean","SPLIT",FACE,{"disambiguationData":[TD([subQ36])],"derivedFrom":makeQuery(id+"F31.boolean.opBoolean","SPLIT",FACE,{"disambiguationData":[TD([subQ36])],"derivedFrom":makeQuery(id+"F30.boolean.opBoolean","SPLIT",FACE,{"disambiguationData":[TD([subQ80])],"derivedFrom":makeQuery(id+"F29.boolean.opBoolean","SPLIT",FACE,{"disambiguationData":[TD([subQ80])],"derivedFrom":makeQuery(id+"F28.boolean.opBoolean","SPLIT",FACE,{"disambiguationData":[TD([subQ80])],"derivedFrom":makeQuery(id+"F27.boolean.opBoolean","SPLIT",FACE,{"disambiguationData":[TD([subQ80])],"derivedFrom":makeQuery(id+"F26.boolean.opBoolean","SPLIT",FACE,{"disambiguationData":[TD([subQ80])],"derivedFrom":makeQuery(id+"F25.boolean.opBoolean","SPLIT",FACE,{"disambiguationData":[TD([subQ80])],"derivedFrom":makeQuery(id+"F24.boolean.opBoolean","SPLIT",FACE,{"disambiguationData":[TD([subQ80])],"derivedFrom":makeQuery(id+"F1.opRevolve","SWEPT_FACE",FACE,{"disambiguationData":[OSD([sQuery(id+"F0.wireOp",EDGE,"E13")])]})})})})})})})})})})})})})})],"blendedInto":[makeQuery(id+"F40.boolean.opBoolean","SPLIT",FACE,{"disambiguationData":[TD([subQ0])],"derivedFrom":makeQuery(id+"F35.boolean.opBoolean","SPLIT",FACE,{"disambiguationData":[TD([subQ12])],"derivedFrom":makeQuery(id+"F34.boolean.opBoolean","SPLIT",FACE,{"disambiguationData":[TD([subQ36])],"derivedFrom":makeQuery(id+"F33.boolean.opBoolean","SPLIT",FACE,{"disambiguationData":[TD([subQ36])],"derivedFrom":makeQuery(id+"F32.boolean.opBoolean","SPLIT",FACE,{"disambiguationData":[TD([subQ36])],"derivedFrom":makeQuery(id+"F31.boolean.opBoolean","SPLIT",FACE,{"disambiguationData":[TD([subQ36])],"derivedFrom":makeQuery(id+"F30.boolean.opBoolean","SPLIT",FACE,{"disambiguationData":[TD([subQ80])],"derivedFrom":makeQuery(id+"F29.boolean.opBoolean","SPLIT",FACE,{"disambiguationData":[TD([subQ80])],"derivedFrom":makeQuery(id+"F28.boolean.opBoolean","SPLIT",FACE,{"disambiguationData":[TD([subQ80])],"derivedFrom":makeQuery(id+"F27.boolean.opBoolean","SPLIT",FACE,{"disambiguationData":[TD([subQ80])],"derivedFrom":makeQuery(id+"F26.boolean.opBoolean","SPLIT",FACE,{"disambiguationData":[TD([subQ80])],"derivedFrom":makeQuery(id+"F25.boolean.opBoolean","SPLIT",FACE,{"disambiguationData":[TD([subQ80])],"derivedFrom":makeQuery(id+"F24.boolean.opBoolean","SPLIT",FACE,{"disambiguationData":[TD([subQ80])],"derivedFrom":makeQuery(id+"F1.opRevolve","SWEPT_FACE",FACE,{"disambiguationData":[OSD([sQuery(id+"F0.wireOp",EDGE,"E13")])]})})})})})})})})})})})})})})]});}
            var Q21;
            {var subQ0=makeQuery(id+"F1.opRevolve","SWEPT_FACE",FACE,{"disambiguationData":[OSD([sQuery(id+"F0.wireOp",EDGE,"E10")])]});var subQ7=sQuery(id+"F4.wireOp",EDGE,"E26.5.3");var subQ8=sQuery(id+"F4.wireOp",EDGE,"E26.5.2");var subQ9=sQuery(id+"F3.wireOp",EDGE,"E20.5.3");var subQ10=sQuery(id+"F3.wireOp",EDGE,"E20.5.2");var subQ11=sQuery(id+"F3.wireOp",EDGE,"E20.5.1");var subQ12=makeQuery(id+"F16.opLoft","SWEPT_FACE",FACE,{"disambiguationData":[OSD([subQ11,subQ10,subQ9,sQuery(id+"F4.wireOp",EDGE,"E26.5.1"),subQ8,subQ7])]});var subQ13=makeQuery(id+"F40.opExtrude","CAP_FACE",FACE,{"disambiguationData":[OSD([sQuery(id+"F39.wireOp",EDGE,"E29"),sQuery(id+"F39.wireOp",EDGE,"E30")])],"isStart":false});var subQ26=sQuery(id+"F3.wireOp",EDGE,"E20.7.0");var subQ30=makeQuery(id+"F14.opLoft","CAP_FACE",FACE,{"disambiguationData":[OSD([makeQuery(id+"F3.imprint","IMPRINT",FACE,{"disambiguationData":[TD([[makeQuery(id+"F3.imprint","IMPRINT",EDGE,{"derivedFrom":subQ26}),-1.0]])]})])],"isStart":true});var subQ75=sQuery(id+"F3.wireOp",EDGE,"E18.bottom");var subQ80=makeQuery(id+"F5.opLoft","CAP_FACE",FACE,{"disambiguationData":[OSD([makeQuery(id+"F3.imprint","IMPRINT",FACE,{"disambiguationData":[TD([[makeQuery(id+"F3.imprint","IMPRINT",EDGE,{"derivedFrom":subQ75}),1.0]])]})])],"isStart":true});Q21=makeQuery(id+"F44.opFillet","BLEND_EDGE",EDGE,{"blendedFrom":[makeQuery(id+"F40.boolean.opBoolean","INTERSECT",EDGE,{"derivedFrom":[subQ12,subQ13]}),makeQuery(id+"F40.boolean.opBoolean","SPLIT",FACE,{"disambiguationData":[TD([subQ0])],"derivedFrom":makeQuery(id+"F36.boolean.opBoolean","SPLIT",FACE,{"disambiguationData":[TD([subQ12])],"derivedFrom":makeQuery(id+"F35.boolean.opBoolean","SPLIT",FACE,{"disambiguationData":[TD([subQ30])],"derivedFrom":makeQuery(id+"F34.boolean.opBoolean","SPLIT",FACE,{"disambiguationData":[TD([subQ30])],"derivedFrom":makeQuery(id+"F33.boolean.opBoolean","SPLIT",FACE,{"disambiguationData":[TD([subQ30])],"derivedFrom":makeQuery(id+"F32.boolean.opBoolean","SPLIT",FACE,{"disambiguationData":[TD([subQ30])],"derivedFrom":makeQuery(id+"F31.boolean.opBoolean","SPLIT",FACE,{"disambiguationData":[TD([subQ30])],"derivedFrom":makeQuery(id+"F30.boolean.opBoolean","SPLIT",FACE,{"disambiguationData":[TD([subQ80])],"derivedFrom":makeQuery(id+"F29.boolean.opBoolean","SPLIT",FACE,{"disambiguationData":[TD([subQ80])],"derivedFrom":makeQuery(id+"F28.boolean.opBoolean","SPLIT",FACE,{"disambiguationData":[TD([subQ80])],"derivedFrom":makeQuery(id+"F27.boolean.opBoolean","SPLIT",FACE,{"disambiguationData":[TD([subQ80])],"derivedFrom":makeQuery(id+"F26.boolean.opBoolean","SPLIT",FACE,{"disambiguationData":[TD([subQ80])],"derivedFrom":makeQuery(id+"F25.boolean.opBoolean","SPLIT",FACE,{"disambiguationData":[TD([subQ80])],"derivedFrom":makeQuery(id+"F24.boolean.opBoolean","SPLIT",FACE,{"disambiguationData":[TD([subQ80])],"derivedFrom":makeQuery(id+"F1.opRevolve","SWEPT_FACE",FACE,{"disambiguationData":[OSD([sQuery(id+"F0.wireOp",EDGE,"E13")])]})})})})})})})})})})})})})})})],"blendedInto":[makeQuery(id+"F40.boolean.opBoolean","SPLIT",FACE,{"disambiguationData":[TD([subQ0])],"derivedFrom":makeQuery(id+"F36.boolean.opBoolean","SPLIT",FACE,{"disambiguationData":[TD([subQ12])],"derivedFrom":makeQuery(id+"F35.boolean.opBoolean","SPLIT",FACE,{"disambiguationData":[TD([subQ30])],"derivedFrom":makeQuery(id+"F34.boolean.opBoolean","SPLIT",FACE,{"disambiguationData":[TD([subQ30])],"derivedFrom":makeQuery(id+"F33.boolean.opBoolean","SPLIT",FACE,{"disambiguationData":[TD([subQ30])],"derivedFrom":makeQuery(id+"F32.boolean.opBoolean","SPLIT",FACE,{"disambiguationData":[TD([subQ30])],"derivedFrom":makeQuery(id+"F31.boolean.opBoolean","SPLIT",FACE,{"disambiguationData":[TD([subQ30])],"derivedFrom":makeQuery(id+"F30.boolean.opBoolean","SPLIT",FACE,{"disambiguationData":[TD([subQ80])],"derivedFrom":makeQuery(id+"F29.boolean.opBoolean","SPLIT",FACE,{"disambiguationData":[TD([subQ80])],"derivedFrom":makeQuery(id+"F28.boolean.opBoolean","SPLIT",FACE,{"disambiguationData":[TD([subQ80])],"derivedFrom":makeQuery(id+"F27.boolean.opBoolean","SPLIT",FACE,{"disambiguationData":[TD([subQ80])],"derivedFrom":makeQuery(id+"F26.boolean.opBoolean","SPLIT",FACE,{"disambiguationData":[TD([subQ80])],"derivedFrom":makeQuery(id+"F25.boolean.opBoolean","SPLIT",FACE,{"disambiguationData":[TD([subQ80])],"derivedFrom":makeQuery(id+"F24.boolean.opBoolean","SPLIT",FACE,{"disambiguationData":[TD([subQ80])],"derivedFrom":makeQuery(id+"F1.opRevolve","SWEPT_FACE",FACE,{"disambiguationData":[OSD([sQuery(id+"F0.wireOp",EDGE,"E13")])]})})})})})})})})})})})})})})})]});}
            var Q22;
            {var subQ0=makeQuery(id+"F1.opRevolve","SWEPT_FACE",FACE,{"disambiguationData":[OSD([sQuery(id+"F0.wireOp",EDGE,"E10")])]});var subQ1=sQuery(id+"F4.wireOp",EDGE,"E26.6.3");var subQ2=sQuery(id+"F4.wireOp",EDGE,"E26.6.2");var subQ3=sQuery(id+"F3.wireOp",EDGE,"E20.6.3");var subQ4=sQuery(id+"F3.wireOp",EDGE,"E20.6.2");var subQ5=sQuery(id+"F3.wireOp",EDGE,"E20.6.1");var subQ6=makeQuery(id+"F15.opLoft","SWEPT_FACE",FACE,{"disambiguationData":[OSD([subQ5,subQ4,subQ3,sQuery(id+"F4.wireOp",EDGE,"E26.6.1"),subQ2,subQ1])]});var subQ13=makeQuery(id+"F40.opExtrude","CAP_FACE",FACE,{"disambiguationData":[OSD([sQuery(id+"F39.wireOp",EDGE,"E29"),sQuery(id+"F39.wireOp",EDGE,"E30")])],"isStart":false});var subQ19=sQuery(id+"F3.wireOp",EDGE,"E20.7.0");var subQ23=makeQuery(id+"F14.opLoft","CAP_FACE",FACE,{"disambiguationData":[OSD([makeQuery(id+"F3.imprint","IMPRINT",FACE,{"disambiguationData":[TD([[makeQuery(id+"F3.imprint","IMPRINT",EDGE,{"derivedFrom":subQ19}),-1.0]])]})])],"isStart":true});var subQ75=sQuery(id+"F3.wireOp",EDGE,"E18.bottom");var subQ80=makeQuery(id+"F5.opLoft","CAP_FACE",FACE,{"disambiguationData":[OSD([makeQuery(id+"F3.imprint","IMPRINT",FACE,{"disambiguationData":[TD([[makeQuery(id+"F3.imprint","IMPRINT",EDGE,{"derivedFrom":subQ75}),1.0]])]})])],"isStart":true});Q22=makeQuery(id+"F44.opFillet","BLEND_EDGE",EDGE,{"blendedFrom":[makeQuery(id+"F40.boolean.opBoolean","INTERSECT",EDGE,{"derivedFrom":[subQ6,subQ13]}),makeQuery(id+"F40.boolean.opBoolean","SPLIT",FACE,{"disambiguationData":[TD([subQ0])],"derivedFrom":makeQuery(id+"F37.boolean.opBoolean","SPLIT",FACE,{"disambiguationData":[TD([subQ6])],"derivedFrom":makeQuery(id+"F36.boolean.opBoolean","SPLIT",FACE,{"disambiguationData":[TD([subQ23])],"derivedFrom":makeQuery(id+"F35.boolean.opBoolean","SPLIT",FACE,{"disambiguationData":[TD([subQ23])],"derivedFrom":makeQuery(id+"F34.boolean.opBoolean","SPLIT",FACE,{"disambiguationData":[TD([subQ23])],"derivedFrom":makeQuery(id+"F33.boolean.opBoolean","SPLIT",FACE,{"disambiguationData":[TD([subQ23])],"derivedFrom":makeQuery(id+"F32.boolean.opBoolean","SPLIT",FACE,{"disambiguationData":[TD([subQ23])],"derivedFrom":makeQuery(id+"F31.boolean.opBoolean","SPLIT",FACE,{"disambiguationData":[TD([subQ23])],"derivedFrom":makeQuery(id+"F30.boolean.opBoolean","SPLIT",FACE,{"disambiguationData":[TD([subQ80])],"derivedFrom":makeQuery(id+"F29.boolean.opBoolean","SPLIT",FACE,{"disambiguationData":[TD([subQ80])],"derivedFrom":makeQuery(id+"F28.boolean.opBoolean","SPLIT",FACE,{"disambiguationData":[TD([subQ80])],"derivedFrom":makeQuery(id+"F27.boolean.opBoolean","SPLIT",FACE,{"disambiguationData":[TD([subQ80])],"derivedFrom":makeQuery(id+"F26.boolean.opBoolean","SPLIT",FACE,{"disambiguationData":[TD([subQ80])],"derivedFrom":makeQuery(id+"F25.boolean.opBoolean","SPLIT",FACE,{"disambiguationData":[TD([subQ80])],"derivedFrom":makeQuery(id+"F24.boolean.opBoolean","SPLIT",FACE,{"disambiguationData":[TD([subQ80])],"derivedFrom":makeQuery(id+"F1.opRevolve","SWEPT_FACE",FACE,{"disambiguationData":[OSD([sQuery(id+"F0.wireOp",EDGE,"E13")])]})})})})})})})})})})})})})})})})],"blendedInto":[makeQuery(id+"F40.boolean.opBoolean","SPLIT",FACE,{"disambiguationData":[TD([subQ0])],"derivedFrom":makeQuery(id+"F37.boolean.opBoolean","SPLIT",FACE,{"disambiguationData":[TD([subQ6])],"derivedFrom":makeQuery(id+"F36.boolean.opBoolean","SPLIT",FACE,{"disambiguationData":[TD([subQ23])],"derivedFrom":makeQuery(id+"F35.boolean.opBoolean","SPLIT",FACE,{"disambiguationData":[TD([subQ23])],"derivedFrom":makeQuery(id+"F34.boolean.opBoolean","SPLIT",FACE,{"disambiguationData":[TD([subQ23])],"derivedFrom":makeQuery(id+"F33.boolean.opBoolean","SPLIT",FACE,{"disambiguationData":[TD([subQ23])],"derivedFrom":makeQuery(id+"F32.boolean.opBoolean","SPLIT",FACE,{"disambiguationData":[TD([subQ23])],"derivedFrom":makeQuery(id+"F31.boolean.opBoolean","SPLIT",FACE,{"disambiguationData":[TD([subQ23])],"derivedFrom":makeQuery(id+"F30.boolean.opBoolean","SPLIT",FACE,{"disambiguationData":[TD([subQ80])],"derivedFrom":makeQuery(id+"F29.boolean.opBoolean","SPLIT",FACE,{"disambiguationData":[TD([subQ80])],"derivedFrom":makeQuery(id+"F28.boolean.opBoolean","SPLIT",FACE,{"disambiguationData":[TD([subQ80])],"derivedFrom":makeQuery(id+"F27.boolean.opBoolean","SPLIT",FACE,{"disambiguationData":[TD([subQ80])],"derivedFrom":makeQuery(id+"F26.boolean.opBoolean","SPLIT",FACE,{"disambiguationData":[TD([subQ80])],"derivedFrom":makeQuery(id+"F25.boolean.opBoolean","SPLIT",FACE,{"disambiguationData":[TD([subQ80])],"derivedFrom":makeQuery(id+"F24.boolean.opBoolean","SPLIT",FACE,{"disambiguationData":[TD([subQ80])],"derivedFrom":makeQuery(id+"F1.opRevolve","SWEPT_FACE",FACE,{"disambiguationData":[OSD([sQuery(id+"F0.wireOp",EDGE,"E13")])]})})})})})})})})})})})})})})})})]});}
            var Q23;
            {var subQ0=makeQuery(id+"F1.opRevolve","SWEPT_FACE",FACE,{"disambiguationData":[OSD([sQuery(id+"F0.wireOp",EDGE,"E10")])]});var subQ1=sQuery(id+"F4.wireOp",EDGE,"E26.7.3");var subQ2=sQuery(id+"F4.wireOp",EDGE,"E26.7.2");var subQ3=sQuery(id+"F3.wireOp",EDGE,"E20.7.3");var subQ4=sQuery(id+"F3.wireOp",EDGE,"E20.7.2");var subQ5=sQuery(id+"F3.wireOp",EDGE,"E20.7.1");var subQ6=makeQuery(id+"F14.opLoft","SWEPT_FACE",FACE,{"disambiguationData":[OSD([subQ5,subQ4,subQ3,sQuery(id+"F4.wireOp",EDGE,"E26.7.1"),subQ2,subQ1])]});var subQ13=makeQuery(id+"F40.opExtrude","CAP_FACE",FACE,{"disambiguationData":[OSD([sQuery(id+"F39.wireOp",EDGE,"E29"),sQuery(id+"F39.wireOp",EDGE,"E30")])],"isStart":false});var subQ20=sQuery(id+"F3.wireOp",EDGE,"E20.7.0");var subQ22=makeQuery(id+"F14.opLoft","CAP_FACE",FACE,{"disambiguationData":[OSD([makeQuery(id+"F3.imprint","IMPRINT",FACE,{"disambiguationData":[TD([[makeQuery(id+"F3.imprint","IMPRINT",EDGE,{"derivedFrom":subQ20}),-1.0]])]})])],"isStart":true});var subQ75=sQuery(id+"F3.wireOp",EDGE,"E18.bottom");var subQ80=makeQuery(id+"F5.opLoft","CAP_FACE",FACE,{"disambiguationData":[OSD([makeQuery(id+"F3.imprint","IMPRINT",FACE,{"disambiguationData":[TD([[makeQuery(id+"F3.imprint","IMPRINT",EDGE,{"derivedFrom":subQ75}),1.0]])]})])],"isStart":true});Q23=makeQuery(id+"F44.opFillet","BLEND_EDGE",EDGE,{"blendedFrom":[makeQuery(id+"F40.boolean.opBoolean","INTERSECT",EDGE,{"derivedFrom":[subQ6,subQ13]}),makeQuery(id+"F40.boolean.opBoolean","SPLIT",FACE,{"disambiguationData":[TD([subQ0])],"derivedFrom":makeQuery(id+"F38.boolean.opBoolean","SPLIT",FACE,{"disambiguationData":[TD([subQ6])],"derivedFrom":makeQuery(id+"F37.boolean.opBoolean","SPLIT",FACE,{"disambiguationData":[TD([subQ22])],"derivedFrom":makeQuery(id+"F36.boolean.opBoolean","SPLIT",FACE,{"disambiguationData":[TD([subQ22])],"derivedFrom":makeQuery(id+"F35.boolean.opBoolean","SPLIT",FACE,{"disambiguationData":[TD([subQ22])],"derivedFrom":makeQuery(id+"F34.boolean.opBoolean","SPLIT",FACE,{"disambiguationData":[TD([subQ22])],"derivedFrom":makeQuery(id+"F33.boolean.opBoolean","SPLIT",FACE,{"disambiguationData":[TD([subQ22])],"derivedFrom":makeQuery(id+"F32.boolean.opBoolean","SPLIT",FACE,{"disambiguationData":[TD([subQ22])],"derivedFrom":makeQuery(id+"F31.boolean.opBoolean","SPLIT",FACE,{"disambiguationData":[TD([subQ22])],"derivedFrom":makeQuery(id+"F30.boolean.opBoolean","SPLIT",FACE,{"disambiguationData":[TD([subQ80])],"derivedFrom":makeQuery(id+"F29.boolean.opBoolean","SPLIT",FACE,{"disambiguationData":[TD([subQ80])],"derivedFrom":makeQuery(id+"F28.boolean.opBoolean","SPLIT",FACE,{"disambiguationData":[TD([subQ80])],"derivedFrom":makeQuery(id+"F27.boolean.opBoolean","SPLIT",FACE,{"disambiguationData":[TD([subQ80])],"derivedFrom":makeQuery(id+"F26.boolean.opBoolean","SPLIT",FACE,{"disambiguationData":[TD([subQ80])],"derivedFrom":makeQuery(id+"F25.boolean.opBoolean","SPLIT",FACE,{"disambiguationData":[TD([subQ80])],"derivedFrom":makeQuery(id+"F24.boolean.opBoolean","SPLIT",FACE,{"disambiguationData":[TD([subQ80])],"derivedFrom":makeQuery(id+"F1.opRevolve","SWEPT_FACE",FACE,{"disambiguationData":[OSD([sQuery(id+"F0.wireOp",EDGE,"E13")])]})})})})})})})})})})})})})})})})})],"blendedInto":[makeQuery(id+"F40.boolean.opBoolean","SPLIT",FACE,{"disambiguationData":[TD([subQ0])],"derivedFrom":makeQuery(id+"F38.boolean.opBoolean","SPLIT",FACE,{"disambiguationData":[TD([subQ6])],"derivedFrom":makeQuery(id+"F37.boolean.opBoolean","SPLIT",FACE,{"disambiguationData":[TD([subQ22])],"derivedFrom":makeQuery(id+"F36.boolean.opBoolean","SPLIT",FACE,{"disambiguationData":[TD([subQ22])],"derivedFrom":makeQuery(id+"F35.boolean.opBoolean","SPLIT",FACE,{"disambiguationData":[TD([subQ22])],"derivedFrom":makeQuery(id+"F34.boolean.opBoolean","SPLIT",FACE,{"disambiguationData":[TD([subQ22])],"derivedFrom":makeQuery(id+"F33.boolean.opBoolean","SPLIT",FACE,{"disambiguationData":[TD([subQ22])],"derivedFrom":makeQuery(id+"F32.boolean.opBoolean","SPLIT",FACE,{"disambiguationData":[TD([subQ22])],"derivedFrom":makeQuery(id+"F31.boolean.opBoolean","SPLIT",FACE,{"disambiguationData":[TD([subQ22])],"derivedFrom":makeQuery(id+"F30.boolean.opBoolean","SPLIT",FACE,{"disambiguationData":[TD([subQ80])],"derivedFrom":makeQuery(id+"F29.boolean.opBoolean","SPLIT",FACE,{"disambiguationData":[TD([subQ80])],"derivedFrom":makeQuery(id+"F28.boolean.opBoolean","SPLIT",FACE,{"disambiguationData":[TD([subQ80])],"derivedFrom":makeQuery(id+"F27.boolean.opBoolean","SPLIT",FACE,{"disambiguationData":[TD([subQ80])],"derivedFrom":makeQuery(id+"F26.boolean.opBoolean","SPLIT",FACE,{"disambiguationData":[TD([subQ80])],"derivedFrom":makeQuery(id+"F25.boolean.opBoolean","SPLIT",FACE,{"disambiguationData":[TD([subQ80])],"derivedFrom":makeQuery(id+"F24.boolean.opBoolean","SPLIT",FACE,{"disambiguationData":[TD([subQ80])],"derivedFrom":makeQuery(id+"F1.opRevolve","SWEPT_FACE",FACE,{"disambiguationData":[OSD([sQuery(id+"F0.wireOp",EDGE,"E13")])]})})})})})})})})})})})})})})})})})]});}
            var Q24;
            {var subQ0=makeQuery(id+"F1.opRevolve","SWEPT_FACE",FACE,{"disambiguationData":[OSD([sQuery(id+"F0.wireOp",EDGE,"E10")])]});var subQ1=sQuery(id+"F3.wireOp",EDGE,"E20.8.3");var subQ2=sQuery(id+"F3.wireOp",EDGE,"E20.8.2");var subQ3=sQuery(id+"F3.wireOp",EDGE,"E20.8.1");var subQ4=makeQuery(id+"F13.opLoft","SWEPT_FACE",FACE,{"disambiguationData":[OSD([subQ3,subQ2,subQ1,sQuery(id+"F4.wireOp",EDGE,"E26.8.1"),sQuery(id+"F4.wireOp",EDGE,"E26.8.2"),sQuery(id+"F4.wireOp",EDGE,"E26.8.3")])]});var subQ5=makeQuery(id+"F40.opExtrude","CAP_FACE",FACE,{"disambiguationData":[OSD([sQuery(id+"F39.wireOp",EDGE,"E29"),sQuery(id+"F39.wireOp",EDGE,"E30")])],"isStart":false});var subQ10=sQuery(id+"F3.wireOp",EDGE,"E20.7.0");var subQ16=makeQuery(id+"F14.opLoft","CAP_FACE",FACE,{"disambiguationData":[OSD([makeQuery(id+"F3.imprint","IMPRINT",FACE,{"disambiguationData":[TD([[makeQuery(id+"F3.imprint","IMPRINT",EDGE,{"derivedFrom":subQ10}),-1.0]])]})])],"isStart":true});var subQ74=sQuery(id+"F3.wireOp",EDGE,"E18.bottom");var subQ79=makeQuery(id+"F5.opLoft","CAP_FACE",FACE,{"disambiguationData":[OSD([makeQuery(id+"F3.imprint","IMPRINT",FACE,{"disambiguationData":[TD([[makeQuery(id+"F3.imprint","IMPRINT",EDGE,{"derivedFrom":subQ74}),1.0]])]})])],"isStart":true});Q24=makeQuery(id+"F44.opFillet","BLEND_EDGE",EDGE,{"blendedFrom":[makeQuery(id+"F40.boolean.opBoolean","INTERSECT",EDGE,{"derivedFrom":[subQ4,subQ5]}),makeQuery(id+"F40.boolean.opBoolean","SPLIT",FACE,{"disambiguationData":[TD([subQ0])],"derivedFrom":makeQuery(id+"F38.boolean.opBoolean","SPLIT",FACE,{"disambiguationData":[TD([subQ4])],"derivedFrom":makeQuery(id+"F37.boolean.opBoolean","SPLIT",FACE,{"disambiguationData":[TD([subQ16])],"derivedFrom":makeQuery(id+"F36.boolean.opBoolean","SPLIT",FACE,{"disambiguationData":[TD([subQ16])],"derivedFrom":makeQuery(id+"F35.boolean.opBoolean","SPLIT",FACE,{"disambiguationData":[TD([subQ16])],"derivedFrom":makeQuery(id+"F34.boolean.opBoolean","SPLIT",FACE,{"disambiguationData":[TD([subQ16])],"derivedFrom":makeQuery(id+"F33.boolean.opBoolean","SPLIT",FACE,{"disambiguationData":[TD([subQ16])],"derivedFrom":makeQuery(id+"F32.boolean.opBoolean","SPLIT",FACE,{"disambiguationData":[TD([subQ16])],"derivedFrom":makeQuery(id+"F31.boolean.opBoolean","SPLIT",FACE,{"disambiguationData":[TD([subQ16])],"derivedFrom":makeQuery(id+"F30.boolean.opBoolean","SPLIT",FACE,{"disambiguationData":[TD([subQ79])],"derivedFrom":makeQuery(id+"F29.boolean.opBoolean","SPLIT",FACE,{"disambiguationData":[TD([subQ79])],"derivedFrom":makeQuery(id+"F28.boolean.opBoolean","SPLIT",FACE,{"disambiguationData":[TD([subQ79])],"derivedFrom":makeQuery(id+"F27.boolean.opBoolean","SPLIT",FACE,{"disambiguationData":[TD([subQ79])],"derivedFrom":makeQuery(id+"F26.boolean.opBoolean","SPLIT",FACE,{"disambiguationData":[TD([subQ79])],"derivedFrom":makeQuery(id+"F25.boolean.opBoolean","SPLIT",FACE,{"disambiguationData":[TD([subQ79])],"derivedFrom":makeQuery(id+"F24.boolean.opBoolean","SPLIT",FACE,{"disambiguationData":[TD([subQ79])],"derivedFrom":makeQuery(id+"F1.opRevolve","SWEPT_FACE",FACE,{"disambiguationData":[OSD([sQuery(id+"F0.wireOp",EDGE,"E13")])]})})})})})})})})})})})})})})})})})],"blendedInto":[makeQuery(id+"F40.boolean.opBoolean","SPLIT",FACE,{"disambiguationData":[TD([subQ0])],"derivedFrom":makeQuery(id+"F38.boolean.opBoolean","SPLIT",FACE,{"disambiguationData":[TD([subQ4])],"derivedFrom":makeQuery(id+"F37.boolean.opBoolean","SPLIT",FACE,{"disambiguationData":[TD([subQ16])],"derivedFrom":makeQuery(id+"F36.boolean.opBoolean","SPLIT",FACE,{"disambiguationData":[TD([subQ16])],"derivedFrom":makeQuery(id+"F35.boolean.opBoolean","SPLIT",FACE,{"disambiguationData":[TD([subQ16])],"derivedFrom":makeQuery(id+"F34.boolean.opBoolean","SPLIT",FACE,{"disambiguationData":[TD([subQ16])],"derivedFrom":makeQuery(id+"F33.boolean.opBoolean","SPLIT",FACE,{"disambiguationData":[TD([subQ16])],"derivedFrom":makeQuery(id+"F32.boolean.opBoolean","SPLIT",FACE,{"disambiguationData":[TD([subQ16])],"derivedFrom":makeQuery(id+"F31.boolean.opBoolean","SPLIT",FACE,{"disambiguationData":[TD([subQ16])],"derivedFrom":makeQuery(id+"F30.boolean.opBoolean","SPLIT",FACE,{"disambiguationData":[TD([subQ79])],"derivedFrom":makeQuery(id+"F29.boolean.opBoolean","SPLIT",FACE,{"disambiguationData":[TD([subQ79])],"derivedFrom":makeQuery(id+"F28.boolean.opBoolean","SPLIT",FACE,{"disambiguationData":[TD([subQ79])],"derivedFrom":makeQuery(id+"F27.boolean.opBoolean","SPLIT",FACE,{"disambiguationData":[TD([subQ79])],"derivedFrom":makeQuery(id+"F26.boolean.opBoolean","SPLIT",FACE,{"disambiguationData":[TD([subQ79])],"derivedFrom":makeQuery(id+"F25.boolean.opBoolean","SPLIT",FACE,{"disambiguationData":[TD([subQ79])],"derivedFrom":makeQuery(id+"F24.boolean.opBoolean","SPLIT",FACE,{"disambiguationData":[TD([subQ79])],"derivedFrom":makeQuery(id+"F1.opRevolve","SWEPT_FACE",FACE,{"disambiguationData":[OSD([sQuery(id+"F0.wireOp",EDGE,"E13")])]})})})})})})})})})})})})})})})})})]});}
            var Q25;
            {var subQ0=makeQuery(id+"F1.opRevolve","SWEPT_FACE",FACE,{"disambiguationData":[OSD([sQuery(id+"F0.wireOp",EDGE,"E10")])]});var subQ1=sQuery(id+"F3.wireOp",EDGE,"E20.9.3");var subQ2=sQuery(id+"F3.wireOp",EDGE,"E20.9.2");var subQ3=sQuery(id+"F3.wireOp",EDGE,"E20.9.1");var subQ4=makeQuery(id+"F12.opLoft","SWEPT_FACE",FACE,{"disambiguationData":[OSD([subQ3,subQ2,subQ1,sQuery(id+"F4.wireOp",EDGE,"E26.9.1"),sQuery(id+"F4.wireOp",EDGE,"E26.9.2"),sQuery(id+"F4.wireOp",EDGE,"E26.9.3")])]});var subQ9=makeQuery(id+"F40.opExtrude","CAP_FACE",FACE,{"disambiguationData":[OSD([sQuery(id+"F39.wireOp",EDGE,"E29"),sQuery(id+"F39.wireOp",EDGE,"E30")])],"isStart":false});Q25=makeQuery(id+"F44.opFillet","BLEND_EDGE",EDGE,{"blendedFrom":[makeQuery(id+"F40.boolean.opBoolean","INTERSECT",EDGE,{"derivedFrom":[subQ4,subQ9]}),makeQuery(id+"F40.boolean.opBoolean","SPLIT",FACE,{"disambiguationData":[TD([subQ0])],"derivedFrom":makeQuery(id+"F24.boolean.opBoolean","SPLIT",FACE,{"disambiguationData":[TD([subQ4])],"derivedFrom":makeQuery(id+"F1.opRevolve","SWEPT_FACE",FACE,{"disambiguationData":[OSD([sQuery(id+"F0.wireOp",EDGE,"E13")])]})})})],"blendedInto":[makeQuery(id+"F40.boolean.opBoolean","SPLIT",FACE,{"disambiguationData":[TD([subQ0])],"derivedFrom":makeQuery(id+"F24.boolean.opBoolean","SPLIT",FACE,{"disambiguationData":[TD([subQ4])],"derivedFrom":makeQuery(id+"F1.opRevolve","SWEPT_FACE",FACE,{"disambiguationData":[OSD([sQuery(id+"F0.wireOp",EDGE,"E13")])]})})})]});}
            var Q26;
            {var subQ0=makeQuery(id+"F1.opRevolve","SWEPT_FACE",FACE,{"disambiguationData":[OSD([sQuery(id+"F0.wireOp",EDGE,"E10")])]});var subQ1=sQuery(id+"F4.wireOp",EDGE,"E26.10.3");var subQ2=sQuery(id+"F4.wireOp",EDGE,"E26.10.2");var subQ3=sQuery(id+"F3.wireOp",EDGE,"E20.10.3");var subQ4=sQuery(id+"F3.wireOp",EDGE,"E20.10.2");var subQ5=sQuery(id+"F3.wireOp",EDGE,"E20.10.1");var subQ6=makeQuery(id+"F11.opLoft","SWEPT_FACE",FACE,{"disambiguationData":[OSD([subQ5,subQ4,subQ3,sQuery(id+"F4.wireOp",EDGE,"E26.10.1"),subQ2,subQ1])]});var subQ11=makeQuery(id+"F40.opExtrude","CAP_FACE",FACE,{"disambiguationData":[OSD([sQuery(id+"F39.wireOp",EDGE,"E29"),sQuery(id+"F39.wireOp",EDGE,"E30")])],"isStart":false});var subQ89=sQuery(id+"F3.wireOp",EDGE,"E18.bottom");Q26=makeQuery(id+"F44.opFillet","BLEND_EDGE",EDGE,{"blendedFrom":[makeQuery(id+"F40.boolean.opBoolean","INTERSECT",EDGE,{"derivedFrom":[subQ6,subQ11]}),makeQuery(id+"F40.boolean.opBoolean","SPLIT",FACE,{"disambiguationData":[TD([subQ0])],"derivedFrom":makeQuery(id+"F25.boolean.opBoolean","SPLIT",FACE,{"disambiguationData":[TD([subQ6])],"derivedFrom":makeQuery(id+"F24.boolean.opBoolean","SPLIT",FACE,{"disambiguationData":[TD([makeQuery(id+"F5.opLoft","CAP_FACE",FACE,{"disambiguationData":[OSD([makeQuery(id+"F3.imprint","IMPRINT",FACE,{"disambiguationData":[TD([[makeQuery(id+"F3.imprint","IMPRINT",EDGE,{"derivedFrom":subQ89}),1.0]])]})])],"isStart":true})])],"derivedFrom":makeQuery(id+"F1.opRevolve","SWEPT_FACE",FACE,{"disambiguationData":[OSD([sQuery(id+"F0.wireOp",EDGE,"E13")])]})})})})],"blendedInto":[makeQuery(id+"F40.boolean.opBoolean","SPLIT",FACE,{"disambiguationData":[TD([subQ0])],"derivedFrom":makeQuery(id+"F25.boolean.opBoolean","SPLIT",FACE,{"disambiguationData":[TD([subQ6])],"derivedFrom":makeQuery(id+"F24.boolean.opBoolean","SPLIT",FACE,{"disambiguationData":[TD([makeQuery(id+"F5.opLoft","CAP_FACE",FACE,{"disambiguationData":[OSD([makeQuery(id+"F3.imprint","IMPRINT",FACE,{"disambiguationData":[TD([[makeQuery(id+"F3.imprint","IMPRINT",EDGE,{"derivedFrom":subQ89}),1.0]])]})])],"isStart":true})])],"derivedFrom":makeQuery(id+"F1.opRevolve","SWEPT_FACE",FACE,{"disambiguationData":[OSD([sQuery(id+"F0.wireOp",EDGE,"E13")])]})})})})]});}
            var Q27;
            {var subQ0=makeQuery(id+"F1.opRevolve","SWEPT_FACE",FACE,{"disambiguationData":[OSD([sQuery(id+"F0.wireOp",EDGE,"E10")])]});var subQ1=sQuery(id+"F4.wireOp",EDGE,"E26.11.3");var subQ2=sQuery(id+"F4.wireOp",EDGE,"E26.11.2");var subQ3=sQuery(id+"F3.wireOp",EDGE,"E20.11.3");var subQ4=sQuery(id+"F3.wireOp",EDGE,"E20.11.2");var subQ5=sQuery(id+"F3.wireOp",EDGE,"E20.11.1");var subQ6=makeQuery(id+"F10.opLoft","SWEPT_FACE",FACE,{"disambiguationData":[OSD([subQ5,subQ4,subQ3,sQuery(id+"F4.wireOp",EDGE,"E26.11.1"),subQ2,subQ1])]});var subQ13=makeQuery(id+"F40.opExtrude","CAP_FACE",FACE,{"disambiguationData":[OSD([sQuery(id+"F39.wireOp",EDGE,"E29"),sQuery(id+"F39.wireOp",EDGE,"E30")])],"isStart":false});var subQ79=sQuery(id+"F3.wireOp",EDGE,"E18.bottom");var subQ82=makeQuery(id+"F5.opLoft","CAP_FACE",FACE,{"disambiguationData":[OSD([makeQuery(id+"F3.imprint","IMPRINT",FACE,{"disambiguationData":[TD([[makeQuery(id+"F3.imprint","IMPRINT",EDGE,{"derivedFrom":subQ79}),1.0]])]})])],"isStart":true});Q27=makeQuery(id+"F44.opFillet","BLEND_EDGE",EDGE,{"blendedFrom":[makeQuery(id+"F40.boolean.opBoolean","INTERSECT",EDGE,{"derivedFrom":[subQ6,subQ13]}),makeQuery(id+"F40.boolean.opBoolean","SPLIT",FACE,{"disambiguationData":[TD([subQ0])],"derivedFrom":makeQuery(id+"F26.boolean.opBoolean","SPLIT",FACE,{"disambiguationData":[TD([subQ6])],"derivedFrom":makeQuery(id+"F25.boolean.opBoolean","SPLIT",FACE,{"disambiguationData":[TD([subQ82])],"derivedFrom":makeQuery(id+"F24.boolean.opBoolean","SPLIT",FACE,{"disambiguationData":[TD([subQ82])],"derivedFrom":makeQuery(id+"F1.opRevolve","SWEPT_FACE",FACE,{"disambiguationData":[OSD([sQuery(id+"F0.wireOp",EDGE,"E13")])]})})})})})],"blendedInto":[makeQuery(id+"F40.boolean.opBoolean","SPLIT",FACE,{"disambiguationData":[TD([subQ0])],"derivedFrom":makeQuery(id+"F26.boolean.opBoolean","SPLIT",FACE,{"disambiguationData":[TD([subQ6])],"derivedFrom":makeQuery(id+"F25.boolean.opBoolean","SPLIT",FACE,{"disambiguationData":[TD([subQ82])],"derivedFrom":makeQuery(id+"F24.boolean.opBoolean","SPLIT",FACE,{"disambiguationData":[TD([subQ82])],"derivedFrom":makeQuery(id+"F1.opRevolve","SWEPT_FACE",FACE,{"disambiguationData":[OSD([sQuery(id+"F0.wireOp",EDGE,"E13")])]})})})})})]});}
            var Q28;
            {var subQ0=makeQuery(id+"F1.opRevolve","SWEPT_FACE",FACE,{"disambiguationData":[OSD([sQuery(id+"F0.wireOp",EDGE,"E10")])]});var subQ1=sQuery(id+"F4.wireOp",EDGE,"E26.12.3");var subQ2=sQuery(id+"F4.wireOp",EDGE,"E26.12.2");var subQ3=sQuery(id+"F3.wireOp",EDGE,"E20.12.3");var subQ4=sQuery(id+"F3.wireOp",EDGE,"E20.12.2");var subQ5=sQuery(id+"F3.wireOp",EDGE,"E20.12.1");var subQ6=makeQuery(id+"F9.opLoft","SWEPT_FACE",FACE,{"disambiguationData":[OSD([subQ5,subQ4,subQ3,sQuery(id+"F4.wireOp",EDGE,"E26.12.1"),subQ2,subQ1])]});var subQ7=makeQuery(id+"F40.opExtrude","CAP_FACE",FACE,{"disambiguationData":[OSD([sQuery(id+"F39.wireOp",EDGE,"E29"),sQuery(id+"F39.wireOp",EDGE,"E30")])],"isStart":false});var subQ74=sQuery(id+"F3.wireOp",EDGE,"E18.bottom");var subQ77=makeQuery(id+"F5.opLoft","CAP_FACE",FACE,{"disambiguationData":[OSD([makeQuery(id+"F3.imprint","IMPRINT",FACE,{"disambiguationData":[TD([[makeQuery(id+"F3.imprint","IMPRINT",EDGE,{"derivedFrom":subQ74}),1.0]])]})])],"isStart":true});Q28=makeQuery(id+"F44.opFillet","BLEND_EDGE",EDGE,{"blendedFrom":[makeQuery(id+"F40.boolean.opBoolean","INTERSECT",EDGE,{"derivedFrom":[subQ6,subQ7]}),makeQuery(id+"F40.boolean.opBoolean","SPLIT",FACE,{"disambiguationData":[TD([subQ0])],"derivedFrom":makeQuery(id+"F27.boolean.opBoolean","SPLIT",FACE,{"disambiguationData":[TD([subQ6])],"derivedFrom":makeQuery(id+"F26.boolean.opBoolean","SPLIT",FACE,{"disambiguationData":[TD([subQ77])],"derivedFrom":makeQuery(id+"F25.boolean.opBoolean","SPLIT",FACE,{"disambiguationData":[TD([subQ77])],"derivedFrom":makeQuery(id+"F24.boolean.opBoolean","SPLIT",FACE,{"disambiguationData":[TD([subQ77])],"derivedFrom":makeQuery(id+"F1.opRevolve","SWEPT_FACE",FACE,{"disambiguationData":[OSD([sQuery(id+"F0.wireOp",EDGE,"E13")])]})})})})})})],"blendedInto":[makeQuery(id+"F40.boolean.opBoolean","SPLIT",FACE,{"disambiguationData":[TD([subQ0])],"derivedFrom":makeQuery(id+"F27.boolean.opBoolean","SPLIT",FACE,{"disambiguationData":[TD([subQ6])],"derivedFrom":makeQuery(id+"F26.boolean.opBoolean","SPLIT",FACE,{"disambiguationData":[TD([subQ77])],"derivedFrom":makeQuery(id+"F25.boolean.opBoolean","SPLIT",FACE,{"disambiguationData":[TD([subQ77])],"derivedFrom":makeQuery(id+"F24.boolean.opBoolean","SPLIT",FACE,{"disambiguationData":[TD([subQ77])],"derivedFrom":makeQuery(id+"F1.opRevolve","SWEPT_FACE",FACE,{"disambiguationData":[OSD([sQuery(id+"F0.wireOp",EDGE,"E13")])]})})})})})})]});}
            var Q29;
            {var subQ0=makeQuery(id+"F1.opRevolve","SWEPT_FACE",FACE,{"disambiguationData":[OSD([sQuery(id+"F0.wireOp",EDGE,"E10")])]});var subQ1=sQuery(id+"F4.wireOp",EDGE,"E26.13.3");var subQ2=sQuery(id+"F4.wireOp",EDGE,"E26.13.2");var subQ3=sQuery(id+"F3.wireOp",EDGE,"E20.13.3");var subQ4=sQuery(id+"F3.wireOp",EDGE,"E20.13.2");var subQ5=sQuery(id+"F3.wireOp",EDGE,"E20.13.1");var subQ6=makeQuery(id+"F8.opLoft","SWEPT_FACE",FACE,{"disambiguationData":[OSD([subQ5,subQ4,subQ3,sQuery(id+"F4.wireOp",EDGE,"E26.13.1"),subQ2,subQ1])]});var subQ13=makeQuery(id+"F40.opExtrude","CAP_FACE",FACE,{"disambiguationData":[OSD([sQuery(id+"F39.wireOp",EDGE,"E29"),sQuery(id+"F39.wireOp",EDGE,"E30")])],"isStart":false});var subQ56=sQuery(id+"F3.wireOp",EDGE,"E18.bottom");var subQ59=makeQuery(id+"F5.opLoft","CAP_FACE",FACE,{"disambiguationData":[OSD([makeQuery(id+"F3.imprint","IMPRINT",FACE,{"disambiguationData":[TD([[makeQuery(id+"F3.imprint","IMPRINT",EDGE,{"derivedFrom":subQ56}),1.0]])]})])],"isStart":true});Q29=makeQuery(id+"F44.opFillet","BLEND_EDGE",EDGE,{"blendedFrom":[makeQuery(id+"F40.boolean.opBoolean","INTERSECT",EDGE,{"derivedFrom":[subQ6,subQ13]}),makeQuery(id+"F40.boolean.opBoolean","SPLIT",FACE,{"disambiguationData":[TD([subQ0])],"derivedFrom":makeQuery(id+"F28.boolean.opBoolean","SPLIT",FACE,{"disambiguationData":[TD([subQ6])],"derivedFrom":makeQuery(id+"F27.boolean.opBoolean","SPLIT",FACE,{"disambiguationData":[TD([subQ59])],"derivedFrom":makeQuery(id+"F26.boolean.opBoolean","SPLIT",FACE,{"disambiguationData":[TD([subQ59])],"derivedFrom":makeQuery(id+"F25.boolean.opBoolean","SPLIT",FACE,{"disambiguationData":[TD([subQ59])],"derivedFrom":makeQuery(id+"F24.boolean.opBoolean","SPLIT",FACE,{"disambiguationData":[TD([subQ59])],"derivedFrom":makeQuery(id+"F1.opRevolve","SWEPT_FACE",FACE,{"disambiguationData":[OSD([sQuery(id+"F0.wireOp",EDGE,"E13")])]})})})})})})})],"blendedInto":[makeQuery(id+"F40.boolean.opBoolean","SPLIT",FACE,{"disambiguationData":[TD([subQ0])],"derivedFrom":makeQuery(id+"F28.boolean.opBoolean","SPLIT",FACE,{"disambiguationData":[TD([subQ6])],"derivedFrom":makeQuery(id+"F27.boolean.opBoolean","SPLIT",FACE,{"disambiguationData":[TD([subQ59])],"derivedFrom":makeQuery(id+"F26.boolean.opBoolean","SPLIT",FACE,{"disambiguationData":[TD([subQ59])],"derivedFrom":makeQuery(id+"F25.boolean.opBoolean","SPLIT",FACE,{"disambiguationData":[TD([subQ59])],"derivedFrom":makeQuery(id+"F24.boolean.opBoolean","SPLIT",FACE,{"disambiguationData":[TD([subQ59])],"derivedFrom":makeQuery(id+"F1.opRevolve","SWEPT_FACE",FACE,{"disambiguationData":[OSD([sQuery(id+"F0.wireOp",EDGE,"E13")])]})})})})})})})]});}
            var Q30;
            {var subQ0=makeQuery(id+"F1.opRevolve","SWEPT_FACE",FACE,{"disambiguationData":[OSD([sQuery(id+"F0.wireOp",EDGE,"E10")])]});var subQ1=sQuery(id+"F4.wireOp",EDGE,"E26.14.3");var subQ2=sQuery(id+"F4.wireOp",EDGE,"E26.14.2");var subQ3=sQuery(id+"F3.wireOp",EDGE,"E20.14.3");var subQ4=sQuery(id+"F3.wireOp",EDGE,"E20.14.2");var subQ5=sQuery(id+"F3.wireOp",EDGE,"E20.14.1");var subQ6=makeQuery(id+"F7.opLoft","SWEPT_FACE",FACE,{"disambiguationData":[OSD([subQ5,subQ4,subQ3,sQuery(id+"F4.wireOp",EDGE,"E26.14.1"),subQ2,subQ1])]});var subQ13=makeQuery(id+"F40.opExtrude","CAP_FACE",FACE,{"disambiguationData":[OSD([sQuery(id+"F39.wireOp",EDGE,"E29"),sQuery(id+"F39.wireOp",EDGE,"E30")])],"isStart":false});var subQ48=sQuery(id+"F3.wireOp",EDGE,"E18.bottom");var subQ51=makeQuery(id+"F5.opLoft","CAP_FACE",FACE,{"disambiguationData":[OSD([makeQuery(id+"F3.imprint","IMPRINT",FACE,{"disambiguationData":[TD([[makeQuery(id+"F3.imprint","IMPRINT",EDGE,{"derivedFrom":subQ48}),1.0]])]})])],"isStart":true});Q30=makeQuery(id+"F44.opFillet","BLEND_EDGE",EDGE,{"blendedFrom":[makeQuery(id+"F40.boolean.opBoolean","INTERSECT",EDGE,{"derivedFrom":[subQ6,subQ13]}),makeQuery(id+"F40.boolean.opBoolean","SPLIT",FACE,{"disambiguationData":[TD([subQ0])],"derivedFrom":makeQuery(id+"F29.boolean.opBoolean","SPLIT",FACE,{"disambiguationData":[TD([subQ6])],"derivedFrom":makeQuery(id+"F28.boolean.opBoolean","SPLIT",FACE,{"disambiguationData":[TD([subQ51])],"derivedFrom":makeQuery(id+"F27.boolean.opBoolean","SPLIT",FACE,{"disambiguationData":[TD([subQ51])],"derivedFrom":makeQuery(id+"F26.boolean.opBoolean","SPLIT",FACE,{"disambiguationData":[TD([subQ51])],"derivedFrom":makeQuery(id+"F25.boolean.opBoolean","SPLIT",FACE,{"disambiguationData":[TD([subQ51])],"derivedFrom":makeQuery(id+"F24.boolean.opBoolean","SPLIT",FACE,{"disambiguationData":[TD([subQ51])],"derivedFrom":makeQuery(id+"F1.opRevolve","SWEPT_FACE",FACE,{"disambiguationData":[OSD([sQuery(id+"F0.wireOp",EDGE,"E13")])]})})})})})})})})],"blendedInto":[makeQuery(id+"F40.boolean.opBoolean","SPLIT",FACE,{"disambiguationData":[TD([subQ0])],"derivedFrom":makeQuery(id+"F29.boolean.opBoolean","SPLIT",FACE,{"disambiguationData":[TD([subQ6])],"derivedFrom":makeQuery(id+"F28.boolean.opBoolean","SPLIT",FACE,{"disambiguationData":[TD([subQ51])],"derivedFrom":makeQuery(id+"F27.boolean.opBoolean","SPLIT",FACE,{"disambiguationData":[TD([subQ51])],"derivedFrom":makeQuery(id+"F26.boolean.opBoolean","SPLIT",FACE,{"disambiguationData":[TD([subQ51])],"derivedFrom":makeQuery(id+"F25.boolean.opBoolean","SPLIT",FACE,{"disambiguationData":[TD([subQ51])],"derivedFrom":makeQuery(id+"F24.boolean.opBoolean","SPLIT",FACE,{"disambiguationData":[TD([subQ51])],"derivedFrom":makeQuery(id+"F1.opRevolve","SWEPT_FACE",FACE,{"disambiguationData":[OSD([sQuery(id+"F0.wireOp",EDGE,"E13")])]})})})})})})})})]});}
            var Q31;
            {var subQ0=makeQuery(id+"F1.opRevolve","SWEPT_FACE",FACE,{"disambiguationData":[OSD([sQuery(id+"F0.wireOp",EDGE,"E10")])]});var subQ7=sQuery(id+"F4.wireOp",EDGE,"E26.15.3");var subQ8=sQuery(id+"F4.wireOp",EDGE,"E26.15.2");var subQ9=sQuery(id+"F3.wireOp",EDGE,"E20.15.3");var subQ10=sQuery(id+"F3.wireOp",EDGE,"E20.15.2");var subQ11=sQuery(id+"F3.wireOp",EDGE,"E20.15.1");var subQ12=makeQuery(id+"F6.opLoft","SWEPT_FACE",FACE,{"disambiguationData":[OSD([subQ11,subQ10,subQ9,sQuery(id+"F4.wireOp",EDGE,"E26.15.1"),subQ8,subQ7])]});var subQ13=makeQuery(id+"F40.opExtrude","CAP_FACE",FACE,{"disambiguationData":[OSD([sQuery(id+"F39.wireOp",EDGE,"E29"),sQuery(id+"F39.wireOp",EDGE,"E30")])],"isStart":false});var subQ47=sQuery(id+"F3.wireOp",EDGE,"E18.bottom");var subQ50=makeQuery(id+"F5.opLoft","CAP_FACE",FACE,{"disambiguationData":[OSD([makeQuery(id+"F3.imprint","IMPRINT",FACE,{"disambiguationData":[TD([[makeQuery(id+"F3.imprint","IMPRINT",EDGE,{"derivedFrom":subQ47}),1.0]])]})])],"isStart":true});Q31=makeQuery(id+"F44.opFillet","BLEND_EDGE",EDGE,{"blendedFrom":[makeQuery(id+"F40.boolean.opBoolean","INTERSECT",EDGE,{"derivedFrom":[subQ12,subQ13]}),makeQuery(id+"F40.boolean.opBoolean","SPLIT",FACE,{"disambiguationData":[TD([subQ0])],"derivedFrom":makeQuery(id+"F30.boolean.opBoolean","SPLIT",FACE,{"disambiguationData":[TD([subQ12])],"derivedFrom":makeQuery(id+"F29.boolean.opBoolean","SPLIT",FACE,{"disambiguationData":[TD([subQ50])],"derivedFrom":makeQuery(id+"F28.boolean.opBoolean","SPLIT",FACE,{"disambiguationData":[TD([subQ50])],"derivedFrom":makeQuery(id+"F27.boolean.opBoolean","SPLIT",FACE,{"disambiguationData":[TD([subQ50])],"derivedFrom":makeQuery(id+"F26.boolean.opBoolean","SPLIT",FACE,{"disambiguationData":[TD([subQ50])],"derivedFrom":makeQuery(id+"F25.boolean.opBoolean","SPLIT",FACE,{"disambiguationData":[TD([subQ50])],"derivedFrom":makeQuery(id+"F24.boolean.opBoolean","SPLIT",FACE,{"disambiguationData":[TD([subQ50])],"derivedFrom":makeQuery(id+"F1.opRevolve","SWEPT_FACE",FACE,{"disambiguationData":[OSD([sQuery(id+"F0.wireOp",EDGE,"E13")])]})})})})})})})})})],"blendedInto":[makeQuery(id+"F40.boolean.opBoolean","SPLIT",FACE,{"disambiguationData":[TD([subQ0])],"derivedFrom":makeQuery(id+"F30.boolean.opBoolean","SPLIT",FACE,{"disambiguationData":[TD([subQ12])],"derivedFrom":makeQuery(id+"F29.boolean.opBoolean","SPLIT",FACE,{"disambiguationData":[TD([subQ50])],"derivedFrom":makeQuery(id+"F28.boolean.opBoolean","SPLIT",FACE,{"disambiguationData":[TD([subQ50])],"derivedFrom":makeQuery(id+"F27.boolean.opBoolean","SPLIT",FACE,{"disambiguationData":[TD([subQ50])],"derivedFrom":makeQuery(id+"F26.boolean.opBoolean","SPLIT",FACE,{"disambiguationData":[TD([subQ50])],"derivedFrom":makeQuery(id+"F25.boolean.opBoolean","SPLIT",FACE,{"disambiguationData":[TD([subQ50])],"derivedFrom":makeQuery(id+"F24.boolean.opBoolean","SPLIT",FACE,{"disambiguationData":[TD([subQ50])],"derivedFrom":makeQuery(id+"F1.opRevolve","SWEPT_FACE",FACE,{"disambiguationData":[OSD([sQuery(id+"F0.wireOp",EDGE,"E13")])]})})})})})})})})})]});}
            fillet(context, id + "F45", {"entities" : qUnion([Q0, Q1, Q2, Q3, Q4, Q5, Q6, Q7, Q8, Q9, Q10, Q11, Q12, Q13, Q14, Q15, Q16, Q17, Q18, Q19, Q20, Q21, Q22, Q23, Q24, Q25, Q26, Q27, Q28, Q29, Q30, Q31]), "radius" : 4 * mm, "tangentPropagation" : true, "allowEdgeOverflow" : false});
        }
        {
            var Q0;
            Q0=makeQuery(id+"F19.boolean.opBoolean","INTERSECT",EDGE,{"derivedFrom":[makeQuery(id+"F1.opRevolve","SWEPT_FACE",FACE,{"disambiguationData":[OSD([sQuery(id+"F0.wireOp",EDGE,"E13")])]}),makeQuery(id+"F19.opLoft","SWEPT_FACE",FACE,{"disambiguationData":[OSD([sQuery(id+"F3.wireOp",EDGE,"E20.2.0"),sQuery(id+"F3.wireOp",EDGE,"E20.2.1"),sQuery(id+"F3.wireOp",EDGE,"E20.2.3"),sQuery(id+"F4.wireOp",EDGE,"E26.2.0"),sQuery(id+"F4.wireOp",EDGE,"E26.2.2"),sQuery(id+"F4.wireOp",EDGE,"E26.2.3")])]})]});
            var Q1;
            Q1=makeQuery(id+"F20.boolean.opBoolean","INTERSECT",EDGE,{"derivedFrom":[makeQuery(id+"F1.opRevolve","SWEPT_FACE",FACE,{"disambiguationData":[OSD([sQuery(id+"F0.wireOp",EDGE,"E13")])]}),makeQuery(id+"F20.opLoft","SWEPT_FACE",FACE,{"disambiguationData":[OSD([sQuery(id+"F3.wireOp",EDGE,"E20.1.0"),sQuery(id+"F3.wireOp",EDGE,"E20.1.1"),sQuery(id+"F3.wireOp",EDGE,"E20.1.3"),sQuery(id+"F4.wireOp",EDGE,"E26.1.0"),sQuery(id+"F4.wireOp",EDGE,"E26.1.2"),sQuery(id+"F4.wireOp",EDGE,"E26.1.3")])]})]});
            var Q2;
            {var subQ0=sQuery(id+"F3.wireOp",EDGE,"E20.1.3");var subQ1=sQuery(id+"F3.wireOp",EDGE,"E20.1.1");var subQ2=sQuery(id+"F3.wireOp",EDGE,"E20.1.0");var subQ51=sQuery(id+"F3.wireOp",EDGE,"E18.bottom");var subQ62=sQuery(id+"F3.wireOp",EDGE,"E20.7.0");var subQ70=makeQuery(id+"F14.opLoft","CAP_FACE",FACE,{"disambiguationData":[OSD([makeQuery(id+"F3.imprint","IMPRINT",FACE,{"disambiguationData":[TD([[makeQuery(id+"F3.imprint","IMPRINT",EDGE,{"derivedFrom":subQ62}),-1.0]])]})])],"isStart":true});var subQ78=makeQuery(id+"F5.opLoft","CAP_FACE",FACE,{"disambiguationData":[OSD([makeQuery(id+"F3.imprint","IMPRINT",FACE,{"disambiguationData":[TD([[makeQuery(id+"F3.imprint","IMPRINT",EDGE,{"derivedFrom":subQ51}),1.0]])]})])],"isStart":true});Q2=makeQuery(id+"F32.boolean.opBoolean","INTERSECT",EDGE,{"derivedFrom":[makeQuery(id+"F31.boolean.opBoolean","SPLIT",FACE,{"disambiguationData":[TD([subQ70])],"derivedFrom":makeQuery(id+"F30.boolean.opBoolean","SPLIT",FACE,{"disambiguationData":[TD([subQ78])],"derivedFrom":makeQuery(id+"F29.boolean.opBoolean","SPLIT",FACE,{"disambiguationData":[TD([subQ78])],"derivedFrom":makeQuery(id+"F28.boolean.opBoolean","SPLIT",FACE,{"disambiguationData":[TD([subQ78])],"derivedFrom":makeQuery(id+"F27.boolean.opBoolean","SPLIT",FACE,{"disambiguationData":[TD([subQ78])],"derivedFrom":makeQuery(id+"F26.boolean.opBoolean","SPLIT",FACE,{"disambiguationData":[TD([subQ78])],"derivedFrom":makeQuery(id+"F25.boolean.opBoolean","SPLIT",FACE,{"disambiguationData":[TD([subQ78])],"derivedFrom":makeQuery(id+"F24.boolean.opBoolean","SPLIT",FACE,{"disambiguationData":[TD([subQ78])],"derivedFrom":makeQuery(id+"F1.opRevolve","SWEPT_FACE",FACE,{"disambiguationData":[OSD([sQuery(id+"F0.wireOp",EDGE,"E13")])]})})})})})})})})}),makeQuery(id+"F32.opLoft","SWEPT_FACE",FACE,{"disambiguationData":[OSD([subQ2,subQ1,subQ0,sQuery(id+"F22.wireOp",EDGE,"E28.9.1"),sQuery(id+"F22.wireOp",EDGE,"E28.9.2"),sQuery(id+"F22.wireOp",EDGE,"E28.9.3")])]})]});}
            var Q3;
            {var subQ0=sQuery(id+"F3.wireOp",EDGE,"E20.2.3");var subQ1=sQuery(id+"F3.wireOp",EDGE,"E20.2.1");var subQ2=sQuery(id+"F3.wireOp",EDGE,"E20.2.0");var subQ51=sQuery(id+"F3.wireOp",EDGE,"E20.7.0");var subQ60=makeQuery(id+"F14.opLoft","CAP_FACE",FACE,{"disambiguationData":[OSD([makeQuery(id+"F3.imprint","IMPRINT",FACE,{"disambiguationData":[TD([[makeQuery(id+"F3.imprint","IMPRINT",EDGE,{"derivedFrom":subQ51}),-1.0]])]})])],"isStart":true});var subQ73=sQuery(id+"F3.wireOp",EDGE,"E18.bottom");var subQ78=makeQuery(id+"F5.opLoft","CAP_FACE",FACE,{"disambiguationData":[OSD([makeQuery(id+"F3.imprint","IMPRINT",FACE,{"disambiguationData":[TD([[makeQuery(id+"F3.imprint","IMPRINT",EDGE,{"derivedFrom":subQ73}),1.0]])]})])],"isStart":true});Q3=makeQuery(id+"F33.boolean.opBoolean","INTERSECT",EDGE,{"derivedFrom":[makeQuery(id+"F32.boolean.opBoolean","SPLIT",FACE,{"disambiguationData":[TD([subQ60])],"derivedFrom":makeQuery(id+"F31.boolean.opBoolean","SPLIT",FACE,{"disambiguationData":[TD([subQ60])],"derivedFrom":makeQuery(id+"F30.boolean.opBoolean","SPLIT",FACE,{"disambiguationData":[TD([subQ78])],"derivedFrom":makeQuery(id+"F29.boolean.opBoolean","SPLIT",FACE,{"disambiguationData":[TD([subQ78])],"derivedFrom":makeQuery(id+"F28.boolean.opBoolean","SPLIT",FACE,{"disambiguationData":[TD([subQ78])],"derivedFrom":makeQuery(id+"F27.boolean.opBoolean","SPLIT",FACE,{"disambiguationData":[TD([subQ78])],"derivedFrom":makeQuery(id+"F26.boolean.opBoolean","SPLIT",FACE,{"disambiguationData":[TD([subQ78])],"derivedFrom":makeQuery(id+"F25.boolean.opBoolean","SPLIT",FACE,{"disambiguationData":[TD([subQ78])],"derivedFrom":makeQuery(id+"F24.boolean.opBoolean","SPLIT",FACE,{"disambiguationData":[TD([subQ78])],"derivedFrom":makeQuery(id+"F1.opRevolve","SWEPT_FACE",FACE,{"disambiguationData":[OSD([sQuery(id+"F0.wireOp",EDGE,"E13")])]})})})})})})})})})}),makeQuery(id+"F33.opLoft","SWEPT_FACE",FACE,{"disambiguationData":[OSD([subQ2,subQ1,subQ0,sQuery(id+"F22.wireOp",EDGE,"E28.10.1"),sQuery(id+"F22.wireOp",EDGE,"E28.10.2"),sQuery(id+"F22.wireOp",EDGE,"E28.10.3")])]})]});}
            var Q4;
            {var subQ0=sQuery(id+"F3.wireOp",EDGE,"E20.3.3");var subQ1=sQuery(id+"F3.wireOp",EDGE,"E20.3.1");var subQ2=sQuery(id+"F3.wireOp",EDGE,"E20.3.0");var subQ22=sQuery(id+"F3.wireOp",EDGE,"E20.7.0");var subQ26=makeQuery(id+"F14.opLoft","CAP_FACE",FACE,{"disambiguationData":[OSD([makeQuery(id+"F3.imprint","IMPRINT",FACE,{"disambiguationData":[TD([[makeQuery(id+"F3.imprint","IMPRINT",EDGE,{"derivedFrom":subQ22}),-1.0]])]})])],"isStart":true});var subQ73=sQuery(id+"F3.wireOp",EDGE,"E18.bottom");var subQ78=makeQuery(id+"F5.opLoft","CAP_FACE",FACE,{"disambiguationData":[OSD([makeQuery(id+"F3.imprint","IMPRINT",FACE,{"disambiguationData":[TD([[makeQuery(id+"F3.imprint","IMPRINT",EDGE,{"derivedFrom":subQ73}),1.0]])]})])],"isStart":true});Q4=makeQuery(id+"F34.boolean.opBoolean","INTERSECT",EDGE,{"derivedFrom":[makeQuery(id+"F33.boolean.opBoolean","SPLIT",FACE,{"disambiguationData":[TD([subQ26])],"derivedFrom":makeQuery(id+"F32.boolean.opBoolean","SPLIT",FACE,{"disambiguationData":[TD([subQ26])],"derivedFrom":makeQuery(id+"F31.boolean.opBoolean","SPLIT",FACE,{"disambiguationData":[TD([subQ26])],"derivedFrom":makeQuery(id+"F30.boolean.opBoolean","SPLIT",FACE,{"disambiguationData":[TD([subQ78])],"derivedFrom":makeQuery(id+"F29.boolean.opBoolean","SPLIT",FACE,{"disambiguationData":[TD([subQ78])],"derivedFrom":makeQuery(id+"F28.boolean.opBoolean","SPLIT",FACE,{"disambiguationData":[TD([subQ78])],"derivedFrom":makeQuery(id+"F27.boolean.opBoolean","SPLIT",FACE,{"disambiguationData":[TD([subQ78])],"derivedFrom":makeQuery(id+"F26.boolean.opBoolean","SPLIT",FACE,{"disambiguationData":[TD([subQ78])],"derivedFrom":makeQuery(id+"F25.boolean.opBoolean","SPLIT",FACE,{"disambiguationData":[TD([subQ78])],"derivedFrom":makeQuery(id+"F24.boolean.opBoolean","SPLIT",FACE,{"disambiguationData":[TD([subQ78])],"derivedFrom":makeQuery(id+"F1.opRevolve","SWEPT_FACE",FACE,{"disambiguationData":[OSD([sQuery(id+"F0.wireOp",EDGE,"E13")])]})})})})})})})})})})}),makeQuery(id+"F34.opLoft","SWEPT_FACE",FACE,{"disambiguationData":[OSD([subQ2,subQ1,subQ0,sQuery(id+"F22.wireOp",EDGE,"E28.11.1"),sQuery(id+"F22.wireOp",EDGE,"E28.11.2"),sQuery(id+"F22.wireOp",EDGE,"E28.11.3")])]})]});}
            var Q5;
            {var subQ0=sQuery(id+"F3.wireOp",EDGE,"E20.4.3");var subQ1=sQuery(id+"F3.wireOp",EDGE,"E20.4.1");var subQ2=sQuery(id+"F3.wireOp",EDGE,"E20.4.0");var subQ19=sQuery(id+"F3.wireOp",EDGE,"E20.7.0");var subQ23=makeQuery(id+"F14.opLoft","CAP_FACE",FACE,{"disambiguationData":[OSD([makeQuery(id+"F3.imprint","IMPRINT",FACE,{"disambiguationData":[TD([[makeQuery(id+"F3.imprint","IMPRINT",EDGE,{"derivedFrom":subQ19}),-1.0]])]})])],"isStart":true});var subQ73=sQuery(id+"F3.wireOp",EDGE,"E18.bottom");var subQ78=makeQuery(id+"F5.opLoft","CAP_FACE",FACE,{"disambiguationData":[OSD([makeQuery(id+"F3.imprint","IMPRINT",FACE,{"disambiguationData":[TD([[makeQuery(id+"F3.imprint","IMPRINT",EDGE,{"derivedFrom":subQ73}),1.0]])]})])],"isStart":true});Q5=makeQuery(id+"F35.boolean.opBoolean","INTERSECT",EDGE,{"derivedFrom":[makeQuery(id+"F34.boolean.opBoolean","SPLIT",FACE,{"disambiguationData":[TD([subQ23])],"derivedFrom":makeQuery(id+"F33.boolean.opBoolean","SPLIT",FACE,{"disambiguationData":[TD([subQ23])],"derivedFrom":makeQuery(id+"F32.boolean.opBoolean","SPLIT",FACE,{"disambiguationData":[TD([subQ23])],"derivedFrom":makeQuery(id+"F31.boolean.opBoolean","SPLIT",FACE,{"disambiguationData":[TD([subQ23])],"derivedFrom":makeQuery(id+"F30.boolean.opBoolean","SPLIT",FACE,{"disambiguationData":[TD([subQ78])],"derivedFrom":makeQuery(id+"F29.boolean.opBoolean","SPLIT",FACE,{"disambiguationData":[TD([subQ78])],"derivedFrom":makeQuery(id+"F28.boolean.opBoolean","SPLIT",FACE,{"disambiguationData":[TD([subQ78])],"derivedFrom":makeQuery(id+"F27.boolean.opBoolean","SPLIT",FACE,{"disambiguationData":[TD([subQ78])],"derivedFrom":makeQuery(id+"F26.boolean.opBoolean","SPLIT",FACE,{"disambiguationData":[TD([subQ78])],"derivedFrom":makeQuery(id+"F25.boolean.opBoolean","SPLIT",FACE,{"disambiguationData":[TD([subQ78])],"derivedFrom":makeQuery(id+"F24.boolean.opBoolean","SPLIT",FACE,{"disambiguationData":[TD([subQ78])],"derivedFrom":makeQuery(id+"F1.opRevolve","SWEPT_FACE",FACE,{"disambiguationData":[OSD([sQuery(id+"F0.wireOp",EDGE,"E13")])]})})})})})})})})})})})}),makeQuery(id+"F35.opLoft","SWEPT_FACE",FACE,{"disambiguationData":[OSD([subQ2,subQ1,subQ0,sQuery(id+"F22.wireOp",EDGE,"E28.12.1"),sQuery(id+"F22.wireOp",EDGE,"E28.12.2"),sQuery(id+"F22.wireOp",EDGE,"E28.12.3")])]})]});}
            var Q6;
            {var subQ0=sQuery(id+"F3.wireOp",EDGE,"E20.5.3");var subQ1=sQuery(id+"F3.wireOp",EDGE,"E20.5.1");var subQ2=sQuery(id+"F3.wireOp",EDGE,"E20.5.0");var subQ14=sQuery(id+"F3.wireOp",EDGE,"E20.7.0");var subQ18=makeQuery(id+"F14.opLoft","CAP_FACE",FACE,{"disambiguationData":[OSD([makeQuery(id+"F3.imprint","IMPRINT",FACE,{"disambiguationData":[TD([[makeQuery(id+"F3.imprint","IMPRINT",EDGE,{"derivedFrom":subQ14}),-1.0]])]})])],"isStart":true});var subQ73=sQuery(id+"F3.wireOp",EDGE,"E18.bottom");var subQ78=makeQuery(id+"F5.opLoft","CAP_FACE",FACE,{"disambiguationData":[OSD([makeQuery(id+"F3.imprint","IMPRINT",FACE,{"disambiguationData":[TD([[makeQuery(id+"F3.imprint","IMPRINT",EDGE,{"derivedFrom":subQ73}),1.0]])]})])],"isStart":true});Q6=makeQuery(id+"F36.boolean.opBoolean","INTERSECT",EDGE,{"derivedFrom":[makeQuery(id+"F35.boolean.opBoolean","SPLIT",FACE,{"disambiguationData":[TD([subQ18])],"derivedFrom":makeQuery(id+"F34.boolean.opBoolean","SPLIT",FACE,{"disambiguationData":[TD([subQ18])],"derivedFrom":makeQuery(id+"F33.boolean.opBoolean","SPLIT",FACE,{"disambiguationData":[TD([subQ18])],"derivedFrom":makeQuery(id+"F32.boolean.opBoolean","SPLIT",FACE,{"disambiguationData":[TD([subQ18])],"derivedFrom":makeQuery(id+"F31.boolean.opBoolean","SPLIT",FACE,{"disambiguationData":[TD([subQ18])],"derivedFrom":makeQuery(id+"F30.boolean.opBoolean","SPLIT",FACE,{"disambiguationData":[TD([subQ78])],"derivedFrom":makeQuery(id+"F29.boolean.opBoolean","SPLIT",FACE,{"disambiguationData":[TD([subQ78])],"derivedFrom":makeQuery(id+"F28.boolean.opBoolean","SPLIT",FACE,{"disambiguationData":[TD([subQ78])],"derivedFrom":makeQuery(id+"F27.boolean.opBoolean","SPLIT",FACE,{"disambiguationData":[TD([subQ78])],"derivedFrom":makeQuery(id+"F26.boolean.opBoolean","SPLIT",FACE,{"disambiguationData":[TD([subQ78])],"derivedFrom":makeQuery(id+"F25.boolean.opBoolean","SPLIT",FACE,{"disambiguationData":[TD([subQ78])],"derivedFrom":makeQuery(id+"F24.boolean.opBoolean","SPLIT",FACE,{"disambiguationData":[TD([subQ78])],"derivedFrom":makeQuery(id+"F1.opRevolve","SWEPT_FACE",FACE,{"disambiguationData":[OSD([sQuery(id+"F0.wireOp",EDGE,"E13")])]})})})})})})})})})})})})}),makeQuery(id+"F36.opLoft","SWEPT_FACE",FACE,{"disambiguationData":[OSD([subQ2,subQ1,subQ0,sQuery(id+"F22.wireOp",EDGE,"E28.13.1"),sQuery(id+"F22.wireOp",EDGE,"E28.13.2"),sQuery(id+"F22.wireOp",EDGE,"E28.13.3")])]})]});}
            var Q7;
            {var subQ0=sQuery(id+"F3.wireOp",EDGE,"E20.6.3");var subQ1=sQuery(id+"F3.wireOp",EDGE,"E20.6.1");var subQ2=sQuery(id+"F3.wireOp",EDGE,"E20.6.0");var subQ14=sQuery(id+"F3.wireOp",EDGE,"E20.7.0");var subQ18=makeQuery(id+"F14.opLoft","CAP_FACE",FACE,{"disambiguationData":[OSD([makeQuery(id+"F3.imprint","IMPRINT",FACE,{"disambiguationData":[TD([[makeQuery(id+"F3.imprint","IMPRINT",EDGE,{"derivedFrom":subQ14}),-1.0]])]})])],"isStart":true});var subQ73=sQuery(id+"F3.wireOp",EDGE,"E18.bottom");var subQ78=makeQuery(id+"F5.opLoft","CAP_FACE",FACE,{"disambiguationData":[OSD([makeQuery(id+"F3.imprint","IMPRINT",FACE,{"disambiguationData":[TD([[makeQuery(id+"F3.imprint","IMPRINT",EDGE,{"derivedFrom":subQ73}),1.0]])]})])],"isStart":true});Q7=makeQuery(id+"F37.boolean.opBoolean","INTERSECT",EDGE,{"derivedFrom":[makeQuery(id+"F36.boolean.opBoolean","SPLIT",FACE,{"disambiguationData":[TD([subQ18])],"derivedFrom":makeQuery(id+"F35.boolean.opBoolean","SPLIT",FACE,{"disambiguationData":[TD([subQ18])],"derivedFrom":makeQuery(id+"F34.boolean.opBoolean","SPLIT",FACE,{"disambiguationData":[TD([subQ18])],"derivedFrom":makeQuery(id+"F33.boolean.opBoolean","SPLIT",FACE,{"disambiguationData":[TD([subQ18])],"derivedFrom":makeQuery(id+"F32.boolean.opBoolean","SPLIT",FACE,{"disambiguationData":[TD([subQ18])],"derivedFrom":makeQuery(id+"F31.boolean.opBoolean","SPLIT",FACE,{"disambiguationData":[TD([subQ18])],"derivedFrom":makeQuery(id+"F30.boolean.opBoolean","SPLIT",FACE,{"disambiguationData":[TD([subQ78])],"derivedFrom":makeQuery(id+"F29.boolean.opBoolean","SPLIT",FACE,{"disambiguationData":[TD([subQ78])],"derivedFrom":makeQuery(id+"F28.boolean.opBoolean","SPLIT",FACE,{"disambiguationData":[TD([subQ78])],"derivedFrom":makeQuery(id+"F27.boolean.opBoolean","SPLIT",FACE,{"disambiguationData":[TD([subQ78])],"derivedFrom":makeQuery(id+"F26.boolean.opBoolean","SPLIT",FACE,{"disambiguationData":[TD([subQ78])],"derivedFrom":makeQuery(id+"F25.boolean.opBoolean","SPLIT",FACE,{"disambiguationData":[TD([subQ78])],"derivedFrom":makeQuery(id+"F24.boolean.opBoolean","SPLIT",FACE,{"disambiguationData":[TD([subQ78])],"derivedFrom":makeQuery(id+"F1.opRevolve","SWEPT_FACE",FACE,{"disambiguationData":[OSD([sQuery(id+"F0.wireOp",EDGE,"E13")])]})})})})})})})})})})})})})}),makeQuery(id+"F37.opLoft","SWEPT_FACE",FACE,{"disambiguationData":[OSD([subQ2,subQ1,subQ0,sQuery(id+"F22.wireOp",EDGE,"E28.14.1"),sQuery(id+"F22.wireOp",EDGE,"E28.14.2"),sQuery(id+"F22.wireOp",EDGE,"E28.14.3")])]})]});}
            var Q8;
            {var subQ0=sQuery(id+"F3.wireOp",EDGE,"E20.7.3");var subQ1=sQuery(id+"F3.wireOp",EDGE,"E20.7.1");var subQ2=sQuery(id+"F3.wireOp",EDGE,"E20.7.0");var subQ14=makeQuery(id+"F14.opLoft","CAP_FACE",FACE,{"disambiguationData":[OSD([makeQuery(id+"F3.imprint","IMPRINT",FACE,{"disambiguationData":[TD([[makeQuery(id+"F3.imprint","IMPRINT",EDGE,{"derivedFrom":subQ2}),-1.0]])]})])],"isStart":true});var subQ73=sQuery(id+"F3.wireOp",EDGE,"E18.bottom");var subQ78=makeQuery(id+"F5.opLoft","CAP_FACE",FACE,{"disambiguationData":[OSD([makeQuery(id+"F3.imprint","IMPRINT",FACE,{"disambiguationData":[TD([[makeQuery(id+"F3.imprint","IMPRINT",EDGE,{"derivedFrom":subQ73}),1.0]])]})])],"isStart":true});Q8=makeQuery(id+"F38.boolean.opBoolean","INTERSECT",EDGE,{"derivedFrom":[makeQuery(id+"F37.boolean.opBoolean","SPLIT",FACE,{"disambiguationData":[TD([subQ14])],"derivedFrom":makeQuery(id+"F36.boolean.opBoolean","SPLIT",FACE,{"disambiguationData":[TD([subQ14])],"derivedFrom":makeQuery(id+"F35.boolean.opBoolean","SPLIT",FACE,{"disambiguationData":[TD([subQ14])],"derivedFrom":makeQuery(id+"F34.boolean.opBoolean","SPLIT",FACE,{"disambiguationData":[TD([subQ14])],"derivedFrom":makeQuery(id+"F33.boolean.opBoolean","SPLIT",FACE,{"disambiguationData":[TD([subQ14])],"derivedFrom":makeQuery(id+"F32.boolean.opBoolean","SPLIT",FACE,{"disambiguationData":[TD([subQ14])],"derivedFrom":makeQuery(id+"F31.boolean.opBoolean","SPLIT",FACE,{"disambiguationData":[TD([subQ14])],"derivedFrom":makeQuery(id+"F30.boolean.opBoolean","SPLIT",FACE,{"disambiguationData":[TD([subQ78])],"derivedFrom":makeQuery(id+"F29.boolean.opBoolean","SPLIT",FACE,{"disambiguationData":[TD([subQ78])],"derivedFrom":makeQuery(id+"F28.boolean.opBoolean","SPLIT",FACE,{"disambiguationData":[TD([subQ78])],"derivedFrom":makeQuery(id+"F27.boolean.opBoolean","SPLIT",FACE,{"disambiguationData":[TD([subQ78])],"derivedFrom":makeQuery(id+"F26.boolean.opBoolean","SPLIT",FACE,{"disambiguationData":[TD([subQ78])],"derivedFrom":makeQuery(id+"F25.boolean.opBoolean","SPLIT",FACE,{"disambiguationData":[TD([subQ78])],"derivedFrom":makeQuery(id+"F24.boolean.opBoolean","SPLIT",FACE,{"disambiguationData":[TD([subQ78])],"derivedFrom":makeQuery(id+"F1.opRevolve","SWEPT_FACE",FACE,{"disambiguationData":[OSD([sQuery(id+"F0.wireOp",EDGE,"E13")])]})})})})})})})})})})})})})})}),makeQuery(id+"F38.opLoft","SWEPT_FACE",FACE,{"disambiguationData":[OSD([subQ2,subQ1,subQ0,sQuery(id+"F22.wireOp",EDGE,"E28.15.1"),sQuery(id+"F22.wireOp",EDGE,"E28.15.2"),sQuery(id+"F22.wireOp",EDGE,"E28.15.3")])]})]});}
            var Q9;
            Q9=makeQuery(id+"F23.boolean.opBoolean","INTERSECT",EDGE,{"derivedFrom":[makeQuery(id+"F1.opRevolve","SWEPT_FACE",FACE,{"disambiguationData":[OSD([sQuery(id+"F0.wireOp",EDGE,"E13")])]}),makeQuery(id+"F23.opLoft","SWEPT_FACE",FACE,{"disambiguationData":[OSD([sQuery(id+"F3.wireOp",EDGE,"E20.8.0"),sQuery(id+"F3.wireOp",EDGE,"E20.8.1"),sQuery(id+"F3.wireOp",EDGE,"E20.8.3"),sQuery(id+"F22.wireOp",EDGE,"E27.bottom"),sQuery(id+"F22.wireOp",EDGE,"E27.top"),sQuery(id+"F22.wireOp",EDGE,"E27.right")])]})]});
            var Q10;
            Q10=makeQuery(id+"F24.boolean.opBoolean","INTERSECT",EDGE,{"derivedFrom":[makeQuery(id+"F1.opRevolve","SWEPT_FACE",FACE,{"disambiguationData":[OSD([sQuery(id+"F0.wireOp",EDGE,"E13")])]}),makeQuery(id+"F24.opLoft","SWEPT_FACE",FACE,{"disambiguationData":[OSD([sQuery(id+"F3.wireOp",EDGE,"E20.9.0"),sQuery(id+"F3.wireOp",EDGE,"E20.9.1"),sQuery(id+"F3.wireOp",EDGE,"E20.9.3"),sQuery(id+"F22.wireOp",EDGE,"E28.1.1"),sQuery(id+"F22.wireOp",EDGE,"E28.1.2"),sQuery(id+"F22.wireOp",EDGE,"E28.1.3")])]})]});
            var Q11;
            {var subQ0=sQuery(id+"F3.wireOp",EDGE,"E20.10.3");var subQ1=sQuery(id+"F3.wireOp",EDGE,"E20.10.1");var subQ2=sQuery(id+"F3.wireOp",EDGE,"E20.10.0");var subQ81=sQuery(id+"F3.wireOp",EDGE,"E18.bottom");Q11=makeQuery(id+"F25.boolean.opBoolean","INTERSECT",EDGE,{"derivedFrom":[makeQuery(id+"F24.boolean.opBoolean","SPLIT",FACE,{"disambiguationData":[TD([makeQuery(id+"F5.opLoft","CAP_FACE",FACE,{"disambiguationData":[OSD([makeQuery(id+"F3.imprint","IMPRINT",FACE,{"disambiguationData":[TD([[makeQuery(id+"F3.imprint","IMPRINT",EDGE,{"derivedFrom":subQ81}),1.0]])]})])],"isStart":true})])],"derivedFrom":makeQuery(id+"F1.opRevolve","SWEPT_FACE",FACE,{"disambiguationData":[OSD([sQuery(id+"F0.wireOp",EDGE,"E13")])]})}),makeQuery(id+"F25.opLoft","SWEPT_FACE",FACE,{"disambiguationData":[OSD([subQ2,subQ1,subQ0,sQuery(id+"F22.wireOp",EDGE,"E28.2.1"),sQuery(id+"F22.wireOp",EDGE,"E28.2.2"),sQuery(id+"F22.wireOp",EDGE,"E28.2.3")])]})]});}
            var Q12;
            {var subQ0=sQuery(id+"F3.wireOp",EDGE,"E20.11.3");var subQ1=sQuery(id+"F3.wireOp",EDGE,"E20.11.1");var subQ2=sQuery(id+"F3.wireOp",EDGE,"E20.11.0");var subQ74=sQuery(id+"F3.wireOp",EDGE,"E18.bottom");var subQ77=makeQuery(id+"F5.opLoft","CAP_FACE",FACE,{"disambiguationData":[OSD([makeQuery(id+"F3.imprint","IMPRINT",FACE,{"disambiguationData":[TD([[makeQuery(id+"F3.imprint","IMPRINT",EDGE,{"derivedFrom":subQ74}),1.0]])]})])],"isStart":true});Q12=makeQuery(id+"F26.boolean.opBoolean","INTERSECT",EDGE,{"derivedFrom":[makeQuery(id+"F25.boolean.opBoolean","SPLIT",FACE,{"disambiguationData":[TD([subQ77])],"derivedFrom":makeQuery(id+"F24.boolean.opBoolean","SPLIT",FACE,{"disambiguationData":[TD([subQ77])],"derivedFrom":makeQuery(id+"F1.opRevolve","SWEPT_FACE",FACE,{"disambiguationData":[OSD([sQuery(id+"F0.wireOp",EDGE,"E13")])]})})}),makeQuery(id+"F26.opLoft","SWEPT_FACE",FACE,{"disambiguationData":[OSD([subQ2,subQ1,subQ0,sQuery(id+"F22.wireOp",EDGE,"E28.3.1"),sQuery(id+"F22.wireOp",EDGE,"E28.3.2"),sQuery(id+"F22.wireOp",EDGE,"E28.3.3")])]})]});}
            var Q13;
            {var subQ0=sQuery(id+"F3.wireOp",EDGE,"E20.12.3");var subQ1=sQuery(id+"F3.wireOp",EDGE,"E20.12.1");var subQ2=sQuery(id+"F3.wireOp",EDGE,"E20.12.0");var subQ70=sQuery(id+"F3.wireOp",EDGE,"E18.bottom");var subQ73=makeQuery(id+"F5.opLoft","CAP_FACE",FACE,{"disambiguationData":[OSD([makeQuery(id+"F3.imprint","IMPRINT",FACE,{"disambiguationData":[TD([[makeQuery(id+"F3.imprint","IMPRINT",EDGE,{"derivedFrom":subQ70}),1.0]])]})])],"isStart":true});Q13=makeQuery(id+"F27.boolean.opBoolean","INTERSECT",EDGE,{"derivedFrom":[makeQuery(id+"F26.boolean.opBoolean","SPLIT",FACE,{"disambiguationData":[TD([subQ73])],"derivedFrom":makeQuery(id+"F25.boolean.opBoolean","SPLIT",FACE,{"disambiguationData":[TD([subQ73])],"derivedFrom":makeQuery(id+"F24.boolean.opBoolean","SPLIT",FACE,{"disambiguationData":[TD([subQ73])],"derivedFrom":makeQuery(id+"F1.opRevolve","SWEPT_FACE",FACE,{"disambiguationData":[OSD([sQuery(id+"F0.wireOp",EDGE,"E13")])]})})})}),makeQuery(id+"F27.opLoft","SWEPT_FACE",FACE,{"disambiguationData":[OSD([subQ2,subQ1,subQ0,sQuery(id+"F22.wireOp",EDGE,"E28.4.1"),sQuery(id+"F22.wireOp",EDGE,"E28.4.2"),sQuery(id+"F22.wireOp",EDGE,"E28.4.3")])]})]});}
            var Q14;
            {var subQ0=sQuery(id+"F3.wireOp",EDGE,"E20.13.3");var subQ1=sQuery(id+"F3.wireOp",EDGE,"E20.13.1");var subQ2=sQuery(id+"F3.wireOp",EDGE,"E20.13.0");var subQ52=sQuery(id+"F3.wireOp",EDGE,"E18.bottom");var subQ55=makeQuery(id+"F5.opLoft","CAP_FACE",FACE,{"disambiguationData":[OSD([makeQuery(id+"F3.imprint","IMPRINT",FACE,{"disambiguationData":[TD([[makeQuery(id+"F3.imprint","IMPRINT",EDGE,{"derivedFrom":subQ52}),1.0]])]})])],"isStart":true});Q14=makeQuery(id+"F28.boolean.opBoolean","INTERSECT",EDGE,{"derivedFrom":[makeQuery(id+"F27.boolean.opBoolean","SPLIT",FACE,{"disambiguationData":[TD([subQ55])],"derivedFrom":makeQuery(id+"F26.boolean.opBoolean","SPLIT",FACE,{"disambiguationData":[TD([subQ55])],"derivedFrom":makeQuery(id+"F25.boolean.opBoolean","SPLIT",FACE,{"disambiguationData":[TD([subQ55])],"derivedFrom":makeQuery(id+"F24.boolean.opBoolean","SPLIT",FACE,{"disambiguationData":[TD([subQ55])],"derivedFrom":makeQuery(id+"F1.opRevolve","SWEPT_FACE",FACE,{"disambiguationData":[OSD([sQuery(id+"F0.wireOp",EDGE,"E13")])]})})})})}),makeQuery(id+"F28.opLoft","SWEPT_FACE",FACE,{"disambiguationData":[OSD([subQ2,subQ1,subQ0,sQuery(id+"F22.wireOp",EDGE,"E28.5.1"),sQuery(id+"F22.wireOp",EDGE,"E28.5.2"),sQuery(id+"F22.wireOp",EDGE,"E28.5.3")])]})]});}
            var Q15;
            {var subQ0=sQuery(id+"F3.wireOp",EDGE,"E20.14.3");var subQ1=sQuery(id+"F3.wireOp",EDGE,"E20.14.1");var subQ2=sQuery(id+"F3.wireOp",EDGE,"E20.14.0");var subQ41=sQuery(id+"F3.wireOp",EDGE,"E18.bottom");var subQ44=makeQuery(id+"F5.opLoft","CAP_FACE",FACE,{"disambiguationData":[OSD([makeQuery(id+"F3.imprint","IMPRINT",FACE,{"disambiguationData":[TD([[makeQuery(id+"F3.imprint","IMPRINT",EDGE,{"derivedFrom":subQ41}),1.0]])]})])],"isStart":true});Q15=makeQuery(id+"F29.boolean.opBoolean","INTERSECT",EDGE,{"derivedFrom":[makeQuery(id+"F28.boolean.opBoolean","SPLIT",FACE,{"disambiguationData":[TD([subQ44])],"derivedFrom":makeQuery(id+"F27.boolean.opBoolean","SPLIT",FACE,{"disambiguationData":[TD([subQ44])],"derivedFrom":makeQuery(id+"F26.boolean.opBoolean","SPLIT",FACE,{"disambiguationData":[TD([subQ44])],"derivedFrom":makeQuery(id+"F25.boolean.opBoolean","SPLIT",FACE,{"disambiguationData":[TD([subQ44])],"derivedFrom":makeQuery(id+"F24.boolean.opBoolean","SPLIT",FACE,{"disambiguationData":[TD([subQ44])],"derivedFrom":makeQuery(id+"F1.opRevolve","SWEPT_FACE",FACE,{"disambiguationData":[OSD([sQuery(id+"F0.wireOp",EDGE,"E13")])]})})})})})}),makeQuery(id+"F29.opLoft","SWEPT_FACE",FACE,{"disambiguationData":[OSD([subQ2,subQ1,subQ0,sQuery(id+"F22.wireOp",EDGE,"E28.6.1"),sQuery(id+"F22.wireOp",EDGE,"E28.6.2"),sQuery(id+"F22.wireOp",EDGE,"E28.6.3")])]})]});}
            var Q16;
            {var subQ0=sQuery(id+"F3.wireOp",EDGE,"E20.15.3");var subQ1=sQuery(id+"F3.wireOp",EDGE,"E20.15.1");var subQ2=sQuery(id+"F3.wireOp",EDGE,"E20.15.0");var subQ34=sQuery(id+"F3.wireOp",EDGE,"E18.bottom");var subQ37=makeQuery(id+"F5.opLoft","CAP_FACE",FACE,{"disambiguationData":[OSD([makeQuery(id+"F3.imprint","IMPRINT",FACE,{"disambiguationData":[TD([[makeQuery(id+"F3.imprint","IMPRINT",EDGE,{"derivedFrom":subQ34}),1.0]])]})])],"isStart":true});Q16=makeQuery(id+"F30.boolean.opBoolean","INTERSECT",EDGE,{"derivedFrom":[makeQuery(id+"F29.boolean.opBoolean","SPLIT",FACE,{"disambiguationData":[TD([subQ37])],"derivedFrom":makeQuery(id+"F28.boolean.opBoolean","SPLIT",FACE,{"disambiguationData":[TD([subQ37])],"derivedFrom":makeQuery(id+"F27.boolean.opBoolean","SPLIT",FACE,{"disambiguationData":[TD([subQ37])],"derivedFrom":makeQuery(id+"F26.boolean.opBoolean","SPLIT",FACE,{"disambiguationData":[TD([subQ37])],"derivedFrom":makeQuery(id+"F25.boolean.opBoolean","SPLIT",FACE,{"disambiguationData":[TD([subQ37])],"derivedFrom":makeQuery(id+"F24.boolean.opBoolean","SPLIT",FACE,{"disambiguationData":[TD([subQ37])],"derivedFrom":makeQuery(id+"F1.opRevolve","SWEPT_FACE",FACE,{"disambiguationData":[OSD([sQuery(id+"F0.wireOp",EDGE,"E13")])]})})})})})})}),makeQuery(id+"F30.opLoft","SWEPT_FACE",FACE,{"disambiguationData":[OSD([subQ2,subQ1,subQ0,sQuery(id+"F22.wireOp",EDGE,"E28.7.1"),sQuery(id+"F22.wireOp",EDGE,"E28.7.2"),sQuery(id+"F22.wireOp",EDGE,"E28.7.3")])]})]});}
            var Q17;
            {var subQ0=sQuery(id+"F3.wireOp",EDGE,"E18.left");var subQ1=sQuery(id+"F3.wireOp",EDGE,"E18.top");var subQ2=sQuery(id+"F3.wireOp",EDGE,"E18.bottom");var subQ48=makeQuery(id+"F5.opLoft","CAP_FACE",FACE,{"disambiguationData":[OSD([makeQuery(id+"F3.imprint","IMPRINT",FACE,{"disambiguationData":[TD([[makeQuery(id+"F3.imprint","IMPRINT",EDGE,{"derivedFrom":subQ2}),1.0]])]})])],"isStart":true});Q17=makeQuery(id+"F31.boolean.opBoolean","INTERSECT",EDGE,{"derivedFrom":[makeQuery(id+"F30.boolean.opBoolean","SPLIT",FACE,{"disambiguationData":[TD([subQ48])],"derivedFrom":makeQuery(id+"F29.boolean.opBoolean","SPLIT",FACE,{"disambiguationData":[TD([subQ48])],"derivedFrom":makeQuery(id+"F28.boolean.opBoolean","SPLIT",FACE,{"disambiguationData":[TD([subQ48])],"derivedFrom":makeQuery(id+"F27.boolean.opBoolean","SPLIT",FACE,{"disambiguationData":[TD([subQ48])],"derivedFrom":makeQuery(id+"F26.boolean.opBoolean","SPLIT",FACE,{"disambiguationData":[TD([subQ48])],"derivedFrom":makeQuery(id+"F25.boolean.opBoolean","SPLIT",FACE,{"disambiguationData":[TD([subQ48])],"derivedFrom":makeQuery(id+"F24.boolean.opBoolean","SPLIT",FACE,{"disambiguationData":[TD([subQ48])],"derivedFrom":makeQuery(id+"F1.opRevolve","SWEPT_FACE",FACE,{"disambiguationData":[OSD([sQuery(id+"F0.wireOp",EDGE,"E13")])]})})})})})})})}),makeQuery(id+"F31.opLoft","SWEPT_FACE",FACE,{"disambiguationData":[OSD([subQ2,subQ1,subQ0,sQuery(id+"F22.wireOp",EDGE,"E28.8.1"),sQuery(id+"F22.wireOp",EDGE,"E28.8.2"),sQuery(id+"F22.wireOp",EDGE,"E28.8.3")])]})]});}
            var Q18;
            Q18=makeQuery(id+"F5.boolean.opBoolean","INTERSECT",EDGE,{"derivedFrom":[makeQuery(id+"F1.opRevolve","SWEPT_FACE",FACE,{"disambiguationData":[OSD([sQuery(id+"F0.wireOp",EDGE,"E13")])]}),makeQuery(id+"F5.opLoft","SWEPT_FACE",FACE,{"disambiguationData":[OSD([sQuery(id+"F3.wireOp",EDGE,"E18.bottom"),sQuery(id+"F3.wireOp",EDGE,"E18.top"),sQuery(id+"F3.wireOp",EDGE,"E18.left"),sQuery(id+"F4.wireOp",EDGE,"E21"),sQuery(id+"F4.wireOp",EDGE,"E22"),sQuery(id+"F4.wireOp",EDGE,"E23")])]})]});
            var Q19;
            Q19=makeQuery(id+"F6.boolean.opBoolean","INTERSECT",EDGE,{"derivedFrom":[makeQuery(id+"F1.opRevolve","SWEPT_FACE",FACE,{"disambiguationData":[OSD([sQuery(id+"F0.wireOp",EDGE,"E13")])]}),makeQuery(id+"F6.opLoft","SWEPT_FACE",FACE,{"disambiguationData":[OSD([sQuery(id+"F3.wireOp",EDGE,"E20.15.0"),sQuery(id+"F3.wireOp",EDGE,"E20.15.1"),sQuery(id+"F3.wireOp",EDGE,"E20.15.3"),sQuery(id+"F4.wireOp",EDGE,"E26.15.0"),sQuery(id+"F4.wireOp",EDGE,"E26.15.2"),sQuery(id+"F4.wireOp",EDGE,"E26.15.3")])]})]});
            var Q20;
            Q20=makeQuery(id+"F7.boolean.opBoolean","INTERSECT",EDGE,{"derivedFrom":[makeQuery(id+"F1.opRevolve","SWEPT_FACE",FACE,{"disambiguationData":[OSD([sQuery(id+"F0.wireOp",EDGE,"E13")])]}),makeQuery(id+"F7.opLoft","SWEPT_FACE",FACE,{"disambiguationData":[OSD([sQuery(id+"F3.wireOp",EDGE,"E20.14.0"),sQuery(id+"F3.wireOp",EDGE,"E20.14.1"),sQuery(id+"F3.wireOp",EDGE,"E20.14.3"),sQuery(id+"F4.wireOp",EDGE,"E26.14.0"),sQuery(id+"F4.wireOp",EDGE,"E26.14.2"),sQuery(id+"F4.wireOp",EDGE,"E26.14.3")])]})]});
            var Q21;
            Q21=makeQuery(id+"F8.boolean.opBoolean","INTERSECT",EDGE,{"derivedFrom":[makeQuery(id+"F1.opRevolve","SWEPT_FACE",FACE,{"disambiguationData":[OSD([sQuery(id+"F0.wireOp",EDGE,"E13")])]}),makeQuery(id+"F8.opLoft","SWEPT_FACE",FACE,{"disambiguationData":[OSD([sQuery(id+"F3.wireOp",EDGE,"E20.13.0"),sQuery(id+"F3.wireOp",EDGE,"E20.13.1"),sQuery(id+"F3.wireOp",EDGE,"E20.13.3"),sQuery(id+"F4.wireOp",EDGE,"E26.13.0"),sQuery(id+"F4.wireOp",EDGE,"E26.13.2"),sQuery(id+"F4.wireOp",EDGE,"E26.13.3")])]})]});
            var Q22;
            Q22=makeQuery(id+"F9.boolean.opBoolean","INTERSECT",EDGE,{"derivedFrom":[makeQuery(id+"F1.opRevolve","SWEPT_FACE",FACE,{"disambiguationData":[OSD([sQuery(id+"F0.wireOp",EDGE,"E13")])]}),makeQuery(id+"F9.opLoft","SWEPT_FACE",FACE,{"disambiguationData":[OSD([sQuery(id+"F3.wireOp",EDGE,"E20.12.0"),sQuery(id+"F3.wireOp",EDGE,"E20.12.1"),sQuery(id+"F3.wireOp",EDGE,"E20.12.3"),sQuery(id+"F4.wireOp",EDGE,"E26.12.0"),sQuery(id+"F4.wireOp",EDGE,"E26.12.2"),sQuery(id+"F4.wireOp",EDGE,"E26.12.3")])]})]});
            var Q23;
            Q23=makeQuery(id+"F10.boolean.opBoolean","INTERSECT",EDGE,{"derivedFrom":[makeQuery(id+"F1.opRevolve","SWEPT_FACE",FACE,{"disambiguationData":[OSD([sQuery(id+"F0.wireOp",EDGE,"E13")])]}),makeQuery(id+"F10.opLoft","SWEPT_FACE",FACE,{"disambiguationData":[OSD([sQuery(id+"F3.wireOp",EDGE,"E20.11.0"),sQuery(id+"F3.wireOp",EDGE,"E20.11.1"),sQuery(id+"F3.wireOp",EDGE,"E20.11.3"),sQuery(id+"F4.wireOp",EDGE,"E26.11.0"),sQuery(id+"F4.wireOp",EDGE,"E26.11.2"),sQuery(id+"F4.wireOp",EDGE,"E26.11.3")])]})]});
            var Q24;
            Q24=makeQuery(id+"F11.boolean.opBoolean","INTERSECT",EDGE,{"derivedFrom":[makeQuery(id+"F1.opRevolve","SWEPT_FACE",FACE,{"disambiguationData":[OSD([sQuery(id+"F0.wireOp",EDGE,"E13")])]}),makeQuery(id+"F11.opLoft","SWEPT_FACE",FACE,{"disambiguationData":[OSD([sQuery(id+"F3.wireOp",EDGE,"E20.10.0"),sQuery(id+"F3.wireOp",EDGE,"E20.10.1"),sQuery(id+"F3.wireOp",EDGE,"E20.10.3"),sQuery(id+"F4.wireOp",EDGE,"E26.10.0"),sQuery(id+"F4.wireOp",EDGE,"E26.10.2"),sQuery(id+"F4.wireOp",EDGE,"E26.10.3")])]})]});
            var Q25;
            Q25=makeQuery(id+"F12.boolean.opBoolean","INTERSECT",EDGE,{"derivedFrom":[makeQuery(id+"F1.opRevolve","SWEPT_FACE",FACE,{"disambiguationData":[OSD([sQuery(id+"F0.wireOp",EDGE,"E13")])]}),makeQuery(id+"F12.opLoft","SWEPT_FACE",FACE,{"disambiguationData":[OSD([sQuery(id+"F3.wireOp",EDGE,"E20.9.0"),sQuery(id+"F3.wireOp",EDGE,"E20.9.1"),sQuery(id+"F3.wireOp",EDGE,"E20.9.3"),sQuery(id+"F4.wireOp",EDGE,"E26.9.0"),sQuery(id+"F4.wireOp",EDGE,"E26.9.2"),sQuery(id+"F4.wireOp",EDGE,"E26.9.3")])]})]});
            var Q26;
            Q26=makeQuery(id+"F13.boolean.opBoolean","INTERSECT",EDGE,{"derivedFrom":[makeQuery(id+"F1.opRevolve","SWEPT_FACE",FACE,{"disambiguationData":[OSD([sQuery(id+"F0.wireOp",EDGE,"E13")])]}),makeQuery(id+"F13.opLoft","SWEPT_FACE",FACE,{"disambiguationData":[OSD([sQuery(id+"F3.wireOp",EDGE,"E20.8.0"),sQuery(id+"F3.wireOp",EDGE,"E20.8.1"),sQuery(id+"F3.wireOp",EDGE,"E20.8.3"),sQuery(id+"F4.wireOp",EDGE,"E26.8.0"),sQuery(id+"F4.wireOp",EDGE,"E26.8.2"),sQuery(id+"F4.wireOp",EDGE,"E26.8.3")])]})]});
            var Q27;
            Q27=makeQuery(id+"F14.boolean.opBoolean","INTERSECT",EDGE,{"derivedFrom":[makeQuery(id+"F1.opRevolve","SWEPT_FACE",FACE,{"disambiguationData":[OSD([sQuery(id+"F0.wireOp",EDGE,"E13")])]}),makeQuery(id+"F14.opLoft","SWEPT_FACE",FACE,{"disambiguationData":[OSD([sQuery(id+"F3.wireOp",EDGE,"E20.7.0"),sQuery(id+"F3.wireOp",EDGE,"E20.7.1"),sQuery(id+"F3.wireOp",EDGE,"E20.7.3"),sQuery(id+"F4.wireOp",EDGE,"E26.7.0"),sQuery(id+"F4.wireOp",EDGE,"E26.7.2"),sQuery(id+"F4.wireOp",EDGE,"E26.7.3")])]})]});
            var Q28;
            Q28=makeQuery(id+"F15.boolean.opBoolean","INTERSECT",EDGE,{"derivedFrom":[makeQuery(id+"F1.opRevolve","SWEPT_FACE",FACE,{"disambiguationData":[OSD([sQuery(id+"F0.wireOp",EDGE,"E13")])]}),makeQuery(id+"F15.opLoft","SWEPT_FACE",FACE,{"disambiguationData":[OSD([sQuery(id+"F3.wireOp",EDGE,"E20.6.0"),sQuery(id+"F3.wireOp",EDGE,"E20.6.1"),sQuery(id+"F3.wireOp",EDGE,"E20.6.3"),sQuery(id+"F4.wireOp",EDGE,"E26.6.0"),sQuery(id+"F4.wireOp",EDGE,"E26.6.2"),sQuery(id+"F4.wireOp",EDGE,"E26.6.3")])]})]});
            var Q29;
            Q29=makeQuery(id+"F16.boolean.opBoolean","INTERSECT",EDGE,{"derivedFrom":[makeQuery(id+"F1.opRevolve","SWEPT_FACE",FACE,{"disambiguationData":[OSD([sQuery(id+"F0.wireOp",EDGE,"E13")])]}),makeQuery(id+"F16.opLoft","SWEPT_FACE",FACE,{"disambiguationData":[OSD([sQuery(id+"F3.wireOp",EDGE,"E20.5.0"),sQuery(id+"F3.wireOp",EDGE,"E20.5.1"),sQuery(id+"F3.wireOp",EDGE,"E20.5.3"),sQuery(id+"F4.wireOp",EDGE,"E26.5.0"),sQuery(id+"F4.wireOp",EDGE,"E26.5.2"),sQuery(id+"F4.wireOp",EDGE,"E26.5.3")])]})]});
            var Q30;
            Q30=makeQuery(id+"F17.boolean.opBoolean","INTERSECT",EDGE,{"derivedFrom":[makeQuery(id+"F1.opRevolve","SWEPT_FACE",FACE,{"disambiguationData":[OSD([sQuery(id+"F0.wireOp",EDGE,"E13")])]}),makeQuery(id+"F17.opLoft","SWEPT_FACE",FACE,{"disambiguationData":[OSD([sQuery(id+"F3.wireOp",EDGE,"E20.4.0"),sQuery(id+"F3.wireOp",EDGE,"E20.4.1"),sQuery(id+"F3.wireOp",EDGE,"E20.4.3"),sQuery(id+"F4.wireOp",EDGE,"E26.4.0"),sQuery(id+"F4.wireOp",EDGE,"E26.4.2"),sQuery(id+"F4.wireOp",EDGE,"E26.4.3")])]})]});
            var Q31;
            Q31=makeQuery(id+"F18.boolean.opBoolean","INTERSECT",EDGE,{"derivedFrom":[makeQuery(id+"F1.opRevolve","SWEPT_FACE",FACE,{"disambiguationData":[OSD([sQuery(id+"F0.wireOp",EDGE,"E13")])]}),makeQuery(id+"F18.opLoft","SWEPT_FACE",FACE,{"disambiguationData":[OSD([sQuery(id+"F3.wireOp",EDGE,"E20.3.0"),sQuery(id+"F3.wireOp",EDGE,"E20.3.1"),sQuery(id+"F3.wireOp",EDGE,"E20.3.3"),sQuery(id+"F4.wireOp",EDGE,"E26.3.0"),sQuery(id+"F4.wireOp",EDGE,"E26.3.2"),sQuery(id+"F4.wireOp",EDGE,"E26.3.3")])]})]});
            fillet(context, id + "F46", {"entities" : qUnion([Q0, Q1, Q2, Q3, Q4, Q5, Q6, Q7, Q8, Q9, Q10, Q11, Q12, Q13, Q14, Q15, Q16, Q17, Q18, Q19, Q20, Q21, Q22, Q23, Q24, Q25, Q26, Q27, Q28, Q29, Q30, Q31]), "radius" : 1.5 * mm, "tangentPropagation" : true, "allowEdgeOverflow" : false});
        }
        {
            var Q0;
            Q0=makeQuery(id+"F1.opRevolve","SWEPT_EDGE",EDGE,{"disambiguationData":[OSD([sQuery(id+"F0.wireOp",EDGE,"E0"),sQuery(id+"F0.wireOp",EDGE,"E14")])]});
            var Q1;
            Q1=makeQuery(id+"F1.opRevolve","SWEPT_EDGE",EDGE,{"disambiguationData":[OSD([sQuery(id+"F0.wireOp",EDGE,"E7"),sQuery(id+"F0.wireOp",EDGE,"E15")])]});
            chamfer(context, id + "F47", {"entities" : qUnion([Q0, Q1]), "width" : 1 * mm, "tangentPropagation" : true});
        }
    });
